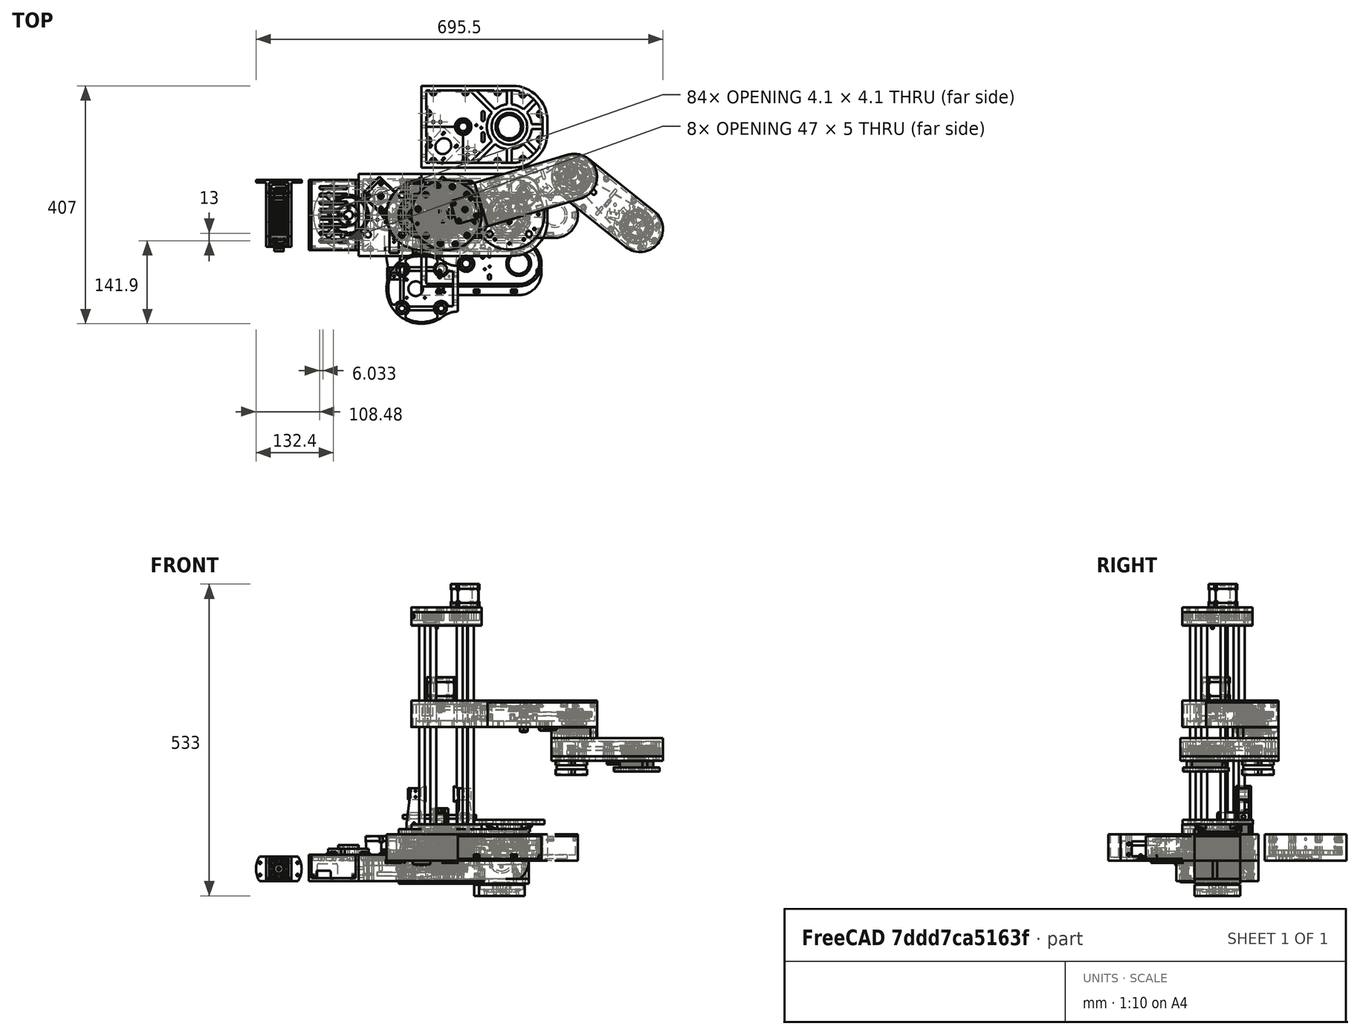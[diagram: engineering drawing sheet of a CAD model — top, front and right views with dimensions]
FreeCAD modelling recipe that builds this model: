
FCSTD DOCUMENT  (FreeCAD 0.20R28717 (Git))
Label: SCARARobot
License: All rights reserved
LicenseURL: http://en.wikipedia.org/wiki/All_rights_reserved
objects: Part::Feature×123, Sketcher::SketchObject×110, PartDesign::Pocket×76, PartDesign::Pad×44, Part::Part2DObjectPython×22, PartDesign::Body×22, Part::FeaturePython×17, App::Part×16, PartDesign::PolarPattern×9, Spreadsheet::Sheet×8, PartDesign::LinearPattern×6, TechDraw::DrawViewDimension×6, PartDesign::FeatureBase×5, Part::Mirroring×5, PartDesign::Hole×5, PartDesign::Chamfer×4, PartDesign::FeaturePython×3, Part::Cylinder×2, Part::Box×2, PartDesign::Line×2, +10 more types
note: 601 computed .brp shape members not serialized (recipe doc carries the construction recipe); baked Part::Feature solids carry a one-line shape summary decoded from their .brp

FEATURE [Part::Feature] Part__Feature059  label="Servo Motor MG996R 3D Model_Servo Motor MG996R 3D Model"
  Placement = pos=(-0.337733,-44.2936,-36.6383) rot=(0.57735,-0.57735,-0.57735;2.0944rad)
  shape: bbox 22.19 x 55.8 x 45.2 mm, 123 faces, 4 solids (baked)
FEATURE [Spreadsheet::Sheet] Spreadsheet  label="gripperdims"
  cells = A1=MG996R; B2=height; C2(mg996r_height)==40.3mm; E2=slide thickness; F2(mg996r_slide_thickness)==1.5mm; B3=width; C3(mg996r_width)==20mm; E3=slide length; F3(mg996r_slide_length)==6mm; B4=hole distance; C4(mg996r_holedistance)==3.5mm; E4=slide depth; F4(mg996r_slide_depth)==1.5mm; B5=hole separation; C5(mg996r_holeseparation)==10mm; B6=hole diameter; C6(mg996r_holediameter)==3.2mm; B7=extra depth; C7(mg996r_extra_depth)==3mm; B8=center height; C8(mg996r_center_height)==1.5mm; B9=center length; C9(mg996r_center_length)==7mm; B10=center thickness; C10(mg996r_center_thickness)==1.5mm; A11=Servo Holder; B12=moving hole; C12(servo_holder_moving_hole_diameter)==3.4mm; B13=width; C13(servo_holder_width)==30mm; B14=height; C14(servo_holder_height)==72.5mm; B15=top skirt; C15(servo_holder_top_skirt)==24.75mm; B16=bottom skirt; C16(servo_holder_bottom_skirt)==20mm; B17=thickness; C17(servo_holder_thickness)==6mm; B18=rod diameter; C18(servo_holder_roddiameter)==6mm; B19=rod casing; C19(servo_holder_rodcasing)==17.5mm; B20=rod casing layer; C20(servo_holder_rodcasing_layer)==5mm; B21=rod casing cutin; C21(servo_holder_rodcasing_cutin)==9mm; B22=rod casing overhang; C22(servo_holder_rodcasing_overhang)==2.5mm; B23=hole top distance; C23(servo_holder_hole_top_distance)==4.7mm; B24=hole side distance; C24(servo_holder_hole_side_distance)==5.5mm; B25=axis distance; C25(servo_holder_axis_distance)==46mm; B26=axis top offset; C26(servo_holder_axis_top_offset)==12mm; B27=side wings; C27(servo_holder_side_wings)==7mm; B28=side wing thickness; C28(servo_holder_side_wing_thickness)==4.5mm; A29=Servo cover; B29=cover thickness; C29(cover_thickness)==2.5mm; B30=cover height; C30(cover_height)==12.5mm; A31=Rod; B31=length; C31(rod_length)==125mm; A32=Slider; B32=height; C32(slider_height)==18mm; B33=width; C33(slider_width)==16mm; B34=length; C34(slider_length)==60mm; B35=handholes distance; C35(slider_handholes_distance)==22mm; B36=slider margin; C36(slider_margin)==0.4mm; B37=connector length; C37(slider_connector_length)==14mm; B38=connector thickness; C38(slider_connector_thickness)==4mm; B39=connector depth; C39(slider_connector_depth)==10mm; B40=connector foot; C40(slider_connector_foot)==9mm; B41=connector foot thickness; C41(slider_connector_foot_thickness)==3.5mm; A42=Hand; B42=height; C42(hand_height)==105mm; B43=thickness; C43(hand_thickness)==4mm; B44=overhang; C44(hand_overhang)==5mm; A45=Gripper; B45=hole distance; C45(gripper_hole_distance)==10mm; B46=height; C46(gripper_height)==20mm; A47=Link; B47=width; C47(link_width)==7.2mm; B48=length; C48(link_length)==27mm; B49=height; C49(link_height)==3.5mm; A50=Horn; B50=screw head diameter; C50(horn_screw_head_diameter)==6mm; B51=screw inlay depth; C51(horn_screw_inlay_depth)==1mm; A52=Sliderbody; B52=width; C52(sliderbody_width)==20mm; B53=depth; C53(sliderbody_depth)==22mm; B54=hole sidedistance; C54(sliderbody_hole_sidedistance)==10mm; B55=alternate hole distance; C55(sliderbody_alternate_hole_distance)==8mm; B56=hammer thickness; C56(sliderbody_hammer_thickness)==7.5mm; B57=hammer fanout; C57(sliderbody_hammer_fanout)==3.5mm; B58=hammer plate; C58(sliderbody_hammer_plate)==1mm; A59=Coupler; B59=Outer angle; C59(coupler_outerangle)==60deg; B60=Straight part; C60(coupler_straight_part)==16mm; B61=thickness; C61(coupler_thickness)==4.5mm
FEATURE [Sketcher::SketchObject] Sketch
  FullyConstrained = true
  MapMode = 5
  Support = -> [XY_Plane001]
  expr: Constraints[18] = <<gripperdims>>.mg996r_width
  expr: Constraints[20] = <<gripperdims>>.mg996r_height
  expr: Constraints[21] = <<gripperdims>>.servo_holder_top_skirt
  expr: Constraints[24] = <<gripperdims>>.mg996r_holedistance
  expr: Constraints[25] = <<gripperdims>>.mg996r_holeseparation
  expr: Constraints[29] = <<gripperdims>>.mg996r_holeseparation
  expr: Constraints[30] = <<gripperdims>>.mg996r_holedistance
  expr: Constraints[31] = <<gripperdims>>.mg996r_holediameter
  expr: Constraints[7] = <<gripperdims>>.servo_holder_height
  expr: Constraints[8] = <<gripperdims>>.servo_holder_width
  sketch-geometry (12):
    g0: LineSegment StartX=-15 StartY=0 StartZ=0 EndX=15 EndY=0 EndZ=0
    g1: LineSegment StartX=15 StartY=0 StartZ=0 EndX=15 EndY=-72.5 EndZ=0
    g2: LineSegment StartX=15 StartY=-72.5 StartZ=0 EndX=-15 EndY=-72.5 EndZ=0
    g3: LineSegment StartX=-15 StartY=-72.5 StartZ=0 EndX=-15 EndY=0 EndZ=0
    g4: LineSegment StartX=-10 StartY=-24.75 StartZ=0 EndX=10 EndY=-24.75 EndZ=0
    g5: LineSegment StartX=10 StartY=-24.75 StartZ=0 EndX=10 EndY=-65.05 EndZ=0
    g6: LineSegment StartX=10 StartY=-65.05 StartZ=0 EndX=-10 EndY=-65.05 EndZ=0
    g7: LineSegment StartX=-10 StartY=-65.05 StartZ=0 EndX=-10 EndY=-24.75 EndZ=0
    g8: Circle CenterX=-5 CenterY=-21.25 CenterZ=0 NormalX=0 NormalY=0 NormalZ=1 AngleXU=0 Radius=1.6
    g9: Circle CenterX=5 CenterY=-21.25 CenterZ=0 NormalX=0 NormalY=0 NormalZ=1 AngleXU=0 Radius=1.6
    g10: Circle CenterX=-5 CenterY=-68.55 CenterZ=0 NormalX=0 NormalY=0 NormalZ=1 AngleXU=0 Radius=1.6
    g11: Circle CenterX=5 CenterY=-68.55 CenterZ=0 NormalX=0 NormalY=0 NormalZ=1 AngleXU=0 Radius=1.6
  constraints (32):
    c: Coincident(g0,g1)
    c: Coincident(g1,g2)
    c: Coincident(g2,g3)
    c: Coincident(g3,g0)
    c: Horizontal(g2)
    c: Vertical(g1)
    c: Vertical(g3)
    c: DistanceY(g1,g1) = 72.5
    c: DistanceX(g0,g0) = 30
    c: Horizontal(g0,g-1)
    c: Symmetric(g0,g0,g-2)
    c: Coincident(g4,g5)
    c: Coincident(g5,g6)
    c: Coincident(g6,g7)
    c: Coincident(g7,g4)
    c: Horizontal(g6)
    c: Vertical(g5)
    c: Vertical(g7)
    c: DistanceX(g4,g4) = 20
    c: Symmetric(g4,g4,g-2)
    c: DistanceY(g7,g7) = 40.3
    c: DistanceY(g4,g0) = 24.75
    c: Equal(g8,g9)
    c: Symmetric(g8,g9,g-2)
    c: DistanceY(g4,g8) = 3.5
    c: DistanceX(g8,g9) = 10
    c: Equal(g10,g11)
    c: Equal(g11,g9)
    c: Symmetric(g10,g11,g-2)
    c: DistanceX(g10,g11) = 10
    c: DistanceY(g10,g6) = 3.5
    c: Diameter(g8) = 3.2
FEATURE [PartDesign::Pad] Pad
  Direction = (0,0,1)
  Length = 6
  Length2 = 100
  Profile = -> Sketch
  Reversed = true
  Type = 0
  expr: Length = <<gripperdims>>.servo_holder_thickness
FEATURE [Sketcher::SketchObject] Sketch001
  FullyConstrained = true
  MapMode = 5
  Support = -> [Pad]
  expr: Constraints[15] = <<gripperdims>>.servo_holder_rodcasing
  expr: Constraints[16] = <<gripperdims>>.servo_holder_width
  expr: Constraints[21] = <<gripperdims>>.servo_holder_height
  expr: Constraints[22] = <<gripperdims>>.servo_holder_bottom_skirt
  sketch-geometry (8):
    g0: LineSegment StartX=-15 StartY=0 StartZ=0 EndX=15 EndY=0 EndZ=0
    g1: LineSegment StartX=15 StartY=0 StartZ=0 EndX=15 EndY=-17.5 EndZ=0
    g2: LineSegment StartX=15 StartY=-17.5 StartZ=0 EndX=-15 EndY=-17.5 EndZ=0
    g3: LineSegment StartX=-15 StartY=-17.5 StartZ=0 EndX=-15 EndY=0 EndZ=0
    g4: LineSegment StartX=-15 StartY=-52.5 StartZ=0 EndX=15 EndY=-52.5 EndZ=0
    g5: LineSegment StartX=15 StartY=-52.5 StartZ=0 EndX=15 EndY=-72.5 EndZ=0
    g6: LineSegment StartX=15 StartY=-72.5 StartZ=0 EndX=-15 EndY=-72.5 EndZ=0
    g7: LineSegment StartX=-15 StartY=-72.5 StartZ=0 EndX=-15 EndY=-52.5 EndZ=0
  constraints (23):
    c: Coincident(g0,g1)
    c: Coincident(g1,g2)
    c: Coincident(g2,g3)
    c: Coincident(g3,g0)
    c: Horizontal(g2)
    c: Vertical(g1)
    c: Vertical(g3)
    c: Coincident(g4,g5)
    c: Coincident(g5,g6)
    c: Coincident(g6,g7)
    c: Coincident(g7,g4)
    c: Horizontal(g4)
    c: Horizontal(g6)
    c: Vertical(g5)
    c: Vertical(g7)
    c: DistanceY(g1,g1) = 17.5
    c: DistanceX(g0,g0) = 30
    c: Symmetric(g0,g0,g-2)
    c: Horizontal(g0,g-1)
    c: Vertical(g4,g2)
    c: Vertical(g4,g1)
    c: DistanceY(g6,g0) = 72.5
    c: DistanceY(g5,g5) = 20
FEATURE [PartDesign::Pad] Pad001
  BaseFeature = -> Pad
  Direction = (0,0,1)
  Length = 10
  Length2 = 100
  Profile = -> Sketch001
  Type = 0
  expr: Length = <<gripperdims>>.servo_holder_rodcasing_layer * 2
FEATURE [Sketcher::SketchObject] Sketch002
  FullyConstrained = true
  MapMode = 5
  Placement = pos=(15,0,0) rot=(0.57735,0.57735,0.57735;2.0944rad)
  Support = -> [Pad001]
  expr: Constraints[16] = <<gripperdims>>.servo_holder_rodcasing_overhang
  expr: Constraints[17] = <<gripperdims>>.servo_holder_rodcasing_layer
  expr: Constraints[5] = <<gripperdims>>.servo_holder_rodcasing_cutin
  expr: Constraints[6] = <<gripperdims>>.servo_holder_height
  expr: Constraints[7] = <<gripperdims>>.servo_holder_rodcasing_layer * 2
  sketch-geometry (6):
    g0: LineSegment StartX=-63.5 StartY=5 StartZ=0 EndX=-63.5 EndY=0 EndZ=0
    g1: LineSegment StartX=-63.5 StartY=0 StartZ=0 EndX=-72.5 EndY=0 EndZ=0
    g2: LineSegment StartX=-72.5 StartY=0 StartZ=0 EndX=-72.5 EndY=10 EndZ=0
    g3: LineSegment StartX=-72.5 StartY=10 StartZ=0 EndX=-70 EndY=10 EndZ=0
    g4: LineSegment StartX=-70 StartY=10 StartZ=0 EndX=-70 EndY=5 EndZ=0
    g5: LineSegment StartX=-70 StartY=5 StartZ=0 EndX=-63.5 EndY=5 EndZ=0
  constraints (18):
    c: Coincident(g0,g1)
    c: Coincident(g1,g2)
    c: Horizontal(g1)
    c: Vertical(g0)
    c: Vertical(g2)
    c: DistanceX(g2,g0) = 9
    c: DistanceX(g1,g-1) = 72.5
    c: DistanceY(g2,g2) = 10
    c: Horizontal(g0,g-1)
    c: Coincident(g2,g3)
    c: Horizontal(g3)
    c: Coincident(g3,g4)
    c: Vertical(g4)
    c: Coincident(g4,g5)
    c: Coincident(g5,g0)
    c: Horizontal(g5)
    c: DistanceX(g3,g3) = 2.5
    c: DistanceY(g0,g0) = 5
FEATURE [PartDesign::Pocket] Pocket
  BaseFeature = -> Pad001
  Direction = (-1,0,0)
  Length = 5
  Length2 = 100
  Profile = -> Sketch002
  Type = 2
FEATURE [Sketcher::SketchObject] Sketch003
  FullyConstrained = true
  MapMode = 5
  Placement = pos=(0,0,10) rot=(0,0,1;0rad)
  Support = -> [Pocket]
  expr: Constraints[1] = <<gripperdims>>.servo_holder_width / 2 - <<gripperdims>>.servo_holder_hole_side_distance
  expr: Constraints[3] = <<gripperdims>>.servo_holder_hole_top_distance
  expr: Constraints[4] = <<gripperdims>>.mg996r_holediameter
  sketch-geometry (2):
    g0: Circle CenterX=-9.5 CenterY=-4.7 CenterZ=0 NormalX=0 NormalY=0 NormalZ=1 AngleXU=0 Radius=1.6
    g1: Circle CenterX=9.5 CenterY=-4.7 CenterZ=0 NormalX=0 NormalY=0 NormalZ=1 AngleXU=0 Radius=1.6
  constraints (5):
    c: Equal(g0,g1)
    c: DistanceX(g0,g-1) = 9.5
    c: Symmetric(g0,g1,g-2)
    c: DistanceY(g0,g-1) = 4.7
    c: Diameter(g0) = 3.2
FEATURE [Sketcher::SketchObject] Sketch004
  FullyConstrained = true
  MapMode = 5
  Placement = pos=(0,0,10) rot=(0,0,1;0rad)
  Support = -> [Pocket]
  expr: Constraints[1] = <<gripperdims>>.servo_holder_height - <<gripperdims>>.servo_holder_hole_top_distance - <<gripperdims>>.servo_holder_rodcasing_overhang
  expr: Constraints[2] = <<gripperdims>>.servo_holder_width / 2 - <<gripperdims>>.servo_holder_hole_side_distance
  expr: Constraints[4] = <<gripperdims>>.mg996r_holediameter
  sketch-geometry (2):
    g0: Circle CenterX=9.5 CenterY=-65.3 CenterZ=0 NormalX=0 NormalY=0 NormalZ=1 AngleXU=0 Radius=1.6
    g1: Circle CenterX=-9.5 CenterY=-65.3 CenterZ=0 NormalX=0 NormalY=0 NormalZ=1 AngleXU=0 Radius=1.6
  constraints (5):
    c: Equal(g0,g1)
    c: DistanceY(g1,g-1) = 65.3
    c: DistanceX(g1,g-1) = 9.5
    c: Symmetric(g1,g0,g-2)
    c: Diameter(g1) = 3.2
FEATURE [PartDesign::Pocket] Pocket001
  BaseFeature = -> Pocket
  Direction = (0,0,-1)
  Length = 5
  Length2 = 100
  Profile = -> Sketch003
  Type = 1
FEATURE [PartDesign::Pocket] Pocket002
  BaseFeature = -> Pocket001
  Direction = (0,0,-1)
  Length = 5
  Length2 = 100
  Profile = -> Sketch004
  Type = 2
FEATURE [Sketcher::SketchObject] Sketch005
  FullyConstrained = true
  MapMode = 5
  Placement = pos=(0,0,0) rot=(1,0,0;3.14159rad)
  Support = -> [Pocket002]
  expr: Constraints[10] = <<gripperdims>>.mg996r_width
  expr: Constraints[7] = <<gripperdims>>.servo_holder_top_skirt
  expr: Constraints[8] = <<gripperdims>>.mg996r_height
  sketch-geometry (4):
    g0: LineSegment StartX=-10 StartY=65.05 StartZ=0 EndX=10 EndY=65.05 EndZ=0
    g1: LineSegment StartX=10 StartY=65.05 StartZ=0 EndX=10 EndY=24.75 EndZ=0
    g2: LineSegment StartX=10 StartY=24.75 StartZ=0 EndX=-10 EndY=24.75 EndZ=0
    g3: LineSegment StartX=-10 StartY=24.75 StartZ=0 EndX=-10 EndY=65.05 EndZ=0
  constraints (11):
    c: Coincident(g0,g1)
    c: Coincident(g1,g2)
    c: Coincident(g2,g3)
    c: Coincident(g3,g0)
    c: Horizontal(g0)
    c: Vertical(g1)
    c: Vertical(g3)
    c: DistanceY(g-1,g1) = 24.75
    c: DistanceY(g1,g1) = 40.3
    c: Symmetric(g1,g2,g-2)
    c: DistanceX(g2,g2) = 20
FEATURE [PartDesign::Pocket] Pocket003
  BaseFeature = -> Pocket002
  Direction = (0,0,1)
  Length = 3
  Length2 = 100
  Profile = -> Sketch005
  Type = 0
  expr: Length = <<gripperdims>>.mg996r_extra_depth
FEATURE [Sketcher::SketchObject] Sketch006
  FullyConstrained = true
  MapMode = 5
  Placement = pos=(15,0,0) rot=(0.57735,0.57735,0.57735;2.0944rad)
  Support = -> [Pocket003]
  expr: Constraints[0] = <<gripperdims>>.servo_holder_roddiameter
  expr: Constraints[3] = <<gripperdims>>.servo_holder_rodcasing_cutin
  expr: Constraints[4] = <<gripperdims>>.servo_holder_axis_distance
  expr: Constraints[5] = <<gripperdims>>.servo_holder_axis_top_offset
  sketch-geometry (2):
    g0: Circle CenterX=-58 CenterY=9 CenterZ=0 NormalX=0 NormalY=0 NormalZ=1 AngleXU=0 Radius=3
    g1: Circle CenterX=-12 CenterY=9 CenterZ=0 NormalX=0 NormalY=0 NormalZ=1 AngleXU=0 Radius=3
  constraints (6):
    c: Diameter(g1) = 6
    c: Equal(g0,g1)
    c: Horizontal(g0,g1)
    c: DistanceY(g-1,g1) = 9
    c: DistanceX(g0,g1) = 46
    c: DistanceX(g1,g-1) = 12
FEATURE [PartDesign::Pocket] Pocket004
  BaseFeature = -> Pocket003
  Direction = (-1,0,0)
  Length = 5
  Length2 = 100
  Profile = -> Sketch006
  Type = 1
FEATURE [Sketcher::SketchObject] Sketch007
  FullyConstrained = true
  MapMode = 5
  Placement = pos=(0,0,0) rot=(0,0.707107,0.707107;3.14159rad)
  Support = -> [Pocket004]
  expr: Constraints[16] = <<gripperdims>>.servo_holder_side_wings
  expr: Constraints[20] = <<gripperdims>>.servo_holder_width / 2
  expr: Constraints[22] = <<gripperdims>>.servo_holder_rodcasing_layer * 2
  expr: Constraints[23] = <<gripperdims>>.mg996r_holediameter
  expr: Constraints[25] = <<gripperdims>>.servo_holder_side_wings / 2
  expr: Constraints[27] = <<gripperdims>>.servo_holder_side_wings / 2
  sketch-geometry (10):
    g0: LineSegment StartX=15 StartY=10 StartZ=0 EndX=22 EndY=10 EndZ=0
    g1: LineSegment StartX=22 StartY=10 StartZ=0 EndX=22 EndY=3 EndZ=0
    g2: LineSegment StartX=22 StartY=3 StartZ=0 EndX=15 EndY=3 EndZ=0
    g3: LineSegment StartX=15 StartY=3 StartZ=0 EndX=15 EndY=10 EndZ=0
    g4: LineSegment StartX=-15 StartY=10 StartZ=0 EndX=-22 EndY=10 EndZ=0
    g5: LineSegment StartX=-22 StartY=10 StartZ=0 EndX=-22 EndY=3 EndZ=0
    g6: LineSegment StartX=-22 StartY=3 StartZ=0 EndX=-15 EndY=3 EndZ=0
    g7: LineSegment StartX=-15 StartY=3 StartZ=0 EndX=-15 EndY=10 EndZ=0
    g8: Circle CenterX=18.5 CenterY=6.5 CenterZ=0 NormalX=0 NormalY=0 NormalZ=1 AngleXU=0 Radius=1.6
    g9: Circle CenterX=-18.5 CenterY=6.5 CenterZ=0 NormalX=0 NormalY=0 NormalZ=1 AngleXU=0 Radius=1.6
  constraints (28):
    c: Coincident(g0,g1)
    c: Coincident(g1,g2)
    c: Coincident(g2,g3)
    c: Coincident(g3,g0)
    c: Horizontal(g0)
    c: Horizontal(g2)
    c: Vertical(g1)
    c: Vertical(g3)
    c: Coincident(g4,g5)
    c: Coincident(g5,g6)
    c: Coincident(g6,g7)
    c: Coincident(g7,g4)
    c: Horizontal(g4)
    c: Horizontal(g6)
    c: Vertical(g5)
    c: Vertical(g7)
    c: DistanceX(g0,g0) = 7
    c: Equal(g0,g1)
    c: Equal(g1,g4)
    c: Equal(g4,g5)
    c: DistanceX(g-1,g0) = 15
    c: Symmetric(g0,g4,g-2)
    c: DistanceY(g-1,g0) = 10
    c: Diameter(g8) = 3.2
    c: Equal(g9,g8)
    c: DistanceX(g2,g8) = 3.5
    c: Symmetric(g8,g9,g-2)
    c: DistanceY(g2,g8) = 3.5
FEATURE [PartDesign::Pad] Pad002
  BaseFeature = -> Pocket004
  Direction = (0,1,-2e-16)
  Length = 4.5
  Length2 = 10
  Profile = -> Sketch007
  ReferenceAxis = -> Sketch007 [N_Axis]
  Reversed = true
  Type = 0
  expr: Length = <<gripperdims>>.servo_holder_side_wing_thickness
FEATURE [Sketcher::SketchObject] Sketch008
  FullyConstrained = true
  MapMode = 5
  Support = -> [XY_Plane002]
  expr: Constraints[8] = <<gripperdims>>.servo_holder_width
  expr: Constraints[9] = <<gripperdims>>.servo_holder_height - <<gripperdims>>.servo_holder_rodcasing_overhang
  sketch-geometry (4):
    g0: LineSegment StartX=-15 StartY=0 StartZ=0 EndX=15 EndY=0 EndZ=0
    g1: LineSegment StartX=15 StartY=0 StartZ=0 EndX=15 EndY=-70 EndZ=0
    g2: LineSegment StartX=15 StartY=-70 StartZ=0 EndX=-15 EndY=-70 EndZ=0
    g3: LineSegment StartX=-15 StartY=-70 StartZ=0 EndX=-15 EndY=0 EndZ=0
  constraints (11):
    c: Coincident(g0,g1)
    c: Coincident(g1,g2)
    c: Coincident(g2,g3)
    c: Coincident(g3,g0)
    c: Horizontal(g0)
    c: Horizontal(g2)
    c: Vertical(g1)
    c: Vertical(g3)
    c: DistanceX(g0,g0) = 30
    c: DistanceY(g1,g1) = 70
    c: Symmetric(g0,g0,g-1)
FEATURE [PartDesign::Pad] Pad003
  Direction = (0,0,1)
  Length = 12.5
  Length2 = 10
  Profile = -> Sketch008
  ReferenceAxis = -> Sketch008 [N_Axis]
  Reversed = true
  Type = 0
  expr: Length = <<gripperdims>>.cover_height
FEATURE [Sketcher::SketchObject] Sketch009
  FullyConstrained = true
  MapMode = 5
  Placement = pos=(15,0,0) rot=(0.57735,0.57735,0.57735;2.0944rad)
  Support = -> [Pad003]
  expr: Constraints[10] = <<gripperdims>>.servo_holder_height - <<gripperdims>>.servo_holder_bottom_skirt
  expr: Constraints[11] = <<gripperdims>>.cover_height - <<gripperdims>>.cover_thickness
  expr: Constraints[8] = <<gripperdims>>.cover_thickness
  expr: Constraints[9] = <<gripperdims>>.servo_holder_rodcasing
  sketch-geometry (4):
    g0: LineSegment StartX=-52.5 StartY=-2.5 StartZ=0 EndX=-17.5 EndY=-2.5 EndZ=0
    g1: LineSegment StartX=-17.5 StartY=-2.5 StartZ=0 EndX=-17.5 EndY=-12.5 EndZ=0
    g2: LineSegment StartX=-17.5 StartY=-12.5 StartZ=0 EndX=-52.5 EndY=-12.5 EndZ=0
    g3: LineSegment StartX=-52.5 StartY=-12.5 StartZ=0 EndX=-52.5 EndY=-2.5 EndZ=0
  constraints (12):
    c: Coincident(g0,g1)
    c: Coincident(g1,g2)
    c: Coincident(g2,g3)
    c: Coincident(g3,g0)
    c: Horizontal(g0)
    c: Horizontal(g2)
    c: Vertical(g1)
    c: Vertical(g3)
    c: DistanceY(g0,g-1) = 2.5
    c: DistanceX(g0,g-1) = 17.5
    c: DistanceX(g0,g-1) = 52.5
    c: DistanceY(g1,g1) = 10
FEATURE [PartDesign::Pocket] Pocket005
  BaseFeature = -> Pad003
  Direction = (-1,0,0)
  Length = 5
  Length2 = 5
  Profile = -> Sketch009
  ReferenceAxis = -> Sketch009 [N_Axis]
  Type = 2
FEATURE [Sketcher::SketchObject] Sketch010
  FullyConstrained = true
  MapMode = 5
  Support = -> [Pocket005]
  expr: Constraints[6] = <<gripperdims>>.servo_holder_height - <<gripperdims>>.servo_holder_hole_top_distance - <<gripperdims>>.servo_holder_rodcasing_overhang
  expr: Constraints[7] = <<gripperdims>>.servo_holder_hole_top_distance
  expr: Constraints[8] = <<gripperdims>>.servo_holder_width / 2 - <<gripperdims>>.servo_holder_hole_side_distance
  expr: Constraints[9] = <<gripperdims>>.mg996r_holediameter
  sketch-geometry (4):
    g0: Circle CenterX=9.5 CenterY=-4.7 CenterZ=0 NormalX=0 NormalY=0 NormalZ=1 AngleXU=0 Radius=1.6
    g1: Circle CenterX=-9.5 CenterY=-4.7 CenterZ=0 NormalX=0 NormalY=0 NormalZ=1 AngleXU=0 Radius=1.6
    g2: Circle CenterX=9.5 CenterY=-65.3 CenterZ=0 NormalX=0 NormalY=0 NormalZ=1 AngleXU=0 Radius=1.6
    g3: Circle CenterX=-9.5 CenterY=-65.3 CenterZ=0 NormalX=0 NormalY=0 NormalZ=1 AngleXU=0 Radius=1.6
  constraints (10):
    c: Equal(g0,g1)
    c: Equal(g1,g2)
    c: Equal(g2,g3)
    c: Symmetric(g0,g1,g-2)
    c: Symmetric(g3,g2,g-2)
    c: Vertical(g3,g1)
    c: DistanceY(g3,g-1) = 65.3
    c: DistanceY(g1,g-1) = 4.7
    c: DistanceX(g1,g-1) = 9.5
    c: Diameter(g1) = 3.2
FEATURE [PartDesign::Pocket] Pocket006
  BaseFeature = -> Pocket005
  Direction = (0,0,-1)
  Length = 5
  Length2 = 5
  Profile = -> Sketch010
  ReferenceAxis = -> Sketch010 [N_Axis]
  Type = 1
FEATURE [Sketcher::SketchObject] Sketch011
  FullyConstrained = true
  MapMode = 5
  Placement = pos=(0,0,0) rot=(0,0.707107,0.707107;3.14159rad)
  Support = -> [Pocket006]
  expr: Constraints[19] = <<gripperdims>>.servo_holder_side_wings
  expr: Constraints[21] = <<gripperdims>>.cover_height
  expr: Constraints[22] = <<gripperdims>>.servo_holder_width
  expr: Constraints[24] = <<gripperdims>>.mg996r_holediameter
  sketch-geometry (10):
    g0: LineSegment StartX=15 StartY=-5.5 StartZ=0 EndX=22 EndY=-5.5 EndZ=0
    g1: LineSegment StartX=22 StartY=-5.5 StartZ=0 EndX=22 EndY=-12.5 EndZ=0
    g2: LineSegment StartX=22 StartY=-12.5 StartZ=0 EndX=15 EndY=-12.5 EndZ=0
    g3: LineSegment StartX=15 StartY=-12.5 StartZ=0 EndX=15 EndY=-5.5 EndZ=0
    g4: LineSegment StartX=-22 StartY=-5.5 StartZ=0 EndX=-15 EndY=-5.5 EndZ=0
    g5: LineSegment StartX=-15 StartY=-5.5 StartZ=0 EndX=-15 EndY=-12.5 EndZ=0
    g6: LineSegment StartX=-15 StartY=-12.5 StartZ=0 EndX=-22 EndY=-12.5 EndZ=0
    g7: LineSegment StartX=-22 StartY=-12.5 StartZ=0 EndX=-22 EndY=-5.5 EndZ=0
    g8: Circle CenterX=-18.5 CenterY=-9 CenterZ=0 NormalX=0 NormalY=0 NormalZ=1 AngleXU=0 Radius=1.6
    g9: Circle CenterX=18.5 CenterY=-9 CenterZ=0 NormalX=0 NormalY=0 NormalZ=1 AngleXU=0 Radius=1.6
  constraints (27):
    c: Coincident(g0,g1)
    c: Coincident(g1,g2)
    c: Coincident(g2,g3)
    c: Coincident(g3,g0)
    c: Horizontal(g0)
    c: Horizontal(g2)
    c: Vertical(g1)
    c: Vertical(g3)
    c: Coincident(g4,g5)
    c: Coincident(g5,g6)
    c: Coincident(g6,g7)
    c: Coincident(g7,g4)
    c: Horizontal(g4)
    c: Horizontal(g6)
    c: Vertical(g5)
    c: Vertical(g7)
    c: Equal(g6,g5)
    c: Equal(g5,g3)
    c: Equal(g3,g2)
    c: DistanceY(g7,g7) = 7
    c: Symmetric(g5,g2,g-2)
    c: DistanceY(g5,g-1) = 12.5
    c: DistanceX(g4,g0) = 30
    c: Equal(g8,g9)
    c: Diameter(g9) = 3.2
    c: Symmetric(g6,g4,g8)
    c: Symmetric(g8,g9,g-2)
FEATURE [PartDesign::Pad] Pad004
  BaseFeature = -> Pocket006
  Direction = (0,1,-2e-16)
  Length = 4.5
  Length2 = 10
  Profile = -> Sketch011
  ReferenceAxis = -> Sketch011 [N_Axis]
  Reversed = true
  Type = 0
  expr: Length = <<gripperdims>>.servo_holder_side_wing_thickness
FEATURE [Sketcher::SketchObject] Sketch012
  FullyConstrained = true
  MapMode = 5
  Placement = pos=(-15,0,0) rot=(0.57735,-0.57735,-0.57735;2.0944rad)
  Support = -> [Pad004]
  expr: Constraints[1] = <<gripperdims>>.servo_holder_roddiameter
  expr: Constraints[2] = <<gripperdims>>.cover_height + 2 * <<gripperdims>>.servo_holder_rodcasing_layer - <<gripperdims>>.servo_holder_rodcasing_cutin
  expr: Constraints[3] = <<gripperdims>>.servo_holder_axis_top_offset
  expr: Constraints[4] = <<gripperdims>>.servo_holder_axis_distance
  sketch-geometry (2):
    g0: Circle CenterX=12 CenterY=-13.5 CenterZ=0 NormalX=0 NormalY=0 NormalZ=1 AngleXU=0 Radius=3
    g1: Circle CenterX=58 CenterY=-13.5 CenterZ=0 NormalX=0 NormalY=0 NormalZ=1 AngleXU=0 Radius=3
  constraints (6):
    c: Equal(g0,g1)
    c: Diameter(g0) = 6
    c: DistanceY(g0,g-1) = 13.5
    c: DistanceX(g-1,g0) = 12
    c: DistanceX(g0,g1) = 46
    c: Horizontal(g0,g1)
FEATURE [PartDesign::Pocket] Pocket007
  BaseFeature = -> Pad004
  Direction = (1,0,0)
  Length = 5
  Length2 = 5
  Profile = -> Sketch012
  ReferenceAxis = -> Sketch012 [N_Axis]
  Type = 1
FEATURE [Part::Cylinder] Cylinder  label="back gripper rail"
  Angle = 360
  AttacherType = Attacher::AttachEngine3D
  FirstAngle = 0
  Height = 125
  Placement = pos=(-62.5,-12,9) rot=(0,1,0;1.5708rad)
  Radius = 3
  SecondAngle = 0
  expr: .Placement.Base.x = -<<gripperdims>>.rod_length / 2
  expr: .Placement.Base.y = -<<gripperdims>>.servo_holder_axis_top_offset
  expr: .Placement.Base.z = <<gripperdims>>.servo_holder_rodcasing_cutin
  expr: Height = <<gripperdims>>.rod_length
  expr: Radius = <<gripperdims>>.servo_holder_roddiameter / 2
FEATURE [Part::Cylinder] Cylinder001  label="front gripper rail"
  Angle = 360
  AttacherType = Attacher::AttachEngine3D
  FirstAngle = 0
  Height = 125
  Placement = pos=(-62.5,-58,9) rot=(0,1,0;1.5708rad)
  Radius = 3
  SecondAngle = 0
  expr: .Placement.Base.x = -<<gripperdims>>.rod_length / 2
  expr: .Placement.Base.y = -<<gripperdims>>.servo_holder_axis_top_offset - <<gripperdims>>.servo_holder_axis_distance
  expr: .Placement.Base.z = <<gripperdims>>.servo_holder_rodcasing_cutin
  expr: Height = <<gripperdims>>.rod_length
  expr: Radius = <<gripperdims>>.servo_holder_roddiameter / 2
FEATURE [Part::Box] Box  label="Cube"
  AttacherType = Attacher::AttachEngine3D
  Height = 18
  Length = 16
  Placement = pos=(39,-65,0) rot=(0,0,1;0rad)
  Width = 60
  expr: .Placement.Base.y = -<<gripperdims>>.slider_length / 2 - <<gripperdims>>.servo_holder_axis_top_offset - <<gripperdims>>.servo_holder_axis_distance / 2
  expr: .Placement.Base.z = <<gripperdims>>.servo_holder_rodcasing_cutin - <<gripperdims>>.slider_height / 2
  expr: Height = <<gripperdims>>.slider_height
  expr: Length = <<gripperdims>>.slider_width
  expr: Width = <<gripperdims>>.slider_length
FEATURE [PartDesign::FeatureBase] BaseFeature
  BaseFeature = -> Box
FEATURE [Sketcher::SketchObject] Sketch013
  FullyConstrained = true
  MapMode = 5
  Placement = pos=(0,0,18) rot=(0,0,1;0rad)
  Support = -> [BaseFeature]
  expr: Constraints[1] = <<gripperdims>>.mg996r_holediameter
  expr: Constraints[3] = <<gripperdims>>.slider_handholes_distance
  expr: Constraints[4] = <<gripperdims>>.slider_width / 2
  expr: Constraints[5] = <<gripperdims>>.slider_length / 2 - <<gripperdims>>.slider_handholes_distance / 2
  sketch-geometry (2):
    g0: Circle CenterX=8 CenterY=41 CenterZ=0 NormalX=0 NormalY=0 NormalZ=1 AngleXU=0 Radius=1.6
    g1: Circle CenterX=8 CenterY=19 CenterZ=0 NormalX=0 NormalY=0 NormalZ=1 AngleXU=0 Radius=1.6
  constraints (6):
    c: Equal(g1,g0)
    c: Diameter(g1) = 3.2
    c: Vertical(g1,g0)
    c: DistanceY(g1,g0) = 22
    c: DistanceX(g-1,g1) = 8
    c: DistanceY(g-1,g1) = 19
FEATURE [PartDesign::Pocket] Pocket008
  BaseFeature = -> BaseFeature
  Direction = (0,0,-1)
  Length = 5
  Length2 = 5
  Profile = -> Sketch013
  ReferenceAxis = -> Sketch013 [N_Axis]
  Type = 1
FEATURE [Sketcher::SketchObject] Sketch014
  FullyConstrained = true
  MapMode = 5
  Placement = pos=(16,0,0) rot=(0.57735,0.57735,0.57735;2.0944rad)
  Support = -> [Pocket008]
  expr: Constraints[1] = <<gripperdims>>.servo_holder_axis_distance
  expr: Constraints[2] = <<gripperdims>>.slider_length / 2 - <<gripperdims>>.servo_holder_axis_distance / 2
  expr: Constraints[3] = <<gripperdims>>.slider_height / 2
  expr: Constraints[4] = <<gripperdims>>.servo_holder_roddiameter + <<gripperdims>>.slider_margin
  sketch-geometry (2):
    g0: Circle CenterX=53 CenterY=9 CenterZ=0 NormalX=0 NormalY=0 NormalZ=1 AngleXU=0 Radius=3.2
    g1: Circle CenterX=7 CenterY=9 CenterZ=0 NormalX=0 NormalY=0 NormalZ=1 AngleXU=0 Radius=3.2
  constraints (6):
    c: Horizontal(g1,g0)
    c: DistanceX(g1,g0) = 46
    c: DistanceX(g-1,g1) = 7
    c: DistanceY(g-1,g1) = 9
    c: Diameter(g1) = 6.4
    c: Equal(g1,g0)
FEATURE [PartDesign::Pocket] Pocket009
  BaseFeature = -> Pocket008
  Direction = (-1,0,0)
  Length = 5
  Length2 = 5
  Profile = -> Sketch014
  ReferenceAxis = -> Sketch014 [N_Axis]
  Type = 1
FEATURE [Sketcher::SketchObject] Sketch015
  FullyConstrained = true
  MapMode = 5
  Placement = pos=(0,0,0) rot=(0.57735,-0.57735,-0.57735;2.0944rad)
  Support = -> [Pocket009]
  expr: Constraints[10] = <<gripperdims>>.slider_length / 2 - <<gripperdims>>.slider_connector_length / 2
  expr: Constraints[11] = <<gripperdims>>.slider_height / 2 - <<gripperdims>>.slider_connector_thickness / 2
  expr: Constraints[8] = <<gripperdims>>.slider_connector_length
  expr: Constraints[9] = <<gripperdims>>.slider_connector_thickness
  sketch-geometry (4):
    g0: LineSegment StartX=-37 StartY=11 StartZ=0 EndX=-23 EndY=11 EndZ=0
    g1: LineSegment StartX=-23 StartY=11 StartZ=0 EndX=-23 EndY=7 EndZ=0
    g2: LineSegment StartX=-23 StartY=7 StartZ=0 EndX=-37 EndY=7 EndZ=0
    g3: LineSegment StartX=-37 StartY=7 StartZ=0 EndX=-37 EndY=11 EndZ=0
  constraints (12):
    c: Coincident(g0,g1)
    c: Coincident(g1,g2)
    c: Coincident(g2,g3)
    c: Coincident(g3,g0)
    c: Horizontal(g0)
    c: Horizontal(g2)
    c: Vertical(g1)
    c: Vertical(g3)
    c: DistanceX(g2,g2) = 14
    c: DistanceY(g1,g1) = 4
    c: DistanceX(g1,g-1) = 23
    c: DistanceY(g-1,g1) = 7
FEATURE [PartDesign::Pad] Pad005
  BaseFeature = -> Pocket009
  Direction = (-1,0,0)
  Length = 10
  Length2 = 10
  Profile = -> Sketch015
  ReferenceAxis = -> Sketch015 [N_Axis]
  Type = 0
  expr: Length = <<gripperdims>>.slider_connector_depth
FEATURE [Sketcher::SketchObject] Sketch016
  FullyConstrained = true
  MapMode = 5
  Placement = pos=(0,0,11) rot=(0,0,1;0rad)
  Support = -> [Pad005]
  expr: Constraints[0] = <<gripperdims>>.slider_connector_depth / 2
  expr: Constraints[1] = <<gripperdims>>.slider_length / 2
  expr: Constraints[2] = <<gripperdims>>.mg996r_holediameter
  sketch-geometry (1):
    g0: Circle CenterX=-5 CenterY=30 CenterZ=0 NormalX=0 NormalY=0 NormalZ=1 AngleXU=0 Radius=1.6
  constraints (3):
    c: DistanceX(g0,g-1) = 5
    c: DistanceY(g-1,g0) = 30
    c: Diameter(g0) = 3.2
FEATURE [PartDesign::Pocket] Pocket010
  BaseFeature = -> Pad005
  Direction = (0,0,-1)
  Length = 5
  Length2 = 5
  Profile = -> Sketch016
  ReferenceAxis = -> Sketch016 [N_Axis]
  Type = 1
FEATURE [Sketcher::SketchObject] Sketch017
  FullyConstrained = true
  MapMode = 5
  Placement = pos=(0,23,0) rot=(1,0,0;1.5708rad)
  Support = -> [Pocket010]
  expr: Constraints[10] = <<gripperdims>>.slider_height / 2 - <<gripperdims>>.slider_connector_foot / 2
  expr: Constraints[8] = <<gripperdims>>.slider_connector_foot
  expr: Constraints[9] = <<gripperdims>>.slider_connector_foot_thickness
  sketch-geometry (4):
    g0: LineSegment StartX=-3.5 StartY=13.5 StartZ=0 EndX=0 EndY=13.5 EndZ=0
    g1: LineSegment StartX=0 StartY=13.5 StartZ=0 EndX=0 EndY=4.5 EndZ=0
    g2: LineSegment StartX=0 StartY=4.5 StartZ=0 EndX=-3.5 EndY=4.5 EndZ=0
    g3: LineSegment StartX=-3.5 StartY=4.5 StartZ=0 EndX=-3.5 EndY=13.5 EndZ=0
  constraints (12):
    c: Coincident(g0,g1)
    c: Coincident(g1,g2)
    c: Coincident(g2,g3)
    c: Coincident(g3,g0)
    c: Horizontal(g0)
    c: Horizontal(g2)
    c: Vertical(g1)
    c: Vertical(g3)
    c: DistanceY(g3,g3) = 9
    c: DistanceX(g0,g0) = 3.5
    c: DistanceY(g-1,g1) = 4.5
    c: Vertical(g1,g-1)
FEATURE [PartDesign::Pad] Pad006
  BaseFeature = -> Pocket010
  Direction = (0,-1,2e-16)
  Length = 3.5
  Length2 = 10
  Profile = -> Sketch017
  ReferenceAxis = -> Sketch017 [N_Axis]
  Reversed = true
  Type = 0
  expr: Length = <<gripperdims>>.slider_connector_foot_thickness
FEATURE [Sketcher::SketchObject] Sketch018
  FullyConstrained = true
  MapMode = 5
  Placement = pos=(0,37,0) rot=(0,0.707107,0.707107;3.14159rad)
  Support = -> [Pad006]
  expr: Constraints[10] = <<gripperdims>>.slider_height / 2 - <<gripperdims>>.slider_connector_foot / 2
  expr: Constraints[8] = <<gripperdims>>.slider_connector_foot_thickness
  expr: Constraints[9] = <<gripperdims>>.slider_connector_foot
  sketch-geometry (4):
    g0: LineSegment StartX=0 StartY=13.5 StartZ=0 EndX=3.5 EndY=13.5 EndZ=0
    g1: LineSegment StartX=3.5 StartY=13.5 StartZ=0 EndX=3.5 EndY=4.5 EndZ=0
    g2: LineSegment StartX=3.5 StartY=4.5 StartZ=0 EndX=0 EndY=4.5 EndZ=0
    g3: LineSegment StartX=0 StartY=4.5 StartZ=0 EndX=0 EndY=13.5 EndZ=0
  constraints (12):
    c: Coincident(g0,g1)
    c: Coincident(g1,g2)
    c: Coincident(g2,g3)
    c: Coincident(g3,g0)
    c: Horizontal(g0)
    c: Horizontal(g2)
    c: Vertical(g1)
    c: Vertical(g3)
    c: DistanceX(g2,g2) = 3.5
    c: DistanceY(g1,g1) = 9
    c: DistanceY(g-1,g2) = 4.5
    c: Vertical(g2,g-1)
FEATURE [PartDesign::Pad] Pad007
  BaseFeature = -> Pad006
  Direction = (0,1,-2e-16)
  Length = 3.5
  Length2 = 10
  Profile = -> Sketch018
  ReferenceAxis = -> Sketch018 [N_Axis]
  Reversed = true
  Type = 0
  expr: Length = <<gripperdims>>.slider_connector_foot_thickness
FEATURE [PartDesign::Chamfer] Chamfer
  Angle = 45
  Base = -> Pad007 [Edge53,Edge40,Edge61,Edge74]
  BaseFeature = -> Pad007
  ChamferType = 1
  FlipDirection = false
  Size = 3.49
  Size2 = 2.49
  SupportTransform = false
  UseAllEdges = false
FEATURE [PartDesign::Chamfer] Chamfer001
  Angle = 45
  Base = -> Chamfer [Edge42,Edge92]
  BaseFeature = -> Chamfer
  ChamferType = 0
  FlipDirection = false
  Size = 3
  Size2 = 1
  SupportTransform = false
  UseAllEdges = false
FEATURE [Part::Feature] Part__Feature  label="Base_Base"
  Placement = pos=(0,0,0) rot=(1,0,0;1.5708rad)
  shape: bbox 215 x 140 x 45 mm, 316 faces (baked)
FEATURE [Part::Feature] Part__Feature060  label="Stepper NEMA 17 -  20mm shaft_Stepper NEMA 17 -  20mm shaft"
  Placement = pos=(-89.369,-0.156074,63.0261) rot=(0.379405,0.925231,0;3.14159rad)
  shape: bbox 53.07 x 53.07 x 60 mm, 181 faces (baked)
FEATURE [Part::Feature] Part__Feature061  label="Ball Bearing 608 - 8x22x7mm_Ball Bearing 608 - 8x22x7mm"
  Placement = pos=(-36.5,-5.3e-14,3) rot=(0.869075,0.349792,0.349792;1.71066rad)
  shape: bbox 22 x 22 x 7 mm, 26 faces (baked)
FEATURE [Part::Feature] Part__Feature062  label="Ball Bearing 608 - 8x22x7mm_Ball Bearing 608 - 8x22x7mm001"
  Placement = pos=(-36.5,1.42e-13,-7.5) rot=(0.904096,0.302167,0.302167;1.67145rad)
  shape: bbox 22 x 22 x 7 mm, 26 faces (baked)
FEATURE [Part::Feature] Part__Feature063  label="Thrust Bearing - 40x60x13_Thrust Bearing - 40x60x13"
  Placement = pos=(42.5,2.31e-13,-13) rot=(0.921644,0.274383,0.274383;1.6523rad)
  shape: bbox 60 x 60 x 13 mm, 98 faces, 21 solids (baked)
FEATURE [Part::Feature] Part__Feature064  label="Thrust Bearing - 40x60x13_Thrust Bearing - 40x60x014"
  Placement = pos=(42.5,-1.81e-13,10) rot=(0.935807,0.249264,0.249264;1.63709rad)
  shape: bbox 60 x 60 x 13 mm, 98 faces, 21 solids (baked)
FEATURE [Part::Feature] Part__Feature065  label="GT2 Pulley - 110 teeth - J1_GT2 Pulley - Parametric"
  Placement = pos=(42.5,2.01e-13,-11.2) rot=(-0.103324,0.703322,-0.703322;2.93568rad)
  shape: bbox 71.92 x 71.92 x 22.4 mm, 1012 faces (baked)
FEATURE [Part::Feature] Part__Feature066  label="GT2 Pulley - 22 - 80 teeth_GT2 Pulley - Parametric"
  Placement = pos=(-36.5,4.8e-13,-26.7) rot=(0.936789,0.247412,0.247412;1.63605rad)
  shape: bbox 52.82 x 52.82 x 18.8 mm, 935 faces (baked)
FEATURE [Part::Feature] Part__Feature067  label="GT2 Pulley - Parametric_GT2 Pulley - Parametric"
  Placement = pos=(-69.2568,32.2954,-19.7) rot=(0,0.707107,-0.707107;3.14159rad)
  shape: bbox 14.62 x 14.62 x 15.2 mm, 192 faces (baked)
FEATURE [Part::Feature] Part__Feature068  label="M8 Washer_M8 Washer"
  Placement = pos=(-36.5,1.65e-13,-9.1) rot=(0.995847,-0.064381,-0.064381;1.57496rad)
  shape: bbox 14 x 14 x 1.6 mm, 6 faces (baked)
FEATURE [Part::Feature] Part__Feature069  label="J1 coupler_J1 coupler"
  Placement = pos=(42.5,-4.07e-13,23) rot=(0.688995,-0.512487,-0.512487;1.93499rad)
  shape: bbox 120 x 120 x 27 mm, 92 faces (baked)
FEATURE [Part::Feature] Part__Feature070  label="Z-axis Bottom Plate_Z-axis Bottom Plate"
  Placement = pos=(42.5,-8.1e-13,31) rot=(0.465499,0.625824,0.625824;2.27026rad)
  shape: bbox 120 x 120 x 10 mm, 43 faces (baked)
FEATURE [Part::Feature] Part__Feature071  label="Smooth Rod D10mm L400mm_Smooth Rod D10mm L400mm"
  Placement = pos=(65.0083,41.8285,25) rot=(-0.067452,0.705496,0.705496;3.27629rad)
  shape: bbox 10 x 10 x 400 mm, 4 faces (baked)
FEATURE [Part::Feature] Part__Feature072  label="Smooth Rod D10mm L400mm_Smooth Rod D10mm L400mm001"
  Placement = pos=(84.3285,-22.5083,25) rot=(0.921644,0.274383,0.274383;1.6523rad)
  shape: bbox 10 x 10 x 400 mm, 4 faces (baked)
FEATURE [Part::Feature] Part__Feature073  label="Smooth Rod D10mm L400mm_Smooth Rod D10mm L400mm002"
  Placement = pos=(19.9917,-41.8285,25) rot=(0.921644,0.274383,0.274383;1.6523rad)
  shape: bbox 10 x 10 x 400 mm, 4 faces (baked)
FEATURE [Part::Feature] Part__Feature074  label="Smooth Rod D10mm L400mm_Smooth Rod D10mm L400mm003"
  Placement = pos=(0.671485,22.5083,25) rot=(0.921644,0.274383,0.274383;1.6523rad)
  shape: bbox 10 x 10 x 400 mm, 4 faces (baked)
FEATURE [Part::Feature] Part__Feature075  label="Smooth Rod Clamp_Smooth Rod Clamp"
  Placement = pos=(84.3285,-22.5083,41) rot=(0.763835,0.456375,0.456375;1.837rad)
  shape: bbox 32.55 x 37.4 x 14 mm, 30 faces (baked)
FEATURE [Part::Feature] Part__Feature076  label="Smooth Rod Clamp_Smooth Rod Clamp001"
  Placement = pos=(19.9917,-41.8285,41) rot=(0.94198,-0.237353,-0.237353;1.63053rad)
  shape: bbox 37.4 x 32.55 x 14 mm, 30 faces (baked)
FEATURE [Part::Feature] Part__Feature077  label="Smooth Rod Clamp_Smooth Rod Clamp002"
  Placement = pos=(0.671485,22.5083,41) rot=(-0.389175,0.651361,0.651361;3.88387rad)
  shape: bbox 32.55 x 37.4 x 14 mm, 30 faces (baked)
FEATURE [Part::Feature] Part__Feature078  label="Smooth Rod Clamp_Smooth Rod Clamp003"
  Placement = pos=(65.0083,41.8285,41) rot=(0.175409,0.696144,0.696144;2.79431rad)
  shape: bbox 37.4 x 32.55 x 14 mm, 30 faces (baked)
FEATURE [Part::Feature] Part__Feature079  label="Z-axis Top Plate_Z-axis Top Plate"
  Placement = pos=(42.5,-7.155e-12,425) rot=(0.465499,0.625824,0.625824;2.27026rad)
  shape: bbox 120 x 120 x 26 mm, 74 faces (baked)
FEATURE [Part::Feature] Part__Feature080  label="Smooth Rod Clamp_Smooth Rod Clamp004"
  Placement = pos=(19.9917,-41.8285,411) rot=(0.94198,-0.237353,-0.237353;1.63053rad)
  shape: bbox 37.4 x 32.55 x 14 mm, 30 faces (baked)
FEATURE [Part::Feature] Part__Feature081  label="Smooth Rod Clamp_Smooth Rod Clamp005"
  Placement = pos=(84.3285,-22.5083,411) rot=(0.763835,0.456375,0.456375;1.837rad)
  shape: bbox 32.55 x 37.4 x 14 mm, 30 faces (baked)
FEATURE [Part::Feature] Part__Feature082  label="Smooth Rod Clamp_Smooth Rod Clamp006"
  Placement = pos=(65.0083,41.8285,411) rot=(0.175409,0.696144,0.696144;2.79431rad)
  shape: bbox 37.4 x 32.55 x 14 mm, 30 faces (baked)
FEATURE [Part::Feature] Part__Feature083  label="Smooth Rod Clamp_Smooth Rod Clamp007"
  Placement = pos=(0.671485,22.5083,411) rot=(-0.389175,0.651361,0.651361;3.88387rad)
  shape: bbox 32.55 x 37.4 x 14 mm, 30 faces (baked)
FEATURE [Part::Feature] Part__Feature084  label="Lead Screw D8mm L380mm_Lead Screw D8mm L380mm"
  Placement = pos=(74.1057,9.4911,33) rot=(0.928217,0.263072,0.263072;1.64522rad)
  shape: bbox 8 x 8 x 380 mm, 4 faces (baked)
FEATURE [Part::Feature] Part__Feature085  label="Ball Bearing 608 - 8x22x7mm_Ball Bearing 608 - 8x22x7mm002"
  Placement = pos=(74.1057,9.4911,34) rot=(0.824902,0.39971,0.39971;1.76211rad)
  shape: bbox 22 x 22 x 7 mm, 26 faces (baked)
FEATURE [Part::Feature] Part__Feature086  label="Stepper NEMA 17 -  20mm shaft_Stepper NEMA 17 -  20mm shaft001"
  Placement = pos=(40.8832,-9.32019,494.026) rot=(0.596821,0.802374,0;3.14159rad)
  shape: bbox 49.05 x 49.05 x 60 mm, 181 faces (baked)
FEATURE [Part::Feature] Part__Feature087  label="Z-axis Mount Platform_Z-axis Mount Platform"
  Placement = pos=(42.5,-5.095e-12,273.616) rot=(-0.688995,0.512487,-0.512487;1.93499rad)
  shape: bbox 130.6 x 120 x 45 mm, 110 faces (baked)
FEATURE [Part::Feature] Part__Feature088  label="Arm 1_Arm 1"
  Placement = pos=(260.867,65.5748,228.616) rot=(0.979092,0.143837,0.143837;1.59192rad)
  shape: bbox 209.2 x 124.1 x 42 mm, 134 faces (baked)
FEATURE [Part::Feature] Part__Feature089  label="Ball Bearing 608 - 8x22x7mm_Ball Bearing 608 - 8x22x7mm003"
  Placement = pos=(174.669,39.69,244.616) rot=(-0.975962,0.154109,-0.154109;1.59513rad)
  shape: bbox 22 x 22 x 7 mm, 26 faces (baked)
FEATURE [Part::Feature] Part__Feature090  label="Ball Bearing 608 - 8x22x7mm_Ball Bearing 608 - 8x22x7mm004"
  Placement = pos=(174.669,39.69,235.616) rot=(-0.974306,0.15926,-0.15926;1.59682rad)
  shape: bbox 22 x 22 x 7 mm, 26 faces (baked)
FEATURE [Part::Feature] Part__Feature091  label="J2 Coupler_J2 Coupler"
  Placement = pos=(260.867,65.5748,209.616) rot=(0.634652,0.54645,0.54645;2.01057rad)
  shape: bbox 78 x 78 x 24 mm, 93 faces (baked)
FEATURE [Part::Feature] Part__Feature092  label="Thrust Bearing 35x52x12mm_Thrust Bearing 35x52x12mm"
  Placement = pos=(260.867,65.5748,216.616) rot=(0.921729,0.274241,0.274241;1.65221rad)
  shape: bbox 52 x 52 x 12 mm, 90 faces, 19 solids (baked)
FEATURE [Part::Feature] Part__Feature093  label="Ball Bearing 30x42x7mm_Ball Bearing 30x42x7mm"
  Placement = pos=(260.867,65.5748,231.616) rot=(0.921729,0.274241,0.274241;1.65221rad)
  shape: bbox 42 x 42 x 7 mm, 26 faces (baked)
FEATURE [Part::Feature] Part__Feature094  label="GT2 Pulley - 92 teeth - J2_GT2 Pulley - Parametric"
  Placement = pos=(260.867,65.5748,246.816) rot=(0.994469,-0.074265,-0.074265;1.57634rad)
  shape: bbox 60.46 x 60.46 x 20.4 mm, 852 faces (baked)
FEATURE [Part::Feature] Part__Feature095  label="GT2 Pulley - 23 - 80 teeth_GT2 Pulley - Parametric"
  Placement = pos=(174.669,39.69,263.816) rot=(-0.024599,0.706893,-0.706893;3.0924rad)
  shape: bbox 53.62 x 53.62 x 18.8 mm, 951 faces (baked)
FEATURE [Part::Feature] Part__Feature096  label="Thrust Bearing 35x52x12mm_Thrust Bearing 35x52x12mm001"
  Placement = pos=(260.867,65.5748,238.616) rot=(0.921729,0.274241,0.274241;1.65221rad)
  shape: bbox 52 x 52 x 12 mm, 90 faces, 19 solids (baked)
FEATURE [Part::Feature] Part__Feature097  label="Stepper NEMA 17 -  20mm shaft_Stepper NEMA 17 -  20mm shaft002"
  Placement = pos=(-0.29999,-21.6874,334.643) rot=(0.596821,0.802374,0;3.14159rad)
  shape: bbox 49.05 x 49.05 x 60 mm, 181 faces (baked)
FEATURE [Part::Feature] Part__Feature098  label="GT2 Pulley - Parametric_GT2 Pulley - Parametric001"
  Placement = pos=(32.9225,-2.87609,263.816) rot=(-0.154171,-0.698653,0.698653;2.83566rad)
  shape: bbox 14.62 x 14.62 x 15.2 mm, 192 faces (baked)
FEATURE [Part::Feature] Part__Feature099  label="M8 Washer_M8 Washer001"
  Placement = pos=(174.669,39.69,244.616) rot=(0.995847,-0.064381,-0.064381;1.57496rad)
  shape: bbox 14 x 14 x 1.6 mm, 6 faces (baked)
FEATURE [Part::Feature] Part__Feature100  label="Linear Bearing 10x19x29mm_Linear Bearing 10x19x29mm"
  Placement = pos=(0.671485,22.5083,238.616) rot=(0.898843,0.309904,0.309904;1.67724rad)
  shape: bbox 20.41 x 20.41 x 29 mm, 32 faces (baked)
FEATURE [Part::Feature] Part__Feature101  label="Linear Bearing 10x19x29mm_Linear Bearing 10x19x29mm001"
  Placement = pos=(65.0083,41.8285,238.616) rot=(0.986685,0.115004,0.115004;1.5842rad)
  shape: bbox 20.01 x 20.01 x 29 mm, 32 faces (baked)
FEATURE [Part::Feature] Part__Feature102  label="Linear Bearing 10x19x29mm_Linear Bearing 10x19x29mm002"
  Placement = pos=(19.9917,-41.8285,238.616) rot=(0.921644,0.274383,0.274383;1.6523rad)
  shape: bbox 20.13 x 20.13 x 29 mm, 32 faces (baked)
FEATURE [Part::Feature] Part__Feature103  label="Linear Bearing 10x19x29mm_Linear Bearing 10x19x29mm003"
  Placement = pos=(84.3285,-22.5083,238.616) rot=(0.921644,0.274383,0.274383;1.6523rad)
  shape: bbox 20.13 x 20.13 x 29 mm, 32 faces (baked)
FEATURE [Part::Feature] Part__Feature104  label="Arm 2_Arm 2"
  Placement = pos=(373.497,-24.149,209.616) rot=(-0.896411,0.313406,-0.313406;1.67993rad)
  shape: bbox 190.6 x 167.7 x 31 mm, 223 faces (baked)
FEATURE [Part::Feature] Part__Feature105  label="Arm 2 Cover_Arm 2 Cover"
  Placement = pos=(373.497,-24.149,170.616) rot=(0.896411,-0.313406,-0.313406;1.67993rad)
  shape: bbox 190.6 x 167.7 x 8 mm, 82 faces (baked)
FEATURE [Part::Feature] Part__Feature106  label="Micro switch_Micro switch"
  Placement = pos=(212.995,41.2228,228.616) rot=(0.924829,0.380383,0;3.14159rad)
  shape: bbox 30.72 x 23.39 x 6 mm, 67 faces, 2 solids (baked)
FEATURE [Part::Feature] Part__Feature107  label="NEMA 17 Stepper L24mm - 20mm shaft_NEMA 17 Stepper L24mm - 20mm shaft"
  Placement = pos=(256.174,69.3133,146.616) rot=(0.896411,-0.313406,-0.313406;1.67993rad)
  shape: bbox 54.04 x 54.04 x 46 mm, 158 faces, 5 solids (baked)
FEATURE [Part::Feature] Part__Feature108  label="J3 Coupler_J3 Coupler"
  Placement = pos=(367.631,-19.4759,152.616) rot=(0.401857,0.6475,0.6475;2.37738rad)
  shape: bbox 78 x 78 x 22 mm, 64 faces (baked)
FEATURE [Part::Feature] Part__Feature109  label="Ball Bearing 30x42x7mm_Ball Bearing 30x42x7mm001"
  Placement = pos=(367.631,-19.4759,178.616) rot=(-0.000118,0.707107,-0.707107;3.14136rad)
  shape: bbox 42 x 42 x 7 mm, 26 faces (baked)
FEATURE [Part::Feature] Part__Feature110  label="Thrust Bearing 35x52x12mm_Thrust Bearing 35x52x12mm002"
  Placement = pos=(367.631,-19.4759,178.616) rot=(0.771667,0.449739,0.449739;1.82714rad)
  shape: bbox 52 x 52 x 12 mm, 90 faces, 19 solids (baked)
FEATURE [Part::Feature] Part__Feature111  label="Thrust Bearing 35x52x12mm_Thrust Bearing 35x52x12mm003"
  Placement = pos=(367.631,-19.4759,170.616) rot=(-0.153116,-0.698769,0.698769;2.83772rad)
  shape: bbox 52 x 52 x 12 mm, 90 faces, 19 solids (baked)
FEATURE [Part::Feature] Part__Feature112  label="GT2 Pulley - 90 teeth - J3_GT2 Pulley - Parametric"
  Placement = pos=(367.631,-19.4759,188.816) rot=(-0.163304,0.697614,0.697614;3.46534rad)
  shape: bbox 59.19 x 59.19 x 21.4 mm, 836 faces (baked)
FEATURE [Part::Feature] Part__Feature113  label="GT2 Pulley - Parametric_GT2 Pulley - Parametric002"
  Placement = pos=(256.174,69.3133,188.816) rot=(0.786726,0.436498,0.436498;1.8084rad)
  shape: bbox 14.62 x 14.62 x 15.2 mm, 192 faces (baked)
FEATURE [Part::Feature] Part__Feature114  label="Micro switch_Micro switch001"
  Placement = pos=(-8.74106,-2.55473,16) rot=(0.970296,0.241922,0;3.14159rad)
  shape: bbox 28.39 x 21.97 x 6 mm, 67 faces, 2 solids (baked)
FEATURE [Part::Feature] Part__Feature115  label="Micro switch_Micro switch002"
  Placement = pos=(327.465,0.305099,170.616) rot=(0.995772,-0.091863,0;3.14159rad)
  shape: bbox 21.49 x 27.86 x 6 mm, 67 faces, 2 solids (baked)
FEATURE [Part::Feature] Part__Feature116  label="Lead Screw Nut 8mm_Lead Screw Nut 8mm"
  Placement = pos=(74.1057,9.4911,264.116) rot=(0.979092,0.143837,0.143837;1.59192rad)
  shape: bbox 22 x 22 x 15 mm, 20 faces (baked)
FEATURE [Part::Feature] Part__Feature117  label="Servo Holder_Servo Holder"
  Placement = pos=(30.6623,30.9064,53.3617) rot=(0,0,1;0rad)
  shape: bbox 44 x 15 x 72.5 mm, 53 faces (baked)
FEATURE [Part::Feature] Part__Feature118  label="Servo Motor MG996R 3D Model_Servo Motor MG996R 3D Model001"
  Placement = pos=(30.6623,-0.293585,62.3617) rot=(0,-1,0;1.5708rad)
  shape: bbox 22.19 x 45.2 x 55.8 mm, 123 faces, 4 solids (baked)
FEATURE [Part::Feature] Part__Feature119  label="Servo MG996R Horn_Servo MG996R Horn"
  Placement = pos=(30.6623,44.9064,52.1117) rot=(0,-1,0;1.0832rad)
  shape: bbox 17.65 x 2.5 x 28.85 mm, 18 faces (baked)
FEATURE [Part::Feature] Part__Feature120  label="Gripper Cover_Gripper Cover"
  Placement = pos=(30.6623,56.4064,52.1117) rot=(0,0,1;3.14159rad)
  shape: bbox 44 x 10.5 x 70 mm, 32 faces (baked)
FEATURE [Part::Feature] Part__Feature121  label="Gripper Hand Left_Gripper Hand Left"
  Placement = pos=(0.114489,53.9064,27.1117) rot=(0,0,1;0rad)
  shape: bbox 26 x 4 x 105 mm, 19 faces (baked)
FEATURE [Part::Feature] Part__Feature122  label="Gripper rail 6mm_Gripper rail 6mm"
  Placement = pos=(-31.8377,44.9064,75.1117) rot=(0.663001,0.663001,0.347647;3.81075rad)
  shape: bbox 125 x 6 x 6 mm, 4 faces (baked)
FEATURE [Part::Feature] Part__Feature123  label="Gripper End_Gripper End"
  Placement = pos=(-23.3855,44.9064,114.112) rot=(0.57735,0.57735,0.57735;4.18879rad)
  shape: bbox 30 x 25.12 x 27.12 mm, 22 faces (baked)
FEATURE [Part::Feature] Part__Feature124  label="Gripper Hand Right_Gripper Hand Left"
  Placement = pos=(61.21,53.9064,27.1117) rot=(0,0,1;0rad)
  shape: bbox 26 x 4 x 105 mm, 19 faces (baked)
FEATURE [Part::Feature] Part__Feature125  label="Gripper rail 6mm_Gripper rail 6mm001"
  Placement = pos=(93.1623,44.9064,29.1117) rot=(-0.273191,0.273191,0.922352;1.65154rad)
  shape: bbox 125 x 6 x 6 mm, 4 faces (baked)
FEATURE [Part::Feature] Part__Feature126  label="Gripper Mechanism Slider_Gripper Mechanism Slider"
  Placement = pos=(-20.8855,44.9064,52.1117) rot=(0.707107,0.707107,0;3.14159rad)
  shape: bbox 26 x 18 x 60 mm, 31 faces (baked)
FEATURE [Part::Feature] Part__Feature127  label="Gripper Mechanism Slider_Gripper Mechanism Slider001"
  Placement = pos=(82.21,44.9064,52.1117) rot=(0.707107,-0.707107,0;3.14159rad)
  shape: bbox 26 x 18 x 60 mm, 31 faces (baked)
FEATURE [Part::Feature] Part__Feature128  label="Gripper Hand Left_Gripper Hand Left001"
  Placement = pos=(0.114489,31.9064,27.1117) rot=(0,0,1;0rad)
  shape: bbox 26 x 4 x 105 mm, 19 faces (baked)
FEATURE [Part::Feature] Part__Feature129  label="Gripper Hand Right_Gripper Hand Left001"
  Placement = pos=(61.21,31.9064,27.1117) rot=(0,0,1;0rad)
  shape: bbox 26 x 4 x 105 mm, 19 faces (baked)
FEATURE [Part::Feature] Part__Feature130  label="Gripper End_Gripper End001"
  Placement = pos=(84.71,44.9064,114.112) rot=(0.57735,-0.57735,-0.57735;4.18879rad)
  shape: bbox 30 x 25.12 x 27.12 mm, 22 faces (baked)
FEATURE [Part::Feature] Part__Feature131  label="Gripper link 1_Gripper link 1"
  Placement = pos=(24.3375,47.4064,40.185) rot=(0,1,0;0.457527rad)
  shape: bbox 31.42 x 3.5 x 19.13 mm, 10 faces (baked)
FEATURE [Part::Feature] Part__Feature132  label="Gripper link 2_Gripper link 2"
  Placement = pos=(0.114489,39.9064,52.1117) rot=(0,1,0;3.59912rad)
  shape: bbox 31.42 x 5 x 19.13 mm, 14 faces (baked)
FEATURE [Part::Feature] Part__Feature133  label="Gripper link 1_Gripper link 002"
  Placement = pos=(61.21,47.4064,52.1117) rot=(0,1,0;0.457527rad)
  shape: bbox 31.42 x 3.5 x 19.13 mm, 10 faces (baked)
FEATURE [Part::Feature] Part__Feature134  label="Gripper link 2_Gripper link 003"
  Placement = pos=(36.9871,44.9064,64.0385) rot=(0.226773,0,0.973948;3.14159rad)
  shape: bbox 31.42 x 5 x 19.13 mm, 14 faces (baked)
FEATURE [Part::Feature] Part__Feature135  label="Gripper to J3 connector_Gripper to J3 connector"
  Placement = pos=(30.6623,44.9064,17.1117) rot=(0.57735,-0.57735,0.57735;4.18879rad)
  shape: bbox 78 x 39 x 4.5 mm, 44 faces (baked)
FEATURE [App::Part] Gripper_Mechanism_Gripper_Mechanism  label="Gripper Mechanism_Gripper Mechanism"
  Group = -> [Part__Feature117,Part__Feature118,Part__Feature119,Part__Feature120,Part__Feature121,Part__Feature122,Part__Feature123,Part__Feature124,Part__Feature125,Part__Feature126,Part__Feature127,Part__Feature128,Part__Feature129,Part__Feature130,Part__Feature131,Part__Feature132,Part__Feature133,Part__Feature134,Part__Feature135]
  Origin = -> Origin004
  Placement = pos=(330.772,20.5016,165.228) rot=(0.997346,0.072805,0;3.14159rad)
FEATURE [Part::Feature] Part__Feature136  label="Arm 1 Cover_Arm 1 Cover"
  Placement = pos=(260.867,65.5748,273.616) rot=(-0.979092,-0.143837,0.143837;1.59192rad)
  shape: bbox 209.2 x 124.1 x 11 mm, 68 faces (baked)
FEATURE [Part::Feature] Part__Feature137  label="Micro switch_Micro switch003"
  Placement = pos=(17.1693,-13.8714,412) rot=(-0.979092,-0.143837,0.143837;1.59192rad)
  shape: bbox 22.42 x 11.5 x 25.05 mm, 67 faces, 2 solids (baked)
FEATURE [Part::Feature] Part__Feature138  label="Base cover_Base cover"
  Placement = pos=(42.5,-1.375e-12,62.5) rot=(-0.979092,-0.143837,0.143837;1.59192rad)
  shape: bbox 120 x 120 x 21.5 mm, 17 faces (baked)
FEATURE [Part::Feature] Part__Feature139  label="Top cover_Top cover"
  Placement = pos=(42.5,-7.365e-12,402) rot=(0.979092,0.143837,0.143837;1.59192rad)
  shape: bbox 120 x 120 x 23 mm, 59 faces (baked)
FEATURE [Part::Feature] Part__Feature140  label="Arduino Mega case_Arduino UNO case p1"
  Placement = pos=(-150,60,-32.5) rot=(1,0,0;1.5708rad)
  shape: bbox 85 x 120 x 45 mm, 100 faces (baked)
FEATURE [Part::Feature] Part__Feature141  label="Arduino Mega case p2_Arduino UNO case p2"
  Placement = pos=(-150.5,60,8) rot=(1,0,0;1.5708rad)
  shape: bbox 76 x 120 x 40 mm, 94 faces (baked)
FEATURE [Part::Feature] Part__Feature142  label="GT2 Belt 200mm_GT2 Belt 400mm"
  Placement = pos=(-36.5,5.29e-13,-25.7) rot=(0.865061,-0.354732,-0.354732;1.71525rad)
  shape: bbox 66.21 x 65.75 x 6 mm, 14 faces (baked)
FEATURE [Part::Feature] Part__Feature143  label="GT2 Belt 300mm 2_GT2 Belt 400mm"
  Placement = pos=(42.5,3.06e-13,-17.2) rot=(1,0,0;1.5708rad)
  shape: bbox 122.6 x 71.6 x 6 mm, 14 faces (baked)
FEATURE [Part::Feature] Part__Feature144  label="GT2 Belt 400mm_GT2 Belt 400mm"
  Placement = pos=(174.669,39.69,257.816) rot=(0.979092,0.143837,0.143837;1.59192rad)
  shape: bbox 175.2 x 76.02 x 6 mm, 14 faces (baked)
FEATURE [Part::Feature] Part__Feature145  label="GT2 Belt 300mm_GT2 Belt 400mm"
  Placement = pos=(260.867,65.5748,247.816) rot=(0.979092,0.143837,0.143837;1.59192rad)
  shape: bbox 124.4 x 64.08 x 6 mm, 14 faces (baked)
FEATURE [Part::Feature] Part__Feature146  label="GT2 Belt 400mm 2_GT2 Belt 400mm"
  Placement = pos=(367.631,-19.4759,188.816) rot=(0.896411,-0.313406,-0.313406;1.67993rad)
  shape: bbox 148.1 x 125.4 x 6 mm, 14 faces (baked)
FEATURE [Part::Feature] Part__Feature147  label="Ball Bearing 35x47x7mm_Ball Bearing 30x42x7mm"
  Placement = pos=(42.5,0,0) rot=(0.923673,0.27095,0.27095;1.65011rad)
  shape: bbox 47 x 47 x 7 mm, 26 faces (baked)
FEATURE [Part::Feature] Part__Feature148  label="M8 45mm - Bolts_M8 45mm - Bolts"
  Placement = pos=(-36.5,1.45e-13,-8.05) rot=(0.035382,-0.998747,0.035382;1.57205rad)
  shape: bbox 15.01 x 15.01 x 50.3 mm, 19 faces (baked)
FEATURE [Part::Feature] Part__Feature149  label="M8 Lock nut_M8 Lock nut"
  Placement = pos=(-36.5,-1.74e-13,10) rot=(0.61942,-0.555121,-0.555121;2.03244rad)
  shape: bbox 15.01 x 15.01 x 8 mm, 40 faces, 2 solids (baked)
FEATURE [Part::Feature] Part__Feature150  label="M8 45mm - Bolts_M8 45mm - Bolts001"
  Placement = pos=(174.669,39.69,245.166) rot=(0.043786,0.998081,-0.043786;1.57272rad)
  shape: bbox 15.01 x 15.01 x 50.3 mm, 19 faces (baked)
FEATURE [Part::Feature] Part__Feature151  label="M8 Lock nut_M8 Lock nut001"
  Placement = pos=(174.669,39.69,228.616) rot=(0,0.707107,-0.707107;3.14159rad)
  shape: bbox 15.01 x 15.01 x 8 mm, 40 faces, 2 solids (baked)
FEATURE [Part::Feature] Part__Feature152  label="M4 Lock nut_M4 Lock nut"
  Placement = pos=(249.989,67.2086,255.016) rot=(0.921644,0.274383,0.274383;1.6523rad)
  shape: bbox 8.083 x 8.083 x 5 mm, 40 faces, 2 solids (baked)
FEATURE [Part::Feature] Part__Feature153  label="M4 Lock nut_M4 Lock nut001"
  Placement = pos=(262.5,76.4528,255.016) rot=(0.921644,0.274383,0.274383;1.6523rad)
  shape: bbox 8.083 x 8.083 x 5 mm, 40 faces, 2 solids (baked)
FEATURE [Part::Feature] Part__Feature154  label="M4 Lock nut_M4 Lock nut002"
  Placement = pos=(271.745,63.9411,255.016) rot=(0.921644,0.274383,0.274383;1.6523rad)
  shape: bbox 8.083 x 8.083 x 5 mm, 40 faces, 2 solids (baked)
FEATURE [Part::Feature] Part__Feature155  label="M4 Lock nut_M4 Lock nut003"
  Placement = pos=(259.233,54.6969,255.016) rot=(0.921644,0.274383,0.274383;1.6523rad)
  shape: bbox 8.083 x 8.083 x 5 mm, 40 faces, 2 solids (baked)
FEATURE [Part::Feature] Part__Feature156  label="M4 60mm - Bolts_M4 60mm - Bolts"
  Placement = pos=(38.9049,11.9718,28.8) rot=(0,0,1;2.44655rad)
  shape: bbox 7.5 x 7.5 x 60 mm, 31 faces (baked)
FEATURE [Part::Feature] Part__Feature157  label="M4 60mm - Bolts_M4 60mm - Bolts001"
  Placement = pos=(30.5282,-3.59511,28.8) rot=(0,0,1;0.57871rad)
  shape: bbox 7.5 x 7.5 x 60 mm, 31 faces (baked)
FEATURE [Part::Feature] Part__Feature158  label="M4 60mm - Bolts_M4 60mm - Bolts002"
  Placement = pos=(54.4718,3.59511,28.8) rot=(0,0,1;0.57871rad)
  shape: bbox 7.5 x 7.5 x 60 mm, 31 faces (baked)
FEATURE [Part::Feature] Part__Feature159  label="M4 60mm - Bolts_M4 60mm - Bolts003"
  Placement = pos=(46.0951,-11.9718,28.8) rot=(0,0,1;0.57871rad)
  shape: bbox 7.5 x 7.5 x 60 mm, 31 faces (baked)
FEATURE [Part::Feature] Part__Feature160  label="M4 50mm - Bolts_M4 50mm - Bolts"
  Placement = pos=(249.989,67.2086,211.816) rot=(0.958428,0.285334,0;3.14159rad)
  shape: bbox 7.5 x 7.5 x 50 mm, 31 faces (baked)
FEATURE [Part::Feature] Part__Feature161  label="M4 50mm - Bolts_M4 50mm - Bolts001"
  Placement = pos=(259.233,54.6969,211.816) rot=(0.958428,0.285334,0;3.14159rad)
  shape: bbox 7.5 x 7.5 x 50 mm, 31 faces (baked)
FEATURE [Part::Feature] Part__Feature162  label="M4 50mm - Bolts_M4 50mm - Bolts002"
  Placement = pos=(271.745,63.9411,211.816) rot=(0.958428,0.285334,0;3.14159rad)
  shape: bbox 7.5 x 7.5 x 50 mm, 31 faces (baked)
FEATURE [Part::Feature] Part__Feature163  label="M4 50mm - Bolts_M4 50mm - Bolts003"
  Placement = pos=(262.5,76.4528,211.816) rot=(0.958428,0.285334,0;3.14159rad)
  shape: bbox 7.5 x 7.5 x 50 mm, 31 faces (baked)
FEATURE [Part::Feature] Part__Feature164  label="M4 Lock nut_M4 Lock nut004"
  Placement = pos=(46.0951,-11.9718,-19.4) rot=(0,0.707107,-0.707107;3.14159rad)
  shape: bbox 8.083 x 8.083 x 5 mm, 40 faces, 2 solids (baked)
FEATURE [Part::Feature] Part__Feature165  label="M4 Lock nut_M4 Lock nut005"
  Placement = pos=(38.9049,11.9718,-19.4) rot=(0,0.707107,-0.707107;3.14159rad)
  shape: bbox 8.083 x 8.083 x 5 mm, 40 faces, 2 solids (baked)
FEATURE [Part::Feature] Part__Feature166  label="M4 Lock nut_M4 Lock nut006"
  Placement = pos=(54.4718,3.59511,-19.4) rot=(0,0.707107,-0.707107;3.14159rad)
  shape: bbox 8.083 x 8.083 x 5 mm, 40 faces, 2 solids (baked)
FEATURE [Part::Feature] Part__Feature167  label="M4 Lock nut_M4 Lock nut007"
  Placement = pos=(30.5282,-3.59511,-19.4) rot=(0,0.707107,-0.707107;3.14159rad)
  shape: bbox 8.083 x 8.083 x 5 mm, 40 faces, 2 solids (baked)
FEATURE [Part::Feature] Part__Feature168  label="Laser module holder_Gripper to J3 connector"
  Placement = pos=(-244,55.5,-14) rot=(0,1,0;1.5708rad)
  shape: bbox 78 x 114.5 x 42 mm, 77 faces (baked)
FEATURE [Part::Feature] Part__Feature169  label="Laser Module 5.5W"
  Placement = pos=(-244,-62,-14) rot=(0,0,1;0rad)
  shape: bbox 33 x 108.8 x 33.22 mm, 478 faces, 17 solids (baked)
FEATURE [Sketcher::SketchObject] Sketch019
  FullyConstrained = true
  MapMode = 5
  Support = -> [XY_Plane006]
  expr: Constraints[16] = <<gripperdims>>.slider_width
  expr: Constraints[17] = <<gripperdims>>.hand_overhang
  expr: Constraints[27] = <<gripperdims>>.slider_width / 2
  expr: Constraints[30] = <<gripperdims>>.slider_handholes_distance
  expr: Constraints[31] = <<gripperdims>>.slider_length / 2 - <<gripperdims>>.slider_handholes_distance / 2
  expr: Constraints[32] = <<gripperdims>>.mg996r_holediameter
  expr: Constraints[37] = <<gripperdims>>.gripper_hole_distance
  expr: Constraints[38] = (<<gripperdims>>.gripper_height - <<gripperdims>>.gripper_hole_distance) / 2
  expr: Constraints[3] = <<gripperdims>>.slider_length
  expr: Constraints[4] = <<gripperdims>>.hand_height
  sketch-geometry (13):
    g0: LineSegment StartX=0 StartY=60 StartZ=0 EndX=16 EndY=60 EndZ=0
    g1: LineSegment StartX=16 StartY=-45 StartZ=0 EndX=0 EndY=-45 EndZ=0
    g2: LineSegment StartX=0 StartY=60 StartZ=0 EndX=-5 EndY=52 EndZ=0
    g3: LineSegment StartX=-5 StartY=52 StartZ=0 EndX=-5 EndY=-3 EndZ=0
    g4: LineSegment StartX=-5 StartY=-3 StartZ=0 EndX=-2 EndY=-9 EndZ=0
    g5: LineSegment StartX=-2 StartY=-9 StartZ=0 EndX=0 EndY=-45 EndZ=0
    g6: LineSegment StartX=16 StartY=-45 StartZ=0 EndX=24 EndY=15 EndZ=0
    g7: LineSegment StartX=24 StartY=15 StartZ=0 EndX=24 EndY=44 EndZ=0
    g8: LineSegment StartX=24 StartY=44 StartZ=0 EndX=16 EndY=60 EndZ=0
    g9: Circle CenterX=8 CenterY=19 CenterZ=0 NormalX=0 NormalY=0 NormalZ=1 AngleXU=0 Radius=1.6
    g10: Circle CenterX=8 CenterY=41 CenterZ=0 NormalX=0 NormalY=0 NormalZ=1 AngleXU=0 Radius=1.6
    g11: Circle CenterX=8 CenterY=-40 CenterZ=0 NormalX=0 NormalY=0 NormalZ=1 AngleXU=0 Radius=1.6
    g12: Circle CenterX=8 CenterY=-30 CenterZ=0 NormalX=0 NormalY=0 NormalZ=1 AngleXU=0 Radius=1.6
  constraints (39):
    c: Horizontal(g0)
    c: Horizontal(g1)
    c: Vertical(g0,g-1)
    c: DistanceY(g-1,g0) = 60
    c: DistanceY(g1,g0) = 105
    c: Coincident(g2,g0)
    c: Coincident(g3,g2)
    c: Vertical(g3)
    c: Coincident(g4,g3)
    c: Coincident(g5,g4)
    c: Coincident(g5,g1)
    c: Coincident(g6,g1)
    c: Coincident(g7,g6)
    c: Vertical(g7)
    c: Coincident(g8,g7)
    c: Coincident(g8,g0)
    c: DistanceX(g0,g0) = 16
    c: DistanceX(g2,g0) = 5
    c: DistanceY(g2,g0) = 8
    c: DistanceY(g3,g3) = 55
    c: DistanceY(g4,g3) = 6
    c: DistanceX(g3,g4) = 3
    c: Vertical(g1,g-1)
    c: Vertical(g1,g0)
    c: DistanceY(g1,g6) = 60
    c: DistanceX(g1,g6) = 8
    c: DistanceY(g7,g0) = 16
    c: DistanceX(g-1,g9) = 8
    c: Vertical(g9,g10)
    c: Equal(g9,g10)
    c: DistanceY(g9,g10) = 22
    c: DistanceY(g-1,g9) = 19
    c: Diameter(g9) = 3.2
    c: Equal(g12,g11)
    c: Equal(g11,g9)
    c: Vertical(g12,g11)
    c: Vertical(g12,g9)
    c: DistanceY(g11,g12) = 10
    c: DistanceY(g1,g11) = 5
FEATURE [PartDesign::Pad] Pad008
  Direction = (0,0,1)
  Length = 4
  Length2 = 10
  Profile = -> Sketch019
  ReferenceAxis = -> Sketch019 [N_Axis]
  Type = 0
  expr: Length = <<gripperdims>>.hand_thickness
FEATURE [Sketcher::SketchObject] Sketch020
  FullyConstrained = true
  MapMode = 5
  Support = -> [XY_Plane007]
  expr: Constraints[7] = <<gripperdims>>.link_length
  expr: Constraints[8] = <<gripperdims>>.link_width
  expr: Constraints[9] = <<gripperdims>>.servo_holder_moving_hole_diameter
  sketch-geometry (6):
    g0: ArcOfCircle CenterX=0 CenterY=0 CenterZ=0 NormalX=0 NormalY=0 NormalZ=1 AngleXU=0 Radius=3.6 StartAngle=1.5708 EndAngle=4.71239
    g1: ArcOfCircle CenterX=27 CenterY=2.76e-14 CenterZ=0 NormalX=0 NormalY=0 NormalZ=1 AngleXU=0 Radius=3.6 StartAngle=4.71239 EndAngle=7.85398
    g2: LineSegment StartX=-7e-16 StartY=-3.6 StartZ=0 EndX=27 EndY=-3.6 EndZ=0
    g3: LineSegment StartX=27 StartY=3.6 StartZ=0 EndX=-3.6e-15 EndY=3.6 EndZ=0
    g4: Circle CenterX=0 CenterY=0 CenterZ=0 NormalX=0 NormalY=0 NormalZ=1 AngleXU=0 Radius=1.7
    g5: Circle CenterX=27 CenterY=2.76e-14 CenterZ=0 NormalX=0 NormalY=0 NormalZ=1 AngleXU=0 Radius=1.7
  constraints (13):
    c: Tangent(g0,g2) = -1.5708
    c: Tangent(g2,g1) = -1.5708
    c: Tangent(g1,g3) = -1.5708
    c: Tangent(g3,g0) = -1.5708
    c: Equal(g0,g1)
    c: Horizontal(g2)
    c: Coincident(g0,g-1)
    c: DistanceX(g3,g3) = 27
    c: DistanceY(g0,g0) = 7.2
    c: Diameter(g4) = 3.4
    c: Equal(g4,g5)
    c: Coincident(g4,g0)
    c: Coincident(g5,g1)
FEATURE [PartDesign::Pad] Pad009
  Direction = (0,0,1)
  Length = 3.5
  Length2 = 10
  Profile = -> Sketch020
  ReferenceAxis = -> Sketch020 [N_Axis]
  Type = 0
  expr: Length = <<gripperdims>>.link_height
FEATURE [Sketcher::SketchObject] Sketch021
  FullyConstrained = true
  MapMode = 5
  Support = -> [XY_Plane008]
  expr: Constraints[26] = <<gripperdims>>.servo_holder_moving_hole_diameter
  sketch-geometry (11):
    g0: ArcOfCircle CenterX=0 CenterY=0 CenterZ=0 NormalX=0 NormalY=0 NormalZ=1 AngleXU=0 Radius=4.5 StartAngle=0.891123 EndAngle=2.25047
    g1: Circle CenterX=0 CenterY=0 CenterZ=0 NormalX=0 NormalY=0 NormalZ=1 AngleXU=0 Radius=1.6
    g2: LineSegment StartX=11.5 StartY=3.5 StartZ=0 EndX=2.82843 EndY=3.5 EndZ=0
    g3: LineSegment StartX=-11.5 StartY=-3.5 StartZ=0 EndX=-2.82843 EndY=-3.5 EndZ=0
    g4: ArcOfCircle CenterX=11.5 CenterY=1e-16 CenterZ=0 NormalX=0 NormalY=0 NormalZ=1 AngleXU=0 Radius=3.5 StartAngle=4.71239 EndAngle=7.85398
    g5: ArcOfCircle CenterX=-11.5 CenterY=1.752e-12 CenterZ=0 NormalX=0 NormalY=0 NormalZ=1 AngleXU=0 Radius=3.5 StartAngle=1.5708 EndAngle=4.71239
    g6: LineSegment StartX=-2.82843 StartY=3.5 StartZ=0 EndX=-11.5 EndY=3.5 EndZ=0
    g7: LineSegment StartX=2.82843 StartY=-3.5 StartZ=0 EndX=11.5 EndY=-3.5 EndZ=0
    g8: ArcOfCircle CenterX=0 CenterY=0 CenterZ=0 NormalX=0 NormalY=0 NormalZ=1 AngleXU=0 Radius=4.5 StartAngle=4.03272 EndAngle=5.39206
    g9: Circle CenterX=-11.5 CenterY=1.752e-12 CenterZ=0 NormalX=0 NormalY=0 NormalZ=1 AngleXU=0 Radius=1.7
    g10: Circle CenterX=11.5 CenterY=1e-16 CenterZ=0 NormalX=0 NormalY=0 NormalZ=1 AngleXU=0 Radius=1.7
  constraints (28):
    c: Diameter(g0) = 9
    c: Coincident(g1,g0)
    c: Diameter(g1) = 3.2
    c: DistanceX(g6,g2) = 23
    c: Symmetric(g6,g2,g-2)
    c: Horizontal(g3)
    c: Vertical(g3,g6)
    c: Symmetric(g2,g7,g-1)
    c: DistanceY(g3,g6) = 7
    c: Coincident(g4,g2)
    c: Coincident(g5,g6)
    c: Tangent(g3,g5) = -1.5708
    c: Coincident(g8,g7)
    c: Coincident(g0,g2)
    c: Equal(g0,g8)
    c: Coincident(g0,g6)
    c: Coincident(g8,g3)
    c: Coincident(g0,g8)
    c: Horizontal(g0,g0)
    c: Horizontal(g6)
    c: Horizontal(g7)
    c: Horizontal(g7,g3)
    c: Coincident(g0,g-1)
    c: Tangent(g7,g4) = -1.5708
    c: Coincident(g9,g5)
    c: Coincident(g10,g4)
    c: Diameter(g9) = 3.4
    c: Equal(g9,g10)
FEATURE [PartDesign::Pad] Pad010
  Direction = (0,0,1)
  Length = 3
  Length2 = 10
  Profile = -> Sketch021
  ReferenceAxis = -> Sketch021 [N_Axis]
  Reversed = true
  Type = 0
FEATURE [Sketcher::SketchObject] Sketch022
  FullyConstrained = true
  MapMode = 5
  Support = -> [XY_Plane008]
  sketch-geometry (2):
    g0: Circle CenterX=0 CenterY=0 CenterZ=0 NormalX=0 NormalY=0 NormalZ=1 AngleXU=0 Radius=4.5
    g1: Circle CenterX=0 CenterY=0 CenterZ=0 NormalX=0 NormalY=0 NormalZ=1 AngleXU=0 Radius=1.6
  constraints (4):
    c: Coincident(g0,g-1)
    c: Diameter(g0) = 9
    c: Coincident(g1,g0)
    c: Diameter(g1) = 3.2
FEATURE [PartDesign::Pad] Pad011
  BaseFeature = -> Pad010
  Direction = (0,0,1)
  Length = 6
  Length2 = 10
  Profile = -> Sketch022
  ReferenceAxis = -> Sketch022 [N_Axis]
  Reversed = true
  Type = 0
FEATURE [Part::Part2DObjectPython] InvoluteGear  # Draft 2D object (typed FeaturePython)
  ExternalGear = true
  HighPrecision = true
  MapMode = 5
  Modules = 0.24
  NumberOfTeeth = 25
  Placement = pos=(0,0,-6) rot=(1,0,0;3.14159rad)
  PressureAngle = 35
  Support = -> [Pad011]
FEATURE [PartDesign::Pocket] Pocket011
  BaseFeature = -> Pad011
  Direction = (0,0,1)
  Length = 3
  Length2 = 5
  Profile = -> InvoluteGear
  ReferenceAxis = -> InvoluteGear [N_Axis]
  Type = 0
FEATURE [Sketcher::SketchObject] Sketch023
  FullyConstrained = true
  MapMode = 5
  Support = -> [Pocket011]
  expr: Constraints[1] = <<gripperdims>>.horn_screw_head_diameter
  sketch-geometry (1):
    g0: Circle CenterX=0 CenterY=0 CenterZ=0 NormalX=0 NormalY=0 NormalZ=1 AngleXU=0 Radius=3
  constraints (2):
    c: Coincident(g0,g-1)
    c: Diameter(g0) = 6
FEATURE [PartDesign::Pocket] Pocket012
  BaseFeature = -> Pocket011
  Direction = (0,0,-1)
  Length = 1
  Length2 = 5
  Profile = -> Sketch023
  ReferenceAxis = -> Sketch023 [N_Axis]
  Type = 0
  expr: Length = <<gripperdims>>.horn_screw_inlay_depth
FEATURE [Sketcher::SketchObject] Sketch024
  FullyConstrained = true
  MapMode = 5
  Placement = pos=(0,0,5) rot=(1,0,0;3.14159rad)
  Support = -> [Pad002]
  expr: Constraints[17] = <<gripperdims>>.servo_holder_height - <<gripperdims>>.servo_holder_hole_top_distance - <<gripperdims>>.servo_holder_rodcasing_overhang
  expr: Constraints[37] = <<gripperdims>>.servo_holder_width - 2 * <<gripperdims>>.servo_holder_hole_side_distance
  sketch-geometry (14):
    g0: LineSegment StartX=-9.5 StartY=68.8 StartZ=0 EndX=-12.5311 EndY=67.05 EndZ=0
    g1: LineSegment StartX=-12.5311 StartY=67.05 StartZ=0 EndX=-12.5311 EndY=63.55 EndZ=0
    g2: LineSegment StartX=-12.5311 StartY=63.55 StartZ=0 EndX=-9.5 EndY=61.8 EndZ=0
    g3: LineSegment StartX=-9.5 StartY=61.8 StartZ=0 EndX=-6.46891 EndY=63.55 EndZ=0
    g4: LineSegment StartX=-6.46891 StartY=63.55 StartZ=0 EndX=-6.46891 EndY=67.05 EndZ=0
    g5: LineSegment StartX=-6.46891 StartY=67.05 StartZ=0 EndX=-9.5 EndY=68.8 EndZ=0
    g6: Circle CenterX=-9.5 CenterY=65.3 CenterZ=0 NormalX=0 NormalY=0 NormalZ=1 AngleXU=0 Radius=3.5
    g7: LineSegment StartX=12.5311 StartY=67.05 StartZ=0 EndX=9.5 EndY=68.8 EndZ=0
    g8: LineSegment StartX=9.5 StartY=68.8 StartZ=0 EndX=6.46891 EndY=67.05 EndZ=0
    g9: LineSegment StartX=6.46891 StartY=67.05 StartZ=0 EndX=6.46891 EndY=63.55 EndZ=0
    g10: LineSegment StartX=6.46891 StartY=63.55 StartZ=0 EndX=9.5 EndY=61.8 EndZ=0
    g11: LineSegment StartX=9.5 StartY=61.8 StartZ=0 EndX=12.5311 EndY=63.55 EndZ=0
    g12: LineSegment StartX=12.5311 StartY=63.55 StartZ=0 EndX=12.5311 EndY=67.05 EndZ=0
    g13: Circle CenterX=9.5 CenterY=65.3 CenterZ=0 NormalX=0 NormalY=0 NormalZ=1 AngleXU=0 Radius=3.5
  constraints (33):
    c: Coincident(g0,g1)
    c: Coincident(g1,g2)
    c: Coincident(g2,g3)
    c: Coincident(g3,g4)
    c: Coincident(g4,g5)
    c: Coincident(g5,g0)
    c: Equal(g0, g1-g5) x5
    c: PointOnObject(g0,g6)
    c: PointOnObject(g1,g6)
    c: PointOnObject(g2,g6)
    c: PointOnObject(g3,g6)
    c: PointOnObject(g4,g6)
    c: PointOnObject(g5,g6)
    c: DistanceY(g-1,g6) = 65.3
    c: Diameter(g6) = 7
    c: Coincident(g7,g8)
    c: Coincident(g8,g9)
    c: Coincident(g9,g10)
    c: Coincident(g10,g11)
    c: Coincident(g11,g12)
    c: Coincident(g12,g7)
    c: Equal(g7, g8-g12) x5
    c: PointOnObject(g7,g13)
    c: PointOnObject(g8,g13)
    c: PointOnObject(g9,g13)
    c: PointOnObject(g10,g13)
    c: PointOnObject(g11,g13)
    c: PointOnObject(g12,g13)
    c: Equal(g6,g13)
    c: DistanceX(g6,g13) = 19
    c: Symmetric(g6,g13,g-2)
    c: Vertical(g1)
    c: Vertical(g12)
FEATURE [PartDesign::Pocket] Pocket013
  BaseFeature = -> Pad002
  Direction = (0,0,1)
  Length = 5
  Length2 = 5
  Profile = -> Sketch024
  ReferenceAxis = -> Sketch024 [N_Axis]
  Reversed = true
  Type = 0
  expr: Length = <<gripperdims>>.servo_holder_rodcasing_layer
FEATURE [Part::Part2DObjectPython] ShapeString  label="Servo holder version"  # Draft 2D object (typed FeaturePython)
  AttachmentOffset = pos=(7,15,0) rot=(0,0,1;3.14159rad)
  FontFile = <path>
  MakeFace = true
  MapMode = 5
  Placement = pos=(7,-15,-6) rot=(0,-1,0;3.14159rad)
  Size = 5
  String = v1.1
  Support = -> [Pocket013]
  Tracking = 0
FEATURE [Spreadsheet::Sheet] Spreadsheet001  label="global settings"
  cells = A1=Label text depth; B1(label_text_depth)==0.4mm; A2=Label font size; B2(label_font_size)==5mm; A3=Font file; B3(font_file)=<path>; A4=M3 static hole; B4(m3_static_hole)==3.2mm; A5=Nema 17 hole distance; B5(nema17_hole_distance)==31mm; A6=Nema 17 motor size; B6(nema17_motor_size)==44mm; A7=Limit switch hole distance; B7(limit_switch_hole_distance)==9.5mm; A8=Wirehole diameter; B8(wirehole_diameter)==5mm; A9=Tightener hole width; B9(tightenerhole_width)==5mm; A10=Tightener hole length; B10(tightenerhole_length)==12mm; A11=Medium tightener hole length; B11(medium_tightenerhole_length)==10mm; A12=Small tightener hole length; B12(small_tightenerhole_length)==4mm; A13=M3 nut width; B13(m3_nut_width)==7.2mm; A14=M3 nut height; B14(m3_nut_height)==3.6mm
FEATURE [PartDesign::Pocket] Pocket014  label="Version number for servo holder"
  BaseFeature = -> Pocket013
  Direction = (0,0,1)
  Length = 0.4
  Length2 = 5
  Profile = -> ShapeString
  ReferenceAxis = -> ShapeString [N_Axis]
  Type = 0
  expr: Length = <<global settings>>.label_text_depth
FEATURE [Part::Part2DObjectPython] ShapeString001  # Draft 2D object (typed FeaturePython)
  AttachmentOffset = pos=(8,31,0) rot=(0,0,1;3.14159rad)
  FontFile = <userpath>/FreeCAD/Font/ARLRDBD.TTF
  MakeFace = true
  MapMode = 5
  Placement = pos=(8,-31,-2.5) rot=(0,-1,0;3.14159rad)
  Size = 5
  String = v1.0
  Support = -> [Pocket007]
  Tracking = 0
  expr: Size = <<global settings>>.label_font_size
FEATURE [PartDesign::Pocket] Pocket015
  BaseFeature = -> Pocket007
  Direction = (0,0,1)
  Length = 0.4
  Length2 = 5
  Profile = -> ShapeString001
  ReferenceAxis = -> ShapeString001 [N_Axis]
  Type = 0
  expr: Length = <<global settings>>.label_text_depth
FEATURE [PartDesign::Body] Body001  label="Servo cover"
  Group = -> [Sketch008,Pad003,Sketch009,Pocket005,Sketch010,Pocket006,Sketch011,Pad004,Sketch012,Pocket007,ShapeString001,Pocket015]
  Origin = -> Origin002
  Placement = pos=(0,0,22.5) rot=(0,0,1;0rad)
  Tip = -> Pocket015
  expr: .Placement.Base.z = <<gripperdims>>.servo_holder_rodcasing_layer * 2 + <<gripperdims>>.cover_height
FEATURE [Part::Part2DObjectPython] ShapeString002  # Draft 2D object (typed FeaturePython)
  AttachmentOffset = pos=(10,23,0) rot=(0,0,1;1.5708rad)
  FontFile = <userpath>/FreeCAD/Font/ARLRDBD.TTF
  MakeFace = true
  MapMode = 5
  Placement = pos=(10,23,18) rot=(0,0,1;1.5708rad)
  Size = 5
  String = v1.0
  Support = -> [Chamfer001]
  Tracking = 0
  expr: Size = <<global settings>>.label_font_size
FEATURE [PartDesign::Pocket] Pocket016
  BaseFeature = -> Chamfer001
  Direction = (0,0,-1)
  Length = 0.4
  Length2 = 5
  Profile = -> ShapeString002
  ReferenceAxis = -> ShapeString002 [N_Axis]
  Type = 0
  expr: Length = <<global settings>>.label_text_depth
FEATURE [PartDesign::Body] Body002  label="right slider"
  BaseFeature = -> Box
  Group = -> [BaseFeature,Sketch013,Pocket008,Sketch014,Pocket009,Sketch015,Pad005,Sketch016,Pocket010,Sketch017,Pad006,Sketch018,Pad007,Chamfer,Chamfer001,ShapeString002,Pocket016]
  Origin = -> Origin003
  Placement = pos=(39,-65,0) rot=(0,0,1;0rad)
  Tip = -> Pocket016
  expr: .Placement.Base.y = -<<gripperdims>>.slider_length / 2 - <<gripperdims>>.servo_holder_axis_top_offset - <<gripperdims>>.servo_holder_axis_distance / 2
  expr: .Placement.Base.z = <<gripperdims>>.servo_holder_rodcasing_cutin - <<gripperdims>>.slider_height / 2
FEATURE [Part::Mirroring] Part__Mirroring  label="left slider"
  Base = (0,0,0)
  Normal = (1,0,0)
  Source = -> Body002
FEATURE [Part::Part2DObjectPython] ShapeString003  # Draft 2D object (typed FeaturePython)
  AttachmentOffset = pos=(16,-28,0) rot=(0,0,1;3.14159rad)
  FontFile = <userpath>/FreeCAD/Font/ARLRDBD.TTF
  MakeFace = true
  MapMode = 5
  Placement = pos=(16,28,0) rot=(0,-1,0;3.14159rad)
  Size = 5
  String = v1.0
  Support = -> [Pad008]
  Tracking = 0
  expr: Size = <<global settings>>.label_font_size
FEATURE [PartDesign::Pocket] Pocket017
  BaseFeature = -> Pad008
  Direction = (0,0,1)
  Length = 0.4
  Length2 = 5
  Profile = -> ShapeString003
  ReferenceAxis = -> ShapeString003 [N_Axis]
  Type = 0
  expr: Length = <<global settings>>.label_text_depth
FEATURE [PartDesign::Body] Body003  label="right top gripper hand"
  Group = -> [Sketch019,Pad008,ShapeString003,Pocket017]
  Origin = -> Origin006
  Placement = pos=(39,-65,18) rot=(0,0,1;0rad)
  Tip = -> Pocket017
  expr: .Placement.Base.y = -<<gripperdims>>.slider_length / 2 - <<gripperdims>>.servo_holder_axis_top_offset - <<gripperdims>>.servo_holder_axis_distance / 2
  expr: .Placement.Base.z = <<gripperdims>>.slider_height
FEATURE [Part::Mirroring] Part__Mirroring001  label="left top gripper hand"
  Base = (0,0,0)
  Normal = (1,0,0)
  Source = -> Body003
FEATURE [Part::Mirroring] Part__Mirroring002  label="right bottom gripper hand"
  Base = (0,0,9)
  Normal = (0,0,1)
  Source = -> Body003
  expr: .Base.z = <<gripperdims>>.slider_height / 2
FEATURE [Part::Mirroring] Part__Mirroring003  label="left bottom gripper hand"
  Base = (0,0,9)
  Normal = (0,0,1)
  Source = -> Part__Mirroring001
  expr: .Base.z = <<gripperdims>>.slider_height / 2
FEATURE [Part::Part2DObjectPython] ShapeString004  # Draft 2D object (typed FeaturePython)
  AttachmentOffset = pos=(20,2,0) rot=(0,0,1;3.14159rad)
  FontFile = <userpath>/FreeCAD/Font/ARLRDBD.TTF
  MakeFace = true
  MapMode = 5
  Placement = pos=(20,-2,0) rot=(0,-1,0;3.14159rad)
  Size = 5
  String = v1.0
  Support = -> [Pad009]
  Tracking = 0
  expr: Size = <<global settings>>.label_font_size
FEATURE [PartDesign::Pocket] Pocket018
  BaseFeature = -> Pad009
  Direction = (0,0,1)
  Length = 0.4
  Length2 = 5
  Profile = -> ShapeString004
  ReferenceAxis = -> ShapeString004 [N_Axis]
  Type = 0
  expr: Length = <<global settings>>.label_text_depth
FEATURE [PartDesign::Body] Body004  label="link"
  Group = -> [Sketch020,Pad009,ShapeString004,Pocket018]
  Origin = -> Origin007
  Tip = -> Pocket018
FEATURE [Part::Part2DObjectPython] ShapeString005  # Draft 2D object (typed FeaturePython)
  AttachmentOffset = pos=(-9,-2,0) rot=(0,0,1;0rad)
  FontFile = <userpath>/FreeCAD/Font/ARLRDBD.TTF
  MakeFace = true
  MapMode = 5
  Placement = pos=(-9,2,-3) rot=(1,0,0;3.14159rad)
  Size = 5
  String = 1
  Support = -> [Pocket012]
  Tracking = 0
  expr: Size = <<global settings>>.label_font_size
FEATURE [PartDesign::Pocket] Pocket019
  BaseFeature = -> Pocket012
  Direction = (0,0,1)
  Length = 0.4
  Length2 = 5
  Profile = -> ShapeString005
  ReferenceAxis = -> ShapeString005 [N_Axis]
  Type = 0
  expr: Length = <<global settings>>.label_text_depth
FEATURE [PartDesign::Body] Body005  label="horn"
  Group = -> [Sketch021,InvoluteGear,Pad010,Sketch022,Pad011,Pocket011,Sketch023,Pocket012,ShapeString005,Pocket019]
  Origin = -> Origin008
  Tip = -> Pocket019
FEATURE [Part::Box] Box001  label="Cube001"
  AttacherType = Attacher::AttachEngine3D
  Height = 18
  Length = 22
  Width = 20
  expr: Height = <<gripperdims>>.slider_height
  expr: Length = <<gripperdims>>.sliderbody_depth
  expr: Width = <<gripperdims>>.sliderbody_width
FEATURE [PartDesign::FeatureBase] BaseFeature001
  BaseFeature = -> Box001
FEATURE [Sketcher::SketchObject] Sketch025
  FullyConstrained = true
  MapMode = 5
  Placement = pos=(0,0,18) rot=(0,0,1;0rad)
  Support = -> [BaseFeature001]
  expr: Constraints[0] = <<gripperdims>>.sliderbody_hole_sidedistance
  expr: Constraints[11] = <<gripperdims>>.sliderbody_alternate_hole_distance
  expr: Constraints[3] = <<gripperdims>>.gripper_hole_distance
  expr: Constraints[4] = (<<gripperdims>>.gripper_height - <<gripperdims>>.gripper_hole_distance) / 2
  expr: Constraints[5] = <<gripperdims>>.mg996r_holediameter
  sketch-geometry (4):
    g0: Circle CenterX=10 CenterY=15 CenterZ=0 NormalX=0 NormalY=0 NormalZ=1 AngleXU=0 Radius=1.6
    g1: Circle CenterX=10 CenterY=5 CenterZ=0 NormalX=0 NormalY=0 NormalZ=1 AngleXU=0 Radius=1.6
    g2: Circle CenterX=18 CenterY=5 CenterZ=0 NormalX=0 NormalY=0 NormalZ=1 AngleXU=0 Radius=1.6
    g3: Circle CenterX=18 CenterY=15 CenterZ=0 NormalX=0 NormalY=0 NormalZ=1 AngleXU=0 Radius=1.6
  constraints (12):
    c: DistanceX(g-1,g1) = 10
    c: Equal(g1,g0)
    c: Vertical(g1,g0)
    c: DistanceY(g1,g0) = 10
    c: DistanceY(g-1,g1) = 5
    c: Diameter(g1) = 3.2
    c: Equal(g1,g2)
    c: Equal(g2,g3)
    c: Horizontal(g1,g2)
    c: Horizontal(g0,g3)
    c: Vertical(g3,g2)
    c: DistanceX(g1,g2) = 8
FEATURE [PartDesign::Pocket] Pocket020
  BaseFeature = -> BaseFeature001
  Direction = (0,0,-1)
  Length = 5
  Length2 = 5
  Profile = -> Sketch025
  ReferenceAxis = -> Sketch025 [N_Axis]
  Type = 1
FEATURE [Sketcher::SketchObject] Sketch026
  FullyConstrained = true
  MapMode = 5
  Placement = pos=(0,0,0) rot=(0.57735,-0.57735,-0.57735;2.0944rad)
  Support = -> [Pocket020]
  expr: Constraints[10] = <<gripperdims>>.sliderbody_width
  expr: Constraints[8] = <<gripperdims>>.slider_height
  sketch-geometry (4):
    g0: LineSegment StartX=0 StartY=0 StartZ=0 EndX=-20 EndY=0 EndZ=0
    g1: LineSegment StartX=-20 StartY=0 StartZ=0 EndX=-20 EndY=18 EndZ=0
    g2: LineSegment StartX=-20 StartY=18 StartZ=0 EndX=0 EndY=18 EndZ=0
    g3: LineSegment StartX=0 StartY=18 StartZ=0 EndX=0 EndY=0 EndZ=0
  constraints (11):
    c: Coincident(g0,g1)
    c: Coincident(g1,g2)
    c: Coincident(g2,g3)
    c: Coincident(g3,g0)
    c: Horizontal(g0)
    c: Horizontal(g2)
    c: Vertical(g1)
    c: Vertical(g3)
    c: DistanceY(g3,g3) = 18
    c: Coincident(g0,g-1)
    c: DistanceX(g2,g2) = 20
FEATURE [Sketcher::SketchObject] Sketch027
  AttachmentOffset = pos=(0,0,7.5) rot=(0,0,1;0rad)
  FullyConstrained = true
  MapMode = 5
  Placement = pos=(-7.5,0,0) rot=(0.57735,-0.57735,-0.57735;2.0944rad)
  Support = -> [Pocket020]
  expr: .AttachmentOffset.Base.z = <<gripperdims>>.sliderbody_hammer_thickness
  expr: Constraints[10] = <<gripperdims>>.slider_height + <<gripperdims>>.sliderbody_hammer_fanout
  expr: Constraints[11] = <<gripperdims>>.sliderbody_width + <<gripperdims>>.sliderbody_hammer_fanout
  expr: Constraints[8] = <<gripperdims>>.sliderbody_hammer_fanout
  expr: Constraints[9] = <<gripperdims>>.sliderbody_hammer_fanout
  sketch-geometry (4):
    g0: LineSegment StartX=3.5 StartY=-3.5 StartZ=0 EndX=-23.5 EndY=-3.5 EndZ=0
    g1: LineSegment StartX=-23.5 StartY=-3.5 StartZ=0 EndX=-23.5 EndY=21.5 EndZ=0
    g2: LineSegment StartX=-23.5 StartY=21.5 StartZ=0 EndX=3.5 EndY=21.5 EndZ=0
    g3: LineSegment StartX=3.5 StartY=21.5 StartZ=0 EndX=3.5 EndY=-3.5 EndZ=0
  constraints (12):
    c: Coincident(g0,g1)
    c: Coincident(g1,g2)
    c: Coincident(g2,g3)
    c: Coincident(g3,g0)
    c: Horizontal(g0)
    c: Horizontal(g2)
    c: Vertical(g1)
    c: Vertical(g3)
    c: DistanceY(g0,g-1) = 3.5
    c: DistanceX(g-1,g0) = 3.5
    c: DistanceY(g-1,g2) = 21.5
    c: DistanceX(g0,g-1) = 23.5
FEATURE [Sketcher::SketchObject] Sketch028
  AttachmentOffset = pos=(0,0,8.5) rot=(0,0,1;0rad)
  FullyConstrained = true
  MapMode = 5
  Placement = pos=(-8.5,0,0) rot=(0.57735,-0.57735,-0.57735;2.0944rad)
  Support = -> [Pocket020]
  expr: .AttachmentOffset.Base.z = <<gripperdims>>.sliderbody_hammer_thickness + <<gripperdims>>.sliderbody_hammer_plate
  expr: Constraints[10] = <<gripperdims>>.slider_height + <<gripperdims>>.sliderbody_hammer_fanout
  expr: Constraints[11] = <<gripperdims>>.sliderbody_width + <<gripperdims>>.sliderbody_hammer_fanout
  expr: Constraints[8] = <<gripperdims>>.sliderbody_hammer_fanout
  expr: Constraints[9] = <<gripperdims>>.sliderbody_hammer_fanout
  sketch-geometry (4):
    g0: LineSegment StartX=3.5 StartY=-3.5 StartZ=0 EndX=-23.5 EndY=-3.5 EndZ=0
    g1: LineSegment StartX=-23.5 StartY=-3.5 StartZ=0 EndX=-23.5 EndY=21.5 EndZ=0
    g2: LineSegment StartX=-23.5 StartY=21.5 StartZ=0 EndX=3.5 EndY=21.5 EndZ=0
    g3: LineSegment StartX=3.5 StartY=21.5 StartZ=0 EndX=3.5 EndY=-3.5 EndZ=0
  constraints (12):
    c: Coincident(g0,g1)
    c: Coincident(g1,g2)
    c: Coincident(g2,g3)
    c: Coincident(g3,g0)
    c: Horizontal(g0)
    c: Horizontal(g2)
    c: Vertical(g1)
    c: Vertical(g3)
    c: DistanceY(g0,g-1) = 3.5
    c: DistanceX(g-1,g0) = 3.5
    c: DistanceY(g-1,g2) = 21.5
    c: DistanceX(g0,g-1) = 23.5
FEATURE [PartDesign::AdditiveLoft] AdditiveLoft
  BaseFeature = -> Pocket020
  Closed = false
  Profile = -> Sketch026
  Ruled = true
  Sections = -> [Sketch027,Sketch028]
FEATURE [Part::Part2DObjectPython] ShapeString006  # Draft 2D object (typed FeaturePython)
  AttachmentOffset = pos=(-2,13,0) rot=(0,0,1;3.14159rad)
  FontFile = <userpath>/FreeCAD/Font/ARLRDBD.TTF
  MakeFace = true
  MapMode = 5
  Placement = pos=(2,20,13) rot=(1,0,0;4.71239rad)
  Size = 5
  String = v1.0
  Support = -> [AdditiveLoft]
  Tracking = 0
  expr: Size = <<global settings>>.label_font_size
FEATURE [PartDesign::Pocket] Pocket021
  BaseFeature = -> AdditiveLoft
  Direction = (0,-1,2e-16)
  Length = 0.4
  Length2 = 5
  Profile = -> ShapeString006
  ReferenceAxis = -> ShapeString006 [N_Axis]
  Type = 0
  expr: Length = <<global settings>>.label_text_depth
FEATURE [PartDesign::Body] Body006  label="sliderbody right"
  BaseFeature = -> Box001
  Group = -> [BaseFeature001,Sketch025,Pocket020,Sketch026,Sketch027,AdditiveLoft,Sketch028,ShapeString006,Pocket021]
  Origin = -> Origin009
  Placement = pos=(37,-110,0) rot=(0,0,1;0rad)
  Tip = -> Pocket021
FEATURE [Part::Mirroring] Part__Mirroring004  label="sliderbody left"
  Base = (0,0,0)
  Normal = (1,0,0)
  Source = -> Body006
FEATURE [App::Part] Part001  label="Arm 2"
  Group = -> [Part__Feature104,Part__Feature105,Part__Feature107,Part__Feature108,Part__Feature109,Part__Feature110,Part__Feature111,Part__Feature112,Part__Feature091,Part__Feature092,Part__Feature093,Part__Feature146,Part__Feature115,Part__Feature113,Part__Feature160,Part__Feature161,Part__Feature162,Part__Feature163]
  Origin = -> Origin010
FEATURE [App::Part] Part002  label="Arm 1"
  Group = -> [Part__Feature136,Part__Feature088,Part__Feature090,Part__Feature094,Part__Feature145,Part__Feature096,Part__Feature095,Part__Feature152,Part__Feature153,Part__Feature154,Part__Feature155,Part__Feature144,Part__Feature150,Part__Feature089,Part__Feature151,Part__Feature099,Part__Feature087,Part__Feature100,Part__Feature101,Part__Feature102,Part__Feature103,Part__Feature097,Part__Feature116,+2 more]
  Origin = -> Origin011
FEATURE [App::Part] Part003  label="Vertical base"
  Group = -> [Part__Feature139,Part__Feature071,Part__Feature072,Part__Feature073,Part__Feature074,Part__Feature084,Part__Feature086,Part__Feature079,Part__Feature080,Part__Feature081,Part__Feature082,Part__Feature083,Part__Feature137,Part__Feature138,Part__Feature075,Part__Feature076,Part__Feature077,Part__Feature078,Part__Feature070,Part__Feature069,Part__Feature064,Part__Feature085,Part__Feature156,+3 more]
  Origin = -> Origin012
FEATURE [Sketcher::SketchObject] Sketch029
  FullyConstrained = true
  MapMode = 5
  Placement = pos=(0,0,0) rot=(0.57735,0.57735,0.57735;2.0944rad)
  Support = -> [YZ_Plane001]
  expr: Constraints[13] = <<gripperdims>>.mg996r_center_length
  expr: Constraints[15] = <<gripperdims>>.mg996r_center_height
  expr: Constraints[17] = <<gripperdims>>.servo_holder_thickness
  expr: Constraints[8] = <<gripperdims>>.servo_holder_top_skirt
  expr: Constraints[9] = <<gripperdims>>.mg996r_height
  sketch-geometry (6):
    g0: LineSegment StartX=-65.05 StartY=-4.5 StartZ=0 EndX=-65.05 EndY=-6 EndZ=0
    g1: LineSegment StartX=-65.05 StartY=-6 StartZ=0 EndX=-72.05 EndY=-6 EndZ=0
    g2: LineSegment StartX=-72.05 StartY=-6 StartZ=0 EndX=-65.05 EndY=-4.5 EndZ=0
    g3: LineSegment StartX=-24.75 StartY=-4.5 StartZ=0 EndX=-17.75 EndY=-6 EndZ=0
    g4: LineSegment StartX=-17.75 StartY=-6 StartZ=0 EndX=-24.75 EndY=-6 EndZ=0
    g5: LineSegment StartX=-24.75 StartY=-6 StartZ=0 EndX=-24.75 EndY=-4.5 EndZ=0
  constraints (18):
    c: Coincident(g0,g1)
    c: Coincident(g1,g2)
    c: Horizontal(g1)
    c: Vertical(g0)
    c: Coincident(g3,g4)
    c: Coincident(g4,g5)
    c: Horizontal(g4)
    c: Vertical(g5)
    c: DistanceX(g4,g-1) = 24.75
    c: DistanceX(g0,g4) = 40.3
    c: Coincident(g2,g0)
    c: Coincident(g3,g5)
    c: Equal(g0,g5)
    c: DistanceX(g1,g1) = 7
    c: Equal(g1,g4)
    c: DistanceY(g0,g0) = 1.5
    c: Horizontal(g0,g4)
    c: DistanceY(g3,g-1) = 6
FEATURE [PartDesign::Pocket] Pocket022
  BaseFeature = -> Pocket014
  Direction = (-1,2e-16,-3e-16)
  Length = 1.5
  Length2 = 5
  Midplane = true
  Profile = -> Sketch029
  ReferenceAxis = -> Sketch029 [N_Axis]
  Type = 0
  expr: Length = <<gripperdims>>.mg996r_center_thickness
FEATURE [PartDesign::Body] Body  label="Servo Holder"
  Group = -> [Sketch,Pad,Sketch001,Pad001,Sketch002,Pocket,Sketch003,Sketch004,Pocket001,Pocket002,Sketch005,Pocket003,Sketch006,Pocket004,Sketch007,Pad002,Sketch024,Pocket013,ShapeString,Pocket014,Sketch029,Pocket022]
  Origin = -> Origin001
  Tip = -> Pocket022
FEATURE [App::Part] Part004  label="Base"
  Group = -> [Part__Feature,Part__Feature060,Part__Feature061,Part__Feature062,Part__Feature063,Part__Feature065,Part__Feature066,Part__Feature067,Part__Feature068,Part__Feature114,Part__Feature142,Part__Feature143,Part__Feature147,Part__Feature148,Part__Feature149,Part__Feature164,Part__Feature165,Part__Feature166,Part__Feature167]
  Origin = -> Origin013
FEATURE [App::Part] SCARA_Robot_3D_Model  label="SCARA Robot 3D Model"
  Group = -> [Gripper_Mechanism_Gripper_Mechanism,Part__Feature140,Part__Feature141,Part__Feature168,Part__Feature169,Part001,Part002,Part003,Part004]
  Origin = -> Origin005
FEATURE [Spreadsheet::Sheet] Spreadsheet002  label="arm2 dims"
  cells = A1=Gripper coupler; B1=diameter; C1(grippercoupler_diameter)==78mm; B2=number of connector holes; C2(grippercoupler_num_connector_holes)=10; B3=connector hole diameter; C3(grippercoupler_connector_hole_diameter)==4.2mm; B4=connector holeset diameter; C4(grippercoupler_connector_holeset_diameter)==65.40000000000001mm; B5=thickness; C5(grippercoupler_thickness)==7mm; B6=notch diameter; C6(grippercoupler_notch_diameter)==9.1mm; B7=notch center offset; C7(grippercoupler_notch_center_offset)==35.4mm; B8=bearing outer diameter; C8(grippercoupler_bearing_outer_diameter)==53mm; B9=bearing inner diameter; C9(grippercoupler_bearing_inner_diameter)==35mm; B10=bearing holder wall thickness; C10(grippercoupler_bearing_holder_wall_thickness)==2mm; B11=bearing holder wall height; C11(grippercoupler_bearing_holder_wall_height)==10.5mm; B12=bulge width; C12(grippercoupler_bulge_width)==6mm; B13=bulge distance; C13(grippercoupler_bulge_distance)==33.5mm; B14=bearing holder inner height; C14(grippercoupler_bearing_holder_inner_height)==1mm; B15=axl house diameter; C15(grippercoupler_axl_house_diameter)==30mm; B16=axl house height; C16(grippercoupler_axl_house_height)==15mm; B17=axl house inner diameter; C17(grippercoupler_axl_house_inner_diameter)==12.5mm; B18=axl hole diameter; C18(grippercoupler_axl_hole_diameter)==3.6mm; B19=number of axl holes; C19(grippercoupler_number_of_axl_holes)=4; B20=axl holeset diameter; C20(grippercoupler_axl_holeset_diameter)==22mm; A21=arm 1 coupler; B21=diameter; C21(arm1_coupler_diameter)==78mm; B22=wall thickness; C22(arm1_coupler_wall_thickness)==2mm; B23=height; C23(arm1_coupler_height)==18.5mm; B24=wall height; C24(arm1_coupler_wall_height)==7.5mm; B25=bearing diameter; C25(arm1_coupler_bearing_diameter)==53mm; B26=bearing inner diameter; C26(arm1_coupler_bearing_inner_diameter)==35mm; B27=bearing height; C27(arm1_coupler_bearing_height)==4mm; B28=axl house diameter; C28(arm1_coupler_axl_house_diameter)==30mm; B29=axl house inner diameter; C29(arm1_coupler_axl_house_inner_diameter)==12.5mm; B30=axl house height; C30(arm1_coupler_axl_house_height)==12mm; B31=number of connector holes; C31(arm1_coupler_number_of_connector_holes)=6; B32=connector nut diameter; C32(arm1_coupler_connector_nut_diameter)==8.4mm; B33=connector holeset diameter; C33(arm1_coupler_connector_holeset_diameter)==63mm; B34=connector hole diameter; C34(arm1_coupler_connector_hole_diameter)==4.2mm; B35=connector nut depth; C35(arm1_coupler_connector_nut_depth)==2.5mm; B36=axl hole diameter; C36(arm1_coupler_axl_hole_diameter)==3.6mm; B37=number of axl holes; C37(arm1_coupler_number_of_axl_holes)=4; B38=axl holeset diameter; C38(arm1_coupler_axl_holeset_diameter)==22mm; B39=stopper length; C39(arm1_coupler_stopper_length)==4mm; B40=stopper width; C40(arm1_coupler_stopper_width)==8mm; A41=cover; B41=length; C41(cover_length)==144mm; B42=width; C42(cover_width)==78mm; B43=thickness; C43(cover_thickness)==8mm; B44=coupler hole diameter; C44(cover_coupler_hole_diameter)==35mm; B45=arm1 hole diameter; C45(cover_arm1_hole_diameter)==25mm; B46=coupler bearing diameter; C46(cover_coupler_bearing_diameter)==42mm; B47=coupler bearing height; C47(cover_coupler_bearing_height)==7mm; B48=hole distance; C48(cover_hole_distance)==63mm; B49=hole separation; C49(cover_hole_separation)==60mm; B50=arm1 hole offset; C50(cover_arm1_hole_offset)==6mm; B51=coupler hole offset; C51(cover_coupler_hole_offset)==7.5mm; B52=limithole2 horiz offset; C52(cover_forward_limithole_horiz)==96mm; B53=limithole2 vert offset; C53(cover_forward_limithole_vert)==5mm; B54=limit switch angle; C54(cover_limitswitch_angle)==28deg; B55=wirehole horiz offset; C55(cover_wirehole_horiz_offset)==84.5mm; B56=wirehole vert offset; C56(cover_wirehole_vert_offset)==6mm; B57=tightenerhole horiz offset; C57(cover_tightenerhole_horiz_offset)==70mm; B58=tightenerhole vert offset; C58(cover_tightenerhole_vert_offset)==13mm; B59=cablehole horiz offset; C59(cover_cablehole_horiz_offset)==25mm; A60=body; B60=height; C60(body_height)==31mm; B61=wall thickness; C61(body_wall_thickness)==3.75mm; B62=bottom thickness; C62(body_bottom_thickness)==6mm; B63=guide diameter; C63(body_guide_diameter)==10.1mm; B64=guide separation; C64(body_guide_separation)==3.5mm; B65=guide hole depth; C65(body_guide_hole_depth)==25mm; B66=arm1 hole; C66(body_arm1_hole)==34mm; B67=arm1 holeset diameter; C67(body_arm1_holeset_diameter)==62.5mm; B68=arm1 connector hole diameter; C68(body_arm1_connector_hole_diameter)==4.1mm; B69=arm1 num connector holes; C69(body_arm1_num_connector_holes)=6; B70=hook width; C70(body_hook_width)==4.5mm; B71=hook1 position; C71(body_hook1_position)==21.5mm; B72=hook2 position; C72(body_hook2_position)==70.5mm; B73=hook3 position; C73(body_hook3_position)==116.5mm; B74=hook4 position; C74(body_hook4_position)==134.5mm; B75=nut height; C75(body_nut_height)==13mm; B76=nut width; C76(body_nut_width)==7.2mm; B77=nut side; C77(body_nut_side)==4.16mm; B78=nut depth; C78(body_nut_depth)==3.6mm
FEATURE [Sketcher::SketchObject] Sketch030
  FullyConstrained = true
  MapMode = 5
  Placement = pos=(0,0,0) rot=(0,0.707107,0.707107;3.14159rad)
  Support = -> [XZ_Plane015]
  expr: Constraints[18] = <<gripperdims>>.coupler_outerangle
  expr: Constraints[22] = <<arm2 dims>>.grippercoupler_diameter
  expr: Constraints[23] = <<gripperdims>>.coupler_straight_part
  expr: Constraints[25] = 360deg / <<arm2 dims>>.grippercoupler_num_connector_holes
  expr: Constraints[27] = <<arm2 dims>>.grippercoupler_connector_holeset_diameter
  expr: Constraints[31] = <<arm2 dims>>.grippercoupler_connector_hole_diameter
  sketch-geometry (13):
    g0: ArcOfCircle CenterX=0 CenterY=0 CenterZ=0 NormalX=0 NormalY=0 NormalZ=1 AngleXU=0 Radius=39 StartAngle=5.75959 EndAngle=6.80678
    g1: ArcOfCircle CenterX=0 CenterY=0 CenterZ=0 NormalX=0 NormalY=0 NormalZ=1 AngleXU=0 Radius=39 StartAngle=2.61799 EndAngle=3.66519
    g2: LineSegment StartX=-19.9186 StartY=11.5 StartZ=0 EndX=19.9186 EndY=11.5 EndZ=0
    g3: LineSegment StartX=19.9186 StartY=-11.5 StartZ=0 EndX=-19.9186 EndY=-11.5 EndZ=0
    g4: LineSegment StartX=-33.775 StartY=-19.5 StartZ=0 EndX=-19.9186 EndY=-11.5 EndZ=0
    g5: LineSegment StartX=-33.775 StartY=19.5 StartZ=0 EndX=-19.9186 EndY=11.5 EndZ=0
    g6: LineSegment StartX=33.775 StartY=19.5 StartZ=0 EndX=19.9186 EndY=11.5 EndZ=0
    g7: LineSegment StartX=33.775 StartY=-19.5 StartZ=0 EndX=19.9186 EndY=-11.5 EndZ=0
    g8: Circle CenterX=-31.0995 CenterY=10.1049 CenterZ=0 NormalX=0 NormalY=0 NormalZ=1 AngleXU=0 Radius=2.1
    g9: ArcOfCircle CenterX=0 CenterY=0 CenterZ=0 NormalX=0 NormalY=0 NormalZ=1 AngleXU=0 Radius=32.7 StartAngle=2.82743 EndAngle=3.45575
    g10: Circle CenterX=-31.0995 CenterY=-10.1049 CenterZ=0 NormalX=0 NormalY=0 NormalZ=1 AngleXU=0 Radius=2.1
    g11: Circle CenterX=31.0995 CenterY=10.1049 CenterZ=0 NormalX=0 NormalY=0 NormalZ=1 AngleXU=0 Radius=2.1
    g12: Circle CenterX=31.0995 CenterY=-10.1049 CenterZ=0 NormalX=0 NormalY=0 NormalZ=1 AngleXU=0 Radius=2.1
  constraints (36):
    c: Coincident(g0,g-1)
    c: Coincident(g1,g0)
    c: Horizontal(g2)
    c: Horizontal(g3)
    c: Coincident(g4,g1)
    c: Coincident(g4,g3)
    c: Coincident(g5,g1)
    c: Coincident(g5,g2)
    c: Coincident(g6,g0)
    c: Coincident(g6,g2)
    c: Coincident(g7,g0)
    c: Coincident(g7,g3)
    c: PointOnObject(g0,g5)
    c: PointOnObject(g0,g6)
    c: PointOnObject(g0,g7)
    c: PointOnObject(g0,g4)
    c: Vertical(g2,g3)
    c: Vertical(g2,g3)
    c: Angle(g1) = 1.0472
    c: Vertical(g1,g1)
    c: Horizontal(g1,g0)
    c: Equal(g1,g0)
    c: Diameter(g1) = 78
    c: Distance(g5) = 16
    c: Coincident(g9,g0)
    c: Angle(g9) = 0.628319
    c: Vertical(g9,g9)
    c: Diameter(g9) = 65.4
    c: Coincident(g8,g9)
    c: Coincident(g10,g9)
    c: Equal(g10,g8)
    c: Diameter(g10) = 4.2
    c: Equal(g12,g11)
    c: Equal(g11,g10)
    c: Symmetric(g11,g8,g-2)
    c: Symmetric(g12,g10,g-2)
FEATURE [PartDesign::Pad] Pad012
  Direction = (0,1,2e-16)
  Length = 4.5
  Length2 = 10
  Placement = pos=(0,0,0) rot=(1,0,0;1.5708rad)
  Profile = -> Sketch030
  ReferenceAxis = -> Sketch030 [N_Axis]
  Type = 0
  expr: Length = <<gripperdims>>.coupler_thickness
FEATURE [Sketcher::SketchObject] Sketch031
  FullyConstrained = false
  MapMode = 5
  Placement = pos=(0,4.5,0) rot=(-1,0,0;1.5708rad)
  Support = -> [Pad012]
  sketch-geometry (4):
    g0: Circle CenterX=18.5 CenterY=-3.5 CenterZ=0 NormalX=0 NormalY=0 NormalZ=1 AngleXU=0 Radius=1
    g1: Circle CenterX=18.5 CenterY=3.5 CenterZ=0 NormalX=0 NormalY=0 NormalZ=1 AngleXU=0 Radius=1
    g2: Circle CenterX=-18.5 CenterY=3.5 CenterZ=0 NormalX=0 NormalY=0 NormalZ=1 AngleXU=0 Radius=1
    g3: Circle CenterX=-18.5 CenterY=-3.5 CenterZ=0 NormalX=0 NormalY=0 NormalZ=1 AngleXU=0 Radius=1
  constraints (7):
    c: Symmetric(g1,g0,g-1)
    c: Symmetric(g2,g3,g-1)
    c: Symmetric(g2,g1,g-2)
    c: Equal(g2,g3)
    c: Equal(g3,g1)
    c: Equal(g1,g0)
    c: Diameter(g0) = 2
FEATURE [PartDesign::Hole] Hole
  BaseFeature = -> Pad012
  CustomThreadClearance = 0
  Depth = 25
  DepthType = 0
  Diameter = 3.4
  DrillForDepth = false
  DrillPoint = 1
  DrillPointAngle = 118
  HoleCutCountersinkAngle = 90
  HoleCutCustomValues = false
  HoleCutDepth = 0
  HoleCutDiameter = 6.7
  HoleCutType = 7
  ModelThread = false
  Placement = pos=(0,0,0) rot=(1,0,0;1.5708rad)
  Profile = -> Sketch031
  Tapered = false
  TaperedAngle = 90
  ThreadClass = 0
  ThreadDepth = 25
  ThreadDepthType = 0
  ThreadDirection = 0
  ThreadFit = 0
  ThreadSize = 9
  ThreadType = 1
  Threaded = false
  UseCustomThreadClearance = false
FEATURE [Part::Part2DObjectPython] ShapeString007  # Draft 2D object (typed FeaturePython)
  AttachmentOffset = pos=(-5,-3,0) rot=(0,0,1;0rad)
  FontFile = <userpath>/FreeCAD/Font/ARLRDBD.TTF
  MakeFace = true
  MapMode = 5
  Placement = pos=(-5,4.5,3) rot=(-1,0,0;1.5708rad)
  Size = 5
  String = v1.0
  Support = -> [Hole]
  Tracking = 0
  expr: Size = <<global settings>>.label_font_size
FEATURE [PartDesign::Pocket] Pocket023
  BaseFeature = -> Hole
  Direction = (0,-1,-2e-16)
  Length = 0.4
  Length2 = 5
  Placement = pos=(0,0,0) rot=(1,0,0;1.5708rad)
  Profile = -> ShapeString007
  ReferenceAxis = -> ShapeString007 [N_Axis]
  Type = 0
  expr: Length = <<global settings>>.label_text_depth
FEATURE [PartDesign::Body] Body007  label="coupler"
  Group = -> [Sketch030,Pad012,Sketch031,Hole,ShapeString007,Pocket023]
  Origin = -> Origin015
  Placement = pos=(0,0,10) rot=(0,0,1;0rad)
  Tip = -> Pocket023
  expr: .Placement.Base.z = <<gripperdims>>.servo_holder_rodcasing_layer * 2
FEATURE [App::Part] Part  label="Gripper mechanism"
  Group = -> [Spreadsheet,Body,Body001,Cylinder,Cylinder001,Box,Body002,Part__Mirroring,Body003,Part__Mirroring001,Part__Mirroring003,Part__Mirroring002,Body004,Body005,Box001,Body006,Part__Mirroring004,Part__Feature059,Body007]
  Origin = -> Origin
FEATURE [Sketcher::SketchObject] Sketch032
  FullyConstrained = true
  MapMode = 5
  Placement = pos=(0,0,0) rot=(1,0,0;1.5708rad)
  Support = -> [XZ_Plane016]
  expr: Constraints[10] = <<arm2 dims>>.arm1_coupler_stopper_width
  expr: Constraints[11] = <<arm2 dims>>.arm1_coupler_stopper_length
  expr: Constraints[1] = <<arm2 dims>>.arm1_coupler_diameter
  sketch-geometry (4):
    g0: ArcOfCircle CenterX=0 CenterY=0 CenterZ=0 NormalX=0 NormalY=0 NormalZ=1 AngleXU=0 Radius=39 StartAngle=0.102745 EndAngle=6.18044
    g1: LineSegment StartX=38.7943 StartY=4 StartZ=0 EndX=42.7943 EndY=4 EndZ=0
    g2: LineSegment StartX=42.7943 StartY=-4 StartZ=0 EndX=38.7943 EndY=-4 EndZ=0
    g3: ArcOfCircle CenterX=42.7943 CenterY=2e-16 CenterZ=0 NormalX=0 NormalY=0 NormalZ=1 AngleXU=0 Radius=4 StartAngle=4.71239 EndAngle=7.85398
  constraints (13):
    c: Coincident(g0,g-1)
    c: Diameter(g0) = 78
    c: Horizontal(g1)
    c: Horizontal(g2)
    c: Symmetric(g1,g2,g-1)
    c: Coincident(g0,g2)
    c: Coincident(g0,g1)
    c: Coincident(g3,g1)
    c: Coincident(g3,g2)
    c: Vertical(g1,g2)
    c: Diameter(g3) = 8
    c: DistanceX(g2,g2) = 4
    c: Vertical(g3,g1)
FEATURE [PartDesign::Pad] Pad013
  Direction = (0,-1,-2e-16)
  Length = 18.5
  Length2 = 10
  Placement = pos=(0,0,0) rot=(1,0,0;1.5708rad)
  Profile = -> Sketch032
  ReferenceAxis = -> Sketch032 [N_Axis]
  Type = 0
  expr: Length = <<arm2 dims>>.arm1_coupler_height
FEATURE [Sketcher::SketchObject] Sketch033
  FullyConstrained = true
  MapMode = 5
  Placement = pos=(0,-18.5,0) rot=(1,0,0;1.5708rad)
  Support = -> [Pad013]
  expr: Constraints[1] = <<arm2 dims>>.arm1_coupler_diameter - <<arm2 dims>>.arm1_coupler_wall_thickness * 2
  sketch-geometry (1):
    g0: Circle CenterX=0 CenterY=0 CenterZ=0 NormalX=0 NormalY=0 NormalZ=1 AngleXU=0 Radius=37
  constraints (2):
    c: Coincident(g0,g-1)
    c: Diameter(g0) = 74
FEATURE [PartDesign::Pocket] Pocket024
  BaseFeature = -> Pad013
  Direction = (0,1,2e-16)
  Length = 7.5
  Length2 = 5
  Placement = pos=(0,0,0) rot=(1,0,0;1.5708rad)
  Profile = -> Sketch033
  ReferenceAxis = -> Sketch033 [N_Axis]
  Type = 0
  expr: Length = <<arm2 dims>>.arm1_coupler_wall_height
FEATURE [Sketcher::SketchObject] Sketch034
  FullyConstrained = true
  MapMode = 5
  Placement = pos=(0,-11,0) rot=(1,0,0;1.5708rad)
  Support = -> [Pocket024]
  expr: Constraints[1] = <<arm2 dims>>.arm1_coupler_bearing_inner_diameter
  expr: Constraints[3] = <<arm2 dims>>.arm1_coupler_bearing_diameter
  sketch-geometry (2):
    g0: Circle CenterX=0 CenterY=0 CenterZ=0 NormalX=0 NormalY=0 NormalZ=1 AngleXU=0 Radius=17.5
    g1: Circle CenterX=0 CenterY=0 CenterZ=0 NormalX=0 NormalY=0 NormalZ=1 AngleXU=0 Radius=26.5
  constraints (4):
    c: Coincident(g0,g-1)
    c: Diameter(g0) = 35
    c: Coincident(g0,g1)
    c: Diameter(g1) = 53
FEATURE [PartDesign::Pocket] Pocket025
  BaseFeature = -> Pocket024
  Direction = (0,1,2e-16)
  Length = 4
  Length2 = 5
  Placement = pos=(0,0,0) rot=(1,0,0;1.5708rad)
  Profile = -> Sketch034
  ReferenceAxis = -> Sketch034 [N_Axis]
  Type = 0
  expr: Length = <<arm2 dims>>.arm1_coupler_bearing_height
FEATURE [Sketcher::SketchObject] Sketch035
  FullyConstrained = true
  MapMode = 5
  Placement = pos=(0,-11,0) rot=(1,0,0;1.5708rad)
  Support = -> [Pocket025]
  expr: Constraints[1] = <<arm2 dims>>.arm1_coupler_axl_house_diameter
  sketch-geometry (1):
    g0: Circle CenterX=0 CenterY=0 CenterZ=0 NormalX=0 NormalY=0 NormalZ=1 AngleXU=0 Radius=15
  constraints (2):
    c: Coincident(g0,g-1)
    c: Diameter(g0) = 30
FEATURE [PartDesign::Pad] Pad014
  BaseFeature = -> Pocket025
  Direction = (0,-1,-2e-16)
  Length = 12
  Length2 = 10
  Placement = pos=(0,0,0) rot=(1,0,0;1.5708rad)
  Profile = -> Sketch035
  ReferenceAxis = -> Sketch035 [N_Axis]
  Type = 0
  expr: Length = <<arm2 dims>>.arm1_coupler_axl_house_height
FEATURE [Sketcher::SketchObject] Sketch036
  FullyConstrained = true
  MapMode = 5
  Placement = pos=(0,-23,-1.1e-15) rot=(1,0,0;1.5708rad)
  Support = -> [Pad014]
  expr: Constraints[1] = <<arm2 dims>>.arm1_coupler_axl_house_inner_diameter
  sketch-geometry (1):
    g0: Circle CenterX=0 CenterY=0 CenterZ=0 NormalX=0 NormalY=0 NormalZ=1 AngleXU=0 Radius=6.25
  constraints (2):
    c: Coincident(g0,g-1)
    c: Diameter(g0) = 12.5
FEATURE [PartDesign::Pocket] Pocket026
  BaseFeature = -> Pad014
  Direction = (0,1,2e-16)
  Length = 5
  Length2 = 5
  Placement = pos=(0,0,0) rot=(1,0,0;1.5708rad)
  Profile = -> Sketch036
  ReferenceAxis = -> Sketch036 [N_Axis]
  Type = 1
FEATURE [Sketcher::SketchObject] Sketch037
  FullyConstrained = true
  MapMode = 5
  Placement = pos=(0,-11,0) rot=(1,0,0;1.5708rad)
  Support = -> [Pocket026]
  expr: Constraints[1] = <<arm2 dims>>.arm1_coupler_connector_holeset_diameter / 2
  expr: Constraints[2] = <<arm2 dims>>.arm1_coupler_connector_hole_diameter
  sketch-geometry (1):
    g0: Circle CenterX=0 CenterY=31.5 CenterZ=0 NormalX=0 NormalY=0 NormalZ=1 AngleXU=0 Radius=2.1
  constraints (3):
    c: Vertical(g0,g-1)
    c: DistanceY(g-1,g0) = 31.5
    c: Diameter(g0) = 4.2
FEATURE [PartDesign::Pocket] Pocket027
  BaseFeature = -> Pocket026
  Direction = (0,1,2e-16)
  Length = 5
  Length2 = 5
  Placement = pos=(0,0,0) rot=(1,0,0;1.5708rad)
  Profile = -> Sketch037
  ReferenceAxis = -> Sketch037 [N_Axis]
  Type = 1
FEATURE [Sketcher::SketchObject] Sketch038
  FullyConstrained = true
  MapMode = 5
  Placement = pos=(0,-11,0) rot=(1,0,0;1.5708rad)
  Support = -> [Pocket027]
  expr: Constraints[18] = <<arm2 dims>>.arm1_coupler_connector_holeset_diameter / 2
  expr: Constraints[19] = <<arm2 dims>>.arm1_coupler_connector_nut_diameter
  sketch-geometry (7):
    g0: LineSegment StartX=-2.1 StartY=35.1373 StartZ=0 EndX=-4.2 EndY=31.5 EndZ=0
    g1: LineSegment StartX=-4.2 StartY=31.5 StartZ=0 EndX=-2.1 EndY=27.8627 EndZ=0
    g2: LineSegment StartX=-2.1 StartY=27.8627 StartZ=0 EndX=2.1 EndY=27.8627 EndZ=0
    g3: LineSegment StartX=2.1 StartY=27.8627 StartZ=0 EndX=4.2 EndY=31.5 EndZ=0
    g4: LineSegment StartX=4.2 StartY=31.5 StartZ=0 EndX=2.1 EndY=35.1373 EndZ=0
    g5: LineSegment StartX=2.1 StartY=35.1373 StartZ=0 EndX=-2.1 EndY=35.1373 EndZ=0
    g6: Circle CenterX=0 CenterY=31.5 CenterZ=0 NormalX=0 NormalY=0 NormalZ=1 AngleXU=0 Radius=4.2
  constraints (17):
    c: Coincident(g0,g1)
    c: Coincident(g1,g2)
    c: Coincident(g2,g3)
    c: Coincident(g3,g4)
    c: Coincident(g4,g5)
    c: Coincident(g5,g0)
    c: Equal(g0, g1-g5) x5
    c: PointOnObject(g0,g6)
    c: PointOnObject(g1,g6)
    c: PointOnObject(g2,g6)
    c: PointOnObject(g3,g6)
    c: PointOnObject(g4,g6)
    c: PointOnObject(g5,g6)
    c: Vertical(g6,g-1)
    c: DistanceY(g-1,g6) = 31.5
    c: Diameter(g6) = 8.4
    c: Horizontal(g5)
FEATURE [PartDesign::Pocket] Pocket028
  BaseFeature = -> Pocket027
  Direction = (0,1,2e-16)
  Length = 2.5
  Length2 = 5
  Placement = pos=(0,0,0) rot=(1,0,0;1.5708rad)
  Profile = -> Sketch038
  ReferenceAxis = -> Sketch038 [N_Axis]
  Type = 0
  expr: Length = <<arm2 dims>>.arm1_coupler_connector_nut_depth
FEATURE [PartDesign::PolarPattern] PolarPattern
  Angle = 360
  Axis = -> Sketch038 [N_Axis]
  BaseFeature = -> Pocket028
  Occurrences = 6
  Originals = -> [Pocket028,Pocket027]
  Overlap = 0
  Placement = pos=(0,0,0) rot=(1,0,0;1.5708rad)
  expr: Occurrences = <<arm2 dims>>.arm1_coupler_number_of_connector_holes
FEATURE [Sketcher::SketchObject] Sketch039
  FullyConstrained = true
  MapMode = 5
  Placement = pos=(0,0,0) rot=(-1,0,0;1.5708rad)
  Support = -> [PolarPattern]
  expr: Constraints[1] = <<arm2 dims>>.arm1_coupler_axl_holeset_diameter / 2
  expr: Constraints[2] = <<arm2 dims>>.arm1_coupler_axl_hole_diameter
  sketch-geometry (1):
    g0: Circle CenterX=0 CenterY=11 CenterZ=0 NormalX=0 NormalY=0 NormalZ=1 AngleXU=0 Radius=1.8
  constraints (3):
    c: Vertical(g-1,g0)
    c: DistanceY(g-1,g0) = 11
    c: Diameter(g0) = 3.6
FEATURE [PartDesign::Hole] Hole001
  BaseFeature = -> PolarPattern
  CustomThreadClearance = 0
  Depth = 25
  DepthType = 0
  Diameter = 4.5
  DrillForDepth = false
  DrillPoint = 1
  DrillPointAngle = 118
  HoleCutCountersinkAngle = 90
  HoleCutCustomValues = false
  HoleCutDepth = 0
  HoleCutDiameter = 9
  HoleCutType = 7
  ModelThread = false
  Placement = pos=(0,0,0) rot=(1,0,0;1.5708rad)
  Profile = -> Sketch039
  Tapered = false
  TaperedAngle = 90
  ThreadClass = 0
  ThreadDepth = 25
  ThreadDepthType = 0
  ThreadDirection = 0
  ThreadFit = 0
  ThreadSize = 11
  ThreadType = 1
  Threaded = false
  UseCustomThreadClearance = false
FEATURE [PartDesign::PolarPattern] PolarPattern001
  Angle = 360
  Axis = -> Sketch039 [N_Axis]
  BaseFeature = -> Hole001
  Occurrences = 4
  Originals = -> [Hole001]
  Overlap = 0
  Placement = pos=(0,0,0) rot=(1,0,0;1.5708rad)
  expr: Occurrences = <<arm2 dims>>.arm1_coupler_number_of_axl_holes
FEATURE [Part::Part2DObjectPython] ShapeString008  # Draft 2D object (typed FeaturePython)
  AttachmentOffset = pos=(-6,20,0) rot=(0,0,1;0rad)
  FontFile = <userpath>/FreeCAD/Font/ARLRDBD.TTF
  MakeFace = true
  MapMode = 5
  Placement = pos=(-6,4.4e-15,-20) rot=(-1,0,0;1.5708rad)
  Size = 5
  String = v1.0
  Support = -> [PolarPattern001]
  Tracking = 0
  expr: Size = <<global settings>>.label_font_size
FEATURE [PartDesign::Pocket] Pocket029
  BaseFeature = -> PolarPattern001
  Direction = (0,-1,-2e-16)
  Length = 0.4
  Length2 = 5
  Placement = pos=(0,0,0) rot=(1,0,0;1.5708rad)
  Profile = -> ShapeString008
  ReferenceAxis = -> ShapeString008 [N_Axis]
  Type = 0
  expr: Length = <<global settings>>.label_text_depth
FEATURE [PartDesign::Body] Body008  label="arm1 arm2 coupler"
  Group = -> [Sketch032,Pad013,Sketch033,Pocket024,Sketch034,Pocket025,Sketch035,Pad014,Sketch036,Pocket026,Sketch037,Pocket027,Sketch038,Pocket028,PolarPattern,Sketch039,Hole001,PolarPattern001,ShapeString008,Pocket029]
  Origin = -> Origin016
  Tip = -> Pocket029
FEATURE [Sketcher::SketchObject] Sketch040
  FullyConstrained = true
  MapMode = 5
  Placement = pos=(0,0,0) rot=(1,0,0;1.5708rad)
  Support = -> [XZ_Plane017]
  expr: Constraints[11] = <<arm2 dims>>.cover_arm1_hole_offset
  expr: Constraints[12] = <<arm2 dims>>.cover_coupler_hole_offset
  expr: Constraints[16] = <<global settings>>.m3_static_hole
  expr: Constraints[24] = <<global settings>>.nema17_hole_distance
  expr: Constraints[26] = <<global settings>>.nema17_hole_distance
  expr: Constraints[27] = <<arm2 dims>>.cover_forward_limithole_horiz
  expr: Constraints[28] = <<arm2 dims>>.cover_forward_limithole_vert
  expr: Constraints[29] = <<global settings>>.m3_static_hole
  expr: Constraints[31] = <<global settings>>.limit_switch_hole_distance
  expr: Constraints[34] = <<arm2 dims>>.cover_limitswitch_angle
  expr: Constraints[35] = <<global settings>>.wirehole_diameter
  expr: Constraints[36] = <<arm2 dims>>.cover_wirehole_horiz_offset
  expr: Constraints[37] = <<arm2 dims>>.cover_wirehole_vert_offset
  expr: Constraints[44] = <<global settings>>.tightenerhole_width
  expr: Constraints[45] = <<global settings>>.tightenerhole_length
  expr: Constraints[46] = <<arm2 dims>>.cover_tightenerhole_horiz_offset
  expr: Constraints[47] = <<arm2 dims>>.cover_tightenerhole_vert_offset
  expr: Constraints[65] = <<arm2 dims>>.cover_cablehole_horiz_offset
  expr: Constraints[6] = <<arm2 dims>>.cover_width
  expr: Constraints[7] = <<arm2 dims>>.cover_length
  expr: Constraints[8] = <<arm2 dims>>.cover_arm1_hole_diameter
  expr: Constraints[9] = <<arm2 dims>>.cover_coupler_hole_diameter
  sketch-geometry (26):
    g0: ArcOfCircle CenterX=0 CenterY=0 CenterZ=0 NormalX=0 NormalY=0 NormalZ=1 AngleXU=0 Radius=39 StartAngle=1.5708 EndAngle=4.71239
    g1: ArcOfCircle CenterX=144 CenterY=2.7e-15 CenterZ=0 NormalX=0 NormalY=0 NormalZ=1 AngleXU=0 Radius=39 StartAngle=4.71239 EndAngle=7.85398
    g2: LineSegment StartX=-7.2e-15 StartY=-39 StartZ=0 EndX=144 EndY=-39 EndZ=0
    g3: LineSegment StartX=144 StartY=39 StartZ=0 EndX=0 EndY=39 EndZ=0
    g4: Circle CenterX=-6 CenterY=0 CenterZ=0 NormalX=0 NormalY=0 NormalZ=1 AngleXU=0 Radius=12.5
    g5: Circle CenterX=136.5 CenterY=2.7e-15 CenterZ=0 NormalX=0 NormalY=0 NormalZ=1 AngleXU=0 Radius=17.5
    g6: Circle CenterX=-21.5 CenterY=15.5 CenterZ=0 NormalX=0 NormalY=0 NormalZ=1 AngleXU=0 Radius=1.6
    g7: Circle CenterX=9.5 CenterY=15.5 CenterZ=0 NormalX=0 NormalY=0 NormalZ=1 AngleXU=0 Radius=1.6
    g8: Circle CenterX=9.5 CenterY=-15.5 CenterZ=0 NormalX=0 NormalY=0 NormalZ=1 AngleXU=0 Radius=1.6
    g9: Circle CenterX=-21.5 CenterY=-15.5 CenterZ=0 NormalX=0 NormalY=0 NormalZ=1 AngleXU=0 Radius=1.6
    g10: Circle CenterX=96 CenterY=-5 CenterZ=0 NormalX=0 NormalY=0 NormalZ=1 AngleXU=0 Radius=1.6
    g11: Circle CenterX=87.612 CenterY=-9.45998 CenterZ=0 NormalX=0 NormalY=0 NormalZ=1 AngleXU=0 Radius=1.6
    g12: LineSegment StartX=87.612 StartY=-9.45998 StartZ=0 EndX=96 EndY=-5 EndZ=0
    g13: Circle CenterX=84.5 CenterY=6 CenterZ=0 NormalX=0 NormalY=0 NormalZ=1 AngleXU=0 Radius=2.5
    g14: ArcOfCircle CenterX=70 CenterY=-13 CenterZ=0 NormalX=0 NormalY=0 NormalZ=1 AngleXU=0 Radius=2.5 StartAngle=0 EndAngle=3.14159
    g15: ArcOfCircle CenterX=70 CenterY=-25 CenterZ=0 NormalX=0 NormalY=0 NormalZ=1 AngleXU=0 Radius=2.5 StartAngle=3.14159 EndAngle=6.28319
    g16: LineSegment StartX=67.5 StartY=-13 StartZ=0 EndX=67.5 EndY=-25 EndZ=0
    g17: LineSegment StartX=72.5 StartY=-25 StartZ=0 EndX=72.5 EndY=-13 EndZ=0
    g18: ArcOfCircle CenterX=70 CenterY=25 CenterZ=0 NormalX=0 NormalY=0 NormalZ=1 AngleXU=0 Radius=2.5 StartAngle=4e-16 EndAngle=3.14159
    g19: ArcOfCircle CenterX=70 CenterY=13 CenterZ=0 NormalX=0 NormalY=0 NormalZ=1 AngleXU=0 Radius=2.5 StartAngle=3.14159 EndAngle=6.28319
    g20: LineSegment StartX=67.5 StartY=25 StartZ=0 EndX=67.5 EndY=13 EndZ=0
    g21: LineSegment StartX=72.5 StartY=13 StartZ=0 EndX=72.5 EndY=25 EndZ=0
    g22: ArcOfCircle CenterX=25 CenterY=6 CenterZ=0 NormalX=0 NormalY=0 NormalZ=1 AngleXU=0 Radius=2.5 StartAngle=0 EndAngle=3.14159
    g23: ArcOfCircle CenterX=25 CenterY=-6 CenterZ=0 NormalX=0 NormalY=0 NormalZ=1 AngleXU=0 Radius=2.5 StartAngle=3.14159 EndAngle=6.28319
    g24: LineSegment StartX=22.5 StartY=6 StartZ=0 EndX=22.5 EndY=-6 EndZ=0
    g25: LineSegment StartX=27.5 StartY=-6 StartZ=0 EndX=27.5 EndY=6 EndZ=0
  constraints (66):
    c: Tangent(g0,g2) = -1.5708
    c: Tangent(g2,g1) = -1.5708
    c: Tangent(g3,g0) = -1.5708
    c: Equal(g0,g1)
    c: Horizontal(g2)
    c: Coincident(g0,g-1)
    c: Diameter(g0) = 78
    c: DistanceX(g3,g3) = 144
    c: Diameter(g4) = 25
    c: Diameter(g5) = 35
    c: Horizontal(g4,g0)
    c: DistanceX(g4,g0) = 6
    c: DistanceX(g5,g1) = 7.5
    c: Coincident(g3,g1)
    c: Vertical(g1,g1)
    c: Horizontal(g1,g5)
    c: Diameter(g8) = 3.2
    c: Equal(g8,g9)
    c: Equal(g9,g6)
    c: Equal(g6,g7)
    c: Symmetric(g8,g6,g4)
    c: Vertical(g7,g8)
    c: Horizontal(g9,g8)
    c: Vertical(g9,g6)
    c: DistanceX(g9,g8) = 31
    c: Horizontal(g6,g7)
    c: DistanceY(g9,g6) = 31
    c: DistanceX(g0,g10) = 96
    c: DistanceY(g10,g0) = 5
    c: Diameter(g10) = 3.2
    c: Equal(g11,g10)
    c: Distance(g11,g10) = 9.5
    c: Coincident(g12,g11)
    c: Coincident(g12,g10)
    c: Angle(g-1,g12) = 0.488692
    c: Diameter(g13) = 5
    c: DistanceX(g0,g13) = 84.5
    c: DistanceY(g0,g13) = 6
    c: Tangent(g14,g16) = -1.5708
    c: Tangent(g16,g15) = -1.5708
    c: Tangent(g15,g17) = -1.5708
    c: Tangent(g17,g14) = -1.5708
    c: Equal(g14,g15)
    c: Vertical(g16)
    c: Diameter(g15) = 5
    c: DistanceY(g17,g17) = 12
    c: DistanceX(g0,g15) = 70
    c: DistanceY(g14,g0) = 13
    c: Tangent(g18,g20) = -1.5708
    c: Tangent(g20,g19) = -1.5708
    c: Tangent(g19,g21) = -1.5708
    c: Tangent(g21,g18) = -1.5708
    c: Equal(g18,g19)
    c: Vertical(g20)
    c: Equal(g19,g14)
    c: Equal(g16,g21)
    c: Symmetric(g19,g14,g-1)
    c: Tangent(g22,g24) = -1.5708
    c: Tangent(g24,g23) = -1.5708
    c: Tangent(g23,g25) = -1.5708
    c: Tangent(g25,g22) = -1.5708
    c: Equal(g22,g23)
    c: Equal(g25,g16)
    c: Equal(g23,g15)
    c: Symmetric(g23,g22,g-1)
    c: DistanceX(g0,g23) = 25
FEATURE [PartDesign::Pad] Pad015
  Direction = (0,-1,-2e-16)
  Length = 8
  Length2 = 10
  Placement = pos=(0,0,0) rot=(1,0,0;1.5708rad)
  Profile = -> Sketch040
  ReferenceAxis = -> Sketch040 [N_Axis]
  Type = 0
  expr: Length = <<arm2 dims>>.cover_thickness
FEATURE [Sketcher::SketchObject] Sketch041
  FullyConstrained = true
  MapMode = 5
  Placement = pos=(0,-8,0) rot=(1,0,0;1.5708rad)
  Support = -> [Pad015]
  expr: Constraints[0] = <<arm2 dims>>.cover_length - <<arm2 dims>>.cover_coupler_hole_offset
  expr: Constraints[2] = <<arm2 dims>>.cover_coupler_bearing_diameter
  sketch-geometry (1):
    g0: Circle CenterX=136.5 CenterY=0 CenterZ=0 NormalX=0 NormalY=0 NormalZ=1 AngleXU=0 Radius=21
  constraints (3):
    c: DistanceX(g-1,g0) = 136.5
    c: Horizontal(g-1,g0)
    c: Diameter(g0) = 42
FEATURE [PartDesign::Pocket] Pocket030
  BaseFeature = -> Pad015
  Direction = (0,1,2e-16)
  Length = 7
  Length2 = 5
  Placement = pos=(0,0,0) rot=(1,0,0;1.5708rad)
  Profile = -> Sketch041
  ReferenceAxis = -> Sketch041 [N_Axis]
  Type = 0
  expr: Length = <<arm2 dims>>.cover_coupler_bearing_height
FEATURE [Sketcher::SketchObject] Sketch042
  FullyConstrained = true
  MapMode = 5
  Placement = pos=(0,0,0) rot=(-1,0,0;1.5708rad)
  Support = -> [Pocket030]
  expr: Constraints[12] = <<arm2 dims>>.cover_length
  expr: Constraints[13] = <<arm2 dims>>.cover_hole_distance
  expr: Constraints[15] = <<arm2 dims>>.cover_hole_separation
  expr: Constraints[20] = <<arm2 dims>>.cover_hole_distance
  expr: Constraints[21] = <<arm2 dims>>.cover_length / 2 - <<arm2 dims>>.cover_hole_separation / 2
  sketch-geometry (14):
    g0: Circle CenterX=-15.75 CenterY=-27.2798 CenterZ=0 NormalX=0 NormalY=0 NormalZ=1 AngleXU=0 Radius=2
    g1: Circle CenterX=-31.5 CenterY=0 CenterZ=0 NormalX=0 NormalY=0 NormalZ=1 AngleXU=0 Radius=2
    g2: Circle CenterX=-15.75 CenterY=27.2798 CenterZ=0 NormalX=0 NormalY=0 NormalZ=1 AngleXU=0 Radius=2
    g3: Circle CenterX=42 CenterY=31.5 CenterZ=0 NormalX=0 NormalY=0 NormalZ=1 AngleXU=0 Radius=2
    g4: Circle CenterX=102 CenterY=31.5 CenterZ=0 NormalX=0 NormalY=0 NormalZ=1 AngleXU=0 Radius=2
    g5: Circle CenterX=42 CenterY=-31.5 CenterZ=0 NormalX=0 NormalY=0 NormalZ=1 AngleXU=0 Radius=2
    g6: Circle CenterX=102 CenterY=-31.5 CenterZ=0 NormalX=0 NormalY=0 NormalZ=1 AngleXU=0 Radius=2
    g7: Circle CenterX=159.75 CenterY=-27.2798 CenterZ=0 NormalX=0 NormalY=0 NormalZ=1 AngleXU=0 Radius=2
    g8: Circle CenterX=175.5 CenterY=0 CenterZ=0 NormalX=0 NormalY=0 NormalZ=1 AngleXU=0 Radius=2
    g9: Circle CenterX=159.75 CenterY=27.2798 CenterZ=0 NormalX=0 NormalY=0 NormalZ=1 AngleXU=0 Radius=2
    g10: Circle CenterX=144 CenterY=0 CenterZ=0 NormalX=0 NormalY=0 NormalZ=1 AngleXU=0 Radius=31.5
    g11: Circle CenterX=0 CenterY=0 CenterZ=0 NormalX=0 NormalY=0 NormalZ=1 AngleXU=0 Radius=31.5
    g12: LineSegment StartX=-15.75 StartY=27.2798 StartZ=0 EndX=0 EndY=0 EndZ=0
    g13: LineSegment StartX=159.75 StartY=27.2798 StartZ=0 EndX=144 EndY=0 EndZ=0
  constraints (36):
    c: Diameter(g0) = 4
    c: Equal(g0,g1)
    c: Equal(g1,g2)
    c: Equal(g2,g3)
    c: Equal(g3,g5)
    c: Equal(g5,g6)
    c: Equal(g6,g4)
    c: Equal(g4,g9)
    c: Equal(g9,g7)
    c: Equal(g7,g8)
    c: Coincident(g11,g-1)
    c: Horizontal(g10,g11)
    c: DistanceX(g11,g10) = 144
    c: Diameter(g11) = 63
    c: Equal(g11,g10)
    c: DistanceX(g5,g6) = 60
    c: Horizontal(g5,g6)
    c: Horizontal(g3,g4)
    c: Vertical(g4,g6)
    c: Symmetric(g3,g5,g-1)
    c: DistanceY(g5,g3) = 63
    c: DistanceX(g11,g5) = 42
    c: Horizontal(g1,g11)
    c: PointOnObject(g1,g11)
    c: PointOnObject(g8,g10)
    c: Horizontal(g8,g11)
    c: PointOnObject(g2,g11)
    c: Coincident(g12,g2)
    c: Coincident(g12,g11)
    c: Angle(g-1,g12) = 2.0944
    c: Symmetric(g0,g2,g-1)
    c: PointOnObject(g9,g10)
    c: Coincident(g13,g9)
    c: Coincident(g13,g10)
    c: Angle(g13,g-1) = 2.0944
    c: Symmetric(g9,g7,g-1)
FEATURE [PartDesign::Hole] Hole002
  BaseFeature = -> Pocket030
  CustomThreadClearance = 0
  Depth = 25
  DepthType = 0
  Diameter = 4.5
  DrillForDepth = false
  DrillPoint = 1
  DrillPointAngle = 118
  HoleCutCountersinkAngle = 90
  HoleCutCustomValues = false
  HoleCutDepth = 0
  HoleCutDiameter = 9
  HoleCutType = 7
  ModelThread = false
  Placement = pos=(0,0,0) rot=(1,0,0;1.5708rad)
  Profile = -> Sketch042
  Tapered = false
  TaperedAngle = 90
  ThreadClass = 0
  ThreadDepth = 25
  ThreadDepthType = 0
  ThreadDirection = 0
  ThreadFit = 0
  ThreadSize = 11
  ThreadType = 1
  Threaded = false
  UseCustomThreadClearance = false
FEATURE [Part::Feature] Part__Feature170  label="Arm 2 Cover_Arm 2 Cover001"
  Placement = pos=(144,0,0) rot=(1,0,0;3.14159rad)
  shape: bbox 222 x 8 x 78 mm, 82 faces (baked)
FEATURE [Part::Part2DObjectPython] ShapeString009  # Draft 2D object (typed FeaturePython)
  AttachmentOffset = pos=(53,-8,0) rot=(0,0,1;1.5708rad)
  FontFile = <userpath>/FreeCAD/Font/ARLRDBD.TTF
  MakeFace = true
  MapMode = 5
  Placement = pos=(53,-8,-8) rot=(0.57735,-0.57735,0.57735;2.0944rad)
  Size = 5
  String = v1.0
  Support = -> [Hole002]
  Tracking = 0
  expr: Size = <<global settings>>.label_font_size
FEATURE [PartDesign::Pocket] Pocket031
  BaseFeature = -> Hole002
  Direction = (0,1,2e-16)
  Length = 0.4
  Length2 = 5
  Placement = pos=(0,0,0) rot=(1,0,0;1.5708rad)
  Profile = -> ShapeString009
  ReferenceAxis = -> ShapeString009 [N_Axis]
  Type = 0
  expr: Length = <<global settings>>.label_text_depth
FEATURE [PartDesign::Body] Body009  label="arm2 cover"
  Group = -> [Sketch040,Pad015,Sketch041,Pocket030,Sketch042,Hole002,ShapeString009,Pocket031]
  Origin = -> Origin017
  Tip = -> Pocket031
FEATURE [Sketcher::SketchObject] Sketch045
  FullyConstrained = true
  MapMode = 5
  Support = -> [XY_Plane018]
  expr: Constraints[11] = <<arm2 dims>>.body_arm1_hole
  expr: Constraints[5] = <<arm2 dims>>.cover_width
  expr: Constraints[6] = <<arm2 dims>>.cover_length
  sketch-geometry (5):
    g0: ArcOfCircle CenterX=0 CenterY=0 CenterZ=0 NormalX=0 NormalY=0 NormalZ=1 AngleXU=0 Radius=39 StartAngle=1.5708 EndAngle=4.71239
    g1: ArcOfCircle CenterX=144 CenterY=-2.1e-15 CenterZ=0 NormalX=0 NormalY=0 NormalZ=1 AngleXU=0 Radius=39 StartAngle=4.71239 EndAngle=7.85398
    g2: LineSegment StartX=-7.2e-15 StartY=-39 StartZ=0 EndX=144 EndY=-39 EndZ=0
    g3: LineSegment StartX=144 StartY=39 StartZ=0 EndX=0 EndY=39 EndZ=0
    g4: Circle CenterX=0 CenterY=0 CenterZ=0 NormalX=0 NormalY=0 NormalZ=1 AngleXU=0 Radius=17
  constraints (12):
    c: Tangent(g0,g2) = -1.5708
    c: Tangent(g2,g1) = -1.5708
    c: Tangent(g3,g0) = -1.5708
    c: Equal(g0,g1)
    c: Horizontal(g2)
    c: Diameter(g0) = 78
    c: DistanceX(g3,g3) = 144
    c: Coincident(g3,g1)
    c: Vertical(g1,g1)
    c: Coincident(g0,g-1)
    c: Coincident(g4,g0)
    c: Diameter(g4) = 34
FEATURE [PartDesign::Pad] Pad016
  Direction = (0,0,1)
  Length = 31
  Length2 = 10
  Profile = -> Sketch045
  ReferenceAxis = -> Sketch045 [N_Axis]
  Type = 0
  expr: Length = <<arm2 dims>>.body_height
FEATURE [Sketcher::SketchObject] Sketch046
  AttachmentOffset = pos=(0,0,31) rot=(0,0,1;0rad)
  FullyConstrained = true
  MapMode = 5
  Placement = pos=(0,0,31) rot=(0,0,1;0rad)
  Support = -> [XY_Plane018]
  expr: .AttachmentOffset.Base.z = <<arm2 dims>>.body_height
  expr: Constraints[14] = <<arm2 dims>>.cover_hole_distance
  expr: Constraints[18] = <<arm2 dims>>.body_guide_diameter
  expr: Constraints[49] = <<arm2 dims>>.cover_length / 2 - <<arm2 dims>>.cover_hole_separation / 2
  expr: Constraints[4] = <<arm2 dims>>.cover_width - <<arm2 dims>>.body_wall_thickness * 2
  expr: Constraints[69] = <<arm2 dims>>.cover_hole_distance
  expr: Constraints[70] = <<arm2 dims>>.cover_hole_separation
  expr: Constraints[8] = <<arm2 dims>>.cover_length
  sketch-geometry (48):
    g0: LineSegment StartX=-1.987e-13 StartY=35.25 StartZ=0 EndX=36.95 EndY=35.25 EndZ=0
    g1: LineSegment StartX=-1.987e-13 StartY=-35.25 StartZ=0 EndX=36.95 EndY=-35.25 EndZ=0
    g2: ArcOfCircle CenterX=-1.987e-13 CenterY=0 CenterZ=0 NormalX=0 NormalY=0 NormalZ=1 AngleXU=0 Radius=35.25 StartAngle=1.5708 EndAngle=1.95064
    g3: ArcOfCircle CenterX=144 CenterY=0 CenterZ=0 NormalX=0 NormalY=0 NormalZ=1 AngleXU=0 Radius=35.25 StartAngle=4.71239 EndAngle=5.09223
    g4: Circle CenterX=-1.987e-13 CenterY=0 CenterZ=0 NormalX=0 NormalY=0 NormalZ=1 AngleXU=0 Radius=31.5
    g5: ArcOfCircle CenterX=-31.5 CenterY=0 CenterZ=0 NormalX=0 NormalY=0 NormalZ=1 AngleXU=0 Radius=5.05 StartAngle=4.71239 EndAngle=7.85398
    g6: LineSegment StartX=-31.5 StartY=5.05 StartZ=0 EndX=-34.8864 EndY=5.05 EndZ=0
    g7: LineSegment StartX=-31.5 StartY=-5.05 StartZ=0 EndX=-34.8864 EndY=-5.05 EndZ=0
    g8: ArcOfCircle CenterX=-1.987e-13 CenterY=0 CenterZ=0 NormalX=0 NormalY=0 NormalZ=1 AngleXU=0 Radius=35.25 StartAngle=3.28535 EndAngle=4.04503
    g9: LineSegment StartX=-1.987e-13 StartY=0 StartZ=0 EndX=-15.75 EndY=27.2798 EndZ=0
    g10: ArcOfCircle CenterX=-15.75 CenterY=27.2798 CenterZ=0 NormalX=0 NormalY=0 NormalZ=1 AngleXU=0 Radius=5.05 StartAngle=3.66519 EndAngle=6.80678
    g11: LineSegment StartX=-20.1234 StartY=24.7548 StartZ=0 EndX=-21.8166 EndY=27.6875 EndZ=0
    g12: LineSegment StartX=-11.3766 StartY=29.8048 StartZ=0 EndX=-13.0698 EndY=32.7375 EndZ=0
    g13: ArcOfCircle CenterX=-1.987e-13 CenterY=0 CenterZ=0 NormalX=0 NormalY=0 NormalZ=1 AngleXU=0 Radius=35.25 StartAngle=2.23815 EndAngle=2.99784
    g14: ArcOfCircle CenterX=-15.75 CenterY=-27.2798 CenterZ=0 NormalX=0 NormalY=0 NormalZ=1 AngleXU=0 Radius=5.05 StartAngle=5.75959 EndAngle=8.90118
    g15: LineSegment StartX=-20.1234 StartY=-24.7548 StartZ=0 EndX=-21.8166 EndY=-27.6875 EndZ=0
    g16: LineSegment StartX=-11.3766 StartY=-29.8048 StartZ=0 EndX=-13.0698 EndY=-32.7375 EndZ=0
    g17: ArcOfCircle CenterX=-1.987e-13 CenterY=0 CenterZ=0 NormalX=0 NormalY=0 NormalZ=1 AngleXU=0 Radius=35.25 StartAngle=4.33255 EndAngle=4.71239
    g18: ArcOfCircle CenterX=42 CenterY=-31.5 CenterZ=0 NormalX=0 NormalY=0 NormalZ=1 AngleXU=0 Radius=5.05 StartAngle=0 EndAngle=3.14159
    g19: ArcOfCircle CenterX=42 CenterY=31.5 CenterZ=0 NormalX=0 NormalY=0 NormalZ=1 AngleXU=0 Radius=5.05 StartAngle=3.14159 EndAngle=6.28319
    g20: LineSegment StartX=36.95 StartY=-31.5 StartZ=0 EndX=36.95 EndY=-35.25 EndZ=0
    g21: LineSegment StartX=47.05 StartY=-31.5 StartZ=0 EndX=47.05 EndY=-35.25 EndZ=0
    g22: LineSegment StartX=47.05 StartY=31.5 StartZ=0 EndX=47.05 EndY=35.25 EndZ=0
    g23: LineSegment StartX=36.95 StartY=31.5 StartZ=0 EndX=36.95 EndY=35.25 EndZ=0
    g24: LineSegment StartX=47.05 StartY=35.25 StartZ=0 EndX=96.95 EndY=35.25 EndZ=0
    g25: LineSegment StartX=47.05 StartY=-35.25 StartZ=0 EndX=96.95 EndY=-35.25 EndZ=0
    g26: ArcOfCircle CenterX=102 CenterY=-31.5 CenterZ=0 NormalX=0 NormalY=0 NormalZ=1 AngleXU=0 Radius=5.05 StartAngle=0 EndAngle=3.14159
    g27: ArcOfCircle CenterX=102 CenterY=31.5 CenterZ=0 NormalX=0 NormalY=0 NormalZ=1 AngleXU=0 Radius=5.05 StartAngle=3.14159 EndAngle=6.28319
    g28: LineSegment StartX=96.95 StartY=31.5 StartZ=0 EndX=96.95 EndY=35.25 EndZ=0
    g29: LineSegment StartX=107.05 StartY=31.5 StartZ=0 EndX=107.05 EndY=35.25 EndZ=0
    g30: LineSegment StartX=107.05 StartY=-31.5 StartZ=0 EndX=107.05 EndY=-35.25 EndZ=0
    g31: LineSegment StartX=96.95 StartY=-31.5 StartZ=0 EndX=96.95 EndY=-35.25 EndZ=0
    g32: LineSegment StartX=107.05 StartY=-35.25 StartZ=0 EndX=144 EndY=-35.25 EndZ=0
    g33: LineSegment StartX=107.05 StartY=35.25 StartZ=0 EndX=144 EndY=35.25 EndZ=0
    g34: Circle CenterX=144 CenterY=0 CenterZ=0 NormalX=0 NormalY=0 NormalZ=1 AngleXU=0 Radius=31.5
    g35: ArcOfCircle CenterX=159.75 CenterY=27.2798 CenterZ=0 NormalX=0 NormalY=0 NormalZ=1 AngleXU=0 Radius=5.05 StartAngle=2.61799 EndAngle=5.75959
    g36: LineSegment StartX=159.75 StartY=27.2798 StartZ=0 EndX=144 EndY=0 EndZ=0
    g37: LineSegment StartX=155.377 StartY=29.8048 StartZ=0 EndX=157.07 EndY=32.7375 EndZ=0
    g38: LineSegment StartX=164.123 StartY=24.7548 StartZ=0 EndX=165.817 EndY=27.6875 EndZ=0
    g39: ArcOfCircle CenterX=144 CenterY=0 CenterZ=0 NormalX=0 NormalY=0 NormalZ=1 AngleXU=0 Radius=35.25 StartAngle=1.19095 EndAngle=1.5708
    g40: ArcOfCircle CenterX=175.5 CenterY=0 CenterZ=0 NormalX=0 NormalY=0 NormalZ=1 AngleXU=0 Radius=5.05 StartAngle=1.5708 EndAngle=4.71239
    g41: LineSegment StartX=175.5 StartY=5.05 StartZ=0 EndX=178.886 EndY=5.05 EndZ=0
    g42: LineSegment StartX=175.5 StartY=-5.05 StartZ=0 EndX=178.886 EndY=-5.05 EndZ=0
    g43: ArcOfCircle CenterX=144 CenterY=0 CenterZ=0 NormalX=0 NormalY=0 NormalZ=1 AngleXU=0 Radius=35.25 StartAngle=0.143757 EndAngle=0.903441
    g44: ArcOfCircle CenterX=159.75 CenterY=-27.2798 CenterZ=0 NormalX=0 NormalY=0 NormalZ=1 AngleXU=0 Radius=5.05 StartAngle=0.523599 EndAngle=3.66519
    g45: LineSegment StartX=164.123 StartY=-24.7548 StartZ=0 EndX=165.817 EndY=-27.6875 EndZ=0
    g46: LineSegment StartX=155.377 StartY=-29.8048 StartZ=0 EndX=157.07 EndY=-32.7375 EndZ=0
    g47: ArcOfCircle CenterX=144 CenterY=0 CenterZ=0 NormalX=0 NormalY=0 NormalZ=1 AngleXU=0 Radius=35.25 StartAngle=5.37974 EndAngle=6.13943
  constraints (123):
    c: Horizontal(g0)
    c: Horizontal(g1)
    c: Coincident(g2,g0)
    c: Coincident(g17,g1)
    c: Diameter(g2) = 70.5
    c: Coincident(g2,g-1)
    c: Vertical(g0,g2)
    c: Vertical(g2,g1)
    c: DistanceX(g0,g33) = 144
    c: Coincident(g39,g33)
    c: Coincident(g3,g32)
    c: Equal(g2,g3)
    c: Vertical(g3,g33)
    c: Coincident(g4,g2)
    c: Diameter(g4) = 63
    c: PointOnObject(g5,g4)
    c: Angle(g5) = 3.14159
    c: Horizontal(g5,g2)
    c: Diameter(g5) = 10.1
    c: Tangent(g6,g5) = -1.5708
    c: Tangent(g7,g5) = 1.5708
    c: Equal(g2,g8)
    c: Coincident(g2,g8)
    c: Coincident(g6,g13)
    c: Coincident(g7,g8)
    c: Equal(g6,g7)
    c: Coincident(g9,g2)
    c: PointOnObject(g9,g4)
    c: Coincident(g10,g9)
    c: Equal(g10,g5)
    c: Angle(g10) = 3.14159
    c: Tangent(g11,g10) = 1.5708
    c: Equal(g2,g13)
    c: Coincident(g2,g13)
    c: Coincident(g11,g13)
    c: Coincident(g12,g2)
    c: Tangent(g12,g10) = -1.5708
    c: Equal(g11,g12)
    c: Angle(g-1,g9) = 2.0944
    c: Tangent(g15,g14) = -1.5708
    c: Tangent(g16,g14) = 1.5708
    c: Angle(g14) = 3.14159
    c: Equal(g14,g5)
    c: Symmetric(g14,g10,g-1)
    c: Equal(g8,g17)
    c: Coincident(g8,g17)
    c: Coincident(g15,g8)
    c: Coincident(g16,g17)
    c: Equal(g15,g16)
    c: DistanceX(g2,g18) = 42
    c: Equal(g14,g18)
    c: Angle(g18) = 3.14159
    c: Equal(g19,g18)
    c: Angle(g19) = 3.14159
    c: Symmetric(g18,g19,g-1)
    c: Tangent(g20,g18) = -1.5708
    c: Tangent(g21,g18) = 1.5708
    c: Tangent(g23,g19) = 1.5708
    c: Tangent(g22,g19) = -1.5708
    c: Coincident(g23,g0)
    c: Coincident(g22,g24)
    c: Coincident(g20,g1)
    c: Coincident(g21,g25)
    c: Perpendicular(g1,g20)
    c: Perpendicular(g0,g23)
    c: Horizontal(g0,g22)
    c: Horizontal(g21,g1)
    c: Horizontal(g24)
    c: Horizontal(g25)
    c: DistanceY(g18,g19) = 63
    c: DistanceX(g18,g26) = 60
    c: Equal(g18,g26)
    c: Symmetric(g26,g27,g-1)
    c: Equal(g26,g27)
    c: Horizontal(g26,g18)
    c: Tangent(g28,g27) = 1.5708
    c: Tangent(g29,g27) = -1.5708
    c: Tangent(g30,g26) = 1.5708
    c: Tangent(g31,g26) = -1.5708
    c: Perpendicular(g31,g25) = 1.5708
    c: Perpendicular(g30,g32) = 1.5708
    c: Horizontal(g25,g30)
    c: Horizontal(g32)
    c: Perpendicular(g29,g33) = 4.71239
    c: Perpendicular(g28,g24) = 4.71239
    c: Horizontal(g24,g29)
    c: Horizontal(g33)
    c: Coincident(g34,g3)
    c: Equal(g4,g34)
    c: PointOnObject(g35,g34)
    c: Coincident(g36,g35)
    c: Coincident(g36,g3)
    c: Equal(g35,g27)
    c: Angle(g36,g-1) = 2.0944
    c: Angle(g35) = 3.14159
    c: Tangent(g38,g35) = -1.5708
    c: Tangent(g37,g35) = 1.5708
    c: Equal(g3,g39)
    c: Coincident(g3,g39)
    c: Coincident(g37,g39)
    c: Coincident(g38,g43)
    c: Equal(g37,g38)
    c: PointOnObject(g40,g-1)
    c: PointOnObject(g40,g34)
    c: Equal(g35,g40)
    c: Angle(g40) = 3.14159
    c: Tangent(g42,g40) = -1.5708
    c: Tangent(g41,g40) = 1.5708
    c: Equal(g3,g43)
    c: Coincident(g3,g43)
    c: Coincident(g41,g43)
    c: Coincident(g42,g47)
    c: Equal(g41,g42)
    c: Equal(g44,g40)
    c: Angle(g44) = 3.14159
    c: Tangent(g45,g44) = 1.5708
    c: Tangent(g46,g44) = -1.5708
    c: Equal(g3,g47)
    c: Coincident(g3,g47)
    c: Coincident(g45,g47)
    c: Coincident(g46,g3)
    c: Equal(g45,g46)
    c: Symmetric(g35,g44,g-1)
FEATURE [PartDesign::Pocket] Pocket032
  BaseFeature = -> Pad016
  Direction = (0,0,-1)
  Length = 25
  Length2 = 5
  Profile = -> Sketch046
  ReferenceAxis = -> Sketch046 [N_Axis]
  Type = 0
  expr: Length = <<arm2 dims>>.body_height - <<arm2 dims>>.body_bottom_thickness
FEATURE [Sketcher::SketchObject] Sketch048
  AttachmentOffset = pos=(0,0,31) rot=(0,0,1;0rad)
  FullyConstrained = true
  MapMode = 5
  Placement = pos=(0,0,31) rot=(0,0,1;0rad)
  Support = -> [XY_Plane018]
  expr: .AttachmentOffset.Base.z = <<arm2 dims>>.body_height
  expr: Constraints[12] = <<arm2 dims>>.cover_length
  expr: Constraints[13] = <<arm2 dims>>.cover_hole_distance
  expr: Constraints[15] = <<arm2 dims>>.cover_hole_separation
  expr: Constraints[20] = <<arm2 dims>>.cover_hole_distance
  expr: Constraints[21] = <<arm2 dims>>.cover_length / 2 - <<arm2 dims>>.cover_hole_separation / 2
  sketch-geometry (14):
    g0: Circle CenterX=-15.75 CenterY=-27.2798 CenterZ=0 NormalX=0 NormalY=0 NormalZ=1 AngleXU=0 Radius=2
    g1: Circle CenterX=-31.5 CenterY=0 CenterZ=0 NormalX=0 NormalY=0 NormalZ=1 AngleXU=0 Radius=2
    g2: Circle CenterX=-15.75 CenterY=27.2798 CenterZ=0 NormalX=0 NormalY=0 NormalZ=1 AngleXU=0 Radius=2
    g3: Circle CenterX=42 CenterY=31.5 CenterZ=0 NormalX=0 NormalY=0 NormalZ=1 AngleXU=0 Radius=2
    g4: Circle CenterX=102 CenterY=31.5 CenterZ=0 NormalX=0 NormalY=0 NormalZ=1 AngleXU=0 Radius=2
    g5: Circle CenterX=42 CenterY=-31.5 CenterZ=0 NormalX=0 NormalY=0 NormalZ=1 AngleXU=0 Radius=2
    g6: Circle CenterX=102 CenterY=-31.5 CenterZ=0 NormalX=0 NormalY=0 NormalZ=1 AngleXU=0 Radius=2
    g7: Circle CenterX=159.75 CenterY=-27.2798 CenterZ=0 NormalX=0 NormalY=0 NormalZ=1 AngleXU=0 Radius=2
    g8: Circle CenterX=175.5 CenterY=0 CenterZ=0 NormalX=0 NormalY=0 NormalZ=1 AngleXU=0 Radius=2
    g9: Circle CenterX=159.75 CenterY=27.2798 CenterZ=0 NormalX=0 NormalY=0 NormalZ=1 AngleXU=0 Radius=2
    g10: Circle CenterX=144 CenterY=0 CenterZ=0 NormalX=0 NormalY=0 NormalZ=1 AngleXU=0 Radius=31.5
    g11: Circle CenterX=0 CenterY=0 CenterZ=0 NormalX=0 NormalY=0 NormalZ=1 AngleXU=0 Radius=31.5
    g12: LineSegment StartX=-15.75 StartY=27.2798 StartZ=0 EndX=0 EndY=0 EndZ=0
    g13: LineSegment StartX=159.75 StartY=27.2798 StartZ=0 EndX=144 EndY=0 EndZ=0
  constraints (36):
    c: Diameter(g0) = 4
    c: Equal(g0,g1)
    c: Equal(g1,g2)
    c: Equal(g2,g3)
    c: Equal(g3,g5)
    c: Equal(g5,g6)
    c: Equal(g6,g4)
    c: Equal(g4,g9)
    c: Equal(g9,g7)
    c: Equal(g7,g8)
    c: Coincident(g11,g-1)
    c: Horizontal(g10,g11)
    c: DistanceX(g11,g10) = 144
    c: Diameter(g11) = 63
    c: Equal(g11,g10)
    c: DistanceX(g5,g6) = 60
    c: Horizontal(g5,g6)
    c: Horizontal(g3,g4)
    c: Vertical(g4,g6)
    c: Symmetric(g3,g5,g-1)
    c: DistanceY(g5,g3) = 63
    c: DistanceX(g11,g5) = 42
    c: Horizontal(g1,g11)
    c: PointOnObject(g1,g11)
    c: PointOnObject(g8,g10)
    c: Horizontal(g8,g11)
    c: PointOnObject(g2,g11)
    c: Coincident(g12,g2)
    c: Coincident(g12,g11)
    c: Angle(g-1,g12) = 2.0944
    c: Symmetric(g0,g2,g-1)
    c: PointOnObject(g9,g10)
    c: Coincident(g13,g9)
    c: Coincident(g13,g10)
    c: Angle(g13,g-1) = 2.0944
    c: Symmetric(g9,g7,g-1)
FEATURE [PartDesign::Pocket] Pocket033
  BaseFeature = -> Pocket032
  Direction = (0,0,-1)
  Length = 25
  Length2 = 5
  Profile = -> Sketch048
  ReferenceAxis = -> Sketch048 [N_Axis]
  Type = 0
  expr: Length = <<arm2 dims>>.body_guide_hole_depth
FEATURE [Part::Feature] Part__Feature171  label="Arm 2_Arm 003"
  Placement = pos=(144,-5e-15,23) rot=(1,0,0;1.5708rad)
  shape: bbox 222 x 78 x 31 mm, 223 faces (baked)
FEATURE [Sketcher::SketchObject] Sketch049
  AttachmentOffset = pos=(0,0,6) rot=(0,0,1;0rad)
  FullyConstrained = true
  MapMode = 5
  Placement = pos=(0,0,6) rot=(0,0,1;0rad)
  Support = -> [XY_Plane018]
  expr: .AttachmentOffset.Base.z = <<arm2 dims>>.body_bottom_thickness
  expr: Constraints[1] = <<arm2 dims>>.body_arm1_holeset_diameter / 2
  expr: Constraints[2] = <<arm2 dims>>.body_arm1_connector_hole_diameter
  sketch-geometry (1):
    g0: Circle CenterX=0 CenterY=31.25 CenterZ=0 NormalX=0 NormalY=0 NormalZ=1 AngleXU=0 Radius=2.05
  constraints (3):
    c: Vertical(g0,g-1)
    c: DistanceY(g-1,g0) = 31.25
    c: Diameter(g0) = 4.1
FEATURE [PartDesign::Pocket] Pocket034
  BaseFeature = -> Pocket033
  Direction = (0,0,-1)
  Length = 5
  Length2 = 5
  Profile = -> Sketch049
  ReferenceAxis = -> Sketch049 [N_Axis]
  Type = 1
FEATURE [PartDesign::PolarPattern] PolarPattern002
  Angle = 360
  Axis = -> Sketch049 [N_Axis]
  BaseFeature = -> Pocket034
  Occurrences = 6
  Originals = -> [Pocket034]
  Overlap = 0
  expr: Occurrences = <<arm2 dims>>.body_arm1_num_connector_holes
FEATURE [Sketcher::SketchObject] Sketch050  label="Horizontal clip"
  AttachmentOffset = pos=(0,0,21.5) rot=(0,0,1;0rad)
  FullyConstrained = true
  MapMode = 5
  Placement = pos=(21.5,-4.8e-15,4.8e-15) rot=(0.57735,0.57735,0.57735;2.0944rad)
  Support = -> [YZ_Plane018]
  expr: .AttachmentOffset.Base.z = <<arm2 dims>>.body_hook1_position
  expr: Constraints[29] = <<arm2 dims>>.body_bottom_thickness
  sketch-geometry (10):
    g0: LineSegment StartX=7.5 StartY=6 StartZ=0 EndX=1.5 EndY=6 EndZ=0
    g1: LineSegment StartX=1.5 StartY=6 StartZ=0 EndX=1.5 EndY=9 EndZ=0
    g2: LineSegment StartX=1.5 StartY=9 StartZ=0 EndX=-4.1 EndY=9 EndZ=0
    g3: LineSegment StartX=-4.1 StartY=9 StartZ=0 EndX=-4.8 EndY=8.3 EndZ=0
    g4: LineSegment StartX=-4.8 StartY=8.3 StartZ=0 EndX=-6.8 EndY=8.3 EndZ=0
    g5: LineSegment StartX=-6.8 StartY=8.3 StartZ=0 EndX=-7.5 EndY=9 EndZ=0
    g6: LineSegment StartX=-7.5 StartY=9 StartZ=0 EndX=-7.5 EndY=12 EndZ=0
    g7: LineSegment StartX=-7.5 StartY=12 StartZ=0 EndX=5.5 EndY=12 EndZ=0
    g8: LineSegment StartX=5.5 StartY=12 StartZ=0 EndX=5.5 EndY=8 EndZ=0
    g9: LineSegment StartX=5.5 StartY=8 StartZ=0 EndX=7.5 EndY=6 EndZ=0
  constraints (30):
    c: Horizontal(g0)
    c: Vertical(g1)
    c: Horizontal(g2)
    c: Horizontal(g4)
    c: Vertical(g6)
    c: Horizontal(g7)
    c: Vertical(g8)
    c: DistanceX(g0,g0) = 6
    c: DistanceY(g1,g1) = 3
    c: DistanceX(g2,g2) = 5.6
    c: DistanceX(g4,g4) = 2
    c: DistanceY(g6,g6) = 3
    c: DistanceX(g7,g7) = 13
    c: DistanceX(g8,g0) = 2
    c: DistanceY(g0,g8) = 2
    c: Horizontal(g5,g2)
    c: DistanceY(g4,g5) = 0.7
    c: Coincident(g3,g4)
    c: Coincident(g2,g3)
    c: Coincident(g5,g6)
    c: Coincident(g4,g5)
    c: Coincident(g1,g2)
    c: Coincident(g0,g1)
    c: Coincident(g0,g9)
    c: Coincident(g8,g9)
    c: Coincident(g6,g7)
    c: Coincident(g7,g8)
    c: DistanceX(g5,g4) = 0.7
    c: DistanceX(g-1,g0) = 1.5
    c: DistanceY(g-1,g0) = 6
FEATURE [PartDesign::Pad] Pad017
  BaseFeature = -> PolarPattern002
  Direction = (1,-2e-16,3e-16)
  Length = 4.5
  Length2 = 10
  Profile = -> Sketch050
  ReferenceAxis = -> Sketch050 [N_Axis]
  Type = 0
  expr: Length = <<arm2 dims>>.body_hook_width
FEATURE [PartDesign::LinearPattern] LinearPattern
  BaseFeature = -> Pad017
  Direction = -> Sketch050 [N_Axis]
  Length = 49
  Occurrences = 2
  Originals = -> [Pad017]
  Overlap = 0
  expr: Length = <<arm2 dims>>.body_hook2_position - <<arm2 dims>>.body_hook1_position
FEATURE [PartDesign::LinearPattern] LinearPattern001
  BaseFeature = -> LinearPattern
  Direction = -> Sketch050 [N_Axis]
  Length = 95
  Occurrences = 2
  Originals = -> [Pad017]
  Overlap = 0
  expr: Length = <<arm2 dims>>.body_hook3_position - <<arm2 dims>>.body_hook1_position
FEATURE [PartDesign::LinearPattern] LinearPattern002
  BaseFeature = -> LinearPattern001
  Direction = -> Sketch050 [N_Axis]
  Length = 113
  Occurrences = 2
  Originals = -> [Pad017]
  Overlap = 0
  expr: Length = <<arm2 dims>>.body_hook4_position - <<arm2 dims>>.body_hook1_position
FEATURE [Sketcher::SketchObject] Sketch051
  AttachmentOffset = pos=(0,0,13) rot=(0,0,1;0rad)
  FullyConstrained = true
  MapMode = 5
  Placement = pos=(0,0,13) rot=(0,0,1;0rad)
  Support = -> [XY_Plane018]
  expr: .AttachmentOffset.Base.z = <<arm2 dims>>.body_nut_height
  expr: Constraints[10] = <<arm2 dims>>.body_nut_side
  expr: Constraints[1] = <<arm2 dims>>.body_nut_width
  expr: Constraints[25] = <<arm2 dims>>.cover_hole_separation
  expr: Constraints[26] = <<arm2 dims>>.body_nut_width
  expr: Constraints[2] = <<arm2 dims>>.cover_length / 2 - <<arm2 dims>>.cover_hole_separation / 2 - <<arm2 dims>>.body_nut_width / 2
  expr: Constraints[3] = <<arm2 dims>>.cover_hole_distance + <<arm2 dims>>.body_nut_side
  expr: Constraints[49] = <<arm2 dims>>.body_nut_width
  expr: Constraints[51] = <<arm2 dims>>.cover_hole_distance + <<arm2 dims>>.body_nut_side
  expr: Constraints[55] = <<arm2 dims>>.cover_length
  expr: Constraints[64] = <<arm2 dims>>.body_nut_width
  expr: Constraints[72] = <<arm2 dims>>.body_guide_diameter
  sketch-geometry (42):
    g0: LineSegment StartX=45.6 StartY=33.58 StartZ=0 EndX=45.6 EndY=-33.58 EndZ=0
    g1: LineSegment StartX=38.4 StartY=-33.58 StartZ=0 EndX=38.4 EndY=33.58 EndZ=0
    g2: LineSegment StartX=38.4 StartY=-33.58 StartZ=0 EndX=42 EndY=-35.6646 EndZ=0
    g3: LineSegment StartX=42 StartY=-35.6646 StartZ=0 EndX=45.6 EndY=-33.58 EndZ=0
    g4: LineSegment StartX=38.4 StartY=33.58 StartZ=0 EndX=42 EndY=35.6646 EndZ=0
    g5: LineSegment StartX=42 StartY=35.6646 StartZ=0 EndX=45.6 EndY=33.58 EndZ=0
    g6: LineSegment StartX=98.4 StartY=33.58 StartZ=0 EndX=98.4 EndY=-33.58 EndZ=0
    g7: LineSegment StartX=98.4 StartY=-33.58 StartZ=0 EndX=102 EndY=-35.6646 EndZ=0
    g8: LineSegment StartX=102 StartY=-35.6646 StartZ=0 EndX=105.6 EndY=-33.58 EndZ=0
    g9: LineSegment StartX=105.6 StartY=-33.58 StartZ=0 EndX=105.6 EndY=33.58 EndZ=0
    g10: LineSegment StartX=105.6 StartY=33.58 StartZ=0 EndX=102 EndY=35.6646 EndZ=0
    g11: LineSegment StartX=102 StartY=35.6646 StartZ=0 EndX=98.4 EndY=33.58 EndZ=0
    g12: LineSegment StartX=-33.3865 StartY=3.6 StartZ=0 EndX=177.386 EndY=3.6 EndZ=0
    g13: LineSegment StartX=177.386 StartY=3.6 StartZ=0 EndX=179.471 EndY=0 EndZ=0
    g14: LineSegment StartX=179.471 StartY=0 StartZ=0 EndX=177.386 EndY=-3.6 EndZ=0
    g15: LineSegment StartX=177.386 StartY=-3.6 StartZ=0 EndX=-33.3865 EndY=-3.6 EndZ=0
    g16: LineSegment StartX=-33.3865 StartY=-3.6 StartZ=0 EndX=-35.4711 EndY=0 EndZ=0
    g17: LineSegment StartX=-35.4711 StartY=0 StartZ=0 EndX=-33.3865 EndY=3.6 EndZ=0
    g18: Circle CenterX=0 CenterY=0 CenterZ=0 NormalX=0 NormalY=0 NormalZ=1 AngleXU=0 Radius=33.58
    g19: Circle CenterX=144 CenterY=0 CenterZ=0 NormalX=0 NormalY=0 NormalZ=1 AngleXU=0 Radius=33.58
    g20: LineSegment StartX=-14.7609 StartY=18.3667 StartZ=0 EndX=-8.52554 EndY=21.9667 EndZ=0
    g21: LineSegment StartX=-8.52554 StartY=21.9667 StartZ=0 EndX=-13.5755 EndY=30.7135 EndZ=0
    g22: LineSegment StartX=-13.5755 StartY=30.7135 StartZ=0 EndX=-17.7355 EndY=30.7189 EndZ=0
    g23: LineSegment StartX=-17.7355 StartY=30.7189 StartZ=0 EndX=-19.8109 EndY=27.1135 EndZ=0
    g24: LineSegment StartX=-19.8109 StartY=27.1135 StartZ=0 EndX=-14.7609 EndY=18.3667 EndZ=0
    g25: LineSegment StartX=-17.7355 StartY=30.7189 StartZ=0 EndX=0 EndY=0 EndZ=0
    g26: LineSegment StartX=-14.7609 StartY=-18.3667 StartZ=0 EndX=-8.52554 EndY=-21.9667 EndZ=0
    g27: LineSegment StartX=-8.52554 StartY=-21.9667 StartZ=0 EndX=-13.5755 EndY=-30.7135 EndZ=0
    g28: LineSegment StartX=-13.5755 StartY=-30.7135 StartZ=0 EndX=-17.7355 EndY=-30.7189 EndZ=0
    g29: LineSegment StartX=-17.7355 StartY=-30.7189 StartZ=0 EndX=-19.8109 EndY=-27.1135 EndZ=0
    g30: LineSegment StartX=-19.8109 StartY=-27.1135 StartZ=0 EndX=-14.7609 EndY=-18.3667 EndZ=0
    g31: LineSegment StartX=152.526 StartY=21.9667 StartZ=0 EndX=158.761 EndY=18.3667 EndZ=0
    g32: LineSegment StartX=158.761 StartY=18.3667 StartZ=0 EndX=163.811 EndY=27.1135 EndZ=0
    g33: LineSegment StartX=163.811 StartY=27.1135 StartZ=0 EndX=161.736 EndY=30.7189 EndZ=0
    g34: LineSegment StartX=161.736 StartY=30.7189 StartZ=0 EndX=157.576 EndY=30.7135 EndZ=0
    g35: LineSegment StartX=157.576 StartY=30.7135 StartZ=0 EndX=152.526 EndY=21.9667 EndZ=0
    g36: LineSegment StartX=144 StartY=0 StartZ=0 EndX=161.736 EndY=30.7189 EndZ=0
    g37: LineSegment StartX=158.761 StartY=-18.3667 StartZ=0 EndX=163.811 EndY=-27.1135 EndZ=0
    g38: LineSegment StartX=163.811 StartY=-27.1135 StartZ=0 EndX=161.736 EndY=-30.7189 EndZ=0
    g39: LineSegment StartX=161.736 StartY=-30.7189 StartZ=0 EndX=157.576 EndY=-30.7135 EndZ=0
    g40: LineSegment StartX=157.576 StartY=-30.7135 StartZ=0 EndX=152.526 EndY=-21.9667 EndZ=0
    g41: LineSegment StartX=152.526 StartY=-21.9667 StartZ=0 EndX=158.761 EndY=-18.3667 EndZ=0
  constraints (113):
    c: Vertical(g0)
    c: DistanceX(g1,g0) = 7.2
    c: DistanceX(g-1,g1) = 38.4
    c: DistanceY(g1,g1) = 67.16
    c: Symmetric(g1,g1,g-1)
    c: Horizontal(g1,g0)
    c: Coincident(g2,g1)
    c: Coincident(g3,g2)
    c: Coincident(g3,g0)
    c: Equal(g2,g3)
    c: Distance(g2) = 4.16
    c: Horizontal(g1,g0)
    c: Coincident(g4,g1)
    c: Coincident(g5,g4)
    c: Coincident(g5,g0)
    c: Equal(g4,g5)
    c: Equal(g4,g2)
    c: Vertical(g6)
    c: Coincident(g6,g7)
    c: Coincident(g7,g8)
    c: Coincident(g8,g9)
    c: Vertical(g9)
    c: Coincident(g9,g10)
    c: Coincident(g10,g11)
    c: Coincident(g11,g6)
    c: DistanceX(g1,g6) = 60
    c: DistanceX(g6,g8) = 7.2
    c: Horizontal(g0,g6)
    c: Horizontal(g6,g9)
    c: Horizontal(g10,g4)
    c: Equal(g11,g10)
    c: Horizontal(g6,g8)
    c: Horizontal(g6,g0)
    c: Horizontal(g7,g2)
    c: Equal(g8,g7)
    c: Horizontal(g12)
    c: Coincident(g12,g13)
    c: Coincident(g13,g14)
    c: Coincident(g14,g15)
    c: Horizontal(g15)
    c: Coincident(g15,g16)
    c: Coincident(g16,g17)
    c: Coincident(g17,g12)
    c: PointOnObject(g16,g-1)
    c: PointOnObject(g13,g-1)
    c: Symmetric(g12,g15,g-1)
    c: Equal(g12,g15)
    c: Equal(g2,g16)
    c: Equal(g16,g14)
    c: DistanceY(g15,g12) = 7.2
    c: Coincident(g18,g-1)
    c: Diameter(g18) = 67.16
    c: PointOnObject(g12,g18)
    c: PointOnObject(g19,g-1)
    c: Equal(g18,g19)
    c: DistanceX(g18,g19) = 144
    c: PointOnObject(g12,g19)
    c: Coincident(g20,g21)
    c: Coincident(g21,g22)
    c: Coincident(g22,g23)
    c: Coincident(g23,g24)
    c: Coincident(g24,g20)
    c: Perpendicular(g24,g20)
    c: Perpendicular(g21,g20)
    c: Distance(g20) = 7.2
    c: Equal(g16,g23)
    c: Equal(g23,g22)
    c: PointOnObject(g23,g18)
    c: Angle(g-1,g24) = 2.0944
    c: Coincident(g25,g22)
    c: Coincident(g25,g18)
    c: Symmetric(g20,g20,g25)
    c: Distance(g21) = 10.1
    c: Coincident(g26,g27)
    c: Coincident(g27,g28)
    c: Coincident(g28,g29)
    c: Coincident(g29,g30)
    c: Coincident(g30,g26)
    c: Symmetric(g20,g26,g-1)
    c: Symmetric(g26,g20,g-1)
    c: Perpendicular(g26,g30)
    c: Perpendicular(g26,g27)
    c: Equal(g30,g24)
    c: Equal(g30,g27)
    c: Symmetric(g28,g22,g-1)
    c: Coincident(g31,g32)
    c: Coincident(g32,g33)
    c: Coincident(g33,g34)
    c: Coincident(g34,g35)
    c: Coincident(g35,g31)
    c: Coincident(g36,g19)
    c: Coincident(g36,g33)
    c: Symmetric(g31,g31,g36)
    c: Perpendicular(g35,g31)
    c: Perpendicular(g32,g31)
    c: Equal(g20,g31)
    c: Equal(g25,g36)
    c: Equal(g35,g32)
    c: PointOnObject(g34,g19)
    c: Equal(g21,g35)
    c: Angle(g36,g-1) = 2.0944
    c: Coincident(g37,g38)
    c: Coincident(g38,g39)
    c: Coincident(g39,g40)
    c: Coincident(g40,g41)
    c: Coincident(g41,g37)
    c: Perpendicular(g41,g37)
    c: Perpendicular(g40,g41)
    c: Equal(g41,g31)
    c: Equal(g40,g37)
    c: Symmetric(g38,g33,g-1)
    c: Symmetric(g37,g32,g-1)
    c: Symmetric(g37,g31,g-1)
FEATURE [PartDesign::Pocket] Pocket035
  BaseFeature = -> LinearPattern002
  Direction = (0,0,-1)
  Length = 3.6
  Length2 = 5
  Profile = -> Sketch051
  ReferenceAxis = -> Sketch051 [N_Axis]
  Reversed = true
  Type = 0
  expr: Length = <<arm2 dims>>.body_nut_depth
FEATURE [Part::Part2DObjectPython] ShapeString010  # Draft 2D object (typed FeaturePython)
  FontFile = <userpath>/FreeCAD/Font/ARLRDBD.TTF
  MakeFace = true
  Placement = pos=(68.12,19.16,6) rot=(0,0,1;0rad)
  Size = 5
  String = v1.0
  Tracking = 0
  expr: .Placement.Base.z = <<arm2 dims>>.body_bottom_thickness
  expr: Size = <<global settings>>.label_font_size
FEATURE [PartDesign::Pocket] Pocket036
  BaseFeature = -> Pocket035
  Direction = (0,0,-1)
  Length = 0.4
  Length2 = 5
  Profile = -> ShapeString010
  ReferenceAxis = -> ShapeString010 [N_Axis]
  Type = 0
  expr: Length = <<global settings>>.label_text_depth
FEATURE [PartDesign::Body] Body010  label="arm2"
  Group = -> [Sketch045,Pad016,Sketch046,Pocket032,Sketch048,Pocket033,Sketch049,Pocket034,PolarPattern002,Sketch050,Pad017,LinearPattern,LinearPattern001,LinearPattern002,Sketch051,Pocket035,ShapeString010,Pocket036]
  Origin = -> Origin018
  Tip = -> Pocket036
FEATURE [Sketcher::SketchObject] Sketch052
  FullyConstrained = true
  MapMode = 5
  Support = -> [XY_Plane019]
  expr: Constraints[1] = <<arm2 dims>>.grippercoupler_diameter
  expr: Constraints[7] = <<arm2 dims>>.grippercoupler_notch_diameter
  expr: Constraints[8] = <<arm2 dims>>.grippercoupler_notch_center_offset
  sketch-geometry (6):
    g0: ArcOfCircle CenterX=0 CenterY=0 CenterZ=0 NormalX=0 NormalY=0 NormalZ=1 AngleXU=0 Radius=39 StartAngle=0.146577 EndAngle=6.13661
    g1: ArcOfCircle CenterX=35.4 CenterY=0 CenterZ=0 NormalX=0 NormalY=0 NormalZ=1 AngleXU=0 Radius=4.55 StartAngle=1.5708 EndAngle=4.71239
    g2: LineSegment StartX=35.4 StartY=4.55 StartZ=0 EndX=37.5925 EndY=4.55 EndZ=0
    g3: LineSegment StartX=35.4 StartY=-4.55 StartZ=0 EndX=37.5925 EndY=-4.55 EndZ=0
    g4: ArcOfCircle CenterX=37.5925 CenterY=5.55 CenterZ=0 NormalX=0 NormalY=0 NormalZ=1 AngleXU=0 Radius=1 StartAngle=4.71239 EndAngle=6.42976
    g5: ArcOfCircle CenterX=37.5925 CenterY=-5.55 CenterZ=0 NormalX=0 NormalY=0 NormalZ=1 AngleXU=0 Radius=1 StartAngle=6.13661 EndAngle=7.85398
  constraints (15):
    c: Coincident(g0,g-1)
    c: Diameter(g0) = 78
    c: Horizontal(g0,g1)
    c: Horizontal(g2)
    c: Horizontal(g3)
    c: Tangent(g3,g1) = -1.5708
    c: Tangent(g2,g1) = 1.5708
    c: Diameter(g1) = 9.1
    c: DistanceX(g0,g1) = 35.4
    c: Tangent(g0,g4) = -1.5708
    c: Tangent(g2,g4) = -1.5708
    c: Diameter(g4) = 2
    c: Tangent(g3,g5) = 1.5708
    c: Tangent(g0,g5) = -1.5708
    c: Equal(g5,g4)
FEATURE [PartDesign::Pad] Pad018
  Direction = (0,0,1)
  Length = 7
  Length2 = 10
  Profile = -> Sketch052
  ReferenceAxis = -> Sketch052 [N_Axis]
  Type = 0
  expr: Length = <<arm2 dims>>.grippercoupler_thickness
FEATURE [Part::Feature] Part__Feature172  label="J3 Coupler_J3 Coupler001"
  Placement = pos=(0,-2e-15,0) rot=(1,0,0;1.5708rad)
  shape: bbox 77.59 x 78 x 22 mm, 64 faces (baked)
FEATURE [Sketcher::SketchObject] Sketch053
  AttachmentOffset = pos=(0,0,7) rot=(0,0,1;0rad)
  FullyConstrained = true
  MapMode = 5
  Placement = pos=(0,0,7) rot=(0,0,1;0rad)
  Support = -> [XY_Plane019]
  expr: .AttachmentOffset.Base.z = <<arm2 dims>>.grippercoupler_thickness
  expr: Constraints[1] = <<arm2 dims>>.grippercoupler_connector_hole_diameter
  expr: Constraints[2] = <<arm2 dims>>.grippercoupler_connector_holeset_diameter / 2
  sketch-geometry (1):
    g0: Circle CenterX=0 CenterY=32.7 CenterZ=0 NormalX=0 NormalY=0 NormalZ=1 AngleXU=0 Radius=2.1
  constraints (3):
    c: Vertical(g0,g-1)
    c: Diameter(g0) = 4.2
    c: DistanceY(g-1,g0) = 32.7
FEATURE [PartDesign::Pocket] Pocket037
  BaseFeature = -> Pad018
  Direction = (0,0,-1)
  Length = 5
  Length2 = 5
  Profile = -> Sketch053
  ReferenceAxis = -> Sketch053 [N_Axis]
  Type = 1
FEATURE [PartDesign::PolarPattern] PolarPattern003
  Angle = 360
  Axis = -> Sketch053 [N_Axis]
  BaseFeature = -> Pocket037
  Occurrences = 10
  Originals = -> [Pocket037]
  Overlap = 0
  expr: Occurrences = <<arm2 dims>>.grippercoupler_num_connector_holes
FEATURE [Sketcher::SketchObject] Sketch054
  AttachmentOffset = pos=(0,0,7) rot=(0,0,1;0rad)
  FullyConstrained = true
  MapMode = 5
  Placement = pos=(0,0,7) rot=(0,0,1;0rad)
  Support = -> [XY_Plane019]
  expr: .AttachmentOffset.Base.z = <<arm2 dims>>.grippercoupler_thickness
  expr: Constraints[2] = <<arm2 dims>>.grippercoupler_bearing_outer_diameter
  expr: Constraints[3] = <<arm2 dims>>.grippercoupler_bearing_outer_diameter + <<arm2 dims>>.grippercoupler_bearing_holder_wall_thickness * 2
  expr: Constraints[5] = <<arm2 dims>>.grippercoupler_bulge_distance
  expr: Constraints[6] = <<arm2 dims>>.grippercoupler_bulge_width
  sketch-geometry (5):
    g0: Circle CenterX=0 CenterY=0 CenterZ=0 NormalX=0 NormalY=0 NormalZ=1 AngleXU=0 Radius=26.5
    g1: ArcOfCircle CenterX=0 CenterY=0 CenterZ=0 NormalX=0 NormalY=0 NormalZ=1 AngleXU=0 Radius=28.5 StartAngle=3.24705 EndAngle=9.31932
    g2: ArcOfCircle CenterX=-33.5 CenterY=0 CenterZ=0 NormalX=0 NormalY=0 NormalZ=1 AngleXU=0 Radius=3 StartAngle=1.5708 EndAngle=4.71239
    g3: LineSegment StartX=-33.5 StartY=3 StartZ=0 EndX=-28.3417 EndY=3 EndZ=0
    g4: LineSegment StartX=-33.5 StartY=-3 StartZ=0 EndX=-28.3417 EndY=-3 EndZ=0
  constraints (13):
    c: Coincident(g0,g-1)
    c: Coincident(g1,g0)
    c: Diameter(g0) = 53
    c: Diameter(g1) = 57
    c: PointOnObject(g2,g-1)
    c: DistanceX(g2,g0) = 33.5
    c: Diameter(g2) = 6
    c: Horizontal(g3)
    c: Horizontal(g4)
    c: Tangent(g3,g2) = 1.5708
    c: Tangent(g4,g2) = -1.5708
    c: Coincident(g3,g1)
    c: Coincident(g4,g1)
FEATURE [PartDesign::Pad] Pad019
  BaseFeature = -> PolarPattern003
  Direction = (0,0,1)
  Length = 10.5
  Length2 = 10
  Profile = -> Sketch054
  ReferenceAxis = -> Sketch054 [N_Axis]
  Type = 0
  expr: Length = <<arm2 dims>>.grippercoupler_bearing_holder_wall_height
FEATURE [Sketcher::SketchObject] Sketch055
  AttachmentOffset = pos=(0,0,7) rot=(0,0,1;0rad)
  FullyConstrained = true
  MapMode = 5
  Placement = pos=(0,0,7) rot=(0,0,1;0rad)
  Support = -> [XY_Plane019]
  expr: .AttachmentOffset.Base.z = <<arm2 dims>>.grippercoupler_thickness
  expr: Constraints[2] = <<arm2 dims>>.grippercoupler_bearing_outer_diameter
  expr: Constraints[3] = <<arm2 dims>>.grippercoupler_bearing_inner_diameter
  sketch-geometry (2):
    g0: Circle CenterX=0 CenterY=0 CenterZ=0 NormalX=0 NormalY=0 NormalZ=1 AngleXU=0 Radius=17.5
    g1: Circle CenterX=0 CenterY=0 CenterZ=0 NormalX=0 NormalY=0 NormalZ=1 AngleXU=0 Radius=26.5
  constraints (4):
    c: Coincident(g0,g-1)
    c: Coincident(g1,g0)
    c: Diameter(g1) = 53
    c: Diameter(g0) = 35
FEATURE [Sketcher::SketchObject] Sketch056
  AttachmentOffset = pos=(0,0,7) rot=(0,0,1;0rad)
  FullyConstrained = true
  MapMode = 5
  Placement = pos=(0,0,7) rot=(0,0,1;0rad)
  Support = -> [XY_Plane019]
  expr: .AttachmentOffset.Base.z = <<arm2 dims>>.grippercoupler_thickness
  expr: Constraints[1] = <<arm2 dims>>.grippercoupler_axl_house_diameter
  expr: Constraints[3] = <<arm2 dims>>.grippercoupler_axl_house_inner_diameter
  sketch-geometry (2):
    g0: Circle CenterX=0 CenterY=0 CenterZ=0 NormalX=0 NormalY=0 NormalZ=1 AngleXU=0 Radius=15
    g1: Circle CenterX=0 CenterY=0 CenterZ=0 NormalX=0 NormalY=0 NormalZ=1 AngleXU=0 Radius=6.25
  constraints (4):
    c: Coincident(g0,g-1)
    c: Diameter(g0) = 30
    c: Coincident(g1,g0)
    c: Diameter(g1) = 12.5
FEATURE [Sketcher::SketchObject] Sketch057
  FullyConstrained = false
  MapMode = 5
  Support = -> [XY_Plane019]
  expr: Constraints[0] = <<arm2 dims>>.grippercoupler_axl_holeset_diameter / 2
  sketch-geometry (1):
    g0: Circle CenterX=-11 CenterY=0 CenterZ=0 NormalX=0 NormalY=0 NormalZ=1 AngleXU=0 Radius=2.33275
  constraints (2):
    c: DistanceX(g0,g-1) = 11
    c: Horizontal(g0,g-1)
FEATURE [Part::Part2DObjectPython] ShapeString011  # Draft 2D object (typed FeaturePython)
  FontFile = <userpath>/FreeCAD/Font/ARLRDBD.TTF
  MakeFace = true
  Placement = pos=(-7,19,6) rot=(0,0,1;0rad)
  Size = 5
  String = v1.0
  Tracking = 0
  expr: .Placement.Base.z = <<arm2 dims>>.grippercoupler_thickness - <<arm2 dims>>.grippercoupler_bearing_holder_inner_height
  expr: Size = <<global settings>>.label_font_size
FEATURE [PartDesign::Pad] Pad021
  BaseFeature = -> Pad019
  Direction = (0,0,1)
  Length = 15
  Length2 = 10
  Profile = -> Sketch056
  ReferenceAxis = -> Sketch056 [N_Axis]
  Type = 0
  expr: Length = <<arm2 dims>>.grippercoupler_axl_house_height
FEATURE [PartDesign::Pocket] Pocket039
  BaseFeature = -> Pad021
  Direction = (0,0,-1)
  Length = 1
  Length2 = 5
  Profile = -> Sketch055
  ReferenceAxis = -> Sketch055 [N_Axis]
  Type = 0
  expr: Length = <<arm2 dims>>.grippercoupler_bearing_holder_inner_height
FEATURE [PartDesign::Pocket] Pocket040
  BaseFeature = -> Pocket039
  Direction = (0,0,-1)
  Length = 0.4
  Length2 = 5
  Profile = -> ShapeString011
  ReferenceAxis = -> ShapeString011 [N_Axis]
  Type = 0
  expr: Length = <<global settings>>.label_text_depth
FEATURE [PartDesign::Hole] Hole003
  BaseFeature = -> Pocket040
  CustomThreadClearance = 0
  Depth = 25
  DepthType = 0
  Diameter = 4.5
  DrillForDepth = false
  DrillPoint = 1
  DrillPointAngle = 118
  HoleCutCountersinkAngle = 90
  HoleCutCustomValues = false
  HoleCutDepth = 0
  HoleCutDiameter = 9
  HoleCutType = 7
  ModelThread = false
  Profile = -> Sketch057
  Reversed = true
  Tapered = false
  TaperedAngle = 90
  ThreadClass = 0
  ThreadDepth = 25
  ThreadDepthType = 0
  ThreadDirection = 0
  ThreadFit = 0
  ThreadSize = 11
  ThreadType = 1
  Threaded = false
  UseCustomThreadClearance = false
FEATURE [PartDesign::PolarPattern] PolarPattern004
  Angle = 360
  Axis = -> Sketch057 [N_Axis]
  BaseFeature = -> Hole003
  Occurrences = 4
  Originals = -> [Hole003]
  Overlap = 0
  expr: Occurrences = <<arm2 dims>>.grippercoupler_number_of_axl_holes
FEATURE [PartDesign::Body] Body011  label="arm2 gripper coupler"
  Group = -> [Sketch052,Pad018,Sketch053,Pocket037,PolarPattern003,Sketch054,Pad019,Sketch055,Sketch056,Pad021,Sketch057,Pocket039,ShapeString011,Pocket040,Hole003,PolarPattern004]
  Origin = -> Origin019
  Tip = -> PolarPattern004
FEATURE [Part::Feature] Part__Feature173  label="Arm 1_Arm 002"
  Placement = pos=(166,-83,1.9e-14) rot=(1,0,0;1.5708rad)
  shape: bbox 205 x 78 x 42 mm, 134 faces (baked)
FEATURE [Sketcher::SketchObject] Sketch058
  FullyConstrained = true
  MapMode = 5
  Support = -> [XY_Plane021]
  expr: Constraints[12] = <<arm1 dims>>.center_pulley_distance
  expr: Constraints[13] = <<arm1 dims>>.center_pulley_hole_diameter
  expr: Constraints[15] = <<arm1 dims>>.arm2_coupler_hole_diameter
  expr: Constraints[28] = <<global settings>>.tightenerhole_width
  expr: Constraints[29] = <<global settings>>.medium_tightenerhole_length
  expr: Constraints[33] = <<arm1 dims>>.body_tightenerhole1_distance
  expr: Constraints[34] = <<arm1 dims>>.body_tightenerhole1_offset
  expr: Constraints[42] = <<global settings>>.tightenerhole_length
  expr: Constraints[44] = <<arm1 dims>>.body_tightenerhole2_offset
  expr: Constraints[45] = <<global settings>>.wirehole_diameter
  expr: Constraints[46] = <<arm1 dims>>.body_connector_hole_diameter
  expr: Constraints[47] = <<arm1 dims>>.body_wirehole_offset
  expr: Constraints[48] = <<arm1 dims>>.body_wirehole_vert_offset
  expr: Constraints[49] = <<arm1 dims>>.body_connector_hole_offset
  expr: Constraints[50] = <<arm1 dims>>.body_connector_hole_diameter / 2
  expr: Constraints[51] = <<global settings>>.m3_static_hole
  expr: Constraints[53] = <<global settings>>.limit_switch_hole_distance
  expr: Constraints[54] = <<arm1 dims>>.body_limit_switch_distance
  expr: Constraints[55] = <<arm1 dims>>.body_limit_switch_vert_distance
  expr: Constraints[58] = <<arm1 dims>>.body_limit_switch_angle
  expr: Constraints[5] = <<arm1 dims>>.body_length
  expr: Constraints[66] = <<global settings>>.small_tightenerhole_length
  expr: Constraints[68] = <<arm1 dims>>.body_tightenerhole2_distance
  expr: Constraints[6] = <<arm1 dims>>.body_width
  sketch-geometry (27):
    g0: LineSegment StartX=0 StartY=39 StartZ=0 EndX=166 EndY=39 EndZ=0
    g1: LineSegment StartX=166 StartY=-39 StartZ=0 EndX=0 EndY=-39 EndZ=0
    g2: LineSegment StartX=0 StartY=-39 StartZ=0 EndX=0 EndY=39 EndZ=0
    g3: ArcOfCircle CenterX=166 CenterY=0 CenterZ=0 NormalX=0 NormalY=0 NormalZ=1 AngleXU=0 Radius=39 StartAngle=4.71239 EndAngle=7.85398
    g4: Circle CenterX=76 CenterY=0 CenterZ=0 NormalX=0 NormalY=0 NormalZ=1 AngleXU=0 Radius=7
    g5: Circle CenterX=166 CenterY=0 CenterZ=0 NormalX=0 NormalY=0 NormalZ=1 AngleXU=0 Radius=17.5
    g6: ArcOfCircle CenterX=31 CenterY=-23 CenterZ=0 NormalX=0 NormalY=0 NormalZ=1 AngleXU=0 Radius=2.5 StartAngle=3.14159 EndAngle=6.28319
    g7: ArcOfCircle CenterX=31 CenterY=-13 CenterZ=0 NormalX=0 NormalY=0 NormalZ=1 AngleXU=0 Radius=2.5 StartAngle=1e-16 EndAngle=3.14159
    g8: LineSegment StartX=33.5 StartY=-23 StartZ=0 EndX=33.5 EndY=-13 EndZ=0
    g9: LineSegment StartX=28.5 StartY=-13 StartZ=0 EndX=28.5 EndY=-23 EndZ=0
    g10: ArcOfCircle CenterX=31 CenterY=13 CenterZ=0 NormalX=0 NormalY=0 NormalZ=1 AngleXU=0 Radius=2.5 StartAngle=3.14159 EndAngle=6.28319
    g11: ArcOfCircle CenterX=31 CenterY=23 CenterZ=0 NormalX=0 NormalY=0 NormalZ=1 AngleXU=0 Radius=2.5 StartAngle=0 EndAngle=3.14159
    g12: LineSegment StartX=33.5 StartY=13 StartZ=0 EndX=33.5 EndY=23 EndZ=0
    g13: LineSegment StartX=28.5 StartY=23 StartZ=0 EndX=28.5 EndY=13 EndZ=0
    g14: ArcOfCircle CenterX=116 CenterY=13 CenterZ=0 NormalX=0 NormalY=0 NormalZ=1 AngleXU=0 Radius=2.5 StartAngle=3.14159 EndAngle=6.28319
    g15: ArcOfCircle CenterX=116 CenterY=25 CenterZ=0 NormalX=0 NormalY=0 NormalZ=1 AngleXU=0 Radius=2.5 StartAngle=5e-16 EndAngle=3.14159
    g16: LineSegment StartX=118.5 StartY=13 StartZ=0 EndX=118.5 EndY=25 EndZ=0
    g17: LineSegment StartX=113.5 StartY=25 StartZ=0 EndX=113.5 EndY=13 EndZ=0
    g18: Circle CenterX=127 CenterY=27.1 CenterZ=0 NormalX=0 NormalY=0 NormalZ=1 AngleXU=0 Radius=2.1
    g19: Circle CenterX=104.5 CenterY=10.8 CenterZ=0 NormalX=0 NormalY=0 NormalZ=1 AngleXU=0 Radius=2.5
    g20: Circle CenterX=116.4 CenterY=-4.8 CenterZ=0 NormalX=0 NormalY=0 NormalZ=1 AngleXU=0 Radius=1.6
    g21: Circle CenterX=108.012 CenterY=-9.25998 CenterZ=0 NormalX=0 NormalY=0 NormalZ=1 AngleXU=0 Radius=1.6
    g22: LineSegment StartX=116.4 StartY=-4.8 StartZ=0 EndX=108.012 EndY=-9.25998 EndZ=0
    g23: ArcOfCircle CenterX=116 CenterY=-25 CenterZ=0 NormalX=0 NormalY=0 NormalZ=1 AngleXU=0 Radius=2.5 StartAngle=3.14159 EndAngle=6.28319
    g24: ArcOfCircle CenterX=116 CenterY=-21 CenterZ=0 NormalX=0 NormalY=0 NormalZ=1 AngleXU=0 Radius=2.5 StartAngle=0 EndAngle=3.14159
    g25: LineSegment StartX=118.5 StartY=-25 StartZ=0 EndX=118.5 EndY=-21 EndZ=0
    g26: LineSegment StartX=113.5 StartY=-21 StartZ=0 EndX=113.5 EndY=-25 EndZ=0
  constraints (69):
    c: Coincident(g1,g2)
    c: Coincident(g2,g0)
    c: Horizontal(g0)
    c: Horizontal(g1)
    c: Vertical(g2)
    c: DistanceX(g1,g1) = 166
    c: DistanceY(g2,g2) = 78
    c: Symmetric(g0,g1,g-1)
    c: Coincident(g3,g1)
    c: Vertical(g1,g0)
    c: Tangent(g3,g0) = 1.5708
    c: Horizontal(g-1,g4)
    c: DistanceX(g-1,g4) = 76
    c: Diameter(g4) = 14
    c: Coincident(g5,g3)
    c: Diameter(g5) = 35
    c: Tangent(g6,g8) = -1.5708
    c: Tangent(g8,g7) = -1.5708
    c: Tangent(g7,g9) = -1.5708
    c: Tangent(g9,g6) = -1.5708
    c: Equal(g6,g7)
    c: Vertical(g8)
    c: Tangent(g10,g12) = -1.5708
    c: Tangent(g12,g11) = -1.5708
    c: Tangent(g11,g13) = -1.5708
    c: Tangent(g13,g10) = -1.5708
    c: Equal(g10,g11)
    c: Vertical(g12)
    c: Diameter(g6) = 5
    c: DistanceY(g8,g8) = 10
    c: Equal(g10,g7)
    c: Equal(g8,g12)
    c: Symmetric(g10,g7,g-1)
    c: DistanceY(g7,g10) = 26
    c: DistanceX(g-1,g6) = 31
    c: Tangent(g14,g16) = -1.5708
    c: Tangent(g16,g15) = -1.5708
    c: Tangent(g15,g17) = -1.5708
    c: Tangent(g17,g14) = -1.5708
    c: Equal(g14,g15)
    c: Vertical(g16)
    c: Equal(g11,g15)
    c: DistanceY(g17,g17) = 12
    c: Horizontal(g10,g14)
    c: DistanceX(g11,g15) = 85
    c: Diameter(g19) = 5
    c: Diameter(g18) = 4.2
    c: DistanceX(g19) = 104.5
    c: DistanceY(g-1,g19) = 10.8
    c: DistanceX(g-1,g18) = 127
    c: DistanceY(g15,g18) = 2.1
    c: Diameter(g21) = 3.2
    c: Equal(g21,g20)
    c: Distance(g21,g20) = 9.5
    c: DistanceX(g-1,g20) = 116.4
    c: DistanceY(g20,g-1) = 4.8
    c: Coincident(g22,g20)
    c: Coincident(g22,g21)
    c: Angle(g-1,g22) = 0.488692
    c: Tangent(g23,g25) = -1.5708
    c: Tangent(g25,g24) = -1.5708
    c: Tangent(g24,g26) = -1.5708
    c: Tangent(g26,g23) = -1.5708
    c: Equal(g23,g24)
    c: Vertical(g25)
    c: Equal(g24,g14)
    c: DistanceY(g25,g25) = 4
    c: Vertical(g24,g14)
    c: DistanceY(g24,g14) = 34
FEATURE [Spreadsheet::Sheet] Spreadsheet003  label="arm1 dims"
  cells = A1=body; B1=width; C1(body_width)==78mm; B2=length; C2(body_length)==166mm; B3=height; C3(body_height)==42mm; B4=wall thickness; C4(body_wall_thickness)==4mm; B5=mount wall thickness; C5(body_mount_wall_thickness)==8mm; B6=bottom thickness; C6(body_bottom_thickness)==10mm; B7=tightener hole1 distance; C7(body_tightenerhole1_distance)==26mm; B8=tightener hole1 offset; C8(body_tightenerhole1_offset)==31mm; B9=tightener hole2 distance; C9(body_tightenerhole2_distance)==34mm; B10=tightener hole2 offset; C10(body_tightenerhole2_offset)==85mm; B11=connector hole diameter; C11(body_connector_hole_diameter)==4.2mm; B12=connector hole offset; C12(body_connector_hole_offset)==127mm; B13=connector hole vert offset; C13(body_connector_hole_vert_offset)==27mm; B14=wirehole offset; C14(body_wirehole_offset)==104.5mm; B15=wirehole vert offset; C15(body_wirehole_vert_offset)==10.8mm; B16=limit switch distance; C16(body_limit_switch_distance)==116.4mm; B17=limit switch vert distance; C17(body_limit_switch_vert_distance)=4.8; B18=limit switch angle; C18(body_limit_switch_angle)==28deg; B19=wall notch height; C19(body_wall_notch_height)==24.6mm; B20=notch1 distance; C20(body_notch1_distance)==24mm; B21=notch length; C21(body_notch_length)==12mm; B22=notch inter distance; C22(body_notch_inter_distance)==52mm; B23=num notches; C23(body_num_notches)=3; A24=arm2 coupler; B24=hole diameter; C24(arm2_coupler_hole_diameter)==35mm; B25=bearing diameter; C25(arm2_coupler_bearing_diameter)==42mm; B26=bearing height; C26(arm2_coupler_bearing_height)==7mm; A27=center pulley; B27=hole diameter; C27(center_pulley_hole_diameter)==14mm; B28=distance; C28(center_pulley_distance)==76mm; B29=bottom bearing diameter; C29(center_pulley_bottom_bearing_diameter)==22mm; B30=bottom bearing height; C30(center_pulley_bottom_bearing_height)==7mm; B31=top bearing diameter; C31(center_pulley_top_bearing_diameter)==22mm; B32=top bearing inset; C32(center_pulley_top_bearing_inset)==1mm; B33=top bearing height; C33(center_pulley_top_bearing_height)==7mm; B34=top bearing wall thickness; C34(center_pulley_top_bearing_wall_thickness)==3mm; A35=mount; B35=window height; C35(mount_window_height)==25mm; B36=window width; C36(mount_window_width)==40mm; B37=window offset; C37(mount_window_offset)==12mm; B38=window fillet radius; C38(mount_window_fillet_radius)==2mm; B39=hole radius; C39(mount_hole_radius)==5.1mm; B40=hole distance horiz; C40(mount_hole_distance_horiz)==51mm; B41=hole distance vert; C41(mount_hole_distance_vert)==18mm; B42=hole offset; C42(mount_hole_offset)==16.5mm; A43=clip; B43=wall offset; C43(clip_wall_offset)==4mm; B44=clip1 distance; C44(clip_clip1_distance)==13mm; B45=inter distance; C45(clip_inter_distance)==40mm; B46=num clips; C46(clip_num_clips)=3; A47=cover; B47=thickness; C47(cover_thickness)==3mm; B48=clip depth; C48(cover_clip_depth)==10mm; B49=clip base; C49(cover_clip_base)==5mm; B50=clip base height; C50(cover_clip_base_height)==1.5mm; B51=clip base backlash; C51(cover_clip_base_backlash)==1.5mm; B52=clip height; C52(cover_clip_height)==8mm; B53=clip bulge forward; C53(cover_clip_bulge_forward)==1.15mm; B54=clip bulge incline; C54(cover_clip_bulge_incline)==1.15mm; B55=clip bulge height; C55(cover_clip_bulge_height)==3.5mm; B56=clip1 distance; C56(cover_clip1_distance)==25mm; B57=clip inter distance; C57(cover_clip_inter_distance)==64mm; B58=clip edge distance; C58(cover_clip_edge_distance)==4.6mm; B59=num clips; C59(cover_num_clips)=3; A60=zaxis; B60=body diameter; C60(zaxis_body_diameter)==120mm; B61=flat side distance; C61(zaxis_flat_side_distance)==62mm; B62=rods tolerance; C62(zaxis_rods_tolerance)==0.5mm; B63=wall thickness; C63(zaxis_wall_thickness)==3mm; B64=bottom thickness; C64(zaxis_bottom_thickness)==6mm; B65=vertical bearing diameter; C65(zaxis_vertical_bearing_diameter)==19mm; B66=vertical bearing height; C66(zaxis_vertical_bearing_height)==39mm; B67=motor shaft diameter; C67(zaxis_motor_shaft_diameter)==25mm; B68=motor distance; C68(zaxis_motor_distance)==10mm; B69=lead screw hole distance; C69(zaxis_lead_screw_hole_distance)==11.5mm; B70=lead screw outer diameter; C70(zaxis_lead_screw_outer_diameter)==10.2mm; B71=lead screw inset depth; C71(zaxis_lead_screw_inset_depth)==2mm; B72=inner wall width; C72(zaxis_inner_wall_width)==60mm; B73=flat wall thickness; C73(zaxis_flat_wall_thickness)==8mm; B74=inner wall height; C74(zaxis_inner_wall_height)==28mm; B75=inner wall thickness; C75(zaxis_inner_wall_thickness)==6mm
FEATURE [PartDesign::Pad] Pad022
  Direction = (0,0,1)
  Length = 42
  Length2 = 10
  Profile = -> Sketch058
  ReferenceAxis = -> Sketch058 [N_Axis]
  Type = 0
  expr: Length = <<arm1 dims>>.body_height
FEATURE [Sketcher::SketchObject] Sketch059
  AttachmentOffset = pos=(0,0,42) rot=(0,0,1;0rad)
  FullyConstrained = true
  MapMode = 5
  Placement = pos=(0,0,42) rot=(0,0,1;0rad)
  Support = -> [XY_Plane021]
  expr: .AttachmentOffset.Base.z = <<arm1 dims>>.body_height
  expr: Constraints[4] = <<arm1 dims>>.body_mount_wall_thickness
  expr: Constraints[5] = <<arm1 dims>>.body_width - <<arm1 dims>>.body_wall_thickness * 2
  expr: Constraints[7] = <<arm1 dims>>.body_length - <<arm1 dims>>.body_mount_wall_thickness
  sketch-geometry (4):
    g0: LineSegment StartX=8 StartY=35 StartZ=0 EndX=166 EndY=35 EndZ=0
    g1: LineSegment StartX=166 StartY=-35 StartZ=0 EndX=8 EndY=-35 EndZ=0
    g2: LineSegment StartX=8 StartY=-35 StartZ=0 EndX=8 EndY=35 EndZ=0
    g3: ArcOfCircle CenterX=166 CenterY=9e-16 CenterZ=0 NormalX=0 NormalY=0 NormalZ=1 AngleXU=0 Radius=35 StartAngle=4.71239 EndAngle=7.85398
  constraints (11):
    c: Coincident(g1,g2)
    c: Coincident(g2,g0)
    c: Horizontal(g0)
    c: Horizontal(g1)
    c: DistanceX(g-1,g1) = 8
    c: DistanceY(g2,g2) = 70
    c: Symmetric(g0,g1,g-1)
    c: DistanceX(g0,g0) = 158
    c: Equal(g0,g1)
    c: Coincident(g3,g1)
    c: Tangent(g3,g0) = 1.5708
FEATURE [PartDesign::Pocket] Pocket041
  BaseFeature = -> Pad022
  Direction = (0,0,-1)
  Length = 32
  Length2 = 5
  Profile = -> Sketch059
  ReferenceAxis = -> Sketch059 [N_Axis]
  Type = 0
  expr: Length = <<arm1 dims>>.body_height - <<arm1 dims>>.body_bottom_thickness
FEATURE [Sketcher::SketchObject] Sketch060
  FullyConstrained = true
  MapMode = 5
  Support = -> [XY_Plane021]
  expr: Constraints[0] = <<arm1 dims>>.center_pulley_distance
  expr: Constraints[1] = <<arm1 dims>>.center_pulley_bottom_bearing_diameter
  sketch-geometry (1):
    g0: Circle CenterX=76 CenterY=0 CenterZ=0 NormalX=0 NormalY=0 NormalZ=1 AngleXU=0 Radius=11
  constraints (3):
    c: DistanceX(g-1,g0) = 76
    c: Diameter(g0) = 22
    c: Horizontal(g0,g-1)
FEATURE [PartDesign::Pocket] Pocket042
  BaseFeature = -> Pocket041
  Direction = (0,0,-1)
  Length = 7
  Length2 = 5
  Profile = -> Sketch060
  ReferenceAxis = -> Sketch060 [N_Axis]
  Reversed = true
  Type = 0
  expr: Length = <<arm1 dims>>.center_pulley_bottom_bearing_height
FEATURE [Sketcher::SketchObject] Sketch061
  AttachmentOffset = pos=(0,0,10) rot=(0,0,1;0rad)
  FullyConstrained = true
  MapMode = 5
  Placement = pos=(0,0,10) rot=(0,0,1;0rad)
  Support = -> [XY_Plane021]
  expr: .AttachmentOffset.Base.z = <<arm1 dims>>.body_bottom_thickness
  expr: Constraints[0] = <<arm1 dims>>.center_pulley_distance
  expr: Constraints[2] = <<arm1 dims>>.center_pulley_top_bearing_diameter
  sketch-geometry (1):
    g0: Circle CenterX=76 CenterY=0 CenterZ=0 NormalX=0 NormalY=0 NormalZ=1 AngleXU=0 Radius=11
  constraints (3):
    c: DistanceX(g-1,g0) = 76
    c: Horizontal(g0,g-1)
    c: Diameter(g0) = 22
FEATURE [PartDesign::Pocket] Pocket043
  BaseFeature = -> Pocket042
  Direction = (0,0,-1)
  Length = 1
  Length2 = 5
  Profile = -> Sketch061
  ReferenceAxis = -> Sketch061 [N_Axis]
  Type = 0
  expr: Length = <<arm1 dims>>.center_pulley_top_bearing_inset
FEATURE [Sketcher::SketchObject] Sketch062
  AttachmentOffset = pos=(0,0,10) rot=(0,0,1;0rad)
  FullyConstrained = true
  MapMode = 5
  Placement = pos=(0,0,10) rot=(0,0,1;0rad)
  Support = -> [XY_Plane021]
  expr: .AttachmentOffset.Base.z = <<arm1 dims>>.body_bottom_thickness
  expr: Constraints[0] = <<arm1 dims>>.center_pulley_distance
  expr: Constraints[3] = <<arm1 dims>>.center_pulley_top_bearing_diameter
  expr: Constraints[4] = <<arm1 dims>>.center_pulley_top_bearing_diameter + <<arm1 dims>>.center_pulley_top_bearing_wall_thickness * 2
  sketch-geometry (2):
    g0: Circle CenterX=76 CenterY=0 CenterZ=0 NormalX=0 NormalY=0 NormalZ=1 AngleXU=0 Radius=11
    g1: Circle CenterX=76 CenterY=0 CenterZ=0 NormalX=0 NormalY=0 NormalZ=1 AngleXU=0 Radius=14
  constraints (5):
    c: DistanceX(g-1,g0) = 76
    c: Horizontal(g-1,g0)
    c: Coincident(g1,g0)
    c: Diameter(g0) = 22
    c: Diameter(g1) = 28
FEATURE [PartDesign::Pad] Pad023
  BaseFeature = -> Pocket043
  Direction = (0,0,1)
  Length = 6
  Length2 = 10
  Profile = -> Sketch062
  ReferenceAxis = -> Sketch062 [N_Axis]
  Type = 0
  expr: Length = <<arm1 dims>>.center_pulley_top_bearing_height - <<arm1 dims>>.center_pulley_top_bearing_inset
FEATURE [Sketcher::SketchObject] Sketch063
  AttachmentOffset = pos=(0,0,10) rot=(0,0,1;0rad)
  FullyConstrained = true
  MapMode = 5
  Placement = pos=(0,0,10) rot=(0,0,1;0rad)
  Support = -> [XY_Plane021]
  expr: .AttachmentOffset.Base.z = <<arm1 dims>>.body_bottom_thickness
  expr: Constraints[0] = <<arm1 dims>>.body_length
  expr: Constraints[2] = <<arm1 dims>>.arm2_coupler_bearing_diameter
  sketch-geometry (1):
    g0: Circle CenterX=166 CenterY=0 CenterZ=0 NormalX=0 NormalY=0 NormalZ=1 AngleXU=0 Radius=21
  constraints (3):
    c: DistanceX(g-1,g0) = 166
    c: Horizontal(g-1,g0)
    c: Diameter(g0) = 42
FEATURE [PartDesign::Pocket] Pocket044
  BaseFeature = -> Pad023
  Direction = (0,0,-1)
  Length = 7
  Length2 = 5
  Profile = -> Sketch063
  ReferenceAxis = -> Sketch063 [N_Axis]
  Type = 0
  expr: Length = <<arm1 dims>>.arm2_coupler_bearing_height
FEATURE [Sketcher::SketchObject] Sketch064
  FullyConstrained = true
  MapMode = 5
  Placement = pos=(0,0,0) rot=(1,0,0;1.5708rad)
  Support = -> [XZ_Plane021]
  expr: Constraints[10] = <<arm1 dims>>.body_wall_notch_height + <<arm1 dims>>.body_bottom_thickness
  expr: Constraints[11] = <<arm1 dims>>.body_length + <<arm1 dims>>.body_width / 2 - <<arm1 dims>>.body_wall_thickness
  sketch-geometry (4):
    g0: LineSegment StartX=201 StartY=36.9 StartZ=0 EndX=201.55 EndY=36.35 EndZ=0
    g1: LineSegment StartX=201.55 StartY=36.35 StartZ=0 EndX=201.55 EndY=35.15 EndZ=0
    g2: LineSegment StartX=201.55 StartY=35.15 StartZ=0 EndX=201 EndY=34.6 EndZ=0
    g3: LineSegment StartX=201 StartY=34.6 StartZ=0 EndX=201 EndY=36.9 EndZ=0
  constraints (12):
    c: Coincident(g1,g0)
    c: Vertical(g1)
    c: Coincident(g2,g1)
    c: Coincident(g3,g2)
    c: Coincident(g3,g0)
    c: Vertical(g3)
    c: DistanceY(g1,g1) = 1.2
    c: DistanceY(g3,g3) = 2.3
    c: DistanceY(g2,g1) = 0.55
    c: DistanceX(g2,g1) = 0.55
    c: DistanceY(g-1,g2) = 34.6
    c: DistanceX(g-1,g2) = 201
FEATURE [PartDesign::Line] DatumLine
  AttacherType = Attacher::AttachEngineLine
  AttachmentOffset = pos=(166,0,0) rot=(0,0,1;0rad)
  Length = 20
  MapMode = 18
  Placement = pos=(166,0,0) rot=(0,0,1;0rad)
  ResizeMode = 0
  Support = -> [XY_Plane021]
  expr: .AttachmentOffset.Base.x = <<arm1 dims>>.body_length
FEATURE [PartDesign::Groove] Groove
  Angle = 20
  Axis = (0,0,1)
  Base = (166,0,0)
  BaseFeature = -> Pocket044
  Midplane = true
  Profile = -> Sketch064
  ReferenceAxis = -> DatumLine
FEATURE [Sketcher::SketchObject] Sketch065
  AttachmentOffset = pos=(0,0,24) rot=(0,0,1;0rad)
  FullyConstrained = true
  MapMode = 5
  Placement = pos=(24,-5.3e-15,5.3e-15) rot=(0.57735,0.57735,0.57735;2.0944rad)
  Support = -> [YZ_Plane021]
  expr: .AttachmentOffset.Base.z = <<arm1 dims>>.body_notch1_distance
  expr: Constraints[10] = <<arm1 dims>>.body_wall_notch_height + <<arm1 dims>>.body_bottom_thickness
  expr: Constraints[11] = <<arm1 dims>>.body_width / 2 - <<arm1 dims>>.body_wall_thickness
  sketch-geometry (4):
    g0: LineSegment StartX=35 StartY=36.9 StartZ=0 EndX=35.55 EndY=36.35 EndZ=0
    g1: LineSegment StartX=35.55 StartY=36.35 StartZ=0 EndX=35.55 EndY=35.15 EndZ=0
    g2: LineSegment StartX=35.55 StartY=35.15 StartZ=0 EndX=35 EndY=34.6 EndZ=0
    g3: LineSegment StartX=35 StartY=34.6 StartZ=0 EndX=35 EndY=36.9 EndZ=0
  constraints (12):
    c: Coincident(g1,g0)
    c: Vertical(g1)
    c: Coincident(g2,g1)
    c: Coincident(g3,g2)
    c: Coincident(g3,g0)
    c: Vertical(g3)
    c: DistanceY(g1,g1) = 1.2
    c: DistanceY(g3,g3) = 2.3
    c: DistanceY(g2,g1) = 0.55
    c: DistanceX(g2,g1) = 0.55
    c: DistanceY(g-1,g2) = 34.6
    c: DistanceX(g-1,g0) = 35
FEATURE [PartDesign::Pocket] Pocket045
  BaseFeature = -> Groove
  Direction = (-1,2e-16,-3e-16)
  Length = 12
  Length2 = 5
  Profile = -> Sketch065
  ReferenceAxis = -> Sketch065 [N_Axis]
  Reversed = true
  Type = 0
  expr: Length = <<arm1 dims>>.body_notch_length
FEATURE [PartDesign::Mirrored] Mirrored
  MirrorPlane = -> Sketch065 [V_Axis]
  Overlap = 0
FEATURE [PartDesign::LinearPattern] LinearPattern003
  Direction = -> Sketch065 [N_Axis]
  Length = 128
  Occurrences = 3
  Overlap = 0
  expr: Length = (<<arm1 dims>>.body_notch_inter_distance + <<arm1 dims>>.body_notch_length) * (<<arm1 dims>>.body_num_notches - 1)
  expr: Occurrences = <<arm1 dims>>.body_num_notches
FEATURE [PartDesign::MultiTransform] MultiTransform
  BaseFeature = -> Pocket045
  Originals = -> [Pocket045]
  Overlap = 0
  Transformations = -> [Mirrored,LinearPattern003]
FEATURE [Sketcher::SketchObject] Sketch066
  FullyConstrained = true
  MapMode = 5
  Placement = pos=(0,0,0) rot=(-0.57735,0.57735,0.57735;4.18879rad)
  Support = -> [YZ_Plane021]
  expr: Constraints[11] = <<arm1 dims>>.mount_window_height
  expr: Constraints[12] = <<arm1 dims>>.mount_window_width
  expr: Constraints[13] = <<arm1 dims>>.mount_window_offset
  expr: Constraints[15] = <<arm1 dims>>.mount_window_fillet_radius
  expr: Constraints[26] = <<arm1 dims>>.mount_hole_offset
  expr: Constraints[27] = <<arm1 dims>>.mount_hole_distance_vert
  expr: Constraints[28] = <<arm1 dims>>.mount_hole_distance_horiz
  expr: Constraints[29] = <<arm1 dims>>.mount_hole_radius
  sketch-geometry (12):
    g0: LineSegment StartX=-19 StartY=37 StartZ=0 EndX=19 EndY=37 EndZ=0
    g1: LineSegment StartX=20 StartY=36 StartZ=0 EndX=20 EndY=13 EndZ=0
    g2: LineSegment StartX=19 StartY=12 StartZ=0 EndX=-19 EndY=12 EndZ=0
    g3: LineSegment StartX=-20 StartY=13 StartZ=0 EndX=-20 EndY=36 EndZ=0
    g4: ArcOfCircle CenterX=19 CenterY=13 CenterZ=0 NormalX=0 NormalY=0 NormalZ=1 AngleXU=0 Radius=1 StartAngle=4.71239 EndAngle=6.28319
    g5: ArcOfCircle CenterX=19 CenterY=36 CenterZ=0 NormalX=0 NormalY=0 NormalZ=1 AngleXU=0 Radius=1 StartAngle=-9e-16 EndAngle=1.5708
    g6: ArcOfCircle CenterX=-19 CenterY=36 CenterZ=0 NormalX=0 NormalY=0 NormalZ=1 AngleXU=0 Radius=1 StartAngle=1.5708 EndAngle=3.14159
    g7: ArcOfCircle CenterX=-19 CenterY=13 CenterZ=0 NormalX=0 NormalY=0 NormalZ=1 AngleXU=0 Radius=1 StartAngle=3.14159 EndAngle=4.71239
    g8: Circle CenterX=25.5 CenterY=34.5 CenterZ=0 NormalX=0 NormalY=0 NormalZ=1 AngleXU=0 Radius=2.55
    g9: Circle CenterX=25.5 CenterY=16.5 CenterZ=0 NormalX=0 NormalY=0 NormalZ=1 AngleXU=0 Radius=2.55
    g10: Circle CenterX=-25.5 CenterY=16.5 CenterZ=0 NormalX=0 NormalY=0 NormalZ=1 AngleXU=0 Radius=2.55
    g11: Circle CenterX=-25.5 CenterY=34.5 CenterZ=0 NormalX=0 NormalY=0 NormalZ=1 AngleXU=0 Radius=2.55
  constraints (30):
    c: Horizontal(g0)
    c: Vertical(g1)
    c: Vertical(g3)
    c: Tangent(g2,g4) = 1.5708
    c: Tangent(g1,g4) = 1.5708
    c: Tangent(g1,g5) = 1.5708
    c: Tangent(g0,g5) = 1.5708
    c: Tangent(g0,g6) = 1.5708
    c: Tangent(g3,g6) = 1.5708
    c: Tangent(g3,g7) = 1.5708
    c: Tangent(g2,g7) = 1.5708
    c: DistanceY(g2,g0) = 25
    c: DistanceX(g3,g1) = 40
    c: DistanceY(g-1,g2) = 12
    c: Symmetric(g2,g2,g-2)
    c: Diameter(g4) = 2
    c: Equal(g4,g5)
    c: Equal(g5,g6)
    c: Equal(g6,g7)
    c: Equal(g11,g10)
    c: Equal(g10,g9)
    c: Equal(g9,g8)
    c: Symmetric(g10,g9,g-2)
    c: Vertical(g10,g11)
    c: Vertical(g9,g8)
    c: Horizontal(g8,g11)
    c: DistanceY(g-1,g9) = 16.5
    c: DistanceY(g9,g8) = 18
    c: DistanceX(g10,g9) = 51
    c: Diameter(g9) = 5.1
FEATURE [PartDesign::Pocket] Pocket046
  BaseFeature = -> MultiTransform
  Direction = (1,-2e-16,3e-16)
  Length = 5
  Length2 = 5
  Profile = -> Sketch066
  ReferenceAxis = -> Sketch066 [N_Axis]
  Type = 2
FEATURE [Spreadsheet::Sheet] Spreadsheet004  label="clips"
  cells = A1=vertical; B1=depth; C1(vertical_depth)==7mm; B2=base; C2(vertical_base)==6mm; B3=base height; C3(vertical_base_height)==2mm; B4=base backlash; C4(vertical_base_backlash)==2mm; B5=height; C5(vertical_height)==12mm; B6=bulge forward; C6(vertical_bulge_forward)==1mm; B7=bulge incline; C7(vertical_bulge_incline)==1mm; B8=bulge height; C8(vertical_bulge_height)==3mm
FEATURE [Sketcher::SketchObject] Sketch067  label="vertical clip"
  AttachmentOffset = pos=(-31,10,-21) rot=(0,0,1;0rad)
  FullyConstrained = true
  MapMode = 5
  Placement = pos=(21,31,10) rot=(-0.57735,0.57735,0.57735;4.18879rad)
  Support = -> [YZ_Plane021]
  expr: .AttachmentOffset.Base.x = -<<arm1 dims>>.body_width / 2 + <<arm1 dims>>.body_wall_thickness + <<arm1 dims>>.clip_wall_offset
  expr: .AttachmentOffset.Base.y = <<arm1 dims>>.body_bottom_thickness
  expr: .AttachmentOffset.Base.z = -<<arm1 dims>>.body_mount_wall_thickness - <<arm1 dims>>.clip_clip1_distance
  expr: Constraints[10] = <<clips>>.vertical_bulge_incline
  expr: Constraints[11] = <<clips>>.vertical_bulge_incline
  expr: Constraints[12] = <<clips>>.vertical_bulge_forward
  expr: Constraints[5] = <<clips>>.vertical_base
  expr: Constraints[6] = <<clips>>.vertical_height
  expr: Constraints[7] = <<clips>>.vertical_base_height
  expr: Constraints[8] = <<clips>>.vertical_bulge_height
  expr: Constraints[9] = <<clips>>.vertical_base_backlash
  sketch-geometry (8):
    g0: LineSegment StartX=0 StartY=12 StartZ=0 EndX=4 EndY=12 EndZ=0
    g1: LineSegment StartX=6 StartY=0 StartZ=0 EndX=0 EndY=0 EndZ=0
    g2: LineSegment StartX=6 StartY=0 StartZ=0 EndX=4 EndY=2 EndZ=0
    g3: LineSegment StartX=4 StartY=2 StartZ=0 EndX=4 EndY=12 EndZ=0
    g4: LineSegment StartX=0 StartY=0 StartZ=0 EndX=0 EndY=9 EndZ=0
    g5: LineSegment StartX=0 StartY=9 StartZ=0 EndX=-1 EndY=10 EndZ=0
    g6: LineSegment StartX=-1 StartY=10 StartZ=0 EndX=-1 EndY=11 EndZ=0
    g7: LineSegment StartX=-1 StartY=11 StartZ=0 EndX=0 EndY=12 EndZ=0
  constraints (23):
    c: Horizontal(g0)
    c: Horizontal(g1)
    c: Vertical(g4)
    c: Vertical(g6)
    c: Vertical(g3)
    c: DistanceX(g1,g1) = 6
    c: DistanceY(g1,g0) = 12
    c: DistanceY(g1,g2) = 2
    c: DistanceY(g4,g0) = 3
    c: DistanceX(g2,g1) = 2
    c: DistanceY(g4,g5) = 1
    c: DistanceY(g6,g0) = 1
    c: DistanceX(g5,g4) = 1
    c: Coincident(g4,g5)
    c: Coincident(g5,g6)
    c: Coincident(g6,g7)
    c: Coincident(g0,g7)
    c: Coincident(g0,g3)
    c: Coincident(g2,g3)
    c: Coincident(g1,g4)
    c: Vertical(g0,g4)
    c: Coincident(g2,g1)
    c: Coincident(g-1,g1)
FEATURE [PartDesign::Pad] Pad024
  BaseFeature = -> Pocket046
  Direction = (-1,2e-16,-3e-16)
  Length = 7
  Length2 = 10
  Profile = -> Sketch067
  ReferenceAxis = -> Sketch067 [N_Axis]
  Reversed = true
  Type = 0
  expr: Length = <<clips>>.vertical_depth
FEATURE [PartDesign::LinearPattern] LinearPattern004
  BaseFeature = -> Pad024
  Direction = -> Sketch067 [N_Axis]
  Length = 80
  Occurrences = 3
  Originals = -> [Pad024]
  Overlap = 0
  Reversed = true
  expr: Length = (<<arm1 dims>>.clip_num_clips - 1) * <<arm1 dims>>.clip_inter_distance
  expr: Occurrences = <<arm1 dims>>.clip_num_clips
FEATURE [Part::Part2DObjectPython] ShapeString012  # Draft 2D object (typed FeaturePython)
  FontFile = <userpath>/FreeCAD/Font/ARLRDBD.TTF
  MakeFace = true
  Placement = pos=(70,-27,10) rot=(0,0,1;0rad)
  Size = 5
  String = v1.0
  Tracking = 0
  expr: .Placement.Base.z = <<arm1 dims>>.body_bottom_thickness
  expr: Size = <<global settings>>.label_font_size
FEATURE [PartDesign::Pocket] Pocket047
  BaseFeature = -> LinearPattern004
  Direction = (0,0,-1)
  Length = 0.4
  Length2 = 5
  Profile = -> ShapeString012
  ReferenceAxis = -> ShapeString012 [N_Axis]
  Type = 0
  expr: Length = <<global settings>>.label_text_depth
FEATURE [PartDesign::Body] Body012  label="arm 1 body"
  Group = -> [Sketch058,Pad022,Sketch059,Pocket041,Sketch060,Pocket042,Sketch061,Pocket043,Sketch062,Pad023,Sketch063,Pocket044,Sketch064,DatumLine,Groove,Sketch065,Pocket045,MultiTransform,Mirrored,LinearPattern003,Sketch066,Pocket046,Sketch067,Pad024,LinearPattern004,ShapeString012,Pocket047]
  Origin = -> Origin021
  Tip = -> Pocket047
FEATURE [Part::Feature] Part__Feature174  label="Arm 1 Cover_Arm 1 Cover001"
  Placement = pos=(166,-98,-2.2e-14) rot=(1,0,0;1.5708rad)
  shape: bbox 205 x 78 x 11 mm, 68 faces (baked)
FEATURE [Sketcher::SketchObject] Sketch068
  FullyConstrained = true
  MapMode = 5
  Support = -> [XY_Plane022]
  expr: Constraints[5] = <<arm1 dims>>.body_length
  expr: Constraints[6] = <<arm1 dims>>.body_width
  sketch-geometry (4):
    g0: LineSegment StartX=0 StartY=39 StartZ=0 EndX=166 EndY=39 EndZ=0
    g1: LineSegment StartX=166 StartY=-39 StartZ=0 EndX=0 EndY=-39 EndZ=0
    g2: LineSegment StartX=0 StartY=-39 StartZ=0 EndX=0 EndY=39 EndZ=0
    g3: ArcOfCircle CenterX=166 CenterY=0 CenterZ=0 NormalX=0 NormalY=0 NormalZ=1 AngleXU=0 Radius=39 StartAngle=4.71239 EndAngle=7.85398
  constraints (11):
    c: Coincident(g1,g2)
    c: Coincident(g2,g0)
    c: Horizontal(g0)
    c: Horizontal(g1)
    c: Vertical(g2)
    c: DistanceX(g1,g1) = 166
    c: DistanceY(g2,g2) = 78
    c: Symmetric(g0,g1,g-1)
    c: Coincident(g3,g1)
    c: Vertical(g1,g0)
    c: Tangent(g3,g0) = 1.5708
FEATURE [PartDesign::Pad] Pad025
  Direction = (0,0,1)
  Length = 3
  Length2 = 10
  Profile = -> Sketch068
  ReferenceAxis = -> Sketch068 [N_Axis]
  Type = 0
  expr: Length = <<arm1 dims>>.cover_thickness
FEATURE [Sketcher::SketchObject] Sketch069  label="vertical clip001"
  AttachmentOffset = pos=(-34.4,3,-25) rot=(0,0,1;0rad)
  FullyConstrained = true
  MapMode = 5
  Placement = pos=(25,34.4,3) rot=(-0.57735,0.57735,0.57735;4.18879rad)
  Support = -> [YZ_Plane022]
  expr: .AttachmentOffset.Base.x = -<<arm1 dims>>.body_width / 2 + <<arm1 dims>>.cover_clip_edge_distance
  expr: .AttachmentOffset.Base.y = <<arm1 dims>>.cover_thickness
  expr: .AttachmentOffset.Base.z = -<<arm1 dims>>.cover_clip1_distance
  expr: Constraints[10] = <<arm1 dims>>.cover_clip_bulge_incline
  expr: Constraints[11] = <<arm1 dims>>.cover_clip_bulge_incline
  expr: Constraints[12] = <<arm1 dims>>.cover_clip_bulge_forward
  expr: Constraints[5] = <<arm1 dims>>.cover_clip_base
  expr: Constraints[6] = <<arm1 dims>>.cover_clip_height
  expr: Constraints[7] = <<arm1 dims>>.cover_clip_base_height
  expr: Constraints[8] = <<arm1 dims>>.cover_clip_bulge_height
  expr: Constraints[9] = <<arm1 dims>>.cover_clip_base_backlash
  sketch-geometry (8):
    g0: LineSegment StartX=0 StartY=8 StartZ=0 EndX=3.5 EndY=8 EndZ=0
    g1: LineSegment StartX=5 StartY=2e-16 StartZ=0 EndX=0 EndY=2e-16 EndZ=0
    g2: LineSegment StartX=5 StartY=2e-16 StartZ=0 EndX=3.5 EndY=1.5 EndZ=0
    g3: LineSegment StartX=3.5 StartY=1.5 StartZ=0 EndX=3.5 EndY=8 EndZ=0
    g4: LineSegment StartX=0 StartY=2e-16 StartZ=0 EndX=0 EndY=4.5 EndZ=0
    g5: LineSegment StartX=0 StartY=4.5 StartZ=0 EndX=-1.15 EndY=5.65 EndZ=0
    g6: LineSegment StartX=-1.15 StartY=5.65 StartZ=0 EndX=-1.15 EndY=6.85 EndZ=0
    g7: LineSegment StartX=-1.15 StartY=6.85 StartZ=0 EndX=0 EndY=8 EndZ=0
  constraints (23):
    c: Horizontal(g0)
    c: Horizontal(g1)
    c: Vertical(g4)
    c: Vertical(g6)
    c: Vertical(g3)
    c: DistanceX(g1,g1) = 5
    c: DistanceY(g1,g0) = 8
    c: DistanceY(g1,g2) = 1.5
    c: DistanceY(g4,g0) = 3.5
    c: DistanceX(g2,g1) = 1.5
    c: DistanceY(g4,g5) = 1.15
    c: DistanceY(g6,g0) = 1.15
    c: DistanceX(g5,g4) = 1.15
    c: Coincident(g4,g5)
    c: Coincident(g5,g6)
    c: Coincident(g6,g7)
    c: Coincident(g0,g7)
    c: Coincident(g0,g3)
    c: Coincident(g2,g3)
    c: Coincident(g1,g4)
    c: Vertical(g0,g4)
    c: Coincident(g2,g1)
    c: Coincident(g-1,g1)
FEATURE [PartDesign::Pad] Pad026
  BaseFeature = -> Pad025
  Direction = (-1,2e-16,-3e-16)
  Length = 10
  Length2 = 10
  Profile = -> Sketch069
  ReferenceAxis = -> Sketch069 [N_Axis]
  Reversed = true
  Type = 0
  expr: Length = <<arm1 dims>>.cover_clip_depth
FEATURE [PartDesign::LinearPattern] LinearPattern005
  Direction = -> Sketch069 [N_Axis]
  Length = 128
  Occurrences = 3
  Overlap = 0
  Reversed = true
  expr: Length = (<<arm1 dims>>.cover_num_clips - 1) * <<arm1 dims>>.cover_clip_inter_distance
FEATURE [PartDesign::Mirrored] Mirrored001
  MirrorPlane = -> XZ_Plane022
  Overlap = 0
FEATURE [PartDesign::MultiTransform] MultiTransform001
  BaseFeature = -> Pad026
  Originals = -> [Pad026]
  Overlap = 0
  Transformations = -> [LinearPattern005,Mirrored001]
FEATURE [Sketcher::SketchObject] Sketch070  label="vertical clip002"
  AttachmentOffset = pos=(-200.4,3,0) rot=(0,0,1;0rad)
  FullyConstrained = true
  MapMode = 5
  Placement = pos=(200.4,-7e-16,3) rot=(0,0.707107,0.707107;3.14159rad)
  Support = -> [XZ_Plane022]
  expr: .AttachmentOffset.Base.x = -<<arm1 dims>>.body_width / 2 - <<arm1 dims>>.body_length + <<arm1 dims>>.cover_clip_edge_distance
  expr: .AttachmentOffset.Base.y = <<arm1 dims>>.cover_thickness
  expr: Constraints[10] = <<arm1 dims>>.cover_clip_bulge_incline
  expr: Constraints[11] = <<arm1 dims>>.cover_clip_bulge_incline
  expr: Constraints[12] = <<arm1 dims>>.cover_clip_bulge_forward
  expr: Constraints[5] = <<arm1 dims>>.cover_clip_base
  expr: Constraints[6] = <<arm1 dims>>.cover_clip_height
  expr: Constraints[7] = <<arm1 dims>>.cover_clip_base_height
  expr: Constraints[8] = <<arm1 dims>>.cover_clip_bulge_height
  expr: Constraints[9] = <<arm1 dims>>.cover_clip_base_backlash
  sketch-geometry (8):
    g0: LineSegment StartX=0 StartY=8 StartZ=0 EndX=3.5 EndY=8 EndZ=0
    g1: LineSegment StartX=5 StartY=2e-16 StartZ=0 EndX=0 EndY=2e-16 EndZ=0
    g2: LineSegment StartX=5 StartY=2e-16 StartZ=0 EndX=3.5 EndY=1.5 EndZ=0
    g3: LineSegment StartX=3.5 StartY=1.5 StartZ=0 EndX=3.5 EndY=8 EndZ=0
    g4: LineSegment StartX=0 StartY=2e-16 StartZ=0 EndX=0 EndY=4.5 EndZ=0
    g5: LineSegment StartX=0 StartY=4.5 StartZ=0 EndX=-1.15 EndY=5.65 EndZ=0
    g6: LineSegment StartX=-1.15 StartY=5.65 StartZ=0 EndX=-1.15 EndY=6.85 EndZ=0
    g7: LineSegment StartX=-1.15 StartY=6.85 StartZ=0 EndX=0 EndY=8 EndZ=0
  constraints (23):
    c: Horizontal(g0)
    c: Horizontal(g1)
    c: Vertical(g4)
    c: Vertical(g6)
    c: Vertical(g3)
    c: DistanceX(g1,g1) = 5
    c: DistanceY(g1,g0) = 8
    c: DistanceY(g1,g2) = 1.5
    c: DistanceY(g4,g0) = 3.5
    c: DistanceX(g2,g1) = 1.5
    c: DistanceY(g4,g5) = 1.15
    c: DistanceY(g6,g0) = 1.15
    c: DistanceX(g5,g4) = 1.15
    c: Coincident(g4,g5)
    c: Coincident(g5,g6)
    c: Coincident(g6,g7)
    c: Coincident(g0,g7)
    c: Coincident(g0,g3)
    c: Coincident(g2,g3)
    c: Coincident(g1,g4)
    c: Vertical(g0,g4)
    c: Coincident(g2,g1)
    c: Coincident(g-1,g1)
FEATURE [PartDesign::Line] DatumLine001
  AttacherType = Attacher::AttachEngineLine
  AttachmentOffset = pos=(166,0,0) rot=(0,0,1;0rad)
  Length = 20
  MapMode = 18
  Placement = pos=(166,0,0) rot=(0,0,1;0rad)
  ResizeMode = 0
  Support = -> [XY_Plane022]
  expr: .AttachmentOffset.Base.x = <<arm1 dims>>.body_length
FEATURE [PartDesign::Revolution] Revolution
  Angle = 18
  Axis = (0,0,1)
  Base = (166,0,0)
  BaseFeature = -> MultiTransform001
  Midplane = true
  Profile = -> Sketch070
  ReferenceAxis = -> DatumLine001
  Reversed = true
FEATURE [Part::FeaturePython] Clone001  label="arm 1 body001"  # Draft clone (typed FeaturePython)
  AttacherType = Attacher::AttachEngine3D
  Fuse = false
  Objects = -> [Body012]
  Placement = pos=(62,0,0) rot=(0,0,1;0rad)
  Scale = (1,1,1)
FEATURE [Part::FeaturePython] Clone003  label="arm2 body 2"  # Draft clone (typed FeaturePython)
  AttacherType = Attacher::AttachEngine3D
  Fuse = false
  Objects = -> [Body010]
  Placement = pos=(0,0,0) rot=(1,0,0;3.14159rad)
  Scale = (1,1,1)
FEATURE [Part::FeaturePython] Clone004  label="arm2 cover002"  # Draft clone (typed FeaturePython)
  AttacherType = Attacher::AttachEngine3D
  Fuse = false
  Objects = -> [Body009]
  Placement = pos=(0,-9e-15,-39) rot=(-1,0,0;1.5708rad)
  Scale = (1,1,1)
FEATURE [Part::FeaturePython] Clone005  label="arm1 arm2 coupler001"  # Draft clone (typed FeaturePython)
  AttacherType = Attacher::AttachEngine3D
  Fuse = false
  Objects = -> [Body008]
  Placement = pos=(0,0,0) rot=(-1,0,0;1.5708rad)
  Scale = (1,1,1)
FEATURE [Part::FeaturePython] Clone006  label="arm1 arm2 coupler002"  # Draft clone (typed FeaturePython)
  AttacherType = Attacher::AttachEngine3D
  Fuse = false
  Objects = -> [Body008]
  Placement = pos=(137,8e-15,-60) rot=(0,0.707107,-0.707107;3.14159rad)
  Scale = (1,1,1)
FEATURE [App::Part] Part008  label="Constructed arm2"
  Group = -> [Clone003,Clone004,Clone005,Clone006]
  Origin = -> Origin024
FEATURE [App::Part] Part005  label="Main Arm 2"
  Group = -> [Spreadsheet002,Body008,Body009,Body010,Body011,Part008]
  Origin = -> Origin014
FEATURE [Part::Part2DObjectPython] ShapeString013  # Draft 2D object (typed FeaturePython)
  FontFile = <userpath>/FreeCAD/Font/ARLRDBD.TTF
  MakeFace = true
  Placement = pos=(90,0,3) rot=(0,0,1;0rad)
  Size = 5
  String = v1.0
  Tracking = 0
  expr: .Placement.Base.z = <<arm1 dims>>.cover_thickness
  expr: Size = <<global settings>>.label_font_size
FEATURE [PartDesign::Pocket] Pocket048
  BaseFeature = -> Revolution
  Direction = (0,0,-1)
  Length = 0.4
  Length2 = 5
  Profile = -> ShapeString013
  ReferenceAxis = -> ShapeString013 [N_Axis]
  Type = 0
  expr: Length = <<global settings>>.label_text_depth
FEATURE [PartDesign::Body] Body013  label="arm1 cover"
  Group = -> [Sketch068,Pad025,Sketch069,Pad026,MultiTransform001,LinearPattern005,Mirrored001,Sketch070,DatumLine001,Revolution,ShapeString013,Pocket048]
  Origin = -> Origin022
  Tip = -> Pocket048
FEATURE [Part::FeaturePython] Clone002  label="arm1 cover001"  # Draft clone (typed FeaturePython)
  AttacherType = Attacher::AttachEngine3D
  Fuse = false
  Objects = -> [Body013]
  Placement = pos=(62,-4e-15,45) rot=(1,0,0;3.14159rad)
  Scale = (1,1,1)
FEATURE [Part::Feature] Part__Feature175  label="Z-axis Mount Platform_Z-axis Mount Platform001"
  Placement = pos=(-4.3e-14,-126,1.9e-14) rot=(0.57735,0.57735,0.57735;2.0944rad)
  shape: bbox 122 x 120 x 45 mm, 110 faces (baked)
FEATURE [Spreadsheet::Sheet] Spreadsheet005  label="vert base dims"
  cells = A1=base; B1=smooth rod distance; C1(base_smooth_rod_distance)==67.18000000000001mm; B2=smooth rod diameter; C2(base_smooth_rod_diameter)==10mm; B3=smooth rod set diameter; C3(base_smooth_rod_set_diameter)==95mm; B4=stepper shaft distance; C4(base_stepper_shaft_distance)==33mm; B5=diameter; C5(base_diameter)==120mm; B6=bottom thickness; C6(base_bottom_thickness)==8mm; B7=screwholes; C7(screwholes)==4.1mm; B8=number screwholes; C8(num_screwholes)=12; B9=screwhole offset; C9(screwhole_offset)==49.5mm; B10=axis height; C10(base_axis_height)==19mm; B11=enforcement wall thickness; C11(base_enforcement_wall_thickness)==4mm; B12=stop thickness; C12(base_stop_thickness)==6mm; B13=stop length; C13(base_stop_length)==3.63mm; B14=enforcement wall height; C14(base_enforcement_wall_height)==12.5mm; B15=rod support high side; C15(base_rod_support_high_side)==7.5mm; B16=rod support slope; C16(base_rod_support_slope)==13.9deg; B17=rod support depth; C17(base_rod_support_depth)==2mm; B18=bottom plate thickness; C18(bottom_plate_thickness)==10mm; B19=bottom plate center hole; C19(bottom_plate_center_hole_diameter)==35mm; B20=lead screw bearing offset; C20(lead_screw_bearing_offset)==33mm; B21=lead screw bearing diameter; C21(lead_screw_bearing_diameter)==22mm; B22=lead screw bearing thickness; C22(lead_screw_bearing_thickness)==7mm; B23=lead screw bearing hole; C23(lead_screw_bearing_hole)==15mm
FEATURE [Sketcher::SketchObject] Sketch071
  FullyConstrained = true
  MapMode = 5
  Support = -> [XY_Plane026]
  expr: Constraints[0] = <<vert base dims>>.base_smooth_rod_set_diameter
  expr: Constraints[22] = <<arm1 dims>>.zaxis_flat_side_distance
  expr: Constraints[23] = <<arm1 dims>>.body_width
  expr: Constraints[31] = <<vert base dims>>.base_smooth_rod_diameter + <<arm1 dims>>.zaxis_rods_tolerance
  expr: Constraints[34] = <<vert base dims>>.base_stepper_shaft_distance
  expr: Constraints[36] = <<arm1 dims>>.zaxis_motor_shaft_diameter
  expr: Constraints[37] = <<arm1 dims>>.zaxis_motor_distance
  expr: Constraints[3] = <<arm1 dims>>.zaxis_body_diameter
  expr: Constraints[43] = <<global settings>>.m3_static_hole
  expr: Constraints[64] = <<global settings>>.m3_static_hole
  expr: Constraints[66] = <<global settings>>.nema17_hole_distance
  expr: Constraints[67] = <<arm1 dims>>.zaxis_lead_screw_hole_distance
  sketch-geometry (27):
    g0: Circle CenterX=0 CenterY=-3e-16 CenterZ=0 NormalX=0 NormalY=0 NormalZ=1 AngleXU=0 Radius=47.5
    g1: ArcOfCircle CenterX=0 CenterY=-3e-16 CenterZ=0 NormalX=0 NormalY=0 NormalZ=1 AngleXU=0 Radius=60 StartAngle=0.917633 EndAngle=5.36555
    g2: LineSegment StartX=-33.5876 StartY=33.5876 StartZ=0 EndX=33.5876 EndY=33.5876 EndZ=0
    g3: LineSegment StartX=33.5876 StartY=33.5876 StartZ=0 EndX=33.5876 EndY=-33.5876 EndZ=0
    g4: LineSegment StartX=33.5876 StartY=-33.5876 StartZ=0 EndX=-33.5876 EndY=-33.5876 EndZ=0
    g5: LineSegment StartX=-33.5876 StartY=-33.5876 StartZ=0 EndX=-33.5876 EndY=33.5876 EndZ=0
    g6: Circle CenterX=-33.5876 CenterY=33.5876 CenterZ=0 NormalX=0 NormalY=0 NormalZ=1 AngleXU=0 Radius=5.25
    g7: Circle CenterX=33.5876 CenterY=33.5876 CenterZ=0 NormalX=0 NormalY=0 NormalZ=1 AngleXU=0 Radius=5.25
    g8: Circle CenterX=33.5876 CenterY=-33.5876 CenterZ=0 NormalX=0 NormalY=0 NormalZ=1 AngleXU=0 Radius=5.25
    g9: Circle CenterX=-33.5876 CenterY=-33.5876 CenterZ=0 NormalX=0 NormalY=0 NormalZ=1 AngleXU=0 Radius=5.25
    g10: LineSegment StartX=62 StartY=-39 StartZ=0 EndX=62 EndY=39 EndZ=0
    g11: ArcOfCircle CenterX=62 CenterY=81.0238 CenterZ=0 NormalX=0 NormalY=0 NormalZ=1 AngleXU=0 Radius=42.0238 StartAngle=4.05923 EndAngle=4.71239
    g12: ArcOfCircle CenterX=62 CenterY=-81.0238 CenterZ=0 NormalX=0 NormalY=0 NormalZ=1 AngleXU=0 Radius=42.0238 StartAngle=1.5708 EndAngle=2.22396
    g13: Circle CenterX=33 CenterY=-3e-16 CenterZ=0 NormalX=0 NormalY=0 NormalZ=1 AngleXU=0 Radius=4.25
    g14: Circle CenterX=-10 CenterY=-3e-16 CenterZ=0 NormalX=0 NormalY=0 NormalZ=1 AngleXU=0 Radius=12.5
    g15: Circle CenterX=-25.5 CenterY=15.5 CenterZ=0 NormalX=0 NormalY=0 NormalZ=1 AngleXU=0 Radius=1.6
    g16: Circle CenterX=5.5 CenterY=15.5 CenterZ=0 NormalX=0 NormalY=0 NormalZ=1 AngleXU=0 Radius=1.6
    g17: Circle CenterX=5.5 CenterY=-15.5 CenterZ=0 NormalX=0 NormalY=0 NormalZ=1 AngleXU=0 Radius=1.6
    g18: Circle CenterX=-25.5 CenterY=-15.5 CenterZ=0 NormalX=0 NormalY=0 NormalZ=1 AngleXU=0 Radius=1.6
    g19: LineSegment StartX=-25.5 StartY=15.5 StartZ=0 EndX=5.5 EndY=15.5 EndZ=0
    g20: LineSegment StartX=5.5 StartY=15.5 StartZ=0 EndX=5.5 EndY=-15.5 EndZ=0
    g21: Circle CenterX=27.25 CenterY=5.75 CenterZ=0 NormalX=0 NormalY=0 NormalZ=1 AngleXU=0 Radius=1.6
    g22: Circle CenterX=38.75 CenterY=5.75 CenterZ=0 NormalX=0 NormalY=0 NormalZ=1 AngleXU=0 Radius=1.6
    g23: Circle CenterX=38.75 CenterY=-5.75 CenterZ=0 NormalX=0 NormalY=0 NormalZ=1 AngleXU=0 Radius=1.6
    g24: Circle CenterX=27.25 CenterY=-5.75 CenterZ=0 NormalX=0 NormalY=0 NormalZ=1 AngleXU=0 Radius=1.6
    g25: LineSegment StartX=27.25 StartY=5.75 StartZ=0 EndX=38.75 EndY=5.75 EndZ=0
    g26: LineSegment StartX=38.75 StartY=5.75 StartZ=0 EndX=38.75 EndY=-5.75 EndZ=0
  constraints (68):
    c: Diameter(g0) = 95
    c: Coincident(g0,g-1)
    c: Coincident(g0,g1)
    c: Diameter(g1) = 120
    c: Coincident(g2,g3)
    c: Coincident(g3,g4)
    c: Coincident(g4,g5)
    c: Coincident(g5,g2)
    c: Horizontal(g4)
    c: Vertical(g3)
    c: Vertical(g5)
    c: PointOnObject(g2,g0)
    c: PointOnObject(g4,g0)
    c: Symmetric(g2,g2,g-2)
    c: Equal(g4,g5)
    c: Coincident(g6,g2)
    c: Coincident(g7,g2)
    c: Coincident(g8,g3)
    c: Coincident(g9,g4)
    c: Equal(g6,g7)
    c: Equal(g7,g8)
    c: Equal(g8,g9)
    c: DistanceX(g1,g10) = 62
    c: DistanceY(g10,g10) = 78
    c: Symmetric(g10,g10,g-1)
    c: Coincident(g11,g10)
    c: Coincident(g12,g10)
    c: Tangent(g1,g12) = 1.5708
    c: Tangent(g1,g11) = 1.5708
    c: Vertical(g1,g1)
    c: Perpendicular(g12,g10)
    c: Diameter(g9) = 10.5
    c: Diameter(g13) = 8.5
    c: Horizontal(g13,g1)
    c: DistanceX(g1,g13) = 33
    c: Horizontal(g14,g1)
    c: Diameter(g14) = 25
    c: DistanceX(g14,g1) = 10
    c: Vertical(g15,g18)
    c: Horizontal(g18,g17)
    c: Equal(g16,g15)
    c: Equal(g15,g18)
    c: Equal(g18,g17)
    c: Diameter(g18) = 3.2
    c: Symmetric(g15,g17,g14)
    c: Coincident(g19,g15)
    c: Coincident(g19,g16)
    c: Horizontal(g19)
    c: Coincident(g20,g16)
    c: Coincident(g20,g17)
    c: Vertical(g20)
    c: Equal(g19,g20)
    c: Coincident(g25,g21)
    c: Coincident(g25,g22)
    c: Coincident(g26,g22)
    c: Coincident(g26,g23)
    c: Vertical(g26)
    c: Horizontal(g25)
    c: Equal(g25,g26)
    c: Horizontal(g23,g24)
    c: Vertical(g24,g21)
    c: Equal(g24,g23)
    c: Equal(g23,g22)
    c: Equal(g22,g21)
    c: Diameter(g24) = 3.2
    c: Symmetric(g21,g23,g13)
    c: DistanceX(g19,g19) = 31
    c: DistanceX(g25,g25) = 11.5
FEATURE [PartDesign::Pad] Pad027
  Direction = (0,0,1)
  Length = 45
  Length2 = 10
  Profile = -> Sketch071
  ReferenceAxis = -> Sketch071 [N_Axis]
  Type = 0
  expr: Length = <<arm1 dims>>.body_height + <<arm1 dims>>.cover_thickness
FEATURE [Sketcher::SketchObject] Sketch072
  AttachmentOffset = pos=(0,0,45) rot=(0,0,1;0rad)
  FullyConstrained = true
  MapMode = 5
  Placement = pos=(0,0,45) rot=(0,0,1;0rad)
  Support = -> [XY_Plane026]
  expr: .AttachmentOffset.Base.z = <<arm1 dims>>.body_height + <<arm1 dims>>.cover_thickness
  expr: Constraints[0] = <<vert base dims>>.base_smooth_rod_set_diameter
  expr: Constraints[21] = <<arm1 dims>>.zaxis_vertical_bearing_diameter
  sketch-geometry (9):
    g0: Circle CenterX=-33.5876 CenterY=33.5876 CenterZ=0 NormalX=0 NormalY=0 NormalZ=1 AngleXU=0 Radius=9.5
    g1: Circle CenterX=33.5876 CenterY=33.5876 CenterZ=0 NormalX=0 NormalY=0 NormalZ=1 AngleXU=0 Radius=9.5
    g2: Circle CenterX=33.5876 CenterY=-33.5876 CenterZ=0 NormalX=0 NormalY=0 NormalZ=1 AngleXU=0 Radius=9.5
    g3: Circle CenterX=-33.5876 CenterY=-33.5876 CenterZ=0 NormalX=0 NormalY=0 NormalZ=1 AngleXU=0 Radius=9.5
    g4: Circle CenterX=0 CenterY=0 CenterZ=0 NormalX=0 NormalY=0 NormalZ=1 AngleXU=0 Radius=47.5
    g5: LineSegment StartX=-33.5876 StartY=33.5876 StartZ=0 EndX=33.5876 EndY=33.5876 EndZ=0
    g6: LineSegment StartX=33.5876 StartY=33.5876 StartZ=0 EndX=33.5876 EndY=-33.5876 EndZ=0
    g7: LineSegment StartX=33.5876 StartY=-33.5876 StartZ=0 EndX=-33.5876 EndY=-33.5876 EndZ=0
    g8: LineSegment StartX=-33.5876 StartY=-33.5876 StartZ=0 EndX=-33.5876 EndY=33.5876 EndZ=0
  constraints (22):
    c: Diameter(g4) = 95
    c: Coincident(g4,g-1)
    c: Coincident(g5,g6)
    c: Coincident(g6,g7)
    c: Coincident(g7,g8)
    c: Coincident(g8,g5)
    c: Horizontal(g5)
    c: Horizontal(g7)
    c: Vertical(g6)
    c: Vertical(g8)
    c: PointOnObject(g5,g4)
    c: PointOnObject(g5,g4)
    c: PointOnObject(g6,g4)
    c: Coincident(g3,g7)
    c: Coincident(g2,g6)
    c: Coincident(g5,g1)
    c: Coincident(g5,g0)
    c: Equal(g5,g8)
    c: Equal(g0,g1)
    c: Equal(g1,g2)
    c: Equal(g2,g3)
    c: Diameter(g3) = 19
FEATURE [PartDesign::Pocket] Pocket049
  BaseFeature = -> Pad027
  Direction = (0,0,-1)
  Length = 39
  Length2 = 5
  Profile = -> Sketch072
  ReferenceAxis = -> Sketch072 [N_Axis]
  Type = 0
  expr: Length = <<arm1 dims>>.zaxis_vertical_bearing_height
FEATURE [Sketcher::SketchObject] Sketch073
  AttachmentOffset = pos=(0,0,45) rot=(0,0,1;0rad)
  FullyConstrained = true
  MapMode = 5
  Placement = pos=(0,0,45) rot=(0,0,1;0rad)
  Support = -> [XY_Plane026]
  expr: .AttachmentOffset.Base.z = <<arm1 dims>>.body_height + <<arm1 dims>>.cover_thickness
  expr: Constraints[19] = <<arm1 dims>>.zaxis_vertical_bearing_diameter + 2 * <<arm1 dims>>.zaxis_wall_thickness
  expr: Constraints[1] = <<arm1 dims>>.zaxis_body_diameter - 2 * <<arm1 dims>>.zaxis_wall_thickness
  expr: Constraints[3] = <<vert base dims>>.base_smooth_rod_set_diameter
  expr: Constraints[47] = <<arm1 dims>>.zaxis_inner_wall_width
  expr: Constraints[54] = <<arm1 dims>>.zaxis_flat_side_distance - <<arm1 dims>>.zaxis_flat_wall_thickness
  sketch-geometry (21):
    g0: ArcOfCircle CenterX=0 CenterY=0 CenterZ=0 NormalX=0 NormalY=0 NormalZ=1 AngleXU=0 Radius=57 StartAngle=4.26893 EndAngle=5.15585
    g1: Circle CenterX=0 CenterY=0 CenterZ=0 NormalX=0 NormalY=0 NormalZ=1 AngleXU=0 Radius=47.5
    g2: LineSegment StartX=-33.5876 StartY=33.5876 StartZ=0 EndX=33.5876 EndY=33.5876 EndZ=0
    g3: LineSegment StartX=33.5876 StartY=33.5876 StartZ=0 EndX=33.5876 EndY=-33.5876 EndZ=0
    g4: ArcOfCircle CenterX=-33.5876 CenterY=33.5876 CenterZ=0 NormalX=0 NormalY=0 NormalZ=1 AngleXU=0 Radius=12.5 StartAngle=3.84177 EndAngle=7.1538
    g5: ArcOfCircle CenterX=33.5876 CenterY=33.5876 CenterZ=0 NormalX=0 NormalY=0 NormalZ=1 AngleXU=0 Radius=12.5 StartAngle=2.27098 EndAngle=5.77027
    g6: ArcOfCircle CenterX=33.5876 CenterY=-33.5876 CenterZ=0 NormalX=0 NormalY=0 NormalZ=1 AngleXU=0 Radius=12.5 StartAngle=0.512914 EndAngle=4.01221
    g7: ArcOfCircle CenterX=-33.5876 CenterY=-33.5876 CenterZ=0 NormalX=0 NormalY=0 NormalZ=1 AngleXU=0 Radius=12.5 StartAngle=5.41257 EndAngle=8.7246
    g8: ArcOfCircle CenterX=0 CenterY=0 CenterZ=0 NormalX=0 NormalY=0 NormalZ=1 AngleXU=0 Radius=57 StartAngle=2.69814 EndAngle=3.58505
    g9: ArcOfCircle CenterX=0 CenterY=0 CenterZ=0 NormalX=0 NormalY=0 NormalZ=1 AngleXU=0 Radius=57 StartAngle=1.12734 EndAngle=2.01425
    g10: ArcOfCircle CenterX=-46.9703 CenterY=22.3113 CenterZ=0 NormalX=0 NormalY=0 NormalZ=1 AngleXU=0 Radius=5 StartAngle=0.700182 EndAngle=2.69814
    g11: ArcOfCircle CenterX=-22.3113 CenterY=46.9703 CenterZ=0 NormalX=0 NormalY=0 NormalZ=1 AngleXU=0 Radius=5 StartAngle=2.01425 EndAngle=4.01221
    g12: ArcOfCircle CenterX=22.3113 CenterY=46.9703 CenterZ=0 NormalX=0 NormalY=0 NormalZ=1 AngleXU=0 Radius=5 StartAngle=5.41257 EndAngle=7.41053
    g13: ArcOfCircle CenterX=48.8356 CenterY=25 CenterZ=0 NormalX=0 NormalY=0 NormalZ=1 AngleXU=0 Radius=5 StartAngle=1.5708 EndAngle=2.62868
    g14: ArcOfCircle CenterX=-46.9703 CenterY=-22.3113 CenterZ=0 NormalX=0 NormalY=0 NormalZ=1 AngleXU=0 Radius=5 StartAngle=3.58505 EndAngle=5.583
    g15: ArcOfCircle CenterX=-22.3113 CenterY=-46.9703 CenterZ=0 NormalX=0 NormalY=0 NormalZ=1 AngleXU=0 Radius=5 StartAngle=2.27098 EndAngle=4.26893
    g16: ArcOfCircle CenterX=22.3113 CenterY=-46.9703 CenterZ=0 NormalX=0 NormalY=0 NormalZ=1 AngleXU=0 Radius=5 StartAngle=5.15585 EndAngle=7.1538
    g17: ArcOfCircle CenterX=48.8356 CenterY=-25 CenterZ=0 NormalX=0 NormalY=0 NormalZ=1 AngleXU=0 Radius=5 StartAngle=3.65451 EndAngle=4.71239
    g18: LineSegment StartX=54 StartY=-30 StartZ=0 EndX=54 EndY=30 EndZ=0
    g19: LineSegment StartX=54 StartY=30 StartZ=0 EndX=48.8356 EndY=30 EndZ=0
    g20: LineSegment StartX=54 StartY=-30 StartZ=0 EndX=48.8356 EndY=-30 EndZ=0
  constraints (55):
    c: Coincident(g0,g-1)
    c: Diameter(g0) = 114
    c: Coincident(g1,g0)
    c: Diameter(g1) = 95
    c: PointOnObject(g2,g1)
    c: PointOnObject(g2,g1)
    c: Horizontal(g2)
    c: Coincident(g3,g2)
    c: PointOnObject(g3,g1)
    c: Vertical(g3)
    c: Equal(g2,g3)
    c: Coincident(g4,g2)
    c: Coincident(g5,g2)
    c: Coincident(g6,g3)
    c: PointOnObject(g7,g1)
    c: Horizontal(g7,g6)
    c: Equal(g7,g6)
    c: Equal(g6,g5)
    c: Equal(g5,g4)
    c: Diameter(g7) = 25
    c: Equal(g0,g8)
    c: Coincident(g0,g8)
    c: Equal(g0,g9)
    c: Coincident(g0,g9)
    c: Tangent(g4,g10) = 1.5708
    c: Tangent(g8,g10) = -1.5708
    c: Radius(g10) = 5
    c: Tangent(g9,g11) = -1.5708
    c: Tangent(g4,g11) = 1.5708
    c: Equal(g11,g10)
    c: Tangent(g9,g12) = -1.5708
    c: Tangent(g5,g12) = 1.5708
    c: Equal(g12,g11)
    c: Tangent(g5,g13) = 1.5708
    c: Equal(g13,g12)
    c: Tangent(g8,g14) = -1.5708
    c: Tangent(g7,g14) = 1.5708
    c: Tangent(g7,g15) = 1.5708
    c: Tangent(g0,g15) = -1.5708
    c: Tangent(g0,g16) = -1.5708
    c: Tangent(g6,g16) = 1.5708
    c: Tangent(g6,g17) = 1.5708
    c: Equal(g14,g15)
    c: Equal(g15,g16)
    c: Equal(g16,g17)
    c: Equal(g14,g10)
    c: Symmetric(g18,g18,g-1)
    c: DistanceY(g18,g18) = 60
    c: Coincident(g19,g18)
    c: Horizontal(g19)
    c: Tangent(g13,g19) = -1.5708
    c: Coincident(g20,g18)
    c: Horizontal(g20)
    c: Tangent(g17,g20) = 1.5708
    c: DistanceX(g0,g18) = 54
FEATURE [PartDesign::Pocket] Pocket050
  BaseFeature = -> Pocket049
  Direction = (0,0,-1)
  Length = 39
  Length2 = 5
  Profile = -> Sketch073
  ReferenceAxis = -> Sketch073 [N_Axis]
  Type = 0
  expr: Length = <<arm1 dims>>.body_height + <<arm1 dims>>.cover_thickness - <<arm1 dims>>.zaxis_bottom_thickness
FEATURE [Sketcher::SketchObject] Sketch074
  AttachmentOffset = pos=(0,0,6) rot=(0,0,1;0rad)
  FullyConstrained = true
  MapMode = 5
  Placement = pos=(0,0,6) rot=(0,0,1;0rad)
  Support = -> [XY_Plane026]
  expr: .AttachmentOffset.Base.z = <<arm1 dims>>.zaxis_bottom_thickness
  expr: Constraints[32] = <<vert base dims>>.base_smooth_rod_set_diameter
  expr: Constraints[35] = <<arm1 dims>>.zaxis_inner_wall_thickness
  expr: Constraints[37] = <<arm1 dims>>.zaxis_rods_tolerance / 2 + <<arm1 dims>>.zaxis_vertical_bearing_diameter / 2
  expr: Constraints[38] = <<arm1 dims>>.zaxis_rods_tolerance / 2 + <<arm1 dims>>.zaxis_vertical_bearing_diameter / 2
  sketch-geometry (17):
    g0: LineSegment StartX=-23.8376 StartY=36.5876 StartZ=0 EndX=23.8376 EndY=36.5876 EndZ=0
    g1: LineSegment StartX=23.8376 StartY=36.5876 StartZ=0 EndX=23.8376 EndY=30.5876 EndZ=0
    g2: LineSegment StartX=23.8376 StartY=30.5876 StartZ=0 EndX=-23.8376 EndY=30.5876 EndZ=0
    g3: LineSegment StartX=-23.8376 StartY=30.5876 StartZ=0 EndX=-23.8376 EndY=36.5876 EndZ=0
    g4: LineSegment StartX=-36.5876 StartY=23.8376 StartZ=0 EndX=-30.5876 EndY=23.8376 EndZ=0
    g5: LineSegment StartX=-30.5876 StartY=23.8376 StartZ=0 EndX=-30.5876 EndY=-23.8376 EndZ=0
    g6: LineSegment StartX=-30.5876 StartY=-23.8376 StartZ=0 EndX=-36.5876 EndY=-23.8376 EndZ=0
    g7: LineSegment StartX=-36.5876 StartY=-23.8376 StartZ=0 EndX=-36.5876 EndY=23.8376 EndZ=0
    g8: LineSegment StartX=-23.8376 StartY=-36.5876 StartZ=0 EndX=23.8376 EndY=-36.5876 EndZ=0
    g9: LineSegment StartX=23.8376 StartY=-36.5876 StartZ=0 EndX=23.8376 EndY=-30.5876 EndZ=0
    g10: LineSegment StartX=23.8376 StartY=-30.5876 StartZ=0 EndX=-23.8376 EndY=-30.5876 EndZ=0
    g11: LineSegment StartX=-23.8376 StartY=-30.5876 StartZ=0 EndX=-23.8376 EndY=-36.5876 EndZ=0
    g12: Circle CenterX=0 CenterY=0 CenterZ=0 NormalX=0 NormalY=0 NormalZ=1 AngleXU=0 Radius=47.5
    g13: LineSegment StartX=-33.5876 StartY=33.5876 StartZ=0 EndX=33.5876 EndY=33.5876 EndZ=0
    g14: LineSegment StartX=33.5876 StartY=33.5876 StartZ=0 EndX=33.5876 EndY=-33.5876 EndZ=0
    g15: LineSegment StartX=33.5876 StartY=-33.5876 StartZ=0 EndX=-33.5876 EndY=-33.5876 EndZ=0
    g16: LineSegment StartX=-33.5876 StartY=-33.5876 StartZ=0 EndX=-33.5876 EndY=33.5876 EndZ=0
  constraints (46):
    c: Coincident(g0,g1)
    c: Coincident(g1,g2)
    c: Coincident(g2,g3)
    c: Coincident(g3,g0)
    c: Horizontal(g0)
    c: Horizontal(g2)
    c: Vertical(g3)
    c: Coincident(g4,g5)
    c: Coincident(g5,g6)
    c: Coincident(g6,g7)
    c: Coincident(g7,g4)
    c: Horizontal(g4)
    c: Horizontal(g6)
    c: Vertical(g7)
    c: Coincident(g8,g9)
    c: Coincident(g9,g10)
    c: Coincident(g10,g11)
    c: Coincident(g11,g8)
    c: Horizontal(g8)
    c: Horizontal(g10)
    c: Vertical(g9)
    c: Vertical(g11)
    c: Coincident(g12,g-1)
    c: Coincident(g13,g14)
    c: Coincident(g14,g15)
    c: Coincident(g15,g16)
    c: Coincident(g16,g13)
    c: Horizontal(g13)
    c: Horizontal(g15)
    c: Vertical(g14)
    c: PointOnObject(g13,g12)
    c: PointOnObject(g14,g12)
    c: Diameter(g12) = 95
    c: Equal(g16,g15)
    c: PointOnObject(g15,g12)
    c: DistanceY(g1,g1) = 6
    c: Symmetric(g0,g1,g13)
    c: DistanceX(g0,g13) = 9.75
    c: DistanceX(g13,g2) = 9.75
    c: Symmetric(g4,g5,g-1)
    c: Symmetric(g4,g4,g16)
    c: Equal(g3,g4)
    c: Equal(g5,g2)
    c: Symmetric(g10,g2,g-1)
    c: Equal(g11,g3)
    c: Equal(g10,g2)
FEATURE [PartDesign::Pad] Pad028
  BaseFeature = -> Pocket050
  Direction = (0,0,1)
  Length = 28
  Length2 = 10
  Profile = -> Sketch074
  ReferenceAxis = -> Sketch074 [N_Axis]
  Type = 0
  expr: Length = <<arm1 dims>>.zaxis_inner_wall_height
FEATURE [Sketcher::SketchObject] Sketch075
  AttachmentOffset = pos=(0,0,6) rot=(0,0,1;0rad)
  FullyConstrained = true
  MapMode = 5
  Placement = pos=(0,0,6) rot=(0,0,1;0rad)
  Support = -> [XY_Plane026]
  expr: .AttachmentOffset.Base.z = <<arm1 dims>>.zaxis_bottom_thickness
  expr: Constraints[0] = <<arm1 dims>>.zaxis_lead_screw_outer_diameter
  expr: Constraints[1] = <<vert base dims>>.base_stepper_shaft_distance
  sketch-geometry (1):
    g0: Circle CenterX=33 CenterY=0 CenterZ=0 NormalX=0 NormalY=0 NormalZ=1 AngleXU=0 Radius=5.1
  constraints (3):
    c: Diameter(g0) = 10.2
    c: DistanceX(g-1,g0) = 33
    c: Horizontal(g0,g-1)
FEATURE [PartDesign::Pocket] Pocket051
  BaseFeature = -> Pad028
  Direction = (0,0,-1)
  Length = 2
  Length2 = 5
  Profile = -> Sketch075
  ReferenceAxis = -> Sketch075 [N_Axis]
  Type = 0
  expr: Length = <<arm1 dims>>.zaxis_lead_screw_inset_depth
FEATURE [Part::Part2DObjectPython] ShapeString014  # Draft 2D object (typed FeaturePython)
  AttachmentOffset = pos=(-6,44,6) rot=(0,0,1;0rad)
  FontFile = <userpath>/FreeCAD/Font/ARLRDBD.TTF
  MakeFace = true
  MapMode = 5
  Placement = pos=(-6,44,6) rot=(0,0,1;0rad)
  Size = 5
  String = v1.0
  Support = -> [XY_Plane026]
  Tracking = 0
  expr: .AttachmentOffset.Base.z = <<arm1 dims>>.zaxis_bottom_thickness
  expr: Size = <<global settings>>.label_font_size
FEATURE [PartDesign::Pocket] Pocket052
  BaseFeature = -> Pocket051
  Direction = (0,0,-1)
  Length = 0.4
  Length2 = 5
  Profile = -> ShapeString014
  ReferenceAxis = -> ShapeString014 [N_Axis]
  Type = 0
  expr: Length = <<global settings>>.label_text_depth
FEATURE [Sketcher::SketchObject] Sketch077
  AttachmentOffset = pos=(0,0,62) rot=(0,0,1;0rad)
  FullyConstrained = true
  MapMode = 5
  Placement = pos=(62,-1.38e-14,1.38e-14) rot=(0.57735,0.57735,0.57735;2.0944rad)
  Support = -> [YZ_Plane026]
  expr: .AttachmentOffset.Base.z = <<arm1 dims>>.zaxis_flat_side_distance
  expr: Constraints[11] = <<arm1 dims>>.mount_window_height
  expr: Constraints[12] = <<arm1 dims>>.mount_window_width
  expr: Constraints[14] = <<arm1 dims>>.mount_window_fillet_radius
  expr: Constraints[25] = <<arm1 dims>>.mount_hole_distance_vert
  expr: Constraints[26] = <<arm1 dims>>.mount_hole_distance_horiz
  expr: Constraints[27] = <<arm1 dims>>.mount_hole_radius
  expr: Constraints[28] = <<arm1 dims>>.body_height + <<arm1 dims>>.cover_thickness - <<arm1 dims>>.mount_window_offset
  expr: Constraints[29] = <<arm1 dims>>.body_height + <<arm1 dims>>.cover_thickness - <<arm1 dims>>.mount_hole_offset
  sketch-geometry (12):
    g0: LineSegment StartX=-19 StartY=33 StartZ=0 EndX=19 EndY=33 EndZ=0
    g1: LineSegment StartX=20 StartY=32 StartZ=0 EndX=20 EndY=9 EndZ=0
    g2: LineSegment StartX=19 StartY=8 StartZ=0 EndX=-19 EndY=8 EndZ=0
    g3: LineSegment StartX=-20 StartY=9 StartZ=0 EndX=-20 EndY=32 EndZ=0
    g4: ArcOfCircle CenterX=19 CenterY=9 CenterZ=0 NormalX=0 NormalY=0 NormalZ=1 AngleXU=0 Radius=1 StartAngle=4.71239 EndAngle=6.28319
    g5: ArcOfCircle CenterX=19 CenterY=32 CenterZ=0 NormalX=0 NormalY=0 NormalZ=1 AngleXU=0 Radius=1 StartAngle=-2.7e-15 EndAngle=1.5708
    g6: ArcOfCircle CenterX=-19 CenterY=32 CenterZ=0 NormalX=0 NormalY=0 NormalZ=1 AngleXU=0 Radius=1 StartAngle=1.5708 EndAngle=3.14159
    g7: ArcOfCircle CenterX=-19 CenterY=9 CenterZ=0 NormalX=0 NormalY=0 NormalZ=1 AngleXU=0 Radius=1 StartAngle=3.14159 EndAngle=4.71239
    g8: Circle CenterX=25.5 CenterY=28.5 CenterZ=0 NormalX=0 NormalY=0 NormalZ=1 AngleXU=0 Radius=2.55
    g9: Circle CenterX=25.5 CenterY=10.5 CenterZ=0 NormalX=0 NormalY=0 NormalZ=1 AngleXU=0 Radius=2.55
    g10: Circle CenterX=-25.5 CenterY=10.5 CenterZ=0 NormalX=0 NormalY=0 NormalZ=1 AngleXU=0 Radius=2.55
    g11: Circle CenterX=-25.5 CenterY=28.5 CenterZ=0 NormalX=0 NormalY=0 NormalZ=1 AngleXU=0 Radius=2.55
  constraints (30):
    c: Horizontal(g0)
    c: Vertical(g1)
    c: Vertical(g3)
    c: Tangent(g2,g4) = 1.5708
    c: Tangent(g1,g4) = 1.5708
    c: Tangent(g1,g5) = 1.5708
    c: Tangent(g0,g5) = 1.5708
    c: Tangent(g0,g6) = 1.5708
    c: Tangent(g3,g6) = 1.5708
    c: Tangent(g3,g7) = 1.5708
    c: Tangent(g2,g7) = 1.5708
    c: DistanceY(g2,g0) = 25
    c: DistanceX(g3,g1) = 40
    c: Symmetric(g2,g2,g-2)
    c: Diameter(g4) = 2
    c: Equal(g4,g5)
    c: Equal(g5,g6)
    c: Equal(g6,g7)
    c: Equal(g11,g10)
    c: Equal(g10,g9)
    c: Equal(g9,g8)
    c: Symmetric(g10,g9,g-2)
    c: Vertical(g10,g11)
    c: Vertical(g9,g8)
    c: Horizontal(g8,g11)
    c: DistanceY(g9,g8) = 18
    c: DistanceX(g10,g9) = 51
    c: Diameter(g9) = 5.1
    c: DistanceY(g-1,g0) = 33
    c: DistanceY(g-1,g8) = 28.5
FEATURE [PartDesign::Pocket] Pocket053
  BaseFeature = -> Pocket052
  Direction = (-1,2e-16,-3e-16)
  Length = 5
  Length2 = 5
  Profile = -> Sketch077
  ReferenceAxis = -> Sketch077 [N_Axis]
  Type = 2
FEATURE [PartDesign::Body] Body014  label="arm1 zaxis mount"
  Group = -> [Sketch071,Pad027,Sketch072,Pocket049,Sketch073,Pocket050,Sketch074,Pad028,Sketch075,Pocket051,ShapeString014,Pocket052,Sketch077,Pocket053]
  Origin = -> Origin026
  Tip = -> Pocket053
FEATURE [Part::FeaturePython] Clone007  label="arm1 zaxis mount001"  # Draft clone (typed FeaturePython)
  AttacherType = Attacher::AttachEngine3D
  Fuse = false
  Objects = -> [Body014]
  Placement = pos=(0,0,45) rot=(1,0,0;3.14159rad)
  Scale = (1,1,1)
FEATURE [App::Part] Part007  label="Constructed arm1"
  Group = -> [Clone001,Clone002,Clone007]
  Origin = -> Origin023
FEATURE [App::Part] Part006  label="Main Arm 1"
  Group = -> [Body012,Spreadsheet003,Body013,Part007,Body014]
  Origin = -> Origin020
FEATURE [Spreadsheet::Sheet] Spreadsheet006  label="base dims"
  cells = A2=base; B2=width; C2(width)==140mm; B3=length; C3(length)==215mm; B4=radius; C4(radius)==60mm; B5=height; C5(height)==45mm; B6=wall thickness; C6(wall_thickness)==8mm; B7=bottom thickness; C7(bottom_thickness)==10mm; B8=main axl diameter; C8(main_axl_diameter)==40mm; B9=main axl hole offset; C9(main_axl_hole_offset)==150mm; B10=main axl bearing diameter; C10(main_axl_bearing_diameter)==47mm; B11=main axl bearing height; C11(main_axl_bearing_height)==7mm; B12=pulley hole diameter; C12(pulley_hole_diameter)==15mm; B13=pulley hole offset; C13(pulley_hole_offset)==71mm; B14=pulley bearing diameter; C14(pulley_bearing_diameter)==22mm; B15=pulley wall thickness; C15(pulley_wall_thickness)==3mm; B16=pulley wall height; C16(pulley_wall_height)==8.5mm; B17=pulley bearing height; C17(pulley_bearing_height)==8mm; B18=pulley bottom inset; C18(pulley_bottom_inset)==7mm; B19=pulley bridge thickness; C19==3.5mm; B20=tightener hole distance; C20(tightener_hole_distance)==19mm; B21=tightener hole offset; C21(tightener_hole_offset)==105mm; B22=limit switch offset; C22(limit_switch_offset)==102mm; B23=limit switch ver offset; C23(limit_switch_ver_offset)==2mm; B24=limit switch angle; C24(limit_switch_angle)==29deg; B25=notch distance; C25(notch_distance)==3mm; B26=cover hole inner diameter; C26(cover_hole_inner_diameter)==4.1mm; B27=notch diameter; C27(notch_diameter)==11.1mm; B28=notch1 distance; C28(notch1_distance)==20mm; B29=notch2 distance; C29(notch2_distance)==75mm; B30=notch3 distance; C30(notch3_distance)==130mm; B31=notch angle; C31(notch_angle)==22.5deg; B32=top notch distance; C32(top_notch_distance)==46mm; B33=nut depth; C33(nut_depth)==10mm; B34=reinforcement diameter; C34(reinforcement_diameter)==61mm; B35=reinforcement height; C35(reinforcement_height)==8mm; B36=hole12 center offset; C36(hole12_center_offset)==8mm; B37=hole1 top offset; C37(hole1_top_offset)==20mm; B38=hole distance; C38(hole_distance)==12mm; B39=hole34 top offset; C39(hole34_top_offset)==79mm; B40=hole3 center offset; C40(hole3_center_ffset)==36mm; B41=hole5 top offset; C41(hole5_top_offset)==91mm; B42=hole5 center offset; C42(hole5_center_offset)==42mm; B43=top hole row1 height; C43(top_hole_row1_height)==23mm; B44=top hole row distance; C44(top_hole_row_distance)==14mm; B45=top hole offset; C45(top_hole_offset)==50mm; A46=motor; B46=platform thickness; C46(motor_platform_thickness)==8mm; B47=hole diameter; C47(motor_hole_diameter)==25mm; B48=hole straight; C48(motor_hole_straight)==3mm; B49=pulley distance; C49(motor_pulley_distance)==48mm; B50=inset; C50(motor_inset)==8mm
FEATURE [Part::Feature] Part__Feature176  label="Base_Base001"
  Placement = pos=(107.5,151,10) rot=(-1,0,0;1.5708rad)
  shape: bbox 215 x 140 x 45 mm, 316 faces (baked)
FEATURE [Sketcher::SketchObject] Sketch078
  FullyConstrained = true
  MapMode = 5
  Support = -> [XY_Plane028]
  expr: Constraints[12] = <<base dims>>.radius
  expr: Constraints[14] = <<base dims>>.length
  expr: Constraints[16] = <<base dims>>.main_axl_hole_offset
  expr: Constraints[17] = <<base dims>>.main_axl_diameter
  expr: Constraints[19] = <<base dims>>.pulley_hole_offset
  expr: Constraints[20] = <<base dims>>.pulley_hole_diameter
  expr: Constraints[33] = <<global settings>>.tightenerhole_length
  expr: Constraints[34] = <<global settings>>.tightenerhole_width
  expr: Constraints[38] = <<base dims>>.tightener_hole_distance + <<global settings>>.tightenerhole_width
  expr: Constraints[39] = <<global settings>>.m3_static_hole
  expr: Constraints[40] = <<base dims>>.limit_switch_offset
  expr: Constraints[41] = <<base dims>>.tightener_hole_offset
  expr: Constraints[42] = <<base dims>>.limit_switch_ver_offset
  expr: Constraints[44] = <<global settings>>.limit_switch_hole_distance
  expr: Constraints[47] = <<base dims>>.limit_switch_angle
  expr: Constraints[48] = <<base dims>>.hole1_top_offset
  expr: Constraints[49] = <<base dims>>.hole12_center_offset
  expr: Constraints[51] = <<base dims>>.cover_hole_inner_diameter
  expr: Constraints[53] = <<base dims>>.hole_distance
  expr: Constraints[57] = <<base dims>>.hole_distance
  expr: Constraints[58] = <<base dims>>.hole3_center_ffset
  expr: Constraints[59] = <<base dims>>.hole34_top_offset
  expr: Constraints[60] = <<base dims>>.hole5_top_offset
  expr: Constraints[61] = -<<base dims>>.hole5_center_offset
  expr: Constraints[7] = <<base dims>>.width
  sketch-geometry (24):
    g0: LineSegment StartX=0 StartY=70 StartZ=0 EndX=155 EndY=70 EndZ=0
    g1: LineSegment StartX=215 StartY=10 StartZ=0 EndX=215 EndY=-10 EndZ=0
    g2: LineSegment StartX=155 StartY=-70 StartZ=0 EndX=0 EndY=-70 EndZ=0
    g3: LineSegment StartX=0 StartY=-70 StartZ=0 EndX=0 EndY=70 EndZ=0
    g4: ArcOfCircle CenterX=155 CenterY=-10 CenterZ=0 NormalX=0 NormalY=0 NormalZ=1 AngleXU=0 Radius=60 StartAngle=4.71239 EndAngle=6.28319
    g5: ArcOfCircle CenterX=155 CenterY=10 CenterZ=0 NormalX=0 NormalY=0 NormalZ=1 AngleXU=0 Radius=60 StartAngle=0 EndAngle=1.5708
    g6: Circle CenterX=150 CenterY=0 CenterZ=0 NormalX=0 NormalY=0 NormalZ=1 AngleXU=0 Radius=20
    g7: Circle CenterX=71 CenterY=0 CenterZ=0 NormalX=0 NormalY=0 NormalZ=1 AngleXU=0 Radius=7.5
    g8: ArcOfCircle CenterX=105 CenterY=12 CenterZ=0 NormalX=0 NormalY=0 NormalZ=1 AngleXU=0 Radius=2.5 StartAngle=3.14159 EndAngle=6.28319
    g9: ArcOfCircle CenterX=105 CenterY=24 CenterZ=0 NormalX=0 NormalY=0 NormalZ=1 AngleXU=0 Radius=2.5 StartAngle=0 EndAngle=3.14159
    g10: LineSegment StartX=107.5 StartY=12 StartZ=0 EndX=107.5 EndY=24 EndZ=0
    g11: LineSegment StartX=102.5 StartY=24 StartZ=0 EndX=102.5 EndY=12 EndZ=0
    g12: ArcOfCircle CenterX=105 CenterY=-12 CenterZ=0 NormalX=0 NormalY=0 NormalZ=1 AngleXU=0 Radius=2.5 StartAngle=0 EndAngle=3.14159
    g13: ArcOfCircle CenterX=105 CenterY=-24 CenterZ=0 NormalX=0 NormalY=0 NormalZ=1 AngleXU=0 Radius=2.5 StartAngle=3.14159 EndAngle=6.28319
    g14: LineSegment StartX=102.5 StartY=-12 StartZ=0 EndX=102.5 EndY=-24 EndZ=0
    g15: LineSegment StartX=107.5 StartY=-24 StartZ=0 EndX=107.5 EndY=-12 EndZ=0
    g16: Circle CenterX=102 CenterY=-2 CenterZ=0 NormalX=0 NormalY=0 NormalZ=1 AngleXU=0 Radius=1.6
    g17: Circle CenterX=93.6911 CenterY=2.60569 CenterZ=0 NormalX=0 NormalY=0 NormalZ=1 AngleXU=0 Radius=1.6
    g18: LineSegment StartX=93.6911 StartY=2.60569 StartZ=0 EndX=102 EndY=-2 EndZ=0
    g19: Circle CenterX=20 CenterY=8 CenterZ=0 NormalX=0 NormalY=0 NormalZ=1 AngleXU=0 Radius=2.05
    g20: Circle CenterX=32 CenterY=8 CenterZ=0 NormalX=0 NormalY=0 NormalZ=1 AngleXU=0 Radius=2.05
    g21: Circle CenterX=79 CenterY=-36 CenterZ=0 NormalX=0 NormalY=0 NormalZ=1 AngleXU=0 Radius=2.05
    g22: Circle CenterX=79 CenterY=-48 CenterZ=0 NormalX=0 NormalY=0 NormalZ=1 AngleXU=0 Radius=2.05
    g23: Circle CenterX=91 CenterY=-42 CenterZ=0 NormalX=0 NormalY=0 NormalZ=1 AngleXU=0 Radius=2.05
  constraints (63):
    c: Coincident(g2,g3)
    c: Coincident(g3,g0)
    c: Horizontal(g0)
    c: Horizontal(g2)
    c: Vertical(g1)
    c: Vertical(g3)
    c: Symmetric(g0,g2,g-1)
    c: DistanceY(g3,g3) = 140
    c: Tangent(g2,g4) = 1.5708
    c: Tangent(g1,g4) = 1.5708
    c: Tangent(g1,g5) = 1.5708
    c: Tangent(g0,g5) = 1.5708
    c: Radius(g5) = 60
    c: Equal(g5,g4)
    c: DistanceX(g0,g1) = 215
    c: Horizontal(g-1,g6)
    c: DistanceX(g-1,g6) = 150
    c: Diameter(g6) = 40
    c: Horizontal(g7,g-1)
    c: DistanceX(g-1,g7) = 71
    c: Diameter(g7) = 15
    c: Tangent(g8,g10) = -1.5708
    c: Tangent(g10,g9) = -1.5708
    c: Tangent(g9,g11) = -1.5708
    c: Tangent(g11,g8) = -1.5708
    c: Equal(g8,g9)
    c: Vertical(g10)
    c: Tangent(g12,g14) = -1.5708
    c: Tangent(g14,g13) = -1.5708
    c: Tangent(g13,g15) = -1.5708
    c: Tangent(g15,g12) = -1.5708
    c: Equal(g12,g13)
    c: Vertical(g14)
    c: DistanceY(g10,g10) = 12
    c: Diameter(g9) = 5
    c: Equal(g15,g10)
    c: Equal(g12,g8)
    c: Symmetric(g8,g12,g-1)
    c: DistanceY(g12,g8) = 24
    c: Diameter(g16) = 3.2
    c: DistanceX(g16) = 102
    c: DistanceX(g-1,g9) = 105
    c: DistanceY(g16,g-1) = 2
    c: Equal(g17,g16)
    c: Distance(g17,g16) = 9.5
    c: Coincident(g18,g17)
    c: Coincident(g18,g16)
    c: Angle(g18,g-1) = 0.506145
    c: DistanceX(g-1,g19) = 20
    c: DistanceY(g-1,g19) = 8
    c: Horizontal(g19,g20)
    c: Diameter(g19) = 4.1
    c: Equal(g19,g20)
    c: DistanceX(g19,g20) = 12
    c: Equal(g21,g22)
    c: Equal(g22,g20)
    c: Vertical(g21,g22)
    c: DistanceY(g22,g21) = 12
    c: DistanceY(g21,g-1) = 36
    c: DistanceX(g21) = 79
    c: DistanceX(g23) = 91
    c: DistanceY(g23) = -42
    c: Equal(g23,g21)
FEATURE [PartDesign::Pad] Pad029
  Direction = (0,0,1)
  Length = 45
  Length2 = 10
  Profile = -> Sketch078
  ReferenceAxis = -> Sketch078 [N_Axis]
  Type = 0
  expr: Length = <<base dims>>.height
FEATURE [Sketcher::SketchObject] Sketch079
  AttachmentOffset = pos=(0,0,45) rot=(0,0,1;0rad)
  FullyConstrained = true
  MapMode = 5
  Placement = pos=(0,0,45) rot=(0,0,1;0rad)
  Support = -> [XY_Plane028]
  expr: .AttachmentOffset.Base.z = <<base dims>>.height
  expr: Constraints[10] = <<base dims>>.wall_thickness
  expr: Constraints[11] = <<base dims>>.radius - <<base dims>>.wall_thickness
  expr: Constraints[130] = <<base dims>>.notch_angle
  expr: Constraints[13] = <<base dims>>.length - <<base dims>>.wall_thickness
  expr: Constraints[145] = 90deg - <<base dims>>.notch_angle
  expr: Constraints[170] = <<base dims>>.top_notch_distance
  expr: Constraints[17] = <<base dims>>.notch_distance
  expr: Constraints[24] = <<base dims>>.notch1_distance
  expr: Constraints[36] = <<base dims>>.notch2_distance
  expr: Constraints[46] = <<base dims>>.notch3_distance
  expr: Constraints[61] = 90deg - <<base dims>>.notch_angle
  expr: Constraints[66] = <<base dims>>.width - 2 * <<base dims>>.radius
  expr: Constraints[79] = <<base dims>>.notch_angle
  expr: Constraints[8] = <<base dims>>.width - 2 * <<base dims>>.wall_thickness
  sketch-geometry (66):
    g0: LineSegment StartX=8 StartY=62 StartZ=0 EndX=14.45 EndY=62 EndZ=0
    g1: LineSegment StartX=207 StartY=10 StartZ=0 EndX=207 EndY=-10 EndZ=0
    g2: LineSegment StartX=155 StartY=-62 StartZ=0 EndX=135.55 EndY=-62 EndZ=0
    g3: LineSegment StartX=8 StartY=-62 StartZ=0 EndX=8 EndY=-28.55 EndZ=0
    g4: ArcOfCircle CenterX=155 CenterY=10 CenterZ=0 NormalX=0 NormalY=0 NormalZ=1 AngleXU=0 Radius=52 StartAngle=0 EndAngle=0.285765
    g5: ArcOfCircle CenterX=155 CenterY=-10 CenterZ=0 NormalX=0 NormalY=0 NormalZ=1 AngleXU=0 Radius=52 StartAngle=4.71239 EndAngle=4.99815
    g6: LineSegment StartX=14.45 StartY=-62 StartZ=0 EndX=14.45 EndY=-59 EndZ=0
    g7: LineSegment StartX=25.55 StartY=-62 StartZ=0 EndX=25.55 EndY=-59 EndZ=0
    g8: ArcOfCircle CenterX=20 CenterY=-59 CenterZ=0 NormalX=0 NormalY=0 NormalZ=1 AngleXU=0 Radius=5.55 StartAngle=0 EndAngle=3.14159
    g9: Circle CenterX=20 CenterY=-59 CenterZ=0 NormalX=0 NormalY=0 NormalZ=1 AngleXU=0 Radius=2.05
    g10: LineSegment StartX=14.45 StartY=-62 StartZ=0 EndX=8 EndY=-62 EndZ=0
    g11: LineSegment StartX=69.45 StartY=-62 StartZ=0 EndX=69.45 EndY=-59 EndZ=0
    g12: LineSegment StartX=80.55 StartY=-62 StartZ=0 EndX=80.55 EndY=-59 EndZ=0
    g13: ArcOfCircle CenterX=75 CenterY=-59 CenterZ=0 NormalX=0 NormalY=0 NormalZ=1 AngleXU=0 Radius=5.55 StartAngle=0 EndAngle=3.14159
    g14: Circle CenterX=75 CenterY=-59 CenterZ=0 NormalX=0 NormalY=0 NormalZ=1 AngleXU=0 Radius=2.05
    g15: LineSegment StartX=69.45 StartY=-62 StartZ=0 EndX=25.55 EndY=-62 EndZ=0
    g16: LineSegment StartX=124.45 StartY=-62 StartZ=0 EndX=124.45 EndY=-59 EndZ=0
    g17: LineSegment StartX=135.55 StartY=-62 StartZ=0 EndX=135.55 EndY=-59 EndZ=0
    g18: ArcOfCircle CenterX=130 CenterY=-59 CenterZ=0 NormalX=0 NormalY=0 NormalZ=1 AngleXU=0 Radius=5.55 StartAngle=0 EndAngle=3.14159
    g19: Circle CenterX=130 CenterY=-59 CenterZ=0 NormalX=0 NormalY=0 NormalZ=1 AngleXU=0 Radius=2.05
    g20: LineSegment StartX=124.45 StartY=-62 StartZ=0 EndX=80.55 EndY=-62 EndZ=0
    g21: LineSegment StartX=169.658 StartY=-59.8912 StartZ=0 EndX=168.51 EndY=-57.1196 EndZ=0
    g22: LineSegment StartX=179.913 StartY=-55.6434 StartZ=0 EndX=178.765 EndY=-52.8718 EndZ=0
    g23: ArcOfCircle CenterX=173.638 CenterY=-54.9957 CenterZ=0 NormalX=0 NormalY=0 NormalZ=1 AngleXU=0 Radius=5.55 StartAngle=0.392699 EndAngle=3.53429
    g24: Circle CenterX=173.638 CenterY=-54.9957 CenterZ=0 NormalX=0 NormalY=0 NormalZ=1 AngleXU=0 Radius=2.05
    g25: ArcOfCircle CenterX=155 CenterY=-10 CenterZ=0 NormalX=0 NormalY=0 NormalZ=1 AngleXU=0 Radius=52 StartAngle=5.21202 EndAngle=5.78355
    g26: LineSegment StartX=200.643 StartY=-34.9134 StartZ=0 EndX=197.872 EndY=-33.7654 EndZ=0
    g27: LineSegment StartX=204.891 StartY=-24.6583 StartZ=0 EndX=202.12 EndY=-23.5103 EndZ=0
    g28: ArcOfCircle CenterX=199.996 CenterY=-28.6378 CenterZ=0 NormalX=0 NormalY=0 NormalZ=1 AngleXU=0 Radius=5.55 StartAngle=1.1781 EndAngle=4.31969
    g29: Circle CenterX=199.996 CenterY=-28.6378 CenterZ=0 NormalX=0 NormalY=0 NormalZ=1 AngleXU=0 Radius=2.05
    g30: ArcOfCircle CenterX=155 CenterY=-10 CenterZ=0 NormalX=0 NormalY=0 NormalZ=1 AngleXU=0 Radius=52 StartAngle=5.99742 EndAngle=6.28319
    g31: LineSegment StartX=25.55 StartY=62 StartZ=0 EndX=25.55 EndY=59 EndZ=0
    g32: LineSegment StartX=14.45 StartY=62 StartZ=0 EndX=14.45 EndY=59 EndZ=0
    g33: ArcOfCircle CenterX=20 CenterY=59 CenterZ=0 NormalX=0 NormalY=0 NormalZ=1 AngleXU=0 Radius=5.55 StartAngle=3.14159 EndAngle=6.28319
    g34: Circle CenterX=20 CenterY=59 CenterZ=0 NormalX=0 NormalY=0 NormalZ=1 AngleXU=0 Radius=2.05
    g35: LineSegment StartX=25.55 StartY=62 StartZ=0 EndX=69.45 EndY=62 EndZ=0
    g36: LineSegment StartX=80.55 StartY=62 StartZ=0 EndX=80.55 EndY=59 EndZ=0
    g37: LineSegment StartX=69.45 StartY=62 StartZ=0 EndX=69.45 EndY=59 EndZ=0
    g38: ArcOfCircle CenterX=75 CenterY=59 CenterZ=0 NormalX=0 NormalY=0 NormalZ=1 AngleXU=0 Radius=5.55 StartAngle=3.14159 EndAngle=6.28319
    g39: Circle CenterX=75 CenterY=59 CenterZ=0 NormalX=0 NormalY=0 NormalZ=1 AngleXU=0 Radius=2.05
    g40: LineSegment StartX=80.55 StartY=62 StartZ=0 EndX=124.45 EndY=62 EndZ=0
    g41: LineSegment StartX=135.55 StartY=62 StartZ=0 EndX=135.55 EndY=59 EndZ=0
    g42: LineSegment StartX=124.45 StartY=62 StartZ=0 EndX=124.45 EndY=59 EndZ=0
    g43: ArcOfCircle CenterX=130 CenterY=59 CenterZ=0 NormalX=0 NormalY=0 NormalZ=1 AngleXU=0 Radius=5.55 StartAngle=3.14159 EndAngle=6.28319
    g44: Circle CenterX=130 CenterY=59 CenterZ=0 NormalX=0 NormalY=0 NormalZ=1 AngleXU=0 Radius=2.05
    g45: LineSegment StartX=135.55 StartY=62 StartZ=0 EndX=155 EndY=62 EndZ=0
    g46: LineSegment StartX=204.891 StartY=24.6583 StartZ=0 EndX=202.12 EndY=23.5103 EndZ=0
    g47: LineSegment StartX=200.643 StartY=34.9134 StartZ=0 EndX=197.872 EndY=33.7654 EndZ=0
    g48: ArcOfCircle CenterX=199.996 CenterY=28.6378 CenterZ=0 NormalX=0 NormalY=0 NormalZ=1 AngleXU=0 Radius=5.55 StartAngle=1.9635 EndAngle=5.10509
    g49: Circle CenterX=199.996 CenterY=28.6378 CenterZ=0 NormalX=0 NormalY=0 NormalZ=1 AngleXU=0 Radius=2.05
    g50: ArcOfCircle CenterX=155 CenterY=10 CenterZ=0 NormalX=0 NormalY=0 NormalZ=1 AngleXU=0 Radius=52 StartAngle=0.499634 EndAngle=1.07116
    g51: LineSegment StartX=179.913 StartY=55.6434 StartZ=0 EndX=178.765 EndY=52.8718 EndZ=0
    g52: LineSegment StartX=169.658 StartY=59.8912 StartZ=0 EndX=168.51 EndY=57.1196 EndZ=0
    g53: ArcOfCircle CenterX=173.638 CenterY=54.9957 CenterZ=0 NormalX=0 NormalY=0 NormalZ=1 AngleXU=0 Radius=5.55 StartAngle=2.74889 EndAngle=5.89049
    g54: Circle CenterX=173.638 CenterY=54.9957 CenterZ=0 NormalX=0 NormalY=0 NormalZ=1 AngleXU=0 Radius=2.05
    g55: ArcOfCircle CenterX=155 CenterY=10 CenterZ=0 NormalX=0 NormalY=0 NormalZ=1 AngleXU=0 Radius=52 StartAngle=1.28503 EndAngle=1.5708
    g56: LineSegment StartX=8 StartY=-17.45 StartZ=0 EndX=11 EndY=-17.45 EndZ=0
    g57: LineSegment StartX=8 StartY=-28.55 StartZ=0 EndX=11 EndY=-28.55 EndZ=0
    g58: ArcOfCircle CenterX=11 CenterY=-23 CenterZ=0 NormalX=0 NormalY=0 NormalZ=1 AngleXU=0 Radius=5.55 StartAngle=4.71239 EndAngle=7.85398
    g59: Circle CenterX=11 CenterY=-23 CenterZ=0 NormalX=0 NormalY=0 NormalZ=1 AngleXU=0 Radius=2.05
    g60: LineSegment StartX=8 StartY=-17.45 StartZ=0 EndX=8 EndY=17.45 EndZ=0
    g61: LineSegment StartX=8 StartY=28.55 StartZ=0 EndX=11 EndY=28.55 EndZ=0
    g62: LineSegment StartX=8 StartY=17.45 StartZ=0 EndX=11 EndY=17.45 EndZ=0
    g63: ArcOfCircle CenterX=11 CenterY=23 CenterZ=0 NormalX=0 NormalY=0 NormalZ=1 AngleXU=0 Radius=5.55 StartAngle=4.71239 EndAngle=7.85398
    g64: Circle CenterX=11 CenterY=23 CenterZ=0 NormalX=0 NormalY=0 NormalZ=1 AngleXU=0 Radius=2.05
    g65: LineSegment StartX=8 StartY=28.55 StartZ=0 EndX=8 EndY=62 EndZ=0
  constraints (171):
    c: Coincident(g10,g3)
    c: Coincident(g65,g0)
    c: Horizontal(g0)
    c: Horizontal(g2)
    c: Coincident(g45,g55) = 1.5708
    c: Tangent(g1,g4) = 1.5708
    c: Coincident(g1,g30) = 1.5708
    c: Tangent(g2,g5) = 1.5708
    c: DistanceY(g3,g65) = 124
    c: Symmetric(g0,g10,g-1)
    c: DistanceX(g-1,g0) = 8
    c: Radius(g4) = 52
    c: Equal(g4,g5)
    c: DistanceX(g-1,g1) = 207
    c: Tangent(g6,g8) = 1.5708
    c: Tangent(g8,g7) = -1.5708
    c: Parallel(g6,g7)
    c: Distance(g7) = 3
    c: Equal(g7,g6)
    c: Diameter(g8) = 11.1
    c: Coincident(g9,g8)
    c: Diameter(g9) = 4.1
    c: Horizontal(g6,g10)
    c: Horizontal(g7,g6)
    c: DistanceX(g-1,g8) = 20
    c: Coincident(g6,g10)
    c: Coincident(g7,g15)
    c: Tangent(g11,g13) = 1.5708
    c: Tangent(g13,g12) = -1.5708
    c: Parallel(g11,g12)
    c: Equal(g7,g12) = 3
    c: Equal(g12,g11)
    c: Equal(g8,g13) = 11.1
    c: Coincident(g14,g13)
    c: Equal(g9,g14) = 4.1
    c: Horizontal(g12,g11)
    c: DistanceX(g-1,g13) = 75
    c: Horizontal(g11,g15)
    c: Coincident(g11,g15)
    c: Coincident(g20,g12)
    c: Tangent(g16,g18) = 1.5708
    c: Tangent(g18,g17) = -1.5708
    c: Parallel(g16,g17)
    c: Equal(g17,g16)
    c: Coincident(g19,g18)
    c: Horizontal(g17,g16)
    c: DistanceX(g-1,g18) = 130
    c: Equal(g16,g12)
    c: Horizontal(g16,g20)
    c: Coincident(g16,g20)
    c: Coincident(g2,g17)
    c: Equal(g18,g13)
    c: Equal(g19,g14)
    c: Tangent(g21,g23) = 1.5708
    c: Tangent(g23,g22) = -1.5708
    c: Parallel(g21,g22)
    c: Equal(g7,g22) = 3
    c: Equal(g22,g21)
    c: Equal(g8,g23) = 11.1
    c: Coincident(g24,g23)
    c: Equal(g9,g24) = 4.1
    c: Angle(g21,g2) = 1.1781
    c: Equal(g5,g25)
    c: Coincident(g5,g21)
    c: Coincident(g25,g22)
    c: Coincident(g5,g25)
    c: DistanceY(g1,g1) = 20
    c: Tangent(g26,g28) = 1.5708
    c: Tangent(g28,g27) = -1.5708
    c: Parallel(g26,g27)
    c: Equal(g7,g27) = 3
    c: Equal(g27,g26)
    c: Equal(g8,g28) = 11.1
    c: Coincident(g29,g28)
    c: Equal(g9,g29) = 4.1
    c: Equal(g25,g30)
    c: Coincident(g25,g26)
    c: Coincident(g30,g27)
    c: Coincident(g25,g30)
    c: Angle(g26,g2) = 0.392699
    c: Tangent(g31,g33) = 1.5708
    c: Tangent(g33,g32) = -1.5708
    c: Parallel(g31,g32)
    c: Equal(g7,g32) = 3
    c: Equal(g32,g31)
    c: Equal(g8,g33) = 11.1
    c: Coincident(g34,g33)
    c: Equal(g9,g34) = 4.1
    c: Vertical(g8,g33)
    c: Coincident(g0,g32)
    c: Coincident(g35,g31)
    c: Horizontal(g0,g31)
    c: Horizontal(g35)
    c: Tangent(g36,g38) = 1.5708
    c: Tangent(g38,g37) = -1.5708
    c: Parallel(g36,g37)
    c: Equal(g7,g37) = 3
    c: Equal(g37,g36)
    c: Equal(g8,g38) = 11.1
    c: Coincident(g39,g38)
    c: Equal(g9,g39) = 4.1
    c: Vertical(g38,g13)
    c: Coincident(g35,g37)
    c: Coincident(g40,g36)
    c: Horizontal(g35,g36)
    c: Horizontal(g40)
    c: Tangent(g41,g43) = 1.5708
    c: Tangent(g43,g42) = -1.5708
    c: Parallel(g41,g42)
    c: Equal(g7,g42) = 3
    c: Equal(g42,g41)
    c: Equal(g8,g43) = 11.1
    c: Coincident(g44,g43)
    c: Equal(g9,g44) = 4.1
    c: Vertical(g18,g43)
    c: Coincident(g40,g42)
    c: Coincident(g45,g41)
    c: Horizontal(g40,g41)
    c: Horizontal(g45)
    c: Tangent(g46,g48) = 1.5708
    c: Tangent(g48,g47) = -1.5708
    c: Parallel(g46,g47)
    c: Equal(g7,g47) = 3
    c: Equal(g47,g46)
    c: Equal(g8,g48) = 11.1
    c: Coincident(g49,g48)
    c: Equal(g9,g49) = 4.1
    c: Equal(g4,g50)
    c: Coincident(g4,g46)
    c: Coincident(g50,g47)
    c: Angle(g45,g47) = 0.392699
    c: Symmetric(g1,g1,g-1)
    c: Coincident(g4,g50)
    c: Tangent(g51,g53) = 1.5708
    c: Tangent(g53,g52) = -1.5708
    c: Parallel(g51,g52)
    c: Equal(g7,g52) = 3
    c: Equal(g52,g51)
    c: Equal(g8,g53) = 11.1
    c: Coincident(g54,g53)
    c: Equal(g9,g54) = 4.1
    c: Equal(g50,g55)
    c: Coincident(g50,g51)
    c: Coincident(g55,g52)
    c: Coincident(g50,g55)
    c: Angle(g45,g52) = 1.1781
    c: Tangent(g56,g58) = 1.5708
    c: Tangent(g58,g57) = -1.5708
    c: Parallel(g56,g57)
    c: Equal(g7,g57) = 3
    c: Equal(g57,g56)
    c: Equal(g8,g58) = 11.1
    c: Coincident(g59,g58)
    c: Equal(g9,g59) = 4.1
    c: Coincident(g3,g57)
    c: Coincident(g60,g56)
    c: Vertical(g3,g56)
    c: Vertical(g60)
    c: Tangent(g61,g63) = 1.5708
    c: Tangent(g63,g62) = -1.5708
    c: Parallel(g61,g62)
    c: Equal(g7,g62) = 3
    c: Equal(g62,g61)
    c: Equal(g8,g63) = 11.1
    c: Coincident(g64,g63)
    c: Equal(g9,g64) = 4.1
    c: Coincident(g60,g62)
    c: Coincident(g65,g61)
    c: Vertical(g65)
    c: Symmetric(g58,g63,g-1)
    c: DistanceY(g58,g63) = 46
FEATURE [PartDesign::Pocket] Pocket054
  BaseFeature = -> Pad029
  Direction = (0,0,-1)
  Length = 35
  Length2 = 5
  Profile = -> Sketch079
  ReferenceAxis = -> Sketch079 [N_Axis]
  Type = 0
  expr: Length = <<base dims>>.height - <<base dims>>.bottom_thickness
FEATURE [Sketcher::SketchObject] Sketch080
  AttachmentOffset = pos=(0,0,10) rot=(0,0,1;0rad)
  FullyConstrained = true
  MapMode = 5
  Placement = pos=(0,0,10) rot=(0,0,1;0rad)
  Support = -> [XY_Plane028]
  expr: .AttachmentOffset.Base.z = <<base dims>>.bottom_thickness
  expr: Constraints[10] = <<base dims>>.pulley_bearing_diameter
  expr: Constraints[8] = <<base dims>>.width / 2
  expr: Constraints[9] = <<base dims>>.pulley_hole_offset
  sketch-geometry (5):
    g0: LineSegment StartX=0 StartY=1.42e-14 StartZ=0 EndX=60 EndY=1.42e-14 EndZ=0
    g1: LineSegment StartX=71 StartY=-11 StartZ=0 EndX=71 EndY=-70 EndZ=0
    g2: LineSegment StartX=71 StartY=-70 StartZ=0 EndX=0 EndY=-70 EndZ=0
    g3: LineSegment StartX=0 StartY=-70 StartZ=0 EndX=0 EndY=1.42e-14 EndZ=0
    g4: ArcOfCircle CenterX=71 CenterY=1.42e-14 CenterZ=0 NormalX=0 NormalY=0 NormalZ=1 AngleXU=0 Radius=11 StartAngle=3.14159 EndAngle=4.71239
  constraints (15):
    c: Coincident(g1,g2)
    c: Coincident(g2,g3)
    c: Coincident(g3,g0)
    c: Horizontal(g0)
    c: Horizontal(g2)
    c: Vertical(g1)
    c: Vertical(g3)
    c: Coincident(g0,g-1)
    c: DistanceY(g3,g3) = 70
    c: DistanceX(g2,g2) = 71
    c: Diameter(g4) = 22
    c: Coincident(g4,g1)
    c: Coincident(g4,g0)
    c: Angle(g4) = 1.5708
    c: Horizontal(g4,g0)
FEATURE [PartDesign::Pad] Pad030
  BaseFeature = -> Pocket054
  Direction = (0,0,1)
  Length = 8
  Length2 = 10
  Profile = -> Sketch080
  ReferenceAxis = -> Sketch080 [N_Axis]
  Type = 0
  expr: Length = <<base dims>>.motor_platform_thickness
FEATURE [Sketcher::SketchObject] Sketch081
  AttachmentOffset = pos=(0,0,18) rot=(0,0,1;0rad)
  FullyConstrained = true
  MapMode = 5
  Placement = pos=(0,0,18) rot=(0,0,1;0rad)
  Support = -> [XY_Plane028]
  expr: .AttachmentOffset.Base.z = <<base dims>>.bottom_thickness + <<base dims>>.motor_platform_thickness
  expr: Constraints[12] = <<base dims>>.motor_pulley_distance
  expr: Constraints[20] = <<global settings>>.nema17_hole_distance
  expr: Constraints[44] = <<global settings>>.m3_static_hole
  expr: Constraints[45] = <<base dims>>.motor_hole_straight
  expr: Constraints[5] = <<base dims>>.motor_hole_diameter
  expr: Constraints[6] = <<base dims>>.motor_hole_straight
  expr: Constraints[8] = <<base dims>>.pulley_hole_offset
  sketch-geometry (25):
    g0: ArcOfCircle CenterX=35.9982 CenterY=-35.0018 CenterZ=0 NormalX=0 NormalY=0 NormalZ=1 AngleXU=0 Radius=12.5 StartAngle=2.35619 EndAngle=5.49779
    g1: ArcOfCircle CenterX=38.1195 CenterY=-32.8805 CenterZ=0 NormalX=0 NormalY=0 NormalZ=1 AngleXU=0 Radius=12.5 StartAngle=5.49779 EndAngle=8.63938
    g2: LineSegment StartX=44.837 StartY=-43.8406 StartZ=0 EndX=46.9584 EndY=-41.7193 EndZ=0
    g3: LineSegment StartX=29.2807 StartY=-24.0416 StartZ=0 EndX=27.1594 EndY=-26.163 EndZ=0
    g4: LineSegment StartX=37.0589 StartY=-33.9411 StartZ=0 EndX=71 EndY=0 EndZ=0
    g5: LineSegment StartX=37.0589 StartY=-12.0208 StartZ=0 EndX=15.1386 EndY=-33.9411 EndZ=0
    g6: LineSegment StartX=15.1386 StartY=-33.9411 StartZ=0 EndX=37.0589 EndY=-55.8614 EndZ=0
    g7: LineSegment StartX=37.0589 StartY=-55.8614 StartZ=0 EndX=58.9792 EndY=-33.9411 EndZ=0
    g8: LineSegment StartX=58.9792 StartY=-33.9411 StartZ=0 EndX=37.0589 EndY=-12.0208 EndZ=0
    g9: ArcOfCircle CenterX=38.1195 CenterY=-10.9602 CenterZ=0 NormalX=0 NormalY=0 NormalZ=1 AngleXU=0 Radius=1.6 StartAngle=5.49779 EndAngle=8.63938
    g10: ArcOfCircle CenterX=35.9982 CenterY=-13.0815 CenterZ=0 NormalX=0 NormalY=0 NormalZ=1 AngleXU=0 Radius=1.6 StartAngle=2.35619 EndAngle=5.49779
    g11: LineSegment StartX=36.9882 StartY=-9.82878 StartZ=0 EndX=34.8668 EndY=-11.9501 EndZ=0
    g12: LineSegment StartX=37.1296 StartY=-14.2128 StartZ=0 EndX=39.2509 EndY=-12.0915 EndZ=0
    g13: ArcOfCircle CenterX=14.0779 CenterY=-35.0018 CenterZ=0 NormalX=0 NormalY=0 NormalZ=1 AngleXU=0 Radius=1.6 StartAngle=2.35619 EndAngle=5.49779
    g14: ArcOfCircle CenterX=16.1992 CenterY=-32.8805 CenterZ=0 NormalX=0 NormalY=0 NormalZ=1 AngleXU=0 Radius=1.6 StartAngle=5.49779 EndAngle=8.63938
    g15: LineSegment StartX=15.2093 StartY=-36.1332 StartZ=0 EndX=17.3306 EndY=-34.0118 EndZ=0
    g16: LineSegment StartX=15.0679 StartY=-31.7491 StartZ=0 EndX=12.9465 EndY=-33.8704 EndZ=0
    g17: ArcOfCircle CenterX=57.9185 CenterY=-35.0018 CenterZ=0 NormalX=0 NormalY=0 NormalZ=1 AngleXU=0 Radius=1.6 StartAngle=2.35619 EndAngle=5.49779
    g18: ArcOfCircle CenterX=60.0398 CenterY=-32.8805 CenterZ=0 NormalX=0 NormalY=0 NormalZ=1 AngleXU=0 Radius=1.6 StartAngle=5.49779 EndAngle=8.63938
    g19: LineSegment StartX=59.0499 StartY=-36.1332 StartZ=0 EndX=61.1712 EndY=-34.0118 EndZ=0
    g20: LineSegment StartX=58.9085 StartY=-31.7491 StartZ=0 EndX=56.7872 EndY=-33.8704 EndZ=0
    g21: ArcOfCircle CenterX=35.9982 CenterY=-56.9221 CenterZ=0 NormalX=0 NormalY=0 NormalZ=1 AngleXU=0 Radius=1.6 StartAngle=2.35619 EndAngle=5.49779
    g22: ArcOfCircle CenterX=38.1195 CenterY=-54.8008 CenterZ=0 NormalX=0 NormalY=0 NormalZ=1 AngleXU=0 Radius=1.6 StartAngle=5.49779 EndAngle=8.63938
    g23: LineSegment StartX=37.1296 StartY=-58.0535 StartZ=0 EndX=39.2509 EndY=-55.9321 EndZ=0
    g24: LineSegment StartX=36.9882 StartY=-53.6694 StartZ=0 EndX=34.8668 EndY=-55.7907 EndZ=0
  constraints (60):
    c: Tangent(g0,g2) = -1.5708
    c: Tangent(g2,g1) = -1.5708
    c: Tangent(g1,g3) = -1.5708
    c: Tangent(g3,g0) = -1.5708
    c: Equal(g0,g1)
    c: Diameter(g0) = 25
    c: Distance(g3) = 3
    c: Horizontal(g4,g-1)
    c: DistanceX(g-1,g4) = 71
    c: Symmetric(g0,g1,g4)
    c: Parallel(g3,g4)
    c: Angle(g-1,g4) = 0.785398
    c: Distance(g4,g4) = 48
    c: Coincident(g5,g6)
    c: Coincident(g6,g7)
    c: Coincident(g7,g8)
    c: Coincident(g8,g5)
    c: Equal(g8,g5)
    c: Equal(g5,g6)
    c: Equal(g6,g7)
    c: Distance(g7) = 31
    c: Perpendicular(g8,g5)
    c: Parallel(g5,g4)
    c: Symmetric(g5,g7,g4)
    c: Tangent(g9,g11) = -1.5708
    c: Tangent(g11,g10) = -1.5708
    c: Tangent(g10,g12) = -1.5708
    c: Tangent(g12,g9) = -1.5708
    c: Equal(g9,g10)
    c: Tangent(g13,g15) = -1.5708
    c: Tangent(g15,g14) = -1.5708
    c: Tangent(g14,g16) = -1.5708
    c: Tangent(g16,g13) = -1.5708
    c: Equal(g13,g14)
    c: Tangent(g17,g19) = -1.5708
    c: Tangent(g19,g18) = -1.5708
    c: Tangent(g18,g20) = -1.5708
    c: Tangent(g20,g17) = -1.5708
    c: Equal(g17,g18)
    c: Tangent(g21,g23) = -1.5708
    c: Tangent(g23,g22) = -1.5708
    c: Tangent(g22,g24) = -1.5708
    c: Tangent(g24,g21) = -1.5708
    c: Equal(g21,g22)
    c: Diameter(g13) = 3.2
    c: Distance(g15) = 3
    c: Equal(g10,g14)
    c: Parallel(g12,g3)
    c: Parallel(g16,g3)
    c: Equal(g16,g11)
    c: Symmetric(g10,g9,g5)
    c: Symmetric(g14,g13,g5)
    c: Equal(g15,g24)
    c: Equal(g21,g13)
    c: Parallel(g24,g15)
    c: Equal(g22,g17)
    c: Equal(g19,g23)
    c: Parallel(g23,g19)
    c: Symmetric(g21,g22,g6)
    c: Symmetric(g17,g18,g7)
FEATURE [PartDesign::Pocket] Pocket055
  BaseFeature = -> Pad030
  Direction = (0,0,-1)
  Length = 5
  Length2 = 5
  Profile = -> Sketch081
  ReferenceAxis = -> Sketch081 [N_Axis]
  Type = 1
FEATURE [Sketcher::SketchObject] Sketch082
  FullyConstrained = true
  MapMode = 5
  Placement = pos=(0,0,0) rot=(0,1,0;3.14159rad)
  Support = -> [XY_Plane028]
  expr: Constraints[11] = <<global settings>>.nema17_motor_size
  expr: Constraints[12] = <<global settings>>.nema17_motor_size + <<base dims>>.motor_hole_straight
  expr: Constraints[5] = <<base dims>>.pulley_hole_offset
  expr: Constraints[7] = <<base dims>>.motor_pulley_distance
  sketch-geometry (5):
    g0: LineSegment StartX=-38.1195 StartY=-1.76777 StartZ=0 EndX=-4.88552 EndY=-35.0018 EndZ=0
    g1: LineSegment StartX=-4.88552 StartY=-35.0018 StartZ=0 EndX=-35.9982 EndY=-66.1145 EndZ=0
    g2: LineSegment StartX=-35.9982 StartY=-66.1145 StartZ=0 EndX=-69.2322 EndY=-32.8805 EndZ=0
    g3: LineSegment StartX=-69.2322 StartY=-32.8805 StartZ=0 EndX=-38.1195 EndY=-1.76777 EndZ=0
    g4: LineSegment StartX=-71 StartY=0 StartZ=0 EndX=-37.0589 EndY=-33.9411 EndZ=0
  constraints (15):
    c: Coincident(g0,g1)
    c: Coincident(g1,g2)
    c: Coincident(g2,g3)
    c: Coincident(g3,g0)
    c: Horizontal(g-1,g4)
    c: DistanceX(g4,g-1) = 71
    c: Angle(g4,g-1) = 0.785398
    c: Distance(g4) = 48
    c: Perpendicular(g0,g3)
    c: Equal(g0,g2)
    c: Equal(g3,g1)
    c: Distance(g3) = 44
    c: Distance(g2) = 47
    c: Parallel(g2,g4)
    c: Symmetric(g2,g0,g4)
FEATURE [PartDesign::Pocket] Pocket056
  BaseFeature = -> Pocket055
  Direction = (0,0,1)
  Length = 8
  Length2 = 5
  Profile = -> Sketch082
  ReferenceAxis = -> Sketch082 [N_Axis]
  Type = 0
  expr: Length = <<base dims>>.motor_inset
FEATURE [Sketcher::SketchObject] Sketch083
  AttachmentOffset = pos=(0,0,10) rot=(0,0,1;0rad)
  FullyConstrained = true
  MapMode = 5
  Placement = pos=(0,0,10) rot=(0,0,1;0rad)
  Support = -> [XY_Plane028]
  expr: .AttachmentOffset.Base.z = <<base dims>>.bottom_thickness
  expr: Constraints[1] = <<base dims>>.pulley_hole_offset
  expr: Constraints[2] = <<base dims>>.pulley_bearing_diameter + 2 * <<base dims>>.pulley_wall_thickness
  expr: Constraints[4] = <<base dims>>.pulley_hole_diameter
  sketch-geometry (2):
    g0: Circle CenterX=71 CenterY=0 CenterZ=0 NormalX=0 NormalY=0 NormalZ=1 AngleXU=0 Radius=14
    g1: Circle CenterX=71 CenterY=0 CenterZ=0 NormalX=0 NormalY=0 NormalZ=1 AngleXU=0 Radius=7.5
  constraints (5):
    c: Horizontal(g-1,g0)
    c: DistanceX(g-1,g0) = 71
    c: Diameter(g0) = 28
    c: Coincident(g1,g0)
    c: Diameter(g1) = 15
FEATURE [PartDesign::Pad] Pad031
  BaseFeature = -> Pocket056
  Direction = (0,0,1)
  Length = 8.5
  Length2 = 10
  Profile = -> Sketch083
  ReferenceAxis = -> Sketch083 [N_Axis]
  Type = 0
  expr: Length = <<base dims>>.pulley_wall_height
FEATURE [Sketcher::SketchObject] Sketch084
  AttachmentOffset = pos=(0,0,18.5) rot=(0,0,1;0rad)
  FullyConstrained = true
  MapMode = 5
  Placement = pos=(0,0,18.5) rot=(0,0,1;0rad)
  Support = -> [XY_Plane028]
  expr: .AttachmentOffset.Base.z = <<base dims>>.bottom_thickness + <<base dims>>.pulley_wall_height
  expr: Constraints[1] = <<base dims>>.pulley_hole_offset
  expr: Constraints[2] = <<base dims>>.pulley_bearing_diameter
  sketch-geometry (1):
    g0: Circle CenterX=71 CenterY=0 CenterZ=0 NormalX=0 NormalY=0 NormalZ=1 AngleXU=0 Radius=11
  constraints (3):
    c: Horizontal(g-1,g0)
    c: DistanceX(g-1,g0) = 71
    c: Diameter(g0) = 22
FEATURE [PartDesign::Pocket] Pocket057
  BaseFeature = -> Pad031
  Direction = (0,0,-1)
  Length = 8
  Length2 = 5
  Profile = -> Sketch084
  ReferenceAxis = -> Sketch084 [N_Axis]
  Type = 0
  expr: Length = <<base dims>>.pulley_bearing_height
FEATURE [Sketcher::SketchObject] Sketch085
  FullyConstrained = true
  MapMode = 5
  Placement = pos=(0,0,0) rot=(0,1,0;3.14159rad)
  Support = -> [XY_Plane028]
  expr: Constraints[1] = <<base dims>>.pulley_hole_offset
  expr: Constraints[2] = <<base dims>>.pulley_bearing_diameter
  sketch-geometry (1):
    g0: Circle CenterX=-71 CenterY=0 CenterZ=0 NormalX=0 NormalY=0 NormalZ=1 AngleXU=0 Radius=11
  constraints (3):
    c: Horizontal(g0,g-1)
    c: DistanceX(g0,g-1) = 71
    c: Diameter(g0) = 22
FEATURE [PartDesign::Pocket] Pocket058
  BaseFeature = -> Pocket057
  Direction = (0,0,1)
  Length = 7
  Length2 = 5
  Profile = -> Sketch085
  ReferenceAxis = -> Sketch085 [N_Axis]
  Type = 0
  expr: Length = <<base dims>>.pulley_bottom_inset
FEATURE [Sketcher::SketchObject] Sketch086
  AttachmentOffset = pos=(0,0,35) rot=(0,0,1;0rad)
  FullyConstrained = true
  MapMode = 5
  Placement = pos=(0,0,35) rot=(0,0,1;0rad)
  Support = -> [XY_Plane028]
  expr: .AttachmentOffset.Base.z = <<base dims>>.height - <<base dims>>.nut_depth
  expr: Constraints[186] = <<base dims>>.notch1_distance
  expr: Constraints[189] = <<base dims>>.width - 2 * <<base dims>>.wall_thickness - 2 * <<base dims>>.notch_distance
  expr: Constraints[190] = <<base dims>>.width - 2 * <<base dims>>.wall_thickness - 2 * <<base dims>>.notch_distance
  expr: Constraints[194] = <<base dims>>.notch3_distance
  expr: Constraints[198] = <<base dims>>.top_notch_distance
  expr: Constraints[199] = <<base dims>>.wall_thickness + <<base dims>>.notch_distance
  expr: Constraints[200] = 90deg + <<base dims>>.notch_angle
  expr: Constraints[201] = 90deg - 2 * <<base dims>>.notch_angle
  expr: Constraints[202] = 2 * <<base dims>>.notch_angle
  expr: Constraints[203] = 90deg - 2 * <<base dims>>.notch_angle
  expr: Constraints[204] = <<base dims>>.length - <<base dims>>.radius
  expr: Constraints[205] = <<base dims>>.width / 2 - <<base dims>>.radius
  expr: Constraints[206] = <<base dims>>.radius - <<base dims>>.wall_thickness - <<base dims>>.notch_distance
  expr: Constraints[31] = <<base dims>>.notch2_distance
  expr: Constraints[48] = <<base dims>>.width - 2 * <<base dims>>.wall_thickness - 2 * <<base dims>>.notch_distance
  expr: Constraints[6] = <<base dims>>.notch_diameter
  expr: Constraints[7] = <<global settings>>.m3_nut_width
  sketch-geometry (75):
    g0: LineSegment StartX=16.4 StartY=-61.0785 StartZ=0 EndX=16.4 EndY=-49.9785 EndZ=0
    g1: LineSegment StartX=16.4 StartY=-49.9785 StartZ=0 EndX=23.6 EndY=-49.9785 EndZ=0
    g2: LineSegment StartX=23.6 StartY=-49.9785 StartZ=0 EndX=23.6 EndY=-61.0785 EndZ=0
    g3: LineSegment StartX=23.6 StartY=-61.0785 StartZ=0 EndX=20 EndY=-63.1569 EndZ=0
    g4: LineSegment StartX=20 StartY=-63.1569 StartZ=0 EndX=16.4 EndY=-61.0785 EndZ=0
    g5: LineSegment StartX=20 StartY=-63.1569 StartZ=0 EndX=20 EndY=-59 EndZ=0
    g6: LineSegment StartX=71.4 StartY=-61.0785 StartZ=0 EndX=71.4 EndY=-49.9785 EndZ=0
    g7: LineSegment StartX=71.4 StartY=-49.9785 StartZ=0 EndX=78.6 EndY=-49.9785 EndZ=0
    g8: LineSegment StartX=78.6 StartY=-49.9785 StartZ=0 EndX=78.6 EndY=-61.0785 EndZ=0
    g9: LineSegment StartX=78.6 StartY=-61.0785 StartZ=0 EndX=75 EndY=-63.1569 EndZ=0
    g10: LineSegment StartX=75 StartY=-63.1569 StartZ=0 EndX=71.4 EndY=-61.0785 EndZ=0
    g11: LineSegment StartX=75 StartY=-63.1569 StartZ=0 EndX=75 EndY=-59 EndZ=0
    g12: LineSegment StartX=78.6 StartY=61.0785 StartZ=0 EndX=78.6 EndY=49.9785 EndZ=0
    g13: LineSegment StartX=78.6 StartY=49.9785 StartZ=0 EndX=71.4 EndY=49.9785 EndZ=0
    g14: LineSegment StartX=71.4 StartY=49.9785 StartZ=0 EndX=71.4 EndY=61.0785 EndZ=0
    g15: LineSegment StartX=71.4 StartY=61.0785 StartZ=0 EndX=75 EndY=63.1569 EndZ=0
    g16: LineSegment StartX=75 StartY=63.1569 StartZ=0 EndX=78.6 EndY=61.0785 EndZ=0
    g17: LineSegment StartX=75 StartY=63.1569 StartZ=0 EndX=75 EndY=59 EndZ=0
    g18: LineSegment StartX=126.4 StartY=-61.0785 StartZ=0 EndX=126.4 EndY=-49.9785 EndZ=0
    g19: LineSegment StartX=126.4 StartY=-49.9785 StartZ=0 EndX=133.6 EndY=-49.9785 EndZ=0
    g20: LineSegment StartX=133.6 StartY=-49.9785 StartZ=0 EndX=133.6 EndY=-61.0785 EndZ=0
    g21: LineSegment StartX=133.6 StartY=-61.0785 StartZ=0 EndX=130 EndY=-63.1569 EndZ=0
    g22: LineSegment StartX=130 StartY=-63.1569 StartZ=0 EndX=126.4 EndY=-61.0785 EndZ=0
    g23: LineSegment StartX=130 StartY=-63.1569 StartZ=0 EndX=130 EndY=-59 EndZ=0
    g24: LineSegment StartX=133.6 StartY=61.0785 StartZ=0 EndX=133.6 EndY=49.9785 EndZ=0
    g25: LineSegment StartX=133.6 StartY=49.9785 StartZ=0 EndX=126.4 EndY=49.9785 EndZ=0
    g26: LineSegment StartX=126.4 StartY=49.9785 StartZ=0 EndX=126.4 EndY=61.0785 EndZ=0
    g27: LineSegment StartX=126.4 StartY=61.0785 StartZ=0 EndX=130 EndY=63.1569 EndZ=0
    g28: LineSegment StartX=130 StartY=63.1569 StartZ=0 EndX=133.6 EndY=61.0785 EndZ=0
    g29: LineSegment StartX=130 StartY=63.1569 StartZ=0 EndX=130 EndY=59 EndZ=0
    g30: LineSegment StartX=23.6 StartY=61.0785 StartZ=0 EndX=23.6 EndY=49.9785 EndZ=0
    g31: LineSegment StartX=23.6 StartY=49.9785 StartZ=0 EndX=16.4 EndY=49.9785 EndZ=0
    g32: LineSegment StartX=16.4 StartY=49.9785 StartZ=0 EndX=16.4 EndY=61.0785 EndZ=0
    g33: LineSegment StartX=16.4 StartY=61.0785 StartZ=0 EndX=20 EndY=63.1569 EndZ=0
    g34: LineSegment StartX=20 StartY=63.1569 StartZ=0 EndX=23.6 EndY=61.0785 EndZ=0
    g35: LineSegment StartX=20 StartY=63.1569 StartZ=0 EndX=20 EndY=59 EndZ=0
    g36: LineSegment StartX=8.92154 StartY=26.6 StartZ=0 EndX=20.0215 EndY=26.6 EndZ=0
    g37: LineSegment StartX=20.0215 StartY=26.6 StartZ=0 EndX=20.0215 EndY=19.4 EndZ=0
    g38: LineSegment StartX=20.0215 StartY=19.4 StartZ=0 EndX=8.92154 EndY=19.4 EndZ=0
    g39: LineSegment StartX=8.92154 StartY=19.4 StartZ=0 EndX=6.84308 EndY=23 EndZ=0
    g40: LineSegment StartX=6.84308 StartY=23 StartZ=0 EndX=8.92154 EndY=26.6 EndZ=0
    g41: LineSegment StartX=6.84308 StartY=23 StartZ=0 EndX=11 EndY=23 EndZ=0
    g42: LineSegment StartX=177.873 StartY=55.8127 StartZ=0 EndX=173.625 EndY=45.5576 EndZ=0
    g43: LineSegment StartX=173.625 StartY=45.5576 StartZ=0 EndX=166.973 EndY=48.3129 EndZ=0
    g44: LineSegment StartX=166.973 StartY=48.3129 StartZ=0 EndX=171.221 EndY=58.568 EndZ=0
    g45: LineSegment StartX=171.221 StartY=58.568 StartZ=0 EndX=175.342 EndY=59.1106 EndZ=0
    g46: LineSegment StartX=175.342 StartY=59.1106 StartZ=0 EndX=177.873 EndY=55.8127 EndZ=0
    g47: LineSegment StartX=175.342 StartY=59.1106 StartZ=0 EndX=173.751 EndY=55.2701 EndZ=0
    g48: LineSegment StartX=203.568 StartY=26.2209 StartZ=0 EndX=193.313 EndY=21.9731 EndZ=0
    g49: LineSegment StartX=193.313 StartY=21.9731 StartZ=0 EndX=190.558 EndY=28.6251 EndZ=0
    g50: LineSegment StartX=190.558 StartY=28.6251 StartZ=0 EndX=200.813 EndY=32.8728 EndZ=0
    g51: LineSegment StartX=200.813 StartY=32.8728 StartZ=0 EndX=204.111 EndY=30.3423 EndZ=0
    g52: LineSegment StartX=204.111 StartY=30.3423 StartZ=0 EndX=203.568 EndY=26.2209 EndZ=0
    g53: LineSegment StartX=204.111 StartY=30.3423 StartZ=0 EndX=200.27 EndY=28.7515 EndZ=0
    g54: LineSegment StartX=200.813 StartY=-32.8728 StartZ=0 EndX=190.558 EndY=-28.6251 EndZ=0
    g55: LineSegment StartX=190.558 StartY=-28.6251 StartZ=0 EndX=193.313 EndY=-21.9731 EndZ=0
    g56: LineSegment StartX=193.313 StartY=-21.9731 StartZ=0 EndX=203.568 EndY=-26.2209 EndZ=0
    g57: LineSegment StartX=203.568 StartY=-26.2209 StartZ=0 EndX=204.111 EndY=-30.3423 EndZ=0
    g58: LineSegment StartX=204.111 StartY=-30.3423 StartZ=0 EndX=200.813 EndY=-32.8728 EndZ=0
    g59: LineSegment StartX=204.111 StartY=-30.3423 StartZ=0 EndX=200.27 EndY=-28.7515 EndZ=0
    g60: LineSegment StartX=171.221 StartY=-58.568 StartZ=0 EndX=166.973 EndY=-48.3129 EndZ=0
    g61: LineSegment StartX=166.973 StartY=-48.3129 StartZ=0 EndX=173.625 EndY=-45.5576 EndZ=0
    g62: LineSegment StartX=173.625 StartY=-45.5576 StartZ=0 EndX=177.873 EndY=-55.8127 EndZ=0
    g63: LineSegment StartX=177.873 StartY=-55.8127 StartZ=0 EndX=175.342 EndY=-59.1106 EndZ=0
    g64: LineSegment StartX=175.342 StartY=-59.1106 StartZ=0 EndX=171.221 EndY=-58.568 EndZ=0
    g65: LineSegment StartX=175.342 StartY=-59.1106 StartZ=0 EndX=173.751 EndY=-55.2701 EndZ=0
    g66: LineSegment StartX=8.92154 StartY=-19.4 StartZ=0 EndX=20.0215 EndY=-19.4 EndZ=0
    g67: LineSegment StartX=20.0215 StartY=-19.4 StartZ=0 EndX=20.0215 EndY=-26.6 EndZ=0
    g68: LineSegment StartX=20.0215 StartY=-26.6 StartZ=0 EndX=8.92154 EndY=-26.6 EndZ=0
    g69: LineSegment StartX=8.92154 StartY=-26.6 StartZ=0 EndX=6.84308 EndY=-23 EndZ=0
    g70: LineSegment StartX=6.84308 StartY=-23 StartZ=0 EndX=8.92154 EndY=-19.4 EndZ=0
    g71: LineSegment StartX=6.84308 StartY=-23 StartZ=0 EndX=11 EndY=-23 EndZ=0
    g72: Circle CenterX=155 CenterY=-10 CenterZ=0 NormalX=0 NormalY=0 NormalZ=1 AngleXU=0 Radius=49
    g73: LineSegment StartX=155 StartY=-10 StartZ=0 EndX=173.751 EndY=-55.2701 EndZ=0
    g74: LineSegment StartX=155 StartY=-10 StartZ=0 EndX=200.27 EndY=-28.7515 EndZ=0
  constraints (217):
    c: Coincident(g0,g1)
    c: Coincident(g1,g2)
    c: Coincident(g3,g2)
    c: Coincident(g4,g3)
    c: Coincident(g4,g0)
    c: Equal(g3,g4)
    c: Distance(g0) = 11.1
    c: Distance(g1) = 7.2
    c: Angle(g3,g4) = 2.0944
    c: Perpendicular(g2,g1)
    c: Perpendicular(g0,g1)
    c: Equal(g2,g0)
    c: Coincident(g5,g3)
    c: Equal(g5,g4)
    c: Parallel(g5,g0)
    c: Coincident(g6,g7)
    c: Coincident(g7,g8)
    c: Coincident(g9,g8)
    c: Coincident(g10,g9)
    c: Coincident(g10,g6)
    c: Equal(g9,g10)
    c: Equal(g0,g6) = 5.55
    c: Equal(g1,g7) = 7.2
    c: Angle(g9,g10) = 2.0944
    c: Perpendicular(g8,g7)
    c: Perpendicular(g6,g7)
    c: Equal(g8,g6)
    c: Coincident(g11,g9)
    c: Equal(g11,g10)
    c: Parallel(g11,g6)
    c: Horizontal(g7)
    c: DistanceX(g-1,g11) = 75
    c: Coincident(g12,g13)
    c: Coincident(g13,g14)
    c: Coincident(g15,g14)
    c: Coincident(g16,g15)
    c: Coincident(g16,g12)
    c: Equal(g15,g16)
    c: Equal(g0,g12) = 5.55
    c: Equal(g1,g13) = 7.2
    c: Angle(g15,g16) = 2.0944
    c: Perpendicular(g14,g13)
    c: Perpendicular(g12,g13)
    c: Equal(g14,g12)
    c: Coincident(g17,g15)
    c: Equal(g17,g16)
    c: Parallel(g17,g12)
    c: Vertical(g14)
    c: DistanceY(g11,g17) = 118
    c: Symmetric(g11,g17,g-1)
    c: Coincident(g18,g19)
    c: Coincident(g19,g20)
    c: Coincident(g21,g20)
    c: Coincident(g22,g21)
    c: Coincident(g22,g18)
    c: Equal(g21,g22)
    c: Equal(g0,g18) = 11.1
    c: Equal(g1,g19) = 7.2
    c: Angle(g21,g22) = 2.0944
    c: Perpendicular(g20,g19)
    c: Perpendicular(g18,g19)
    c: Equal(g20,g18)
    c: Coincident(g23,g21)
    c: Equal(g23,g22)
    c: Parallel(g23,g18)
    c: Coincident(g24,g25)
    c: Coincident(g25,g26)
    c: Coincident(g27,g26)
    c: Coincident(g28,g27)
    c: Coincident(g28,g24)
    c: Equal(g27,g28)
    c: Equal(g0,g24) = 11.1
    c: Equal(g1,g25) = 7.2
    c: Angle(g27,g28) = 2.0944
    c: Perpendicular(g26,g25)
    c: Perpendicular(g24,g25)
    c: Equal(g26,g24)
    c: Coincident(g29,g27)
    c: Equal(g29,g28)
    c: Parallel(g29,g24)
    c: Coincident(g30,g31)
    c: Coincident(g31,g32)
    c: Coincident(g33,g32)
    c: Coincident(g34,g33)
    c: Coincident(g34,g30)
    c: Equal(g33,g34)
    c: Equal(g0,g30) = 11.1
    c: Equal(g1,g31) = 7.2
    c: Angle(g33,g34) = 2.0944
    c: Perpendicular(g32,g31)
    c: Perpendicular(g30,g31)
    c: Equal(g32,g30)
    c: Coincident(g35,g33)
    c: Equal(g35,g34)
    c: Parallel(g35,g30)
    c: Coincident(g36,g37)
    c: Coincident(g37,g38)
    c: Coincident(g39,g38)
    c: Coincident(g40,g39)
    c: Coincident(g40,g36)
    c: Equal(g39,g40)
    c: Equal(g0,g36) = 11.1
    c: Equal(g1,g37) = 7.2
    c: Angle(g39,g40) = 2.0944
    c: Perpendicular(g38,g37)
    c: Perpendicular(g36,g37)
    c: Equal(g38,g36)
    c: Coincident(g41,g39)
    c: Equal(g41,g40)
    c: Parallel(g41,g36)
    c: Coincident(g42,g43)
    c: Coincident(g43,g44)
    c: Coincident(g45,g44)
    c: Coincident(g46,g45)
    c: Coincident(g46,g42)
    c: Equal(g45,g46)
    c: Equal(g0,g42) = 11.1
    c: Equal(g1,g43) = 7.2
    c: Angle(g45,g46) = 2.0944
    c: Perpendicular(g44,g43)
    c: Perpendicular(g42,g43)
    c: Equal(g44,g42)
    c: Coincident(g47,g45)
    c: Equal(g47,g46)
    c: Parallel(g47,g42)
    c: Coincident(g48,g49)
    c: Coincident(g49,g50)
    c: Coincident(g51,g50)
    c: Coincident(g52,g51)
    c: Coincident(g52,g48)
    c: Equal(g51,g52)
    c: Equal(g0,g48) = 11.1
    c: Equal(g1,g49) = 7.2
    c: Angle(g51,g52) = 2.0944
    c: Perpendicular(g50,g49)
    c: Perpendicular(g48,g49)
    c: Equal(g50,g48)
    c: Coincident(g53,g51)
    c: Equal(g53,g52)
    c: Parallel(g53,g48)
    c: Coincident(g54,g55)
    c: Coincident(g55,g56)
    c: Coincident(g57,g56)
    c: Coincident(g58,g57)
    c: Coincident(g58,g54)
    c: Equal(g57,g58)
    c: Equal(g0,g54) = 11.1
    c: Equal(g1,g55) = 7.2
    c: Angle(g57,g58) = 2.0944
    c: Perpendicular(g56,g55)
    c: Perpendicular(g54,g55)
    c: Equal(g56,g54)
    c: Coincident(g59,g57)
    c: Equal(g59,g58)
    c: Parallel(g59,g54)
    c: Coincident(g60,g61)
    c: Coincident(g61,g62)
    c: Coincident(g63,g62)
    c: Coincident(g64,g63)
    c: Coincident(g64,g60)
    c: Equal(g63,g64)
    c: Equal(g0,g60) = 11.1
    c: Equal(g1,g61) = 7.2
    c: Angle(g63,g64) = 2.0944
    c: Perpendicular(g62,g61)
    c: Perpendicular(g60,g61)
    c: Equal(g62,g60)
    c: Coincident(g65,g63)
    c: Equal(g65,g64)
    c: Parallel(g65,g60)
    c: Coincident(g66,g67)
    c: Coincident(g67,g68)
    c: Coincident(g69,g68)
    c: Coincident(g70,g69)
    c: Coincident(g70,g66)
    c: Equal(g69,g70)
    c: Equal(g0,g66) = 11.1
    c: Equal(g1,g67) = 7.2
    c: Angle(g69,g70) = 2.0944
    c: Perpendicular(g68,g67)
    c: Perpendicular(g66,g67)
    c: Equal(g68,g66)
    c: Coincident(g71,g69)
    c: Equal(g71,g70)
    c: Parallel(g71,g66)
    c: Vertical(g0)
    c: DistanceX(g-1,g5) = 20
    c: Vertical(g32)
    c: Symmetric(g35,g5,g-1)
    c: DistanceY(g5,g35) = 118
    c: DistanceY(g23,g29) = 118
    c: Symmetric(g29,g23,g-1)
    c: Vertical(g23)
    c: Vertical(g29)
    c: DistanceX(g-1,g23) = 130
    c: Horizontal(g41)
    c: Horizontal(g71)
    c: Symmetric(g41,g71,g-1)
    c: DistanceY(g71,g41) = 46
    c: DistanceX(g-1,g71) = 11
    c: Angle(g-1,g65) = 1.9635
    c: Angle(g65,g59) = 0.785398
    c: Angle(g59,g53) = 0.785398
    c: Angle(g53,g47) = 0.785398
    c: DistanceX(g-1,g72) = 155
    c: DistanceY(g72,g-1) = 10
    c: Radius(g72) = 49
    c: Symmetric(g65,g47,g-1)
    c: Symmetric(g59,g53,g-1)
    c: PointOnObject(g59,g72)
    c: PointOnObject(g65,g72)
    c: Coincident(g73,g72)
    c: Coincident(g73,g65)
    c: Parallel(g73,g65)
    c: Coincident(g74,g72)
    c: Coincident(g74,g59)
    c: Parallel(g74,g59)
FEATURE [PartDesign::Pocket] Pocket059
  BaseFeature = -> Pocket058
  Direction = (0,0,-1)
  Length = 3.6
  Length2 = 5
  Profile = -> Sketch086
  ReferenceAxis = -> Sketch086 [N_Axis]
  Type = 0
  expr: Length = <<global settings>>.m3_nut_height
FEATURE [Sketcher::SketchObject] Sketch087
  AttachmentOffset = pos=(0,0,10) rot=(0,0,1;0rad)
  FullyConstrained = true
  MapMode = 5
  Placement = pos=(0,0,10) rot=(0,0,1;0rad)
  Support = -> [XY_Plane028]
  expr: .AttachmentOffset.Base.z = <<base dims>>.bottom_thickness
  expr: Constraints[0] = <<base dims>>.main_axl_hole_offset
  expr: Constraints[2] = <<base dims>>.main_axl_bearing_diameter
  sketch-geometry (1):
    g0: Circle CenterX=150 CenterY=0 CenterZ=0 NormalX=0 NormalY=0 NormalZ=1 AngleXU=0 Radius=23.5
  constraints (3):
    c: DistanceX(g-1,g0) = 150
    c: Horizontal(g0,g-1)
    c: Diameter(g0) = 47
FEATURE [PartDesign::Pocket] Pocket060
  BaseFeature = -> Pocket059
  Direction = (0,0,-1)
  Length = 7
  Length2 = 5
  Profile = -> Sketch087
  ReferenceAxis = -> Sketch087 [N_Axis]
  Type = 0
  expr: Length = <<base dims>>.main_axl_bearing_height
FEATURE [Sketcher::SketchObject] Sketch088
  AttachmentOffset = pos=(0,0,10) rot=(0,0,1;0rad)
  FullyConstrained = true
  MapMode = 5
  Placement = pos=(0,0,10) rot=(0,0,1;0rad)
  Support = -> [XY_Plane028]
  expr: .AttachmentOffset.Base.z = <<base dims>>.bottom_thickness
  expr: Constraints[0] = <<base dims>>.main_axl_hole_offset
  expr: Constraints[10] = <<base dims>>.length - <<base dims>>.wall_thickness
  expr: Constraints[13] = <<base dims>>.wall_thickness
  expr: Constraints[18] = <<base dims>>.length - <<base dims>>.radius
  expr: Constraints[19] = <<base dims>>.width / 2 - <<base dims>>.radius
  expr: Constraints[20] = <<base dims>>.radius - <<base dims>>.wall_thickness
  expr: Constraints[22] = <<base dims>>.wall_thickness
  expr: Constraints[2] = <<base dims>>.reinforcement_diameter
  expr: Constraints[47] = <<base dims>>.width / 2 - <<base dims>>.wall_thickness
  expr: Constraints[4] = <<base dims>>.reinforcement_diameter + 2 * <<base dims>>.wall_thickness
  expr: Constraints[53] = <<base dims>>.wall_thickness
  expr: Constraints[78] = <<base dims>>.wall_thickness
  sketch-geometry (32):
    g0: Circle CenterX=150 CenterY=0 CenterZ=0 NormalX=0 NormalY=0 NormalZ=1 AngleXU=0 Radius=30.5
    g1: ArcOfCircle CenterX=150 CenterY=0 CenterZ=0 NormalX=0 NormalY=0 NormalZ=1 AngleXU=0 Radius=38.5 StartAngle=0.104084 EndAngle=0.681557
    g2: LineSegment StartX=188.292 StartY=-4 StartZ=0 EndX=207 EndY=-4 EndZ=0
    g3: LineSegment StartX=207 StartY=-4 StartZ=0 EndX=207 EndY=4 EndZ=0
    g4: LineSegment StartX=207 StartY=4 StartZ=0 EndX=188.292 EndY=4 EndZ=0
    g5: LineSegment StartX=179.899 StartY=-24.2551 StartZ=0 EndX=196.704 EndY=-41.0605 EndZ=0
    g6: LineSegment StartX=174.255 StartY=-29.8988 StartZ=0 EndX=191.446 EndY=-47.09 EndZ=0
    g7: ArcOfCircle CenterX=155 CenterY=-10 CenterZ=0 NormalX=0 NormalY=0 NormalZ=1 AngleXU=0 Radius=52 StartAngle=5.48903 EndAngle=5.64303
    g8: GeomPoint X=194.075 Y=-44.0753 Z=0
    g9: ArcOfCircle CenterX=150 CenterY=0 CenterZ=0 NormalX=0 NormalY=0 NormalZ=1 AngleXU=0 Radius=38.5 StartAngle=5.60163 EndAngle=6.1791
    g10: LineSegment StartX=150 StartY=0 StartZ=0 EndX=194.075 EndY=-44.0753 EndZ=0
    g11: ArcOfCircle CenterX=155 CenterY=10 CenterZ=0 NormalX=0 NormalY=0 NormalZ=1 AngleXU=0 Radius=52 StartAngle=0.640153 EndAngle=0.794151
    g12: LineSegment StartX=191.446 StartY=47.09 StartZ=0 EndX=174.255 EndY=29.8988 EndZ=0
    g13: LineSegment StartX=196.704 StartY=41.0605 StartZ=0 EndX=179.899 EndY=24.2551 EndZ=0
    g14: ArcOfCircle CenterX=150 CenterY=0 CenterZ=0 NormalX=0 NormalY=0 NormalZ=1 AngleXU=0 Radius=38.5 StartAngle=0.889239 EndAngle=1.46671
    g15: LineSegment StartX=154 StartY=-38.2916 StartZ=0 EndX=154 EndY=-62 EndZ=0
    g16: LineSegment StartX=154 StartY=-62 StartZ=0 EndX=146 EndY=-62 EndZ=0
    g17: LineSegment StartX=146 StartY=-62 StartZ=0 EndX=146 EndY=-38.2916 EndZ=0
    g18: ArcOfCircle CenterX=150 CenterY=0 CenterZ=0 NormalX=0 NormalY=0 NormalZ=1 AngleXU=0 Radius=38.5 StartAngle=4.81647 EndAngle=5.39395
    g19: LineSegment StartX=154 StartY=38.2916 StartZ=0 EndX=154 EndY=62 EndZ=0
    g20: LineSegment StartX=154 StartY=62 StartZ=0 EndX=146 EndY=62 EndZ=0
    g21: LineSegment StartX=146 StartY=62 StartZ=0 EndX=146 EndY=38.2916 EndZ=0
    g22: ArcOfCircle CenterX=150 CenterY=0 CenterZ=0 NormalX=0 NormalY=0 NormalZ=1 AngleXU=0 Radius=38.5 StartAngle=1.67488 EndAngle=2.25211
    g23: LineSegment StartX=125.752 StartY=-29.9047 StartZ=0 EndX=93.6569 EndY=-62 EndZ=0
    g24: LineSegment StartX=93.6569 StartY=-62 StartZ=0 EndX=82.3431 EndY=-62 EndZ=0
    g25: LineSegment StartX=82.3431 StartY=-62 StartZ=0 EndX=120.095 EndY=-24.2479 EndZ=0
    g26: LineSegment StartX=150 StartY=0 StartZ=0 EndX=88 EndY=-62 EndZ=0
    g27: ArcOfCircle CenterX=150 CenterY=0 CenterZ=0 NormalX=0 NormalY=0 NormalZ=1 AngleXU=0 Radius=38.5 StartAngle=4.03107 EndAngle=4.60831
    g28: LineSegment StartX=125.752 StartY=29.9047 StartZ=0 EndX=93.6569 EndY=62 EndZ=0
    g29: LineSegment StartX=93.6569 StartY=62 StartZ=0 EndX=82.3431 EndY=62 EndZ=0
    g30: LineSegment StartX=82.3431 StartY=62 StartZ=0 EndX=120.095 EndY=24.2479 EndZ=0
    g31: ArcOfCircle CenterX=150 CenterY=0 CenterZ=0 NormalX=0 NormalY=0 NormalZ=1 AngleXU=0 Radius=38.5 StartAngle=2.46028 EndAngle=3.82291
  constraints (89):
    c: DistanceX(g-1,g0) = 150
    c: Horizontal(g0,g-1)
    c: Diameter(g0) = 61
    c: Coincident(g1,g0)
    c: Diameter(g1) = 77
    c: Coincident(g2,g3)
    c: Coincident(g3,g4)
    c: Horizontal(g2)
    c: Horizontal(g4)
    c: Vertical(g3)
    c: DistanceX(g-1,g3) = 207
    c: Coincident(g4,g1)
    c: Coincident(g2,g9)
    c: DistanceY(g9,g1) = 8
    c: Vertical(g1,g9)
    c: Coincident(g5,g7)
    c: Coincident(g6,g7)
    c: Parallel(g6,g5)
    c: DistanceX(g-1,g7) = 155
    c: DistanceY(g7,g-1) = 10
    c: Radius(g7) = 52
    c: Symmetric(g5,g6,g8)
    c: Distance(g6,g5) = 8
    c: Equal(g1,g9)
    c: Coincident(g1,g9)
    c: Coincident(g5,g9)
    c: Coincident(g6,g18)
    c: Coincident(g10,g0)
    c: Coincident(g10,g8)
    c: Parallel(g10,g6)
    c: Angle(g-1,g10) = 2.35619
    c: Coincident(g12,g11)
    c: Coincident(g13,g11)
    c: Equal(g1,g14)
    c: Coincident(g1,g14)
    c: Coincident(g12,g14)
    c: Coincident(g13,g1)
    c: Symmetric(g11,g7,g-1)
    c: Vertical(g12,g6)
    c: Vertical(g1,g5)
    c: Symmetric(g11,g6,g-1)
    c: Vertical(g11,g5)
    c: Vertical(g15)
    c: Coincident(g15,g16)
    c: Horizontal(g16)
    c: Coincident(g16,g17)
    c: Vertical(g17)
    c: DistanceY(g16,g-1) = 62
    c: Equal(g14,g18)
    c: Coincident(g14,g18)
    c: Coincident(g17,g27)
    c: Coincident(g15,g18)
    c: Horizontal(g27,g15)
    c: DistanceX(g27,g15) = 8
    c: Coincident(g19,g20)
    c: Horizontal(g20)
    c: Coincident(g20,g21)
    c: Vertical(g21)
    c: Vertical(g19)
    c: Equal(g14,g22)
    c: Coincident(g14,g22)
    c: Coincident(g19,g14)
    c: Coincident(g21,g22)
    c: Symmetric(g20,g16,g-1)
    c: Vertical(g19,g15)
    c: Coincident(g24,g23)
    c: Horizontal(g24)
    c: Coincident(g26,g0)
    c: Symmetric(g24,g23,g26)
    c: Coincident(g24,g25)
    c: Parallel(g26,g25)
    c: Parallel(g25,g23)
    c: Perpendicular(g10,g26)
    c: Horizontal(g23,g16)
    c: Equal(g22,g27)
    c: Coincident(g22,g27)
    c: Coincident(g23,g27)
    c: Coincident(g25,g31)
    c: Distance(g31,g23) = 8
    c: Coincident(g28,g29)
    c: Coincident(g29,g30)
    c: Symmetric(g24,g29,g-1)
    c: Symmetric(g23,g28,g-1)
    c: Equal(g22,g31)
    c: Coincident(g22,g31)
    c: Coincident(g28,g22)
    c: Coincident(g30,g31)
    c: Vertical(g22,g23)
    c: Vertical(g30,g25)
FEATURE [PartDesign::Pad] Pad032
  BaseFeature = -> Pocket060
  Direction = (0,0,1)
  Length = 8
  Length2 = 10
  Profile = -> Sketch088
  ReferenceAxis = -> Sketch088 [N_Axis]
  Type = 0
  expr: Length = <<base dims>>.reinforcement_height
FEATURE [Sketcher::SketchObject] Sketch089
  FullyConstrained = true
  MapMode = 5
  Placement = pos=(0,0,0) rot=(-0.57735,0.57735,0.57735;4.18879rad)
  Support = -> [YZ_Plane028]
  expr: Constraints[14] = <<base dims>>.top_hole_row1_height
  expr: Constraints[15] = <<base dims>>.top_hole_row_distance
  expr: Constraints[16] = <<base dims>>.top_hole_offset
  expr: Constraints[17] = <<base dims>>.top_hole_offset
  expr: Constraints[5] = <<base dims>>.cover_hole_inner_diameter
  sketch-geometry (6):
    g0: Circle CenterX=0 CenterY=37 CenterZ=0 NormalX=0 NormalY=0 NormalZ=1 AngleXU=0 Radius=2.05
    g1: Circle CenterX=0 CenterY=23 CenterZ=0 NormalX=0 NormalY=0 NormalZ=1 AngleXU=0 Radius=2.05
    g2: Circle CenterX=50 CenterY=37 CenterZ=0 NormalX=0 NormalY=0 NormalZ=1 AngleXU=0 Radius=2.05
    g3: Circle CenterX=50 CenterY=23 CenterZ=0 NormalX=0 NormalY=0 NormalZ=1 AngleXU=0 Radius=2.05
    g4: Circle CenterX=-50 CenterY=23 CenterZ=0 NormalX=0 NormalY=0 NormalZ=1 AngleXU=0 Radius=2.05
    g5: Circle CenterX=-50 CenterY=37 CenterZ=0 NormalX=0 NormalY=0 NormalZ=1 AngleXU=0 Radius=2.05
  constraints (18):
    c: Equal(g5,g4)
    c: Equal(g4,g0)
    c: Equal(g0,g1)
    c: Equal(g1,g2)
    c: Equal(g2,g3)
    c: Diameter(g4) = 4.1
    c: Vertical(g5,g4)
    c: Vertical(g2,g3)
    c: Vertical(g0,g1)
    c: Horizontal(g4,g1)
    c: Horizontal(g1,g3)
    c: Horizontal(g2,g0)
    c: Horizontal(g0,g5)
    c: Vertical(g1,g-1)
    c: DistanceY(g-1,g1) = 23
    c: DistanceY(g1,g0) = 14
    c: DistanceX(g4,g1) = 50
    c: DistanceX(g1,g3) = 50
FEATURE [PartDesign::Pocket] Pocket061
  BaseFeature = -> Pad032
  Direction = (1,-2e-16,3e-16)
  Length = 5
  Length2 = 5
  Profile = -> Sketch089
  ReferenceAxis = -> Sketch089 [N_Axis]
  Type = 2
FEATURE [Part::Part2DObjectPython] ShapeString015  # Draft 2D object (typed FeaturePython)
  AttachmentOffset = pos=(37,28,10) rot=(0,0,1;0rad)
  FontFile = <userpath>/FreeCAD/Font/ARLRDBD.TTF
  MakeFace = true
  MapMode = 5
  Placement = pos=(37,28,10) rot=(0,0,1;0rad)
  Size = 5
  String = v1.0
  Support = -> [XY_Plane028]
  Tracking = 0
  expr: .AttachmentOffset.Base.z = <<base dims>>.bottom_thickness
  expr: Size = <<global settings>>.label_font_size
FEATURE [PartDesign::Pocket] Pocket062
  BaseFeature = -> Pocket061
  Direction = (0,0,-1)
  Length = 0.4
  Length2 = 5
  Profile = -> ShapeString015
  ReferenceAxis = -> ShapeString015 [N_Axis]
  Type = 0
  expr: Length = <<global settings>>.label_text_depth
FEATURE [PartDesign::Body] Body015  label="base"
  Group = -> [Sketch078,Pad029,Sketch079,Pocket054,Sketch080,Pad030,Sketch081,Pocket055,Sketch082,Pocket056,Sketch083,Pad031,Sketch084,Pocket057,Sketch085,Pocket058,Sketch086,Pocket059,Sketch087,Pocket060,Sketch088,Pad032,Sketch089,Pocket061,ShapeString015,Pocket062]
  Origin = -> Origin028
  Tip = -> Pocket062
FEATURE [TechDraw::DrawSVGTemplate] Template
  Height = 210
  Orientation = 1
  Width = 297
FEATURE [TechDraw::DrawViewPart] View
  CoarseView = false
  Direction = (0,0,1)
  Focus = 100
  HardHidden = false
  IsoCount = 0
  IsoHidden = false
  IsoVisible = false
  LockPosition = false
  Perspective = false
  Rotation = 0
  ScaleType = 0
  SeamHidden = false
  SeamVisible = true
  SmoothHidden = false
  SmoothVisible = true
  Source = -> [Body015]
  X = 148.5
  XDirection = (1,0,0)
  Y = 105
FEATURE [TechDraw::DrawViewDimension] Dimension
  AngleOverride = false
  Arbitrary = false
  ArbitraryTolerances = false
  EqualTolerance = true
  ExtensionAngle = 0
  FormatSpec = %.2f
  FormatSpecOverTolerance = %+.2f
  FormatSpecUnderTolerance = %+.2f
  Inverted = false
  LineAngle = 0
  LockPosition = false
  MeasureType = 1
  OverTolerance = 0
  References2D = -> [View]
  Rotation = 0
  ScaleType = 0
  TheoreticalExact = false
  Type = 1
  UnderTolerance = 0
  X = -1.94085
  Y = 90.5222
FEATURE [TechDraw::DrawViewDimension] Dimension001
  AngleOverride = false
  Arbitrary = false
  ArbitraryTolerances = false
  EqualTolerance = true
  ExtensionAngle = 0
  FormatSpec = %.2f
  FormatSpecOverTolerance = %+.2f
  FormatSpecUnderTolerance = %+.2f
  Inverted = false
  LineAngle = 0
  LockPosition = false
  MeasureType = 1
  OverTolerance = 0
  References2D = -> [View]
  Rotation = 0
  ScaleType = 0
  TheoreticalExact = false
  Type = 2
  UnderTolerance = 0
  X = -125.55
  Y = 0.94732
FEATURE [TechDraw::DrawViewDimension] Dimension002
  AngleOverride = false
  Arbitrary = false
  ArbitraryTolerances = false
  EqualTolerance = true
  ExtensionAngle = 0
  FormatSpec = %.2f
  FormatSpecOverTolerance = %+.2f
  FormatSpecUnderTolerance = %+.2f
  Inverted = false
  LineAngle = 0
  LockPosition = false
  MeasureType = 1
  OverTolerance = 0
  References2D = -> [View]
  Rotation = 0
  ScaleType = 0
  TheoreticalExact = false
  Type = 1
  UnderTolerance = 0
  X = -97.9043
  Y = -76.152
FEATURE [TechDraw::DrawViewDimension] Dimension003
  AngleOverride = false
  Arbitrary = false
  ArbitraryTolerances = false
  EqualTolerance = true
  ExtensionAngle = 0
  FormatSpec = %.2f
  FormatSpecOverTolerance = %+.2f
  FormatSpecUnderTolerance = %+.2f
  Inverted = false
  LineAngle = 0
  LockPosition = false
  MeasureType = 1
  OverTolerance = 0
  References2D = -> [View]
  Rotation = 0
  ScaleType = 0
  TheoreticalExact = false
  Type = 1
  UnderTolerance = 0
  X = -57.5739
  Y = -76.1781
FEATURE [TechDraw::DrawViewDimension] Dimension004
  AngleOverride = false
  Arbitrary = false
  ArbitraryTolerances = false
  EqualTolerance = true
  ExtensionAngle = 0
  FormatSpec = %.2f
  FormatSpecOverTolerance = %+.2f
  FormatSpecUnderTolerance = %+.2f
  Inverted = false
  LineAngle = 0
  LockPosition = false
  MeasureType = 1
  OverTolerance = 0
  References2D = -> [View]
  Rotation = 0
  ScaleType = 0
  TheoreticalExact = false
  Type = 1
  UnderTolerance = 0
  X = -4.86522
  Y = -76.1781
FEATURE [TechDraw::DrawViewDimension] Dimension005
  AngleOverride = false
  Arbitrary = false
  ArbitraryTolerances = false
  EqualTolerance = true
  ExtensionAngle = 0
  FormatSpec = %.2f
  FormatSpecOverTolerance = %+.2f
  FormatSpecUnderTolerance = %+.2f
  Inverted = false
  LineAngle = 0
  LockPosition = false
  MeasureType = 1
  OverTolerance = 0
  References2D = -> [View]
  Rotation = 0
  ScaleType = 0
  TheoreticalExact = false
  Type = 7
  UnderTolerance = 0
  X = 61.431
  Y = -72.4482
FEATURE [TechDraw::DrawPage] Page001  label="Base drawing"
  KeepUpdated = true
  NextBalloonIndex = 1
  ProjectionType = 0
  Template = -> Template
  Views = -> [View,Dimension,Dimension001,Dimension002,Dimension003,Dimension004,Dimension005]
FEATURE [Part::Feature] Part__Feature177  label="GT2 Pulley - 110 teeth - J1_GT2 Pulley - Parametric001"
  Placement = pos=(83,2e-15,8) rot=(-1,0,0;1.5708rad)
  shape: bbox 71.92 x 71.92 x 22.4 mm, 1012 faces (baked)
FEATURE [Spreadsheet::Sheet] Spreadsheet007  label=" pulley dims"
  cells = A1=guide plate thickness; B1(guide_plate_thickness)==1.2mm; A2=tooth width; B2(tooth_width)==7mm; A3=110 axis outer diameter; B3(p110_axis_outer_diameter)==35mm; A4=110 axis inner diameter; B4(p110_axis_inner_diameter)==15mm; A5=axis hole diameter; B5(axis_hole_diameter)==3.6mm; A6=110 axis holeset diameter; B6(p110_axis_holeset_diameter)==25mm; A7=110 bearing inner diameter; B7(p110_bearing_inner_diameter)==40mm; A8=110 bearing outer diameter; B8(p110_bearing_outer_diameter)==62mm; A9=110 bearing inset; B9(p110_bearing_inset)==3mm; A10=110 axis height; B10(p110_axis_height)==16mm; A11=110 bearing threshhold height; B11(p110_bearing_threshhold_height)==1mm; A12=motor axis diameter; B12(motor_axis_diameter)==5.2mm; A13=motor axis main diameter; B13(motor_axis_main_diameter)==14.62mm; A14=motor axis flat area; B14(motor_axis_flat_area)==3mm; A15=motor axis spacing; B15(motor_axis_spacing)==7mm; A16=gear changer small diameter; B16(gear_changer_small_diameter)==15.9mm; A17=gear changer large diameter; B17(gear_changer_large_diameter)==52.82mm; A18=gear changer small wheel; B18(gear_changer_small_wheel)=22; A19=gear change large wheel; B19(gear_changer_large_wheel)=80
FEATURE [PartDesign::FeaturePython] timinggear  # WARN: FeaturePython — macro-defined, semantics opaque (R4)
  AttacherType = Attacher::AttachEngine3D
  AttachmentOffset = pos=(0,0,2) rot=(0,0,1;0rad)
  MapMode = 5
  Placement = pos=(0,0,2) rot=(0,0,1;0rad)
  h = 0.75
  height = 7
  offset = 0.4
  pitch = 2
  r0 = 0.555
  r1 = 1
  rs = 0.15
  teeth = 110
  type = 0
  u = 0.254
  version = 0.0.3
  expr: height = << pulley dims>>.tooth_width
FEATURE [PartDesign::FeatureBase] BaseFeature002
  BaseFeature = -> timinggear
  Placement = pos=(0,0,1.2) rot=(0,0,1;0rad)
  expr: .Placement.Base.z = << pulley dims>>.guide_plate_thickness
FEATURE [Sketcher::SketchObject] Sketch090
  FullyConstrained = true
  MapMode = 5
  Support = -> [XY_Plane029]
  sketch-geometry (1):
    g0: Circle CenterX=0 CenterY=0 CenterZ=0 NormalX=0 NormalY=0 NormalZ=1 AngleXU=0 Radius=35.96
  constraints (2):
    c: Coincident(g0,g-1)
    c: Diameter(g0) = 71.92
FEATURE [PartDesign::Pad] Pad033
  BaseFeature = -> BaseFeature002
  Direction = (0,0,1)
  Length = 1.2
  Length2 = 10
  Placement = pos=(0,0,1.2) rot=(0,0,1;0rad)
  Profile = -> Sketch090
  ReferenceAxis = -> Sketch090 [N_Axis]
  Type = 0
  expr: Length = << pulley dims>>.guide_plate_thickness
FEATURE [Sketcher::SketchObject] Sketch091
  AttachmentOffset = pos=(0,0,8.2) rot=(0,0,1;0rad)
  FullyConstrained = false
  MapMode = 5
  Placement = pos=(0,0,8.2) rot=(0,0,1;0rad)
  Support = -> [XY_Plane029]
  expr: .AttachmentOffset.Base.z = << pulley dims>>.guide_plate_thickness + << pulley dims>>.tooth_width
  sketch-geometry (1):
    g0: Circle CenterX=0 CenterY=0 CenterZ=0 NormalX=0 NormalY=0 NormalZ=1 AngleXU=0 Radius=35.96
  constraints (1):
    c: Diameter(g0) = 71.92
FEATURE [PartDesign::Pad] Pad034
  BaseFeature = -> Pad033
  Direction = (0,0,1)
  Length = 1.2
  Length2 = 10
  Placement = pos=(0,0,1.2) rot=(0,0,1;0rad)
  Profile = -> Sketch091
  ReferenceAxis = -> Sketch091 [N_Axis]
  Type = 0
  expr: Length = << pulley dims>>.guide_plate_thickness
FEATURE [Sketcher::SketchObject] Sketch092
  AttachmentOffset = pos=(0,0,9.4) rot=(0,0,1;0rad)
  FullyConstrained = true
  MapMode = 5
  Placement = pos=(0,0,9.4) rot=(0,0,1;0rad)
  Support = -> [XY_Plane029]
  expr: .AttachmentOffset.Base.z = << pulley dims>>.guide_plate_thickness * 2 + << pulley dims>>.tooth_width
  expr: Constraints[1] = << pulley dims>>.p110_bearing_outer_diameter
  sketch-geometry (1):
    g0: Circle CenterX=0 CenterY=0 CenterZ=0 NormalX=0 NormalY=0 NormalZ=1 AngleXU=0 Radius=31
  constraints (2):
    c: Coincident(g0,g-1)
    c: Diameter(g0) = 62
FEATURE [PartDesign::Pocket] Pocket063
  BaseFeature = -> Pad034
  Direction = (0,0,-1)
  Length = 3
  Length2 = 5
  Placement = pos=(0,0,1.2) rot=(0,0,1;0rad)
  Profile = -> Sketch092
  ReferenceAxis = -> Sketch092 [N_Axis]
  Type = 0
  expr: Length = << pulley dims>>.p110_bearing_inset
FEATURE [Sketcher::SketchObject] Sketch093
  AttachmentOffset = pos=(0,0,6.4) rot=(0,0,1;0rad)
  FullyConstrained = true
  MapMode = 5
  Placement = pos=(0,0,6.4) rot=(0,0,1;0rad)
  Support = -> [XY_Plane029]
  expr: .AttachmentOffset.Base.z = 2 * << pulley dims>>.guide_plate_thickness + << pulley dims>>.tooth_width - << pulley dims>>.p110_bearing_inset
  expr: Constraints[2] = << pulley dims>>.p110_axis_outer_diameter
  expr: Constraints[3] = << pulley dims>>.p110_axis_inner_diameter
  sketch-geometry (2):
    g0: Circle CenterX=0 CenterY=0 CenterZ=0 NormalX=0 NormalY=0 NormalZ=1 AngleXU=0 Radius=17.5
    g1: Circle CenterX=0 CenterY=0 CenterZ=0 NormalX=0 NormalY=0 NormalZ=1 AngleXU=0 Radius=7.5
  constraints (4):
    c: Coincident(g0,g-1)
    c: Coincident(g1,g0)
    c: Diameter(g0) = 35
    c: Diameter(g1) = 15
FEATURE [PartDesign::Pad] Pad035
  BaseFeature = -> Pocket063
  Direction = (0,0,1)
  Length = 16
  Length2 = 10
  Placement = pos=(0,0,1.2) rot=(0,0,1;0rad)
  Profile = -> Sketch093
  ReferenceAxis = -> Sketch093 [N_Axis]
  Type = 0
  expr: Length = << pulley dims>>.p110_axis_height
FEATURE [Sketcher::SketchObject] Sketch094
  AttachmentOffset = pos=(0,0,22.4) rot=(0,0,1;0rad)
  FullyConstrained = true
  MapMode = 5
  Placement = pos=(0,0,22.4) rot=(0,0,1;0rad)
  Support = -> [XY_Plane029]
  expr: .AttachmentOffset.Base.z = 2 * << pulley dims>>.guide_plate_thickness + << pulley dims>>.tooth_width - << pulley dims>>.p110_bearing_inset + << pulley dims>>.p110_axis_height
  expr: Constraints[1] = << pulley dims>>.axis_hole_diameter
  expr: Constraints[2] = << pulley dims>>.p110_axis_holeset_diameter
  expr: Constraints[6] = << pulley dims>>.p110_axis_holeset_diameter
  sketch-geometry (4):
    g0: Circle CenterX=-12.5 CenterY=0 CenterZ=0 NormalX=0 NormalY=0 NormalZ=1 AngleXU=0 Radius=1.8
    g1: Circle CenterX=12.5 CenterY=0 CenterZ=0 NormalX=0 NormalY=0 NormalZ=1 AngleXU=0 Radius=1.8
    g2: Circle CenterX=0 CenterY=12.5 CenterZ=0 NormalX=0 NormalY=0 NormalZ=1 AngleXU=0 Radius=1.8
    g3: Circle CenterX=1.7532e-12 CenterY=-12.5 CenterZ=0 NormalX=0 NormalY=0 NormalZ=1 AngleXU=0 Radius=1.8
  constraints (10):
    c: Horizontal(g0,g-1)
    c: Diameter(g0) = 3.6
    c: DistanceX(g0,g1) = 25
    c: Equal(g0,g3)
    c: Equal(g3,g1)
    c: Equal(g1,g2)
    c: DistanceY(g3,g2) = 25
    c: Symmetric(g2,g3,g-1)
    c: Symmetric(g0,g1,g-1)
    c: Vertical(g2,g-1)
FEATURE [Sketcher::SketchObject] Sketch095
  AttachmentOffset = pos=(0,0,6.4) rot=(0,0,1;0rad)
  FullyConstrained = true
  MapMode = 5
  Placement = pos=(0,0,6.4) rot=(0,0,1;0rad)
  Support = -> [XY_Plane029]
  expr: .AttachmentOffset.Base.z = 2 * << pulley dims>>.guide_plate_thickness + << pulley dims>>.tooth_width - << pulley dims>>.p110_bearing_inset
  expr: Constraints[1] = << pulley dims>>.p110_bearing_inner_diameter
  sketch-geometry (1):
    g0: Circle CenterX=0 CenterY=0 CenterZ=0 NormalX=0 NormalY=0 NormalZ=1 AngleXU=0 Radius=20
  constraints (2):
    c: Coincident(g0,g-1)
    c: Diameter(g0) = 40
FEATURE [PartDesign::Pad] Pad036
  BaseFeature = -> Pad035
  Direction = (0,0,1)
  Length = 1
  Length2 = 10
  Placement = pos=(0,0,1.2) rot=(0,0,1;0rad)
  Profile = -> Sketch095
  ReferenceAxis = -> Sketch095 [N_Axis]
  Type = 0
  expr: Length = << pulley dims>>.p110_bearing_threshhold_height
FEATURE [Sketcher::SketchObject] Sketch096
  FullyConstrained = true
  MapMode = 5
  Placement = pos=(0,0,0) rot=(0,1,0;3.14159rad)
  Support = -> [XY_Plane029]
  expr: Constraints[1] = << pulley dims>>.p110_axis_inner_diameter
  sketch-geometry (1):
    g0: Circle CenterX=0 CenterY=0 CenterZ=0 NormalX=0 NormalY=0 NormalZ=1 AngleXU=0 Radius=7.5
  constraints (2):
    c: Coincident(g0,g-1)
    c: Diameter(g0) = 15
FEATURE [PartDesign::Pocket] Pocket065
  BaseFeature = -> Pad036
  Direction = (0,0,1)
  Length = 5
  Length2 = 5
  Placement = pos=(0,0,1.2) rot=(0,0,1;0rad)
  Profile = -> Sketch096
  ReferenceAxis = -> Sketch096 [N_Axis]
  Type = 1
FEATURE [Part::FeaturePython] Clone009  label="base001"  # Draft clone (typed FeaturePython)
  AttacherType = Attacher::AttachEngine3D
  Fuse = false
  Objects = -> [Body015]
  Placement = pos=(0,6e-15,45) rot=(1,0,0;3.14159rad)
  Scale = (1,1,1)
FEATURE [Part::FeaturePython] Clone011  label="GT2 Pulley - Parametric_GT2 Pulley - Parametric003"  # Draft clone (typed FeaturePython)
  AttacherType = Attacher::AttachEngine3D
  Fuse = false
  Objects = -> [Part__Feature067]
  Placement = pos=(15,-2e-15,7) rot=(1,0,0;1.5708rad)
  Scale = (1,1,1)
FEATURE [Part::FeaturePython] timinggear001  # WARN: FeaturePython — macro-defined, semantics opaque (R4)
  AttacherType = Attacher::AttachEngine3D
  h = 0.75
  height = 7
  offset = 0.4
  pitch = 2
  r0 = 0.555
  r1 = 1
  rs = 0.15
  teeth = 20
  type = 0
  u = 0.254
  version = 0.0.3
  expr: height = << pulley dims>>.tooth_width
FEATURE [PartDesign::FeatureBase] BaseFeature003
  BaseFeature = -> timinggear001
  Placement = pos=(0,0,7) rot=(0,0,1;0rad)
  expr: .Placement.Base.z = << pulley dims>>.motor_axis_spacing
FEATURE [Sketcher::SketchObject] Sketch097
  FullyConstrained = true
  MapMode = 5
  Support = -> [XY_Plane031]
  expr: Constraints[1] = << pulley dims>>.motor_axis_main_diameter
  sketch-geometry (1):
    g0: Circle CenterX=0 CenterY=0 CenterZ=0 NormalX=0 NormalY=0 NormalZ=1 AngleXU=0 Radius=7.31
  constraints (2):
    c: Coincident(g0,g-1)
    c: Diameter(g0) = 14.62
FEATURE [PartDesign::Pad] Pad037
  BaseFeature = -> BaseFeature003
  Direction = (0,0,1)
  Length = 7
  Length2 = 10
  Placement = pos=(0,0,7) rot=(0,0,1;0rad)
  Profile = -> Sketch097
  ReferenceAxis = -> Sketch097 [N_Axis]
  Type = 0
  expr: Length = << pulley dims>>.motor_axis_spacing
FEATURE [Sketcher::SketchObject] Sketch098
  AttachmentOffset = pos=(0,0,14) rot=(0,0,1;0rad)
  FullyConstrained = true
  MapMode = 5
  Placement = pos=(0,0,14) rot=(0,0,1;0rad)
  Support = -> [XY_Plane031]
  expr: .AttachmentOffset.Base.z = << pulley dims>>.motor_axis_spacing + << pulley dims>>.tooth_width
  expr: Constraints[1] = << pulley dims>>.motor_axis_main_diameter
  sketch-geometry (1):
    g0: Circle CenterX=0 CenterY=0 CenterZ=0 NormalX=0 NormalY=0 NormalZ=1 AngleXU=0 Radius=7.31
  constraints (2):
    c: Coincident(g0,g-1)
    c: Diameter(g0) = 14.62
FEATURE [PartDesign::Pad] Pad038
  BaseFeature = -> Pad037
  Direction = (0,0,1)
  Length = 1.2
  Length2 = 10
  Placement = pos=(0,0,7) rot=(0,0,1;0rad)
  Profile = -> Sketch098
  ReferenceAxis = -> Sketch098 [N_Axis]
  Type = 0
  expr: Length = << pulley dims>>.guide_plate_thickness
FEATURE [Sketcher::SketchObject] Sketch099
  AttachmentOffset = pos=(0,0,15.2) rot=(0,0,1;0rad)
  FullyConstrained = true
  MapMode = 5
  Placement = pos=(0,0,15.2) rot=(0,0,1;0rad)
  Support = -> [XY_Plane031]
  expr: .AttachmentOffset.Base.z = << pulley dims>>.motor_axis_spacing + << pulley dims>>.tooth_width + << pulley dims>>.guide_plate_thickness
  expr: Constraints[1] = << pulley dims>>.motor_axis_diameter
  expr: Constraints[5] = << pulley dims>>.motor_axis_flat_area
  sketch-geometry (2):
    g0: ArcOfCircle CenterX=0 CenterY=0 CenterZ=0 NormalX=0 NormalY=0 NormalZ=1 AngleXU=0 Radius=2.6 StartAngle=2.18575 EndAngle=7.23903
    g1: LineSegment StartX=-1.5 StartY=2.12368 StartZ=0 EndX=1.5 EndY=2.12368 EndZ=0
  constraints (6):
    c: Coincident(g0,g-1)
    c: Diameter(g0) = 5.2
    c: Horizontal(g1)
    c: Coincident(g1,g0)
    c: Coincident(g1,g0)
    c: DistanceX(g1,g1) = 3
FEATURE [PartDesign::Pocket] Pocket066
  BaseFeature = -> Pad038
  Direction = (0,0,-1)
  Length = 5
  Length2 = 5
  Placement = pos=(0,0,7) rot=(0,0,1;0rad)
  Profile = -> Sketch099
  ReferenceAxis = -> Sketch099 [N_Axis]
  Type = 1
FEATURE [PartDesign::Chamfer] Chamfer002
  Angle = 45
  Base = -> Pocket066 [Edge370,Edge2]
  BaseFeature = -> Pocket066
  ChamferType = 0
  FlipDirection = false
  Placement = pos=(0,0,7) rot=(0,0,1;0rad)
  Size = 0.8
  Size2 = 1
  SupportTransform = false
  UseAllEdges = false
FEATURE [Part::Part2DObjectPython] ShapeString016  # Draft 2D object (typed FeaturePython)
  AttachmentOffset = pos=(-3,3,15.2) rot=(0,0,1;0rad)
  FontFile = <path>
  MakeFace = true
  MapMode = 5
  Placement = pos=(-3,3,15.2) rot=(0,0,1;0rad)
  Size = 4
  String = v3
  Support = -> [XY_Plane027]
  Tracking = 0
  expr: .AttachmentOffset.Base.z = << pulley dims>>.motor_axis_spacing + << pulley dims>>.tooth_width + << pulley dims>>.guide_plate_thickness
  expr: Size = <<global settings>>.label_font_size * 0.8
FEATURE [PartDesign::Pocket] Pocket067
  BaseFeature = -> Chamfer002
  Direction = (0,0,-1)
  Length = 0.4
  Length2 = 5
  Placement = pos=(0,0,7) rot=(0,0,1;0rad)
  Profile = -> ShapeString016
  ReferenceAxis = -> ShapeString016 [N_Axis]
  Type = 0
  expr: Length = <<global settings>>.label_text_depth
FEATURE [PartDesign::Body] Body017  label="gt2 pully - base motor"
  BaseFeature = -> timinggear001
  Group = -> [BaseFeature003,Sketch097,Pad037,Sketch098,Pad038,Sketch099,Pocket066,Chamfer002,ShapeString016,Pocket067]
  Origin = -> Origin031
  Tip = -> Pocket067
FEATURE [Part::FeaturePython] Clone012  label="gt2 pully - base motor001"  # Draft clone (typed FeaturePython)
  AttacherType = Attacher::AttachEngine3D
  Fuse = false
  Objects = -> [Body017]
  Placement = pos=(37,34,22) rot=(0,1,0;3.14159rad)
  Scale = (1,1,1)
FEATURE [Part::Part2DObjectPython] ShapeString017  # Draft 2D object (typed FeaturePython)
  AttachmentOffset = pos=(-7,22,6.4) rot=(0,0,1;0rad)
  FontFile = <path>
  MakeFace = true
  MapMode = 5
  Placement = pos=(-7,22,6.4) rot=(0,0,1;0rad)
  Size = 5
  String = v1.1
  Support = -> [XY_Plane029]
  Tracking = 0
  expr: .AttachmentOffset.Base.z = 2 * << pulley dims>>.guide_plate_thickness + << pulley dims>>.tooth_width - << pulley dims>>.p110_bearing_inset
  expr: Size = <<global settings>>.label_font_size
FEATURE [PartDesign::Chamfer] Chamfer003
  Angle = 45
  Base = -> Pocket065 [Edge2,Edge1987]
  BaseFeature = -> Pocket065
  ChamferType = 0
  FlipDirection = false
  Placement = pos=(0,0,1.2) rot=(0,0,1;0rad)
  Size = 0.3
  Size2 = 1
  SupportTransform = false
  UseAllEdges = false
FEATURE [Part::FeaturePython] Clone013  label="GT2 Pulley - 22 - 80 teeth_GT2 Pulley - Parametric001"  # Draft clone (typed FeaturePython)
  AttacherType = Attacher::AttachEngine3D
  Fuse = false
  Objects = -> [Part__Feature066]
  Placement = pos=(-59.5,0,1.3) rot=(1,0,0;1.5708rad)
  Scale = (1,1,1)
FEATURE [Sketcher::SketchObject] Sketch103
  FullyConstrained = true
  MapMode = 5
  Placement = pos=(0,0,0) rot=(1,0,0;1.5708rad)
  Support = -> [XZ_Plane032]
  expr: Constraints[27] = << pulley dims>>.guide_plate_thickness
  expr: Constraints[28] = << pulley dims>>.tooth_width
  expr: Constraints[37] = << pulley dims>>.guide_plate_thickness
  expr: Constraints[43] = << pulley dims>>.guide_plate_thickness
  sketch-geometry (16):
    g0: LineSegment StartX=0 StartY=0 StartZ=0 EndX=26.5 EndY=0 EndZ=0
    g1: LineSegment StartX=26.5 StartY=0 StartZ=0 EndX=26.5 EndY=1.2 EndZ=0
    g2: LineSegment StartX=26.5 StartY=1.2 StartZ=0 EndX=4 EndY=1.2 EndZ=0
    g3: LineSegment StartX=4 StartY=1.2 StartZ=0 EndX=4 EndY=8.2 EndZ=0
    g4: LineSegment StartX=4 StartY=8.2 StartZ=0 EndX=25.6 EndY=8.2 EndZ=0
    g5: LineSegment StartX=26.5 StartY=9.1 StartZ=0 EndX=26.5 EndY=9.4 EndZ=0
    g6: LineSegment StartX=26.5 StartY=9.4 StartZ=0 EndX=7.7 EndY=9.4 EndZ=0
    g7: LineSegment StartX=7.7 StartY=9.4 StartZ=0 EndX=7.7 EndY=10.6 EndZ=0
    g8: LineSegment StartX=7.7 StartY=10.6 StartZ=0 EndX=4 EndY=10.6 EndZ=0
    g9: LineSegment StartX=4 StartY=10.6 StartZ=0 EndX=4 EndY=17.6 EndZ=0
    g10: LineSegment StartX=4 StartY=17.6 StartZ=0 EndX=6.8 EndY=17.6 EndZ=0
    g11: LineSegment StartX=7.7 StartY=18.5 StartZ=0 EndX=7.7 EndY=18.8 EndZ=0
    g12: LineSegment StartX=7.7 StartY=18.8 StartZ=0 EndX=0 EndY=18.8 EndZ=0
    g13: LineSegment StartX=0 StartY=18.8 StartZ=0 EndX=0 EndY=0 EndZ=0
    g14: LineSegment StartX=6.8 StartY=17.6 StartZ=0 EndX=7.7 EndY=18.5 EndZ=0
    g15: LineSegment StartX=25.6 StartY=8.2 StartZ=0 EndX=26.5 EndY=9.1 EndZ=0
  constraints (47):
    c: Coincident(g0,g-1)
    c: Horizontal(g0)
    c: Coincident(g0,g1)
    c: Vertical(g1)
    c: Coincident(g1,g2)
    c: Horizontal(g2)
    c: Coincident(g2,g3)
    c: Vertical(g3)
    c: Coincident(g3,g4)
    c: Horizontal(g4)
    c: Vertical(g5)
    c: Coincident(g5,g6)
    c: Horizontal(g6)
    c: Coincident(g6,g7)
    c: Vertical(g7)
    c: Coincident(g7,g8)
    c: Horizontal(g8)
    c: Coincident(g8,g9)
    c: Vertical(g9)
    c: Coincident(g9,g10)
    c: Horizontal(g10)
    c: Vertical(g11)
    c: Coincident(g11,g12)
    c: Horizontal(g12)
    c: Coincident(g12,g13)
    c: Coincident(g13,g0)
    c: Vertical(g13)
    c: DistanceY(g1,g1) = 1.2
    c: DistanceY(g3,g3) = 7
    c: Equal(g3,g9)
    c: DistanceX(g12,g12) = 7.7
    c: DistanceX(g6,g6) = 18.8
    c: DistanceX(g12,g9) = 4
    c: Vertical(g8,g3)
    c: Coincident(g14,g10)
    c: Coincident(g14,g11)
    c: Angle(g14) = 0.785398
    c: DistanceY(g10,g11) = 1.2
    c: DistanceY(g10,g11) = 0.9
    c: Vertical(g7,g11)
    c: Coincident(g15,g5)
    c: Coincident(g15,g4)
    c: Angle(g15) = 0.785398
    c: DistanceY(g4,g5) = 1.2
    c: Equal(g7,g1)
    c: Equal(g14,g15)
    c: Vertical(g1,g5)
FEATURE [PartDesign::Revolution] Revolution001
  Angle = 360
  Axis = (0,-2e-16,1)
  Base = (0,0,0)
  Placement = pos=(0,0,0) rot=(1,0,0;1.5708rad)
  Profile = -> Sketch103
  ReferenceAxis = -> Sketch103 [V_Axis]
  Reversed = true
FEATURE [Part::FeaturePython] timinggear002  # WARN: FeaturePython — macro-defined, semantics opaque (R4)
  AttacherType = Attacher::AttachEngine3D
  AttachmentOffset = pos=(0,0,1.2) rot=(0,0,1;0rad)
  MapMode = 5
  Placement = pos=(0,0,1.2) rot=(0,0,1;0rad)
  Support = -> [XY_Plane034]
  h = 0.75
  height = 7
  offset = 0.4
  pitch = 2
  r0 = 0.555
  r1 = 1
  rs = 0.15
  teeth = 80
  type = 0
  u = 0.254
  version = 0.0.3
  expr: .AttachmentOffset.Base.z = << pulley dims>>.guide_plate_thickness
  expr: height = << pulley dims>>.tooth_width
FEATURE [Part::FeaturePython] timinggear003  # WARN: FeaturePython — macro-defined, semantics opaque (R4)
  AttacherType = Attacher::AttachEngine3D
  AttachmentOffset = pos=(0,0,10.6) rot=(0,0,1;0rad)
  MapMode = 5
  Placement = pos=(0,0,10.6) rot=(0,0,1;0rad)
  Support = -> [XY_Plane034]
  h = 0.75
  height = 7
  offset = 0.4
  pitch = 2
  r0 = 0.555
  r1 = 1
  rs = 0.15
  teeth = 22
  type = 0
  u = 0.254
  version = 0.0.3
  expr: .AttachmentOffset.Base.z = 3 * << pulley dims>>.guide_plate_thickness + << pulley dims>>.tooth_width
  expr: height = << pulley dims>>.tooth_width
FEATURE [Part::Part2DObjectPython] ShapeString018  # Draft 2D object (typed FeaturePython)
  AttachmentOffset = pos=(-11,13,9.4) rot=(0,0,1;0rad)
  FontFile = <path>
  MakeFace = true
  MapMode = 5
  Placement = pos=(-11,13,9.4) rot=(0,0,1;0rad)
  Size = 5
  String = v1.0
  Support = -> [XY_Plane032]
  Tracking = 0
  expr: .AttachmentOffset.Base.z = 2 * << pulley dims>>.guide_plate_thickness + << pulley dims>>.tooth_width
  expr: Size = <<global settings>>.label_font_size
FEATURE [PartDesign::Pocket] Pocket069
  BaseFeature = -> Revolution001
  Direction = (0,0,-1)
  Length = 0.4
  Length2 = 5
  Placement = pos=(0,0,0) rot=(1,0,0;1.5708rad)
  Profile = -> ShapeString018
  ReferenceAxis = -> ShapeString018 [N_Axis]
  Type = 0
  expr: Length = <<global settings>>.label_text_depth
FEATURE [PartDesign::Body] Body018  label="gt2 pulley ratio change base"
  Group = -> [Sketch103,Revolution001,ShapeString018,Pocket069]
  Origin = -> Origin032
  Tip = -> Pocket069
FEATURE [Part::MultiFuse] Fusion
  Shapes = -> [Body018,timinggear002,timinggear003]
FEATURE [PartDesign::FeatureBase] BaseFeature004
  BaseFeature = -> Fusion
FEATURE [Sketcher::SketchObject] Sketch104
  FullyConstrained = true
  MapMode = 5
  Support = -> [XY_Plane035]
  sketch-geometry (1):
    g0: Circle CenterX=0 CenterY=0 CenterZ=0 NormalX=0 NormalY=0 NormalZ=1 AngleXU=0 Radius=4
  constraints (2):
    c: Coincident(g0,g-1)
    c: Diameter(g0) = 8
FEATURE [PartDesign::Pocket] Pocket070
  BaseFeature = -> BaseFeature004
  Direction = (0,0,-1)
  Length = 5
  Length2 = 5
  Profile = -> Sketch104
  ReferenceAxis = -> Sketch104 [N_Axis]
  Reversed = true
  Type = 1
FEATURE [PartDesign::FeaturePython] involutegear  # WARN: FeaturePython — macro-defined, semantics opaque (R4)
  AttacherType = Attacher::AttachEngine3D
  BaseFeature = -> Pocket070
  backlash = 0
  beta = 0
  clearance = 0.25
  da = 17
  df = 12.5
  double_helix = false
  dw = 15
  head = 0
  height = 5
  module = 1
  numpoints = 6
  pressure_angle = 20
  properties_from_tool = false
  reversed_backlash = false
  shift = 0
  simple = false
  teeth = 15
  transverse_pitch = 3.14159
  undercut = false
  version = 0.0.3
FEATURE [PartDesign::FeaturePython] involutegear001  # WARN: FeaturePython — macro-defined, semantics opaque (R4)
  AttacherType = Attacher::AttachEngine3D
  BaseFeature = -> involutegear
  backlash = 0
  beta = 0
  clearance = 0.25
  da = 17
  df = 12.5
  double_helix = false
  dw = 15
  head = 0
  height = 5
  module = 1
  numpoints = 6
  pressure_angle = 20
  properties_from_tool = false
  reversed_backlash = false
  shift = 0
  simple = false
  teeth = 15
  transverse_pitch = 3.14159
  undercut = false
  version = 0.0.3
FEATURE [PartDesign::Body] Body019
  BaseFeature = -> Fusion
  Group = -> [BaseFeature004,Sketch104,Pocket070,involutegear,involutegear001]
  Origin = -> Origin035
  Tip = -> involutegear001
FEATURE [App::Part] Part012  label="gt2 pulley ratio change"
  Group = -> [Body018,timinggear002,timinggear003,Fusion,Body019]
  Origin = -> Origin034
FEATURE [Part::Feature] Part__Feature178  label="J1 coupler_J1 coupler001"
  Placement = pos=(-125,1.8e-15,8) rot=(1,0,0;4.71239rad)
  shape: bbox 120 x 120 x 27 mm, 92 faces (baked)
FEATURE [Sketcher::SketchObject] Sketch105
  FullyConstrained = true
  MapMode = 5
  Support = -> [XY_Plane036]
  expr: Constraints[17] = <<vert base dims>>.base_smooth_rod_diameter
  expr: Constraints[19] = << pulley dims>>.p110_axis_inner_diameter
  expr: Constraints[1] = <<vert base dims>>.base_diameter
  expr: Constraints[3] = <<vert base dims>>.base_smooth_rod_set_diameter
  sketch-geometry (9):
    g0: Circle CenterX=0 CenterY=0 CenterZ=0 NormalX=0 NormalY=0 NormalZ=1 AngleXU=0 Radius=60
    g1: Circle CenterX=0 CenterY=0 CenterZ=0 NormalX=0 NormalY=0 NormalZ=1 AngleXU=0 Radius=47.5
    g2: Circle CenterX=-33.5876 CenterY=33.5876 CenterZ=0 NormalX=0 NormalY=0 NormalZ=1 AngleXU=0 Radius=5
    g3: Circle CenterX=33.5876 CenterY=33.5876 CenterZ=0 NormalX=0 NormalY=0 NormalZ=1 AngleXU=0 Radius=5
    g4: Circle CenterX=33.5876 CenterY=-33.5876 CenterZ=0 NormalX=0 NormalY=0 NormalZ=1 AngleXU=0 Radius=5
    g5: Circle CenterX=-33.5876 CenterY=-33.5876 CenterZ=0 NormalX=0 NormalY=0 NormalZ=1 AngleXU=0 Radius=5
    g6: LineSegment StartX=-33.5876 StartY=-33.5876 StartZ=0 EndX=33.5876 EndY=-33.5876 EndZ=0
    g7: LineSegment StartX=33.5876 StartY=-33.5876 StartZ=0 EndX=33.5876 EndY=33.5876 EndZ=0
    g8: Circle CenterX=0 CenterY=0 CenterZ=0 NormalX=0 NormalY=0 NormalZ=1 AngleXU=0 Radius=7.5
  constraints (20):
    c: Coincident(g0,g-1)
    c: Diameter(g0) = 120
    c: Coincident(g1,g0)
    c: Diameter(g1) = 95
    c: PointOnObject(g2,g1)
    c: PointOnObject(g3,g1)
    c: Symmetric(g5,g3,g0)
    c: Symmetric(g4,g2,g0)
    c: Horizontal(g4,g5)
    c: Coincident(g6,g5)
    c: Coincident(g7,g4)
    c: Coincident(g3,g7)
    c: Coincident(g4,g6)
    c: Equal(g7,g6)
    c: Equal(g4,g5)
    c: Equal(g5,g2)
    c: Equal(g2,g3)
    c: Diameter(g5) = 10
    c: Coincident(g8,g0)
    c: Diameter(g8) = 15
FEATURE [PartDesign::Pad] Pad039
  Direction = (0,0,1)
  Length = 8
  Length2 = 10
  Profile = -> Sketch105
  ReferenceAxis = -> Sketch105 [N_Axis]
  Type = 0
  expr: Length = <<vert base dims>>.base_bottom_thickness
FEATURE [Sketcher::SketchObject] Sketch106
  FullyConstrained = true
  MapMode = 5
  Support = -> [XY_Plane036]
  expr: Constraints[1] = <<vert base dims>>.screwhole_offset
  expr: Constraints[2] = <<vert base dims>>.screwholes
  sketch-geometry (1):
    g0: Circle CenterX=49.5 CenterY=0 CenterZ=0 NormalX=0 NormalY=0 NormalZ=1 AngleXU=0 Radius=2.05
  constraints (3):
    c: PointOnObject(g0,g-1)
    c: DistanceX(g-1,g0) = 49.5
    c: Diameter(g0) = 4.1
FEATURE [PartDesign::Pocket] Pocket071
  BaseFeature = -> Pad039
  Direction = (0,0,-1)
  Length = 5
  Length2 = 5
  Profile = -> Sketch106
  ReferenceAxis = -> Sketch106 [N_Axis]
  Reversed = true
  Type = 1
FEATURE [PartDesign::PolarPattern] PolarPattern005
  Angle = 360
  Axis = -> Sketch106 [N_Axis]
  BaseFeature = -> Pocket071
  Occurrences = 12
  Originals = -> [Pocket071]
  Overlap = 0
  expr: Occurrences = <<vert base dims>>.num_screwholes
FEATURE [PartDesign::Pocket] Pocket072
  BaseFeature = -> Chamfer003
  Direction = (0,0,-1)
  Length = 5
  Length2 = 5
  Placement = pos=(0,0,1.2) rot=(0,0,1;0rad)
  Profile = -> Sketch094
  ReferenceAxis = -> Sketch094 [N_Axis]
  Type = 1
FEATURE [PartDesign::Pocket] Pocket073
  BaseFeature = -> Pocket072
  Direction = (0,0,-1)
  Length = 0.4
  Length2 = 5
  Placement = pos=(0,0,1.2) rot=(0,0,1;0rad)
  Profile = -> ShapeString017
  ReferenceAxis = -> ShapeString017 [N_Axis]
  Type = 0
  expr: Length = <<global settings>>.label_text_depth
FEATURE [PartDesign::Body] Body016  label="gt2 pulley - 110 teeth"
  BaseFeature = -> timinggear
  Group = -> [BaseFeature002,Sketch090,Pad033,Sketch091,Pad034,Sketch092,Pocket063,Sketch093,Pad035,Sketch094,Sketch095,Pad036,Sketch096,Pocket065,ShapeString017,Chamfer003,Pocket072,Pocket073]
  Origin = -> Origin029
  Tip = -> Pocket073
FEATURE [Part::FeaturePython] Clone010  label="gt2 pulley - 110 teeth001"  # Draft clone (typed FeaturePython)
  AttacherType = Attacher::AttachEngine3D
  Fuse = false
  Objects = -> [Body016]
  Placement = pos=(150,0,16) rot=(0,0,1;0rad)
  Scale = (1,1,1)
FEATURE [App::Part] Part011  label="constructed base"
  Group = -> [Clone009,Clone010,Clone012]
  Origin = -> Origin030
FEATURE [App::Part] Part010  label="Main base"
  Group = -> [Spreadsheet006,Body015,Body016,timinggear,Part011,Body017,timinggear001,Part012]
  Origin = -> Origin027
FEATURE [Sketcher::SketchObject] Sketch107
  AttachmentOffset = pos=(0,0,8) rot=(0,0,1;0rad)
  FullyConstrained = true
  MapMode = 5
  Placement = pos=(0,0,8) rot=(0,0,1;0rad)
  Support = -> [XY_Plane036]
  expr: .AttachmentOffset.Base.z = <<vert base dims>>.base_bottom_thickness
  expr: Constraints[2] = << pulley dims>>.p110_axis_inner_diameter
  expr: Constraints[3] = << pulley dims>>.p110_axis_outer_diameter
  sketch-geometry (2):
    g0: Circle CenterX=0 CenterY=0 CenterZ=0 NormalX=0 NormalY=0 NormalZ=1 AngleXU=0 Radius=17.5
    g1: Circle CenterX=0 CenterY=0 CenterZ=0 NormalX=0 NormalY=0 NormalZ=1 AngleXU=0 Radius=7.5
  constraints (4):
    c: Coincident(g0,g-1)
    c: Coincident(g1,g0)
    c: Diameter(g1) = 15
    c: Diameter(g0) = 35
FEATURE [PartDesign::Pad] Pad040
  BaseFeature = -> PolarPattern005
  Direction = (0,0,1)
  Length = 19
  Length2 = 10
  Profile = -> Sketch107
  ReferenceAxis = -> Sketch107 [N_Axis]
  Type = 0
  expr: Length = <<vert base dims>>.base_axis_height
FEATURE [Sketcher::SketchObject] Sketch108
  AttachmentOffset = pos=(0,0,8) rot=(0,0,1;0rad)
  FullyConstrained = true
  MapMode = 5
  Placement = pos=(0,0,8) rot=(0,0,1;0rad)
  Support = -> [XY_Plane036]
  expr: .AttachmentOffset.Base.z = <<vert base dims>>.base_bottom_thickness
  expr: Constraints[2] = << pulley dims>>.p110_axis_outer_diameter
  expr: Constraints[3] = << pulley dims>>.p110_bearing_inner_diameter
  sketch-geometry (2):
    g0: Circle CenterX=0 CenterY=0 CenterZ=0 NormalX=0 NormalY=0 NormalZ=1 AngleXU=0 Radius=20
    g1: Circle CenterX=0 CenterY=0 CenterZ=0 NormalX=0 NormalY=0 NormalZ=1 AngleXU=0 Radius=17.5
  constraints (4):
    c: Coincident(g0,g-1)
    c: Coincident(g1,g0)
    c: Diameter(g1) = 35
    c: Diameter(g0) = 40
FEATURE [PartDesign::Pad] Pad041
  BaseFeature = -> Pad040
  Direction = (0,0,1)
  Length = 1
  Length2 = 10
  Profile = -> Sketch108
  ReferenceAxis = -> Sketch108 [N_Axis]
  Type = 0
  expr: Length = << pulley dims>>.p110_bearing_threshhold_height
FEATURE [Sketcher::SketchObject] Sketch109
  AttachmentOffset = pos=(0,0,8) rot=(0,0,1;0rad)
  FullyConstrained = true
  MapMode = 5
  Placement = pos=(0,0,8) rot=(0,0,1;0rad)
  Support = -> [XY_Plane036]
  expr: .AttachmentOffset.Base.z = <<vert base dims>>.base_bottom_thickness
  expr: Constraints[14] = 180deg - 180deg / <<vert base dims>>.num_screwholes
  expr: Constraints[2] = << pulley dims>>.p110_bearing_outer_diameter
  expr: Constraints[3] = << pulley dims>>.p110_bearing_outer_diameter + <<vert base dims>>.base_enforcement_wall_thickness * 2
  expr: Constraints[8] = <<vert base dims>>.base_stop_thickness
  expr: Constraints[9] = <<vert base dims>>.base_stop_length
  sketch-geometry (6):
    g0: Circle CenterX=0 CenterY=0 CenterZ=0 NormalX=0 NormalY=0 NormalZ=1 AngleXU=0 Radius=31
    g1: ArcOfCircle CenterX=0 CenterY=0 CenterZ=0 NormalX=0 NormalY=0 NormalZ=1 AngleXU=0 Radius=35 StartAngle=4.53641 EndAngle=10.648
    g2: LineSegment StartX=-11.9231 StartY=-32.9065 StartZ=0 EndX=-12.8626 EndY=-36.4128 EndZ=0
    g3: LineSegment StartX=-6.12755 StartY=-34.4594 StartZ=0 EndX=-7.06706 EndY=-37.9658 EndZ=0
    g4: ArcOfCircle CenterX=-9.96484 CenterY=-37.1893 CenterZ=0 NormalX=0 NormalY=0 NormalZ=1 AngleXU=0 Radius=3 StartAngle=2.87979 EndAngle=6.02139
    g5: LineSegment StartX=-9.96484 StartY=-37.1893 StartZ=0 EndX=-9.02533 EndY=-33.683 EndZ=0
  constraints (15):
    c: Coincident(g0,g-1)
    c: Coincident(g1,g0)
    c: Diameter(g0) = 62
    c: Diameter(g1) = 70
    c: Tangent(g4,g2) = -1.5708
    c: Tangent(g4,g3) = 1.5708
    c: Equal(g3,g2)
    c: Parallel(g2,g3)
    c: Diameter(g4) = 6
    c: Distance(g3) = 3.63
    c: Coincident(g5,g4)
    c: Symmetric(g2,g3,g5)
    c: Coincident(g1,g3)
    c: Coincident(g1,g2)
    c: Angle(g-2,g5) = 2.87979
FEATURE [PartDesign::Pad] Pad042
  BaseFeature = -> Pad041
  Direction = (0,0,1)
  Length = 12.5
  Length2 = 10
  Profile = -> Sketch109
  ReferenceAxis = -> Sketch109 [N_Axis]
  Type = 0
  expr: Length = <<vert base dims>>.base_enforcement_wall_height
FEATURE [Sketcher::SketchObject] Sketch110
  AttachmentOffset = pos=(0,0,6) rot=(0,0,1;0rad)
  FullyConstrained = true
  MapMode = 5
  Placement = pos=(0,0,6) rot=(0,0,1;0rad)
  Support = -> [XY_Plane036]
  expr: .AttachmentOffset.Base.z = <<vert base dims>>.base_bottom_thickness - <<vert base dims>>.base_rod_support_depth
  expr: Constraints[15] = << pulley dims>>.p110_bearing_outer_diameter / 2
  expr: Constraints[1] = <<vert base dims>>.base_smooth_rod_set_diameter
  expr: Constraints[5] = <<vert base dims>>.base_smooth_rod_diameter
  sketch-geometry (6):
    g0: Circle CenterX=0 CenterY=0 CenterZ=0 NormalX=0 NormalY=0 NormalZ=1 AngleXU=0 Radius=47.5
    g1: ArcOfCircle CenterX=33.5876 CenterY=-33.5876 CenterZ=0 NormalX=0 NormalY=0 NormalZ=1 AngleXU=0 Radius=5 StartAngle=3.92699 EndAngle=7.06858
    g2: LineSegment StartX=37.1231 StartY=-30.052 StartZ=0 EndX=25.1688 EndY=-18.0978 EndZ=0
    g3: LineSegment StartX=30.052 StartY=-37.1231 StartZ=0 EndX=18.0978 EndY=-25.1688 EndZ=0
    g4: ArcOfCircle CenterX=0 CenterY=0 CenterZ=0 NormalX=0 NormalY=0 NormalZ=1 AngleXU=0 Radius=31 StartAngle=5.33579 EndAngle=5.65979
    g5: LineSegment StartX=33.5876 StartY=-33.5876 StartZ=0 EndX=21.9203 EndY=-21.9203 EndZ=0
  constraints (16):
    c: Coincident(g0,g-1)
    c: Diameter(g0) = 95
    c: PointOnObject(g1,g0)
    c: Tangent(g2,g1) = -1.5708
    c: Tangent(g3,g1) = 1.5708
    c: Diameter(g1) = 10
    c: Coincident(g4,g0)
    c: Coincident(g3,g4)
    c: Coincident(g2,g4)
    c: Coincident(g5,g1)
    c: PointOnObject(g5,g4)
    c: Perpendicular(g4,g5)
    c: Parallel(g2,g5)
    c: Parallel(g5,g3)
    c: Angle(g5) = 2.35619
    c: Distance(g4,g5) = 31
FEATURE [PartDesign::Pad] Pad043
  BaseFeature = -> Pad042
  Direction = (0,0,1)
  Length = 9.5
  Length2 = 10
  Profile = -> Sketch110
  ReferenceAxis = -> Sketch110 [N_Axis]
  Type = 0
  expr: Length = <<vert base dims>>.base_rod_support_high_side + <<vert base dims>>.base_rod_support_depth
FEATURE [PartDesign::PolarPattern] PolarPattern006
  Angle = 360
  Axis = -> Sketch110 [N_Axis]
  BaseFeature = -> Pad043
  Occurrences = 4
  Originals = -> [Pad043]
  Overlap = 0
FEATURE [Sketcher::SketchObject] Sketch111
  AttachmentOffset = pos=(0,0,0) rot=(0,1,0;0.785398rad)
  FullyConstrained = false
  MapMode = 5
  Placement = pos=(0,0,0) rot=(0.862856,0.357407,0.357407;1.71777rad)
  Support = -> [XZ_Plane036]
  expr: Constraints[7] = << pulley dims>>.p110_bearing_outer_diameter / 2 + <<vert base dims>>.base_enforcement_wall_thickness
  expr: Constraints[8] = <<vert base dims>>.base_bottom_thickness + <<vert base dims>>.base_rod_support_high_side
  expr: Constraints[9] = -<<vert base dims>>.base_rod_support_slope
  sketch-geometry (4):
    g0: LineSegment StartX=35 StartY=15.5 StartZ=0 EndX=58.9118 EndY=9.58244 EndZ=0
    g1: LineSegment StartX=58.9118 StartY=9.58244 StartZ=0 EndX=58.9118 EndY=20.0813 EndZ=0
    g2: LineSegment StartX=58.9118 StartY=20.0813 StartZ=0 EndX=35 EndY=20.0813 EndZ=0
    g3: LineSegment StartX=35 StartY=20.0813 StartZ=0 EndX=35 EndY=15.5 EndZ=0
  constraints (10):
    c: Coincident(g0,g1)
    c: Vertical(g1)
    c: Coincident(g1,g2)
    c: Horizontal(g2)
    c: Coincident(g2,g3)
    c: Coincident(g3,g0)
    c: Vertical(g3)
    c: DistanceX(g-1,g0) = 35
    c: DistanceY(g-1,g0) = 15.5
    c: Angle(g0) = -0.242601
FEATURE [PartDesign::Groove] Groove001
  Angle = 20
  Axis = (0,2e-16,1)
  Base = (0,0,0)
  BaseFeature = -> PolarPattern006
  Midplane = true
  Profile = -> Sketch111
  ReferenceAxis = -> Sketch111 [V_Axis]
FEATURE [PartDesign::PolarPattern] PolarPattern007
  Angle = 360
  Axis = -> Z_Axis036
  BaseFeature = -> Groove001
  Occurrences = 4
  Originals = -> [Groove001]
  Overlap = 0
FEATURE [Sketcher::SketchObject] Sketch112
  FullyConstrained = false
  MapMode = 5
  Placement = pos=(0,0,0) rot=(0,1,0;3.14159rad)
  Support = -> [XY_Plane036]
  expr: Constraints[2] = << pulley dims>>.p110_axis_holeset_diameter
  expr: Constraints[5] = << pulley dims>>.p110_axis_holeset_diameter
  sketch-geometry (4):
    g0: Circle CenterX=12.5 CenterY=0 CenterZ=0 NormalX=0 NormalY=0 NormalZ=1 AngleXU=0 Radius=3.29534
    g1: Circle CenterX=0 CenterY=-12.5 CenterZ=0 NormalX=0 NormalY=0 NormalZ=1 AngleXU=0 Radius=3.29534
    g2: Circle CenterX=-12.5 CenterY=0 CenterZ=0 NormalX=0 NormalY=0 NormalZ=1 AngleXU=0 Radius=3.29534
    g3: Circle CenterX=0 CenterY=12.5 CenterZ=0 NormalX=0 NormalY=0 NormalZ=1 AngleXU=0 Radius=3.29534
  constraints (9):
    c: Horizontal(g2,g0)
    c: Equal(g2,g0)
    c: DistanceX(g2,g0) = 25
    c: Symmetric(g2,g0,g-1)
    c: Vertical(g1,g3)
    c: DistanceY(g1,g3) = 25
    c: Equal(g2,g3)
    c: Equal(g3,g1)
    c: Symmetric(g3,g1,g-1)
FEATURE [PartDesign::Hole] Hole004
  BaseFeature = -> PolarPattern007
  CustomThreadClearance = 0
  Depth = 346.66
  DepthType = 1
  Diameter = 3.6
  DrillForDepth = false
  DrillPoint = 1
  DrillPointAngle = 118
  HoleCutCountersinkAngle = 90
  HoleCutCustomValues = true
  HoleCutDepth = 3.2
  HoleCutDiameter = 7.5
  HoleCutType = 7
  ModelThread = false
  Profile = -> Sketch112
  Tapered = false
  TaperedAngle = 90
  ThreadClass = 0
  ThreadDepth = 346.66
  ThreadDepthType = 0
  ThreadDirection = 0
  ThreadFit = 2
  ThreadSize = 9
  ThreadType = 1
  Threaded = false
  UseCustomThreadClearance = false
FEATURE [Part::Part2DObjectPython] ShapeString019  # Draft 2D object (typed FeaturePython)
  AttachmentOffset = pos=(-7,39,8) rot=(0,0,1;0rad)
  FontFile = <path>
  MakeFace = true
  MapMode = 5
  Placement = pos=(-7,39,8) rot=(0,0,1;0rad)
  Size = 5
  String = v1.0
  Support = -> [XY_Plane036]
  Tracking = 0
  expr: .AttachmentOffset.Base.z = <<vert base dims>>.base_bottom_thickness
  expr: Size = <<global settings>>.label_font_size
FEATURE [PartDesign::Pocket] Pocket074
  BaseFeature = -> Hole004
  Direction = (0,0,-1)
  Length = 0.4
  Length2 = 5
  Profile = -> ShapeString019
  ReferenceAxis = -> ShapeString019 [N_Axis]
  Type = 0
  expr: Length = <<global settings>>.label_text_depth
FEATURE [PartDesign::Body] Body020  label="Main vertical coupler"
  Group = -> [Sketch105,Pad039,Sketch106,Pocket071,PolarPattern005,Sketch107,Pad040,Sketch108,Pad041,Sketch109,Pad042,Sketch110,Pad043,PolarPattern006,Sketch111,Groove001,PolarPattern007,Sketch112,Hole004,ShapeString019,Pocket074]
  Origin = -> Origin036
  Tip = -> Pocket074
FEATURE [Part::FeaturePython] Clone014  label="Main vertical coupler001"  # Draft clone (typed FeaturePython)
  AttacherType = Attacher::AttachEngine3D
  Fuse = false
  Objects = -> [Body020]
  Placement = pos=(150,1,70) rot=(1,0,0;3.14159rad)
  Scale = (1,1,1)
FEATURE [App::Part] Part013  label="constructed vertical base"
  Group = -> [Clone014]
  Origin = -> Origin037
FEATURE [Part::Feature] Part__Feature179  label="Smooth Rod Clamp_Smooth Rod Clamp008"
  Placement = pos=(12.4233,46.3644,-1.07e-14) rot=(0.983106,-0.129428,0.129428;4.69535rad)
  shape: bbox 39.11 x 29.3 x 14 mm, 30 faces (baked)
FEATURE [App::DocumentObjectGroup] Group  label="Cleanup"
  Group = -> [Part__Feature176,Part__Feature175,Part__Feature174,Part__Feature173,Part__Feature172,Part__Feature171,Part__Feature170,Part__Feature177,Clone011,Part__Feature179]
FEATURE [Part::FeaturePython] Clone  label="Main vertical coupler002"  # Draft clone (typed FeaturePython)
  AttacherType = Attacher::AttachEngine3D
  Fuse = false
  Objects = -> [Body020]
  Placement = pos=(0,0,0) rot=(0,1,0;3.14159rad)
  Scale = (1,1,1)
FEATURE [Part::Feature] Part__Feature180  label="Z-axis Bottom Plate_Z-axis Bottom Plate001"
  Placement = pos=(0,0,0) rot=(1,0,0;1.5708rad)
  shape: bbox 120 x 120 x 10 mm, 43 faces (baked)
FEATURE [Sketcher::SketchObject] Sketch113
  FullyConstrained = true
  MapMode = 5
  Support = -> [XY_Plane038]
  expr: Constraints[17] = <<vert base dims>>.base_smooth_rod_diameter
  expr: Constraints[19] = <<vert base dims>>.bottom_plate_center_hole_diameter
  expr: Constraints[1] = <<vert base dims>>.base_diameter
  expr: Constraints[3] = <<vert base dims>>.base_smooth_rod_set_diameter
  sketch-geometry (9):
    g0: Circle CenterX=0 CenterY=0 CenterZ=0 NormalX=0 NormalY=0 NormalZ=1 AngleXU=0 Radius=60
    g1: Circle CenterX=0 CenterY=0 CenterZ=0 NormalX=0 NormalY=0 NormalZ=1 AngleXU=0 Radius=47.5
    g2: Circle CenterX=-33.5876 CenterY=33.5876 CenterZ=0 NormalX=0 NormalY=0 NormalZ=1 AngleXU=0 Radius=5
    g3: Circle CenterX=33.5876 CenterY=33.5876 CenterZ=0 NormalX=0 NormalY=0 NormalZ=1 AngleXU=0 Radius=5
    g4: Circle CenterX=33.5876 CenterY=-33.5876 CenterZ=0 NormalX=0 NormalY=0 NormalZ=1 AngleXU=0 Radius=5
    g5: Circle CenterX=-33.5876 CenterY=-33.5876 CenterZ=0 NormalX=0 NormalY=0 NormalZ=1 AngleXU=0 Radius=5
    g6: LineSegment StartX=-33.5876 StartY=-33.5876 StartZ=0 EndX=33.5876 EndY=-33.5876 EndZ=0
    g7: LineSegment StartX=33.5876 StartY=-33.5876 StartZ=0 EndX=33.5876 EndY=33.5876 EndZ=0
    g8: Circle CenterX=0 CenterY=0 CenterZ=0 NormalX=0 NormalY=0 NormalZ=1 AngleXU=0 Radius=17.5
  constraints (20):
    c: Coincident(g0,g-1)
    c: Diameter(g0) = 120
    c: Coincident(g1,g0)
    c: Diameter(g1) = 95
    c: PointOnObject(g2,g1)
    c: PointOnObject(g3,g1)
    c: Symmetric(g5,g3,g0)
    c: Symmetric(g4,g2,g0)
    c: Horizontal(g4,g5)
    c: Coincident(g6,g5)
    c: Coincident(g7,g4)
    c: Coincident(g3,g7)
    c: Coincident(g4,g6)
    c: Equal(g7,g6)
    c: Equal(g4,g5)
    c: Equal(g5,g2)
    c: Equal(g2,g3)
    c: Diameter(g5) = 10
    c: Coincident(g8,g0)
    c: Diameter(g8) = 35
FEATURE [PartDesign::Pad] Pad044
  Direction = (0,0,1)
  Length = 10
  Length2 = 10
  Profile = -> Sketch113
  ReferenceAxis = -> Sketch113 [N_Axis]
  Type = 0
  expr: Length = <<vert base dims>>.bottom_plate_thickness
FEATURE [Sketcher::SketchObject] Sketch114
  FullyConstrained = true
  MapMode = 5
  Support = -> [XY_Plane038]
  expr: Constraints[1] = <<vert base dims>>.screwhole_offset
  expr: Constraints[2] = <<vert base dims>>.screwholes
  sketch-geometry (1):
    g0: Circle CenterX=49.5 CenterY=0 CenterZ=0 NormalX=0 NormalY=0 NormalZ=1 AngleXU=0 Radius=2.05
  constraints (3):
    c: PointOnObject(g0,g-1)
    c: DistanceX(g-1,g0) = 49.5
    c: Diameter(g0) = 4.1
FEATURE [PartDesign::Pocket] Pocket075
  BaseFeature = -> Pad044
  Direction = (0,0,-1)
  Length = 5
  Length2 = 5
  Profile = -> Sketch114
  ReferenceAxis = -> Sketch114 [N_Axis]
  Reversed = true
  Type = 1
FEATURE [PartDesign::PolarPattern] PolarPattern008
  Angle = 360
  Axis = -> Sketch114 [N_Axis]
  BaseFeature = -> Pocket075
  Occurrences = 12
  Originals = -> [Pocket075]
  Overlap = 0
FEATURE [Sketcher::SketchObject] Sketch115
  AttachmentOffset = pos=(0,0,10) rot=(0,0,1;0rad)
  FullyConstrained = true
  MapMode = 5
  Placement = pos=(0,0,10) rot=(0,0,1;0rad)
  Support = -> [XY_Plane038]
  expr: .AttachmentOffset.Base.z = <<vert base dims>>.bottom_plate_thickness
  expr: Constraints[0] = <<vert base dims>>.lead_screw_bearing_offset
  expr: Constraints[2] = <<vert base dims>>.lead_screw_bearing_diameter
  sketch-geometry (1):
    g0: Circle CenterX=0 CenterY=-33 CenterZ=0 NormalX=0 NormalY=0 NormalZ=1 AngleXU=0 Radius=11
  constraints (3):
    c: DistanceY(g0,g-1) = 33
    c: Vertical(g0,g-1)
    c: Diameter(g0) = 22
FEATURE [PartDesign::Pocket] Pocket076
  BaseFeature = -> PolarPattern008
  Direction = (0,0,-1)
  Length = 7
  Length2 = 5
  Profile = -> Sketch115
  ReferenceAxis = -> Sketch115 [N_Axis]
  Type = 0
  expr: Length = <<vert base dims>>.lead_screw_bearing_thickness
FEATURE [Sketcher::SketchObject] Sketch116
  AttachmentOffset = pos=(0,0,10) rot=(0,0,1;0rad)
  FullyConstrained = true
  MapMode = 5
  Placement = pos=(0,0,10) rot=(0,0,1;0rad)
  Support = -> [XY_Plane038]
  expr: .AttachmentOffset.Base.z = <<vert base dims>>.bottom_plate_thickness
  expr: Constraints[0] = <<vert base dims>>.lead_screw_bearing_offset
  expr: Constraints[2] = <<vert base dims>>.lead_screw_bearing_hole
  sketch-geometry (1):
    g0: Circle CenterX=0 CenterY=-33 CenterZ=0 NormalX=0 NormalY=0 NormalZ=1 AngleXU=0 Radius=7.5
  constraints (3):
    c: DistanceY(g0,g-1) = 33
    c: Vertical(g0,g-1)
    c: Diameter(g0) = 15
FEATURE [PartDesign::Pocket] Pocket077
  BaseFeature = -> Pocket076
  Direction = (0,0,-1)
  Length = 5
  Length2 = 5
  Profile = -> Sketch116
  ReferenceAxis = -> Sketch116 [N_Axis]
  Type = 1
FEATURE [Part::Part2DObjectPython] ShapeString020  # Draft 2D object (typed FeaturePython)
  AttachmentOffset = pos=(-7,29,10) rot=(0,0,1;0rad)
  FontFile = <path>
  MakeFace = true
  MapMode = 5
  Placement = pos=(-7,29,10) rot=(0,0,1;0rad)
  Size = 5
  String = v1.0
  Support = -> [XY_Plane038]
  Tracking = 0
  expr: .AttachmentOffset.Base.z = <<vert base dims>>.bottom_plate_thickness
  expr: Size = <<global settings>>.label_font_size
FEATURE [PartDesign::Pocket] Pocket078
  BaseFeature = -> Pocket077
  Direction = (0,0,-1)
  Length = 0.4
  Length2 = 5
  Profile = -> ShapeString020
  ReferenceAxis = -> ShapeString020 [N_Axis]
  Type = 0
  expr: Length = <<global settings>>.label_text_depth
FEATURE [PartDesign::Body] Body021  label="Main vertical bottom plate"
  Group = -> [Sketch113,Pad044,Sketch114,Pocket075,PolarPattern008,Sketch115,Pocket076,Sketch116,Pocket077,ShapeString020,Pocket078]
  Origin = -> Origin038
  Tip = -> Pocket078
FEATURE [App::Part] Part009  label="Main vertical base"
  Group = -> [Spreadsheet005,Body020,Part013,Clone,Body021]
  Origin = -> Origin025
note: 7 file-system paths scrubbed to <path> (originals preserved in the JSON sidecar)
